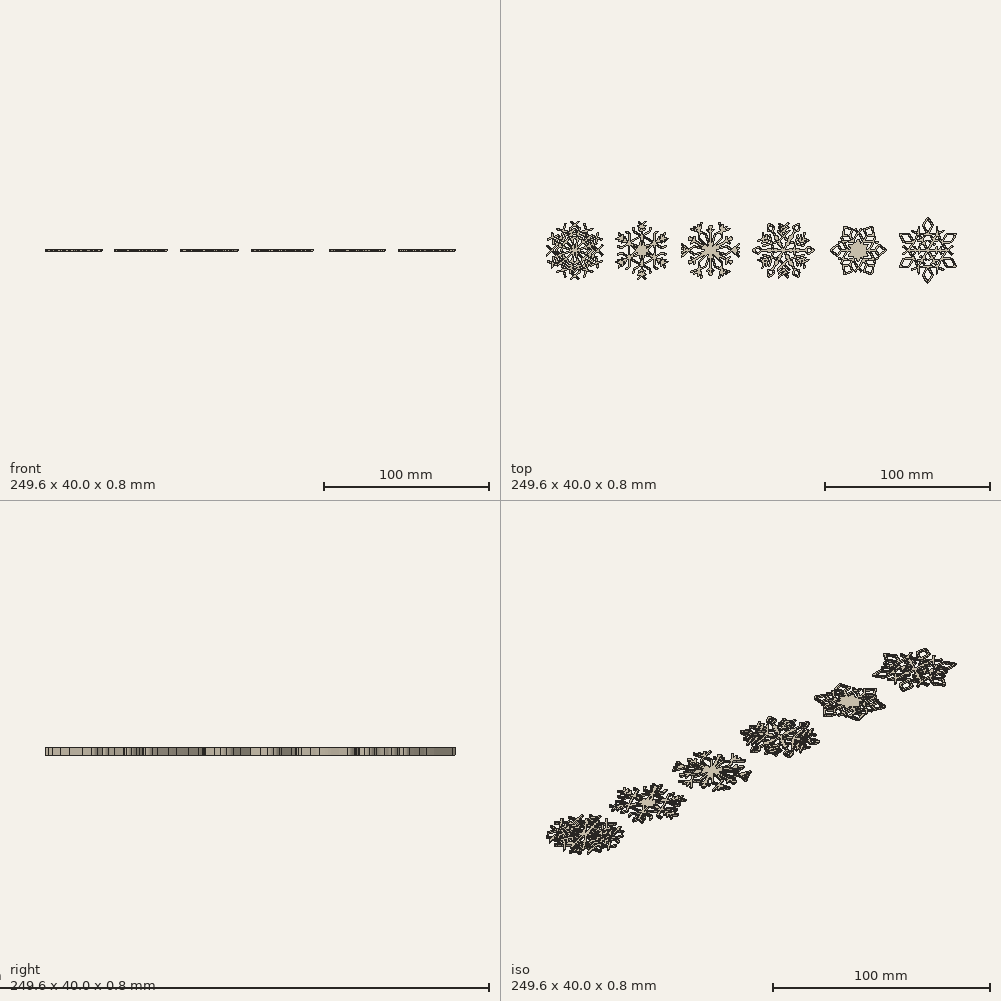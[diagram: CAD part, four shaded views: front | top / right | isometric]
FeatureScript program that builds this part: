
annotation { "Feature Type Name" : "Feature", "Feature Type Description" : "" }
export const myFeature = defineFeature(function(context is Context, id is Id, definition is map)
    precondition{}
    {
        {
            var Q0;
            Q0=qCreatedBy(makeId("Top.planeOp"),FACE);
            var sketch = newSketch(context, id + "F0", { "sketchPlane" : qUnion([Q0])});
            skFitSpline(sketch, "E0", {"points": [v(8.88, -6.2) * mm, v(8.55, -6.04) * mm, v(8.27, -5.88) * mm, v(7.95, -5.8) * mm]});
            skFitSpline(sketch, "E1", {"points": [v(7.95, -5.8) * mm, v(7.92, -6.14) * mm, v(7.88, -6.46) * mm, v(7.85, -6.78) * mm]});
            skFitSpline(sketch, "E2", {"points": [v(7.85, -6.78) * mm, v(8.16, -6.92) * mm, v(8.46, -7.06) * mm, v(8.79, -7.2) * mm]});
            skFitSpline(sketch, "E3", {"points": [v(8.79, -7.2) * mm, v(8.82, -6.86) * mm, v(8.85, -6.53) * mm, v(8.88, -6.2) * mm]});
            skFitSpline(sketch, "E4", {"points": [v(20.42, 12.96) * mm, v(20.13, 13.17) * mm, v(19.86, 13.36) * mm, v(19.6, 13.55) * mm]});
            skFitSpline(sketch, "E5", {"points": [v(19.6, 13.55) * mm, v(19.32, 13.36) * mm, v(19.06, 13.17) * mm, v(18.77, 12.96) * mm]});
            skFitSpline(sketch, "E6", {"points": [v(18.77, 12.96) * mm, v(19.05, 12.76) * mm, v(19.32, 12.56) * mm, v(19.6, 12.36) * mm]});
            skFitSpline(sketch, "E7", {"points": [v(19.6, 12.36) * mm, v(19.88, 12.57) * mm, v(20.14, 12.76) * mm, v(20.42, 12.96) * mm]});
            skFitSpline(sketch, "E8", {"points": [v(7.85, 6.77) * mm, v(7.88, 6.44) * mm, v(7.92, 6.12) * mm, v(7.96, 5.76) * mm]});
            skFitSpline(sketch, "E9", {"points": [v(7.96, 5.76) * mm, v(8.27, 5.9) * mm, v(8.57, 6.04) * mm, v(8.87, 6.17) * mm]});
            skFitSpline(sketch, "E10", {"points": [v(8.87, 6.17) * mm, v(8.87, 6.53) * mm, v(8.83, 6.86) * mm, v(8.77, 7.19) * mm]});
            skFitSpline(sketch, "E11", {"points": [v(8.77, 7.19) * mm, v(8.45, 7.04) * mm, v(8.16, 6.91) * mm, v(7.85, 6.77) * mm]});
            skFitSpline(sketch, "E12", {"points": [v(30.4, 7.2) * mm, v(30.37, 6.85) * mm, v(30.34, 6.52) * mm, v(30.3, 6.18) * mm]});
            skFitSpline(sketch, "E13", {"points": [v(30.3, 6.18) * mm, v(30.62, 6.04) * mm, v(30.92, 5.9) * mm, v(31.24, 5.76) * mm]});
            skFitSpline(sketch, "E14", {"points": [v(31.24, 5.76) * mm, v(31.27, 6.12) * mm, v(31.3, 6.45) * mm, v(31.33, 6.78) * mm]});
            skFitSpline(sketch, "E15", {"points": [v(31.33, 6.78) * mm, v(31.02, 6.92) * mm, v(30.73, 7.05) * mm, v(30.4, 7.2) * mm]});
            skFitSpline(sketch, "E16", {"points": [v(19.6, -13.56) * mm, v(19.88, -13.36) * mm, v(20.14, -13.17) * mm, v(20.42, -12.97) * mm]});
            skFitSpline(sketch, "E17", {"points": [v(20.42, -12.97) * mm, v(20.14, -12.77) * mm, v(19.87, -12.57) * mm, v(19.6, -12.37) * mm]});
            skFitSpline(sketch, "E18", {"points": [v(19.6, -12.37) * mm, v(19.3, -12.58) * mm, v(19.04, -12.77) * mm, v(18.77, -12.97) * mm]});
            skFitSpline(sketch, "E19", {"points": [v(18.77, -12.97) * mm, v(19.05, -13.17) * mm, v(19.32, -13.36) * mm, v(19.6, -13.56) * mm]});
            skFitSpline(sketch, "E20", {"points": [v(30.3, -6.19) * mm, v(30.34, -6.53) * mm, v(30.37, -6.86) * mm, v(30.4, -7.2) * mm]});
            skFitSpline(sketch, "E21", {"points": [v(30.4, -7.2) * mm, v(30.72, -7.06) * mm, v(31.03, -6.92) * mm, v(31.33, -6.78) * mm]});
            skFitSpline(sketch, "E22", {"points": [v(31.33, -6.78) * mm, v(31.3, -6.44) * mm, v(31.27, -6.12) * mm, v(31.24, -5.77) * mm]});
            skFitSpline(sketch, "E23", {"points": [v(31.24, -5.77) * mm, v(30.92, -5.91) * mm, v(30.62, -6.05) * mm, v(30.3, -6.19) * mm]});
            skFitSpline(sketch, "E24", {"points": [v(20.74, 10.31) * mm, v(20.41, 10.61) * mm, v(19.97, 10.81) * mm, v(19.6, 11.12) * mm]});
            skFitSpline(sketch, "E25", {"points": [v(19.6, 11.12) * mm, v(19.21, 10.8) * mm, v(18.76, 10.62) * mm, v(18.4, 10.26) * mm]});
            skFitSpline(sketch, "E26", {"points": [v(18.4, 10.26) * mm, v(18.8, 9.87) * mm, v(19.2, 9.49) * mm, v(19.61, 9.08) * mm]});
            skFitSpline(sketch, "E27", {"points": [v(19.61, 9.08) * mm, v(20, 9.5) * mm, v(20.36, 9.9) * mm, v(20.74, 10.31) * mm]});
            skFitSpline(sketch, "E28", {"points": [v(20.78, -10.27) * mm, v(20.38, -9.88) * mm, v(20, -9.48) * mm, v(19.56, -9.1) * mm]});
            skFitSpline(sketch, "E29", {"points": [v(19.56, -9.1) * mm, v(19.18, -9.5) * mm, v(18.82, -9.9) * mm, v(18.44, -10.32) * mm]});
            skFitSpline(sketch, "E30", {"points": [v(18.44, -10.32) * mm, v(18.77, -10.62) * mm, v(19.22, -10.82) * mm, v(19.6, -11.13) * mm]});
            skFitSpline(sketch, "E31", {"points": [v(19.6, -11.13) * mm, v(19.97, -10.8) * mm, v(20.43, -10.63) * mm, v(20.78, -10.27) * mm]});
            skFitSpline(sketch, "E32", {"points": [v(11.69, -4.55) * mm, v(11.17, -4.4) * mm, v(10.64, -4.26) * mm, v(10.1, -4.11) * mm]});
            skFitSpline(sketch, "E33", {"points": [v(10.1, -4.11) * mm, v(9.96, -4.61) * mm, v(10.04, -5.1) * mm, v(9.96, -5.57) * mm]});
            skFitSpline(sketch, "E34", {"points": [v(9.96, -5.57) * mm, v(10.43, -5.74) * mm, v(10.81, -6.04) * mm, v(11.3, -6.17) * mm]});
            skFitSpline(sketch, "E35", {"points": [v(11.3, -6.17) * mm, v(11.43, -5.64) * mm, v(11.56, -5.14) * mm, v(11.69, -4.64) * mm]});
            skFitSpline(sketch, "E36", {"points": [v(11.69, -4.64) * mm, v(11.7, -4.62) * mm, v(11.69, -4.6) * mm, v(11.69, -4.55) * mm]});
            skFitSpline(sketch, "E37", {"points": [v(27.9, -6.2) * mm, v(28.36, -5.98) * mm, v(28.78, -5.77) * mm, v(29.22, -5.56) * mm]});
            skFitSpline(sketch, "E38", {"points": [v(29.22, -5.56) * mm, v(29.16, -5.09) * mm, v(29.2, -4.6) * mm, v(29.08, -4.11) * mm]});
            skFitSpline(sketch, "E39", {"points": [v(29.08, -4.11) * mm, v(28.53, -4.26) * mm, v(28.01, -4.4) * mm, v(27.47, -4.55) * mm]});
            skFitSpline(sketch, "E40", {"points": [v(27.47, -4.55) * mm, v(27.61, -5.1) * mm, v(27.75, -5.62) * mm, v(27.9, -6.2) * mm]});
            skFitSpline(sketch, "E41", {"points": [v(27.47, 4.55) * mm, v(28.01, 4.4) * mm, v(28.54, 4.25) * mm, v(29.09, 4.1) * mm]});
            skFitSpline(sketch, "E42", {"points": [v(29.09, 4.1) * mm, v(29.2, 4.6) * mm, v(29.17, 5.09) * mm, v(29.21, 5.55) * mm]});
            skFitSpline(sketch, "E43", {"points": [v(29.21, 5.55) * mm, v(28.98, 5.67) * mm, v(28.77, 5.77) * mm, v(28.56, 5.87) * mm]});
            skFitSpline(sketch, "E44", {"points": [v(28.56, 5.87) * mm, v(28.35, 5.98) * mm, v(28.15, 6.11) * mm, v(27.9, 6.15) * mm]});
            skFitSpline(sketch, "E45", {"points": [v(27.9, 6.15) * mm, v(27.75, 5.62) * mm, v(27.62, 5.1) * mm, v(27.47, 4.55) * mm]});
            skFitSpline(sketch, "E46", {"points": [v(9.96, 5.54) * mm, v(10.05, 5.08) * mm, v(9.95, 4.58) * mm, v(10.12, 4.1) * mm]});
            skFitSpline(sketch, "E47", {"points": [v(10.12, 4.1) * mm, v(10.66, 4.25) * mm, v(11.18, 4.4) * mm, v(11.72, 4.55) * mm]});
            skFitSpline(sketch, "E48", {"points": [v(11.72, 4.55) * mm, v(11.57, 5.1) * mm, v(11.43, 5.63) * mm, v(11.3, 6.16) * mm]});
            skFitSpline(sketch, "E49", {"points": [v(11.3, 6.16) * mm, v(11.18, 6.12) * mm, v(11.09, 6.1) * mm, v(11.01, 6.07) * mm]});
            skFitSpline(sketch, "E50", {"points": [v(11.01, 6.07) * mm, v(10.67, 5.9) * mm, v(10.33, 5.72) * mm, v(9.96, 5.54) * mm]});
            skFitSpline(sketch, "E51", {"points": [v(37.3, 0) * mm, v(36.53, 0.5) * mm, v(35.83, 1.07) * mm, v(34.95, 1.36) * mm]});
            skFitSpline(sketch, "E52", {"points": [v(34.95, 1.36) * mm, v(34.4, 1) * mm, v(34.06, 0.44) * mm, v(33.57, 0) * mm]});
            skFitSpline(sketch, "E53", {"points": [v(33.57, 0) * mm, v(34.06, -0.45) * mm, v(34.4, -1.02) * mm, v(34.96, -1.36) * mm]});
            skFitSpline(sketch, "E54", {"points": [v(34.96, -1.36) * mm, v(35.83, -1.07) * mm, v(36.53, -0.5) * mm, v(37.3, 0) * mm]});
            skFitSpline(sketch, "E55", {"points": [v(5.62, 0) * mm, v(5.12, 0.45) * mm, v(4.78, 1) * mm, v(4.23, 1.36) * mm]});
            skFitSpline(sketch, "E56", {"points": [v(4.23, 1.36) * mm, v(3.36, 1.06) * mm, v(2.66, 0.5) * mm, v(1.89, 0) * mm]});
            skFitSpline(sketch, "E57", {"points": [v(1.89, 0) * mm, v(2.67, -0.5) * mm, v(3.37, -1.08) * mm, v(4.24, -1.36) * mm]});
            skFitSpline(sketch, "E58", {"points": [v(4.24, -1.36) * mm, v(4.78, -1) * mm, v(5.13, -0.45) * mm, v(5.62, 0) * mm]});
            skFitSpline(sketch, "E59", {"points": [v(26.58, -12.11) * mm, v(26.44, -12.75) * mm, v(26.13, -13.33) * mm, v(26.1, -13.99) * mm]});
            skFitSpline(sketch, "E60", {"points": [v(26.1, -13.99) * mm, v(26.78, -14.6) * mm, v(27.62, -14.92) * mm, v(28.45, -15.34) * mm]});
            skFitSpline(sketch, "E61", {"points": [v(28.45, -15.34) * mm, v(28.5, -14.4) * mm, v(28.64, -13.52) * mm, v(28.45, -12.63) * mm]});
            skFitSpline(sketch, "E62", {"points": [v(28.45, -12.63) * mm, v(27.87, -12.33) * mm, v(27.2, -12.3) * mm, v(26.58, -12.11) * mm]});
            skFitSpline(sketch, "E63", {"points": [v(12.58, 12.12) * mm, v(12.75, 12.4) * mm, v(13.1, 13.71) * mm, v(13.07, 14) * mm]});
            skFitSpline(sketch, "E64", {"points": [v(13.07, 14) * mm, v(12.39, 14.6) * mm, v(11.56, 14.92) * mm, v(10.73, 15.33) * mm]});
            skFitSpline(sketch, "E65", {"points": [v(10.73, 15.33) * mm, v(10.7, 14.4) * mm, v(10.53, 13.5) * mm, v(10.75, 12.58) * mm]});
            skFitSpline(sketch, "E66", {"points": [v(10.75, 12.58) * mm, v(11.04, 12.5) * mm, v(11.34, 12.4) * mm, v(11.64, 12.33) * mm]});
            skFitSpline(sketch, "E67", {"points": [v(11.64, 12.33) * mm, v(11.95, 12.25) * mm, v(12.26, 12.2) * mm, v(12.58, 12.12) * mm]});
            skFitSpline(sketch, "E68", {"points": [v(13.1, -13.98) * mm, v(13.05, -13.33) * mm, v(12.75, -12.74) * mm, v(12.6, -12.1) * mm]});
            skFitSpline(sketch, "E69", {"points": [v(12.6, -12.1) * mm, v(11.97, -12.31) * mm, v(11.32, -12.33) * mm, v(10.73, -12.63) * mm]});
            skFitSpline(sketch, "E70", {"points": [v(10.73, -12.63) * mm, v(10.54, -13.52) * mm, v(10.7, -14.4) * mm, v(10.73, -15.34) * mm]});
            skFitSpline(sketch, "E71", {"points": [v(10.73, -15.34) * mm, v(11.56, -14.92) * mm, v(12.4, -14.6) * mm, v(13.1, -13.98) * mm]});
            skFitSpline(sketch, "E72", {"points": [v(26.58, 12.11) * mm, v(27.78, 12.36) * mm, v(28.2, 12.48) * mm, v(28.48, 12.65) * mm]});
            skFitSpline(sketch, "E73", {"points": [v(28.48, 12.65) * mm, v(28.5, 12.94) * mm, v(28.53, 13.24) * mm, v(28.54, 13.55) * mm]});
            skFitSpline(sketch, "E74", {"points": [v(28.54, 13.55) * mm, v(28.55, 13.84) * mm, v(28.55, 14.13) * mm, v(28.52, 14.42) * mm]});
            skFitSpline(sketch, "E75", {"points": [v(28.52, 14.42) * mm, v(28.48, 14.71) * mm, v(28.51, 15.02) * mm, v(28.43, 15.32) * mm]});
            skFitSpline(sketch, "E76", {"points": [v(28.43, 15.32) * mm, v(27.6, 14.9) * mm, v(26.77, 14.58) * mm, v(26.1, 13.97) * mm]});
            skFitSpline(sketch, "E77", {"points": [v(26.1, 13.97) * mm, v(26.13, 13.32) * mm, v(26.44, 12.74) * mm, v(26.58, 12.11) * mm]});
            skFitSpline(sketch, "E78", {"points": [v(22.07, -5.29) * mm, v(22.06, -5.27) * mm, v(22.05, -5.25) * mm, v(22.03, -5.24) * mm]});
            skFitSpline(sketch, "E79", {"points": [v(22.03, -5.24) * mm, v(21.97, -5.24) * mm, v(21.9, -5.24) * mm, v(21.85, -5.23) * mm]});
            skFitSpline(sketch, "E80", {"points": [v(21.85, -5.23) * mm, v(21.62, -5.22) * mm, v(21.41, -5.13) * mm, v(21.25, -4.97) * mm]});
            skFitSpline(sketch, "E81", {"points": [v(21.25, -4.97) * mm, v(21.15, -4.88) * mm, v(21.06, -4.78) * mm, v(20.97, -4.68) * mm]});
            skFitSpline(sketch, "E82", {"points": [v(20.97, -4.68) * mm, v(20.65, -4.33) * mm, v(20.52, -3.94) * mm, v(20.72, -3.49) * mm]});
            skFitSpline(sketch, "E83", {"points": [v(20.72, -3.49) * mm, v(20.76, -3.4) * mm, v(20.82, -3.3) * mm, v(20.86, -3.23) * mm]});
            skFitSpline(sketch, "E84", {"points": [v(20.86, -3.23) * mm, v(20.44, -2.49) * mm, v(20.03, -1.76) * mm, v(19.6, -1) * mm]});
            skFitSpline(sketch, "E85", {"points": [v(19.6, -1) * mm, v(19.15, -1.77) * mm, v(18.74, -2.5) * mm, v(18.33, -3.24) * mm]});
            skFitSpline(sketch, "E86", {"points": [v(18.33, -3.24) * mm, v(18.72, -3.84) * mm, v(18.57, -4.35) * mm, v(18.14, -4.75) * mm]});
            skFitSpline(sketch, "E87", {"points": [v(18.14, -4.75) * mm, v(18.1, -4.78) * mm, v(18.07, -4.81) * mm, v(18.04, -4.85) * mm]});
            skFitSpline(sketch, "E88", {"points": [v(18.04, -4.85) * mm, v(17.84, -5.13) * mm, v(17.57, -5.24) * mm, v(17.23, -5.24) * mm]});
            skFitSpline(sketch, "E89", {"points": [v(17.23, -5.24) * mm, v(17.2, -5.24) * mm, v(17.16, -5.27) * mm, v(17.12, -5.29) * mm]});
            skFitSpline(sketch, "E90", {"points": [v(17.12, -5.29) * mm, v(17.27, -5.52) * mm, v(19.42, -7.61) * mm, v(19.62, -7.73) * mm]});
            skFitSpline(sketch, "E91", {"points": [v(19.62, -7.73) * mm, v(19.7, -7.65) * mm, v(19.8, -7.57) * mm, v(19.9, -7.48) * mm]});
            skFitSpline(sketch, "E92", {"points": [v(19.9, -7.48) * mm, v(20.06, -7.32) * mm, v(20.2, -7.14) * mm, v(20.37, -6.98) * mm]});
            skFitSpline(sketch, "E93", {"points": [v(20.37, -6.98) * mm, v(20.9, -6.46) * mm, v(21.44, -5.95) * mm, v(21.97, -5.43) * mm]});
            skFitSpline(sketch, "E94", {"points": [v(21.97, -5.43) * mm, v(22.01, -5.4) * mm, v(22.04, -5.33) * mm, v(22.07, -5.29) * mm]});
            skFitSpline(sketch, "E95", {"points": [v(22.05, 5.26) * mm, v(22.09, 5.33) * mm, v(22.02, 5.38) * mm, v(21.97, 5.43) * mm]});
            skFitSpline(sketch, "E96", {"points": [v(21.97, 5.43) * mm, v(21.55, 5.83) * mm, v(21.13, 6.24) * mm, v(20.72, 6.65) * mm]});
            skFitSpline(sketch, "E97", {"points": [v(20.72, 6.65) * mm, v(20.5, 6.85) * mm, v(20.3, 7.07) * mm, v(20.1, 7.27) * mm]});
            skFitSpline(sketch, "E98", {"points": [v(20.1, 7.27) * mm, v(19.93, 7.43) * mm, v(19.8, 7.61) * mm, v(19.57, 7.72) * mm]});
            skFitSpline(sketch, "E99", {"points": [v(19.57, 7.72) * mm, v(19.48, 7.64) * mm, v(19.38, 7.57) * mm, v(19.3, 7.47) * mm]});
            skFitSpline(sketch, "E100", {"points": [v(19.3, 7.47) * mm, v(18.95, 7.1) * mm, v(18.59, 6.76) * mm, v(18.22, 6.42) * mm]});
            skFitSpline(sketch, "E101", {"points": [v(18.22, 6.42) * mm, v(17.87, 6.1) * mm, v(17.54, 5.75) * mm, v(17.21, 5.42) * mm]});
            skFitSpline(sketch, "E102", {"points": [v(17.21, 5.42) * mm, v(17.18, 5.38) * mm, v(17.16, 5.31) * mm, v(17.14, 5.26) * mm]});
            skFitSpline(sketch, "E103", {"points": [v(17.14, 5.26) * mm, v(17.19, 5.25) * mm, v(17.24, 5.22) * mm, v(17.29, 5.22) * mm]});
            skFitSpline(sketch, "E104", {"points": [v(17.29, 5.22) * mm, v(17.59, 5.22) * mm, v(17.83, 5.11) * mm, v(18.02, 4.88) * mm]});
            skFitSpline(sketch, "E105", {"points": [v(18.02, 4.88) * mm, v(18.06, 4.81) * mm, v(18.13, 4.76) * mm, v(18.18, 4.7) * mm]});
            skFitSpline(sketch, "E106", {"points": [v(18.18, 4.7) * mm, v(18.55, 4.36) * mm, v(18.65, 3.9) * mm, v(18.46, 3.46) * mm]});
            skFitSpline(sketch, "E107", {"points": [v(18.46, 3.46) * mm, v(18.42, 3.38) * mm, v(18.37, 3.3) * mm, v(18.33, 3.22) * mm]});
            skFitSpline(sketch, "E108", {"points": [v(18.33, 3.22) * mm, v(18.75, 2.48) * mm, v(19.16, 1.76) * mm, v(19.6, 0.99) * mm]});
            skFitSpline(sketch, "E109", {"points": [v(19.6, 0.99) * mm, v(20.03, 1.76) * mm, v(20.45, 2.5) * mm, v(20.86, 3.23) * mm]});
            skFitSpline(sketch, "E110", {"points": [v(20.86, 3.23) * mm, v(20.83, 3.29) * mm, v(20.8, 3.33) * mm, v(20.77, 3.38) * mm]});
            skFitSpline(sketch, "E111", {"points": [v(20.77, 3.38) * mm, v(20.68, 3.6) * mm, v(20.59, 3.8) * mm, v(20.64, 4.05) * mm]});
            skFitSpline(sketch, "E112", {"points": [v(20.64, 4.05) * mm, v(20.74, 4.51) * mm, v(21.08, 4.8) * mm, v(21.4, 5.09) * mm]});
            skFitSpline(sketch, "E113", {"points": [v(21.4, 5.09) * mm, v(21.42, 5.1) * mm, v(21.45, 5.11) * mm, v(21.47, 5.12) * mm]});
            skFitSpline(sketch, "E114", {"points": [v(21.47, 5.12) * mm, v(21.65, 5.16) * mm, v(21.83, 5.2) * mm, v(22.05, 5.26) * mm]});
            skLineSegment(sketch, "E115", {"start": v(23.02, -0.51) * mm, "end": v(20.46, -0.51) * mm});
            skFitSpline(sketch, "E116", {"points": [v(20.46, -0.51) * mm, v(20.9, -1.27) * mm, v(21.34, -2) * mm, v(21.76, -2.72) * mm]});
            skFitSpline(sketch, "E117", {"points": [v(21.76, -2.72) * mm, v(21.8, -2.72) * mm, v(21.8, -2.72) * mm, v(21.82, -2.72) * mm]});
            skFitSpline(sketch, "E118", {"points": [v(21.82, -2.72) * mm, v(22.47, -2.68) * mm, v(22.86, -3.07) * mm, v(22.97, -3.64) * mm]});
            skFitSpline(sketch, "E119", {"points": [v(22.97, -3.64) * mm, v(22.98, -3.7) * mm, v(23, -3.74) * mm, v(23.02, -3.8) * mm]});
            skFitSpline(sketch, "E120", {"points": [v(23.02, -3.8) * mm, v(23.15, -4.09) * mm, v(23.1, -4.37) * mm, v(22.96, -4.64) * mm]});
            skFitSpline(sketch, "E121", {"points": [v(22.96, -4.64) * mm, v(22.93, -4.68) * mm, v(22.93, -4.72) * mm, v(22.92, -4.77) * mm]});
            skFitSpline(sketch, "E122", {"points": [v(22.92, -4.77) * mm, v(23.15, -4.8) * mm, v(26.04, -4) * mm, v(26.3, -3.84) * mm]});
            skFitSpline(sketch, "E123", {"points": [v(26.3, -3.84) * mm, v(26.27, -3.72) * mm, v(26.25, -3.6) * mm, v(26.22, -3.48) * mm]});
            skFitSpline(sketch, "E124", {"points": [v(26.22, -3.48) * mm, v(26.12, -3.1) * mm, v(26.02, -2.74) * mm, v(25.92, -2.37) * mm]});
            skFitSpline(sketch, "E125", {"points": [v(25.92, -2.37) * mm, v(25.77, -1.8) * mm, v(25.63, -1.24) * mm, v(25.49, -0.68) * mm]});
            skFitSpline(sketch, "E126", {"points": [v(25.49, -0.68) * mm, v(25.47, -0.62) * mm, v(25.44, -0.57) * mm, v(25.43, -0.52) * mm]});
            skFitSpline(sketch, "E127", {"points": [v(25.43, -0.52) * mm, v(25.3, -0.5) * mm, v(25.3, -0.59) * mm, v(25.26, -0.64) * mm]});
            skFitSpline(sketch, "E128", {"points": [v(25.26, -0.64) * mm, v(25.13, -0.86) * mm, v(24.94, -1) * mm, v(24.7, -1.06) * mm]});
            skFitSpline(sketch, "E129", {"points": [v(24.7, -1.06) * mm, v(24.57, -1.1) * mm, v(24.44, -1.13) * mm, v(24.3, -1.16) * mm]});
            skFitSpline(sketch, "E130", {"points": [v(24.3, -1.16) * mm, v(23.86, -1.23) * mm, v(23.46, -1.17) * mm, v(23.18, -0.77) * mm]});
            skFitSpline(sketch, "E131", {"points": [v(23.18, -0.77) * mm, v(23.12, -0.7) * mm, v(23.08, -0.6) * mm, v(23.02, -0.51) * mm]});
            skFitSpline(sketch, "E132", {"points": [v(16.18, 0.5) * mm, v(17.01, 0.54) * mm, v(17.85, 0.44) * mm, v(18.72, 0.52) * mm]});
            skFitSpline(sketch, "E133", {"points": [v(18.72, 0.52) * mm, v(18.28, 1.26) * mm, v(17.86, 1.98) * mm, v(17.43, 2.7) * mm]});
            skFitSpline(sketch, "E134", {"points": [v(17.43, 2.7) * mm, v(17.37, 2.7) * mm, v(17.3, 2.7) * mm, v(17.25, 2.7) * mm]});
            skFitSpline(sketch, "E135", {"points": [v(17.25, 2.7) * mm, v(16.91, 2.73) * mm, v(16.62, 2.84) * mm, v(16.43, 3.13) * mm]});
            skFitSpline(sketch, "E136", {"points": [v(16.43, 3.13) * mm, v(16.22, 3.43) * mm, v(16.14, 3.78) * mm, v(16.1, 4.14) * mm]});
            skFitSpline(sketch, "E137", {"points": [v(16.1, 4.14) * mm, v(16.08, 4.31) * mm, v(16.13, 4.48) * mm, v(16.24, 4.63) * mm]});
            skFitSpline(sketch, "E138", {"points": [v(16.24, 4.63) * mm, v(16.26, 4.66) * mm, v(16.27, 4.7) * mm, v(16.3, 4.78) * mm]});
            skFitSpline(sketch, "E139", {"points": [v(16.3, 4.78) * mm, v(16.2, 4.77) * mm, v(16.13, 4.78) * mm, v(16.07, 4.76) * mm]});
            skFitSpline(sketch, "E140", {"points": [v(16.07, 4.76) * mm, v(15.54, 4.62) * mm, v(15, 4.47) * mm, v(14.48, 4.32) * mm]});
            skFitSpline(sketch, "E141", {"points": [v(14.48, 4.32) * mm, v(14.16, 4.23) * mm, v(13.83, 4.14) * mm, v(13.51, 4.06) * mm]});
            skFitSpline(sketch, "E142", {"points": [v(13.51, 4.06) * mm, v(13.3, 4) * mm, v(13.09, 3.98) * mm, v(12.89, 3.84) * mm]});
            skFitSpline(sketch, "E143", {"points": [v(12.89, 3.84) * mm, v(12.92, 3.72) * mm, v(12.93, 3.6) * mm, v(12.97, 3.47) * mm]});
            skFitSpline(sketch, "E144", {"points": [v(12.97, 3.47) * mm, v(13.03, 3.27) * mm, v(13.1, 3.06) * mm, v(13.16, 2.86) * mm]});
            skFitSpline(sketch, "E145", {"points": [v(13.16, 2.86) * mm, v(13.35, 2.12) * mm, v(13.52, 1.39) * mm, v(13.7, 0.65) * mm]});
            skFitSpline(sketch, "E146", {"points": [v(13.7, 0.65) * mm, v(13.72, 0.6) * mm, v(13.75, 0.55) * mm, v(13.8, 0.46) * mm]});
            skFitSpline(sketch, "E147", {"points": [v(13.8, 0.46) * mm, v(13.85, 0.53) * mm, v(13.89, 0.57) * mm, v(13.91, 0.61) * mm]});
            skFitSpline(sketch, "E148", {"points": [v(13.91, 0.61) * mm, v(14.06, 0.86) * mm, v(14.27, 1.01) * mm, v(14.56, 1.06) * mm]});
            skFitSpline(sketch, "E149", {"points": [v(14.56, 1.06) * mm, v(14.66, 1.08) * mm, v(14.76, 1.12) * mm, v(14.86, 1.14) * mm]});
            skFitSpline(sketch, "E150", {"points": [v(14.86, 1.14) * mm, v(15.31, 1.23) * mm, v(15.72, 1.17) * mm, v(16, 0.76) * mm]});
            skFitSpline(sketch, "E151", {"points": [v(16, 0.76) * mm, v(16.06, 0.69) * mm, v(16.1, 0.6) * mm, v(16.18, 0.5) * mm]});
            skFitSpline(sketch, "E152", {"points": [v(20.46, 0.5) * mm, v(20.82, 0.5) * mm, v(21.14, 0.48) * mm, v(21.46, 0.48) * mm]});
            skFitSpline(sketch, "E153", {"points": [v(21.46, 0.48) * mm, v(21.85, 0.48) * mm, v(22.24, 0.5) * mm, v(22.63, 0.5) * mm]});
            skFitSpline(sketch, "E154", {"points": [v(22.63, 0.5) * mm, v(22.76, 0.5) * mm, v(22.9, 0.5) * mm, v(23.03, 0.5) * mm]});
            skFitSpline(sketch, "E155", {"points": [v(23.03, 0.5) * mm, v(23.05, 0.55) * mm, v(23.06, 0.57) * mm, v(23.08, 0.6) * mm]});
            skFitSpline(sketch, "E156", {"points": [v(23.08, 0.6) * mm, v(23.28, 0.97) * mm, v(23.58, 1.2) * mm, v(24.02, 1.17) * mm]});
            skFitSpline(sketch, "E157", {"points": [v(24.02, 1.17) * mm, v(24.2, 1.16) * mm, v(24.38, 1.1) * mm, v(24.56, 1.08) * mm]});
            skFitSpline(sketch, "E158", {"points": [v(24.56, 1.08) * mm, v(24.9, 1.03) * mm, v(25.14, 0.87) * mm, v(25.3, 0.57) * mm]});
            skFitSpline(sketch, "E159", {"points": [v(25.3, 0.57) * mm, v(25.32, 0.54) * mm, v(25.37, 0.52) * mm, v(25.43, 0.48) * mm]});
            skFitSpline(sketch, "E160", {"points": [v(25.43, 0.48) * mm, v(25.54, 0.88) * mm, v(25.65, 1.25) * mm, v(25.75, 1.62) * mm]});
            skFitSpline(sketch, "E161", {"points": [v(25.75, 1.62) * mm, v(25.9, 2.18) * mm, v(26.04, 2.74) * mm, v(26.18, 3.3) * mm]});
            skFitSpline(sketch, "E162", {"points": [v(26.18, 3.3) * mm, v(26.22, 3.49) * mm, v(26.31, 3.67) * mm, v(26.26, 3.88) * mm]});
            skFitSpline(sketch, "E163", {"points": [v(26.26, 3.88) * mm, v(26.15, 3.92) * mm, v(26.03, 3.97) * mm, v(25.9, 4) * mm]});
            skFitSpline(sketch, "E164", {"points": [v(25.9, 4) * mm, v(25.7, 4.06) * mm, v(25.47, 4.09) * mm, v(25.25, 4.15) * mm]});
            skFitSpline(sketch, "E165", {"points": [v(25.25, 4.15) * mm, v(24.54, 4.35) * mm, v(23.83, 4.56) * mm, v(23.12, 4.76) * mm]});
            skFitSpline(sketch, "E166", {"points": [v(23.12, 4.76) * mm, v(23.06, 4.78) * mm, v(22.99, 4.77) * mm, v(22.93, 4.77) * mm]});
            skFitSpline(sketch, "E167", {"points": [v(22.93, 4.77) * mm, v(22.92, 4.73) * mm, v(22.92, 4.72) * mm, v(22.92, 4.71) * mm]});
            skFitSpline(sketch, "E168", {"points": [v(22.92, 4.71) * mm, v(22.92, 4.7) * mm, v(22.92, 4.68) * mm, v(22.93, 4.67) * mm]});
            skFitSpline(sketch, "E169", {"points": [v(22.93, 4.67) * mm, v(23.12, 4.37) * mm, v(23.16, 4.06) * mm, v(23, 3.74) * mm]});
            skFitSpline(sketch, "E170", {"points": [v(23, 3.74) * mm, v(22.98, 3.7) * mm, v(22.98, 3.63) * mm, v(22.97, 3.58) * mm]});
            skFitSpline(sketch, "E171", {"points": [v(22.97, 3.58) * mm, v(22.85, 3.17) * mm, v(22.64, 2.83) * mm, v(22.18, 2.75) * mm]});
            skFitSpline(sketch, "E172", {"points": [v(22.18, 2.75) * mm, v(22.04, 2.72) * mm, v(21.9, 2.7) * mm, v(21.75, 2.7) * mm]});
            skFitSpline(sketch, "E173", {"points": [v(21.75, 2.7) * mm, v(21.33, 1.98) * mm, v(20.9, 1.26) * mm, v(20.46, 0.5) * mm]});
            skLineSegment(sketch, "E174", {"start": v(18.73, -0.5) * mm, "end": v(16.17, -0.5) * mm});
            skFitSpline(sketch, "E175", {"points": [v(16.17, -0.5) * mm, v(16.14, -0.55) * mm, v(16.13, -0.58) * mm, v(16.1, -0.61) * mm]});
            skFitSpline(sketch, "E176", {"points": [v(16.1, -0.61) * mm, v(15.9, -0.98) * mm, v(15.6, -1.21) * mm, v(15.16, -1.18) * mm]});
            skFitSpline(sketch, "E177", {"points": [v(15.16, -1.18) * mm, v(14.98, -1.16) * mm, v(14.79, -1.11) * mm, v(14.6, -1.08) * mm]});
            skFitSpline(sketch, "E178", {"points": [v(14.6, -1.08) * mm, v(14.29, -1.04) * mm, v(14.06, -0.88) * mm, v(13.9, -0.6) * mm]});
            skFitSpline(sketch, "E179", {"points": [v(13.9, -0.6) * mm, v(13.88, -0.56) * mm, v(13.83, -0.53) * mm, v(13.8, -0.49) * mm]});
            skFitSpline(sketch, "E180", {"points": [v(13.8, -0.49) * mm, v(13.66, -0.73) * mm, v(12.92, -3.6) * mm, v(12.91, -3.88) * mm]});
            skFitSpline(sketch, "E181", {"points": [v(12.91, -3.88) * mm, v(13.02, -3.92) * mm, v(13.14, -3.97) * mm, v(13.26, -4) * mm]});
            skFitSpline(sketch, "E182", {"points": [v(13.26, -4) * mm, v(13.47, -4.06) * mm, v(13.68, -4.09) * mm, v(13.89, -4.15) * mm]});
            skFitSpline(sketch, "E183", {"points": [v(13.89, -4.15) * mm, v(14.3, -4.26) * mm, v(14.7, -4.4) * mm, v(15.1, -4.52) * mm]});
            skFitSpline(sketch, "E184", {"points": [v(15.1, -4.52) * mm, v(15.44, -4.62) * mm, v(15.78, -4.7) * mm, v(16.12, -4.78) * mm]});
            skFitSpline(sketch, "E185", {"points": [v(16.12, -4.78) * mm, v(16.19, -4.8) * mm, v(16.25, -4.81) * mm, v(16.28, -4.72) * mm]});
            skFitSpline(sketch, "E186", {"points": [v(16.28, -4.72) * mm, v(16.27, -4.7) * mm, v(16.26, -4.68) * mm, v(16.25, -4.66) * mm]});
            skFitSpline(sketch, "E187", {"points": [v(16.25, -4.66) * mm, v(16.06, -4.4) * mm, v(16.05, -4.1) * mm, v(16.16, -3.8) * mm]});
            skFitSpline(sketch, "E188", {"points": [v(16.16, -3.8) * mm, v(16.18, -3.74) * mm, v(16.2, -3.68) * mm, v(16.2, -3.61) * mm]});
            skFitSpline(sketch, "E189", {"points": [v(16.2, -3.61) * mm, v(16.34, -3.17) * mm, v(16.56, -2.82) * mm, v(17.05, -2.74) * mm]});
            skFitSpline(sketch, "E190", {"points": [v(17.05, -2.74) * mm, v(17.18, -2.72) * mm, v(17.3, -2.72) * mm, v(17.44, -2.7) * mm]});
            skFitSpline(sketch, "E191", {"points": [v(17.44, -2.7) * mm, v(17.86, -2) * mm, v(18.28, -1.27) * mm, v(18.73, -0.5) * mm]});
            skFitSpline(sketch, "E192", {"points": [v(18.75, -14.17) * mm, v(18.52, -13.96) * mm, v(18.22, -13.85) * mm, v(18.14, -13.5) * mm]});
            skFitSpline(sketch, "E193", {"points": [v(18.14, -13.5) * mm, v(17.98, -13.6) * mm, v(17.84, -13.71) * mm, v(17.7, -13.81) * mm]});
            skFitSpline(sketch, "E194", {"points": [v(17.7, -13.81) * mm, v(17.52, -13.95) * mm, v(17.35, -14.09) * mm, v(17.16, -14.21) * mm]});
            skFitSpline(sketch, "E195", {"points": [v(17.16, -14.21) * mm, v(16.97, -14.34) * mm, v(16.74, -14.33) * mm, v(16.58, -14.2) * mm]});
            skFitSpline(sketch, "E196", {"points": [v(16.58, -14.2) * mm, v(16.32, -14.01) * mm, v(16.32, -13.66) * mm, v(16.58, -13.44) * mm]});
            skFitSpline(sketch, "E197", {"points": [v(16.58, -13.44) * mm, v(16.8, -13.26) * mm, v(17.04, -13.1) * mm, v(17.27, -12.92) * mm]});
            skFitSpline(sketch, "E198", {"points": [v(17.27, -12.92) * mm, v(17.52, -12.73) * mm, v(17.77, -12.53) * mm, v(18.02, -12.33) * mm]});
            skFitSpline(sketch, "E199", {"points": [v(18.02, -12.33) * mm, v(18.27, -12.14) * mm, v(18.51, -11.95) * mm, v(18.77, -11.75) * mm]});
            skFitSpline(sketch, "E200", {"points": [v(18.77, -11.75) * mm, v(18.41, -11.5) * mm, v(18.06, -11.25) * mm, v(17.7, -11) * mm]});
            skFitSpline(sketch, "E201", {"points": [v(17.7, -11) * mm, v(17.54, -11.14) * mm, v(17.37, -11.29) * mm, v(17.21, -11.45) * mm]});
            skFitSpline(sketch, "E202", {"points": [v(17.21, -11.45) * mm, v(16.93, -11.73) * mm, v(16.67, -12) * mm, v(16.4, -12.29) * mm]});
            skFitSpline(sketch, "E203", {"points": [v(16.4, -12.29) * mm, v(16.22, -12.47) * mm, v(16, -12.5) * mm, v(15.79, -12.36) * mm]});
            skFitSpline(sketch, "E204", {"points": [v(15.79, -12.36) * mm, v(15.58, -12.23) * mm, v(15.5, -11.96) * mm, v(15.61, -11.73) * mm]});
            skFitSpline(sketch, "E205", {"points": [v(15.61, -11.73) * mm, v(15.68, -11.61) * mm, v(15.76, -11.5) * mm, v(15.86, -11.4) * mm]});
            skFitSpline(sketch, "E206", {"points": [v(15.86, -11.4) * mm, v(16.8, -10.47) * mm, v(17.76, -9.54) * mm, v(18.72, -8.6) * mm]});
            skFitSpline(sketch, "E207", {"points": [v(18.72, -8.6) * mm, v(18.77, -8.55) * mm, v(18.81, -8.5) * mm, v(18.87, -8.43) * mm]});
            skFitSpline(sketch, "E208", {"points": [v(18.87, -8.43) * mm, v(18.12, -7.69) * mm, v(17.37, -6.95) * mm, v(16.6, -6.2) * mm]});
            skFitSpline(sketch, "E209", {"points": [v(16.6, -6.2) * mm, v(16.49, -6.37) * mm, v(16.39, -6.54) * mm, v(16.3, -6.7) * mm]});
            skFitSpline(sketch, "E210", {"points": [v(16.3, -6.7) * mm, v(16.37, -6.84) * mm, v(16.46, -6.97) * mm, v(16.5, -7.11) * mm]});
            skFitSpline(sketch, "E211", {"points": [v(16.5, -7.11) * mm, v(16.6, -7.58) * mm, v(16.5, -8.03) * mm, v(16.26, -8.44) * mm]});
            skFitSpline(sketch, "E212", {"points": [v(16.26, -8.44) * mm, v(16.16, -8.6) * mm, v(16.06, -8.77) * mm, v(15.88, -8.87) * mm]});
            skFitSpline(sketch, "E213", {"points": [v(15.88, -8.87) * mm, v(15.56, -9.04) * mm, v(15.43, -9.05) * mm, v(15.06, -8.95) * mm]});
            skFitSpline(sketch, "E214", {"points": [v(15.06, -8.95) * mm, v(14.98, -9.08) * mm, v(14.9, -9.21) * mm, v(14.82, -9.35) * mm]});
            skFitSpline(sketch, "E215", {"points": [v(14.82, -9.35) * mm, v(14.49, -9.92) * mm, v(14.16, -10.48) * mm, v(13.83, -11.05) * mm]});
            skFitSpline(sketch, "E216", {"points": [v(13.83, -11.05) * mm, v(13.74, -11.2) * mm, v(13.63, -11.36) * mm, v(13.54, -11.51) * mm]});
            skFitSpline(sketch, "E217", {"points": [v(13.54, -11.51) * mm, v(13.49, -11.6) * mm, v(13.5, -11.67) * mm, v(13.52, -11.76) * mm]});
            skFitSpline(sketch, "E218", {"points": [v(13.52, -11.76) * mm, v(13.67, -12.26) * mm, v(13.83, -12.75) * mm, v(13.96, -13.26) * mm]});
            skFitSpline(sketch, "E219", {"points": [v(13.96, -13.26) * mm, v(14.03, -13.56) * mm, v(14.06, -13.87) * mm, v(14.1, -14.18) * mm]});
            skFitSpline(sketch, "E220", {"points": [v(14.1, -14.18) * mm, v(14.12, -14.39) * mm, v(14.02, -14.54) * mm, v(13.85, -14.67) * mm]});
            skFitSpline(sketch, "E221", {"points": [v(13.85, -14.67) * mm, v(13.24, -15.13) * mm, v(12.6, -15.55) * mm, v(11.9, -15.86) * mm]});
            skFitSpline(sketch, "E222", {"points": [v(11.9, -15.86) * mm, v(11.57, -16.01) * mm, v(11.26, -16.18) * mm, v(10.95, -16.33) * mm]});
            skFitSpline(sketch, "E223", {"points": [v(10.95, -16.33) * mm, v(10.71, -16.45) * mm, v(10.53, -16.43) * mm, v(10.33, -16.27) * mm]});
            skFitSpline(sketch, "E224", {"points": [v(10.33, -16.27) * mm, v(10.27, -16.22) * mm, v(10.2, -16.18) * mm, v(10.13, -16.15) * mm]});
            skFitSpline(sketch, "E225", {"points": [v(10.13, -16.15) * mm, v(9.9, -16.07) * mm, v(9.8, -15.92) * mm, v(9.78, -15.7) * mm]});
            skFitSpline(sketch, "E226", {"points": [v(9.78, -15.7) * mm, v(9.75, -15.14) * mm, v(9.72, -14.6) * mm, v(9.68, -14.04) * mm]});
            skFitSpline(sketch, "E227", {"points": [v(9.68, -14.04) * mm, v(9.65, -13.56) * mm, v(9.7, -13.09) * mm, v(9.74, -12.61) * mm]});
            skFitSpline(sketch, "E228", {"points": [v(9.74, -12.61) * mm, v(9.75, -12.5) * mm, v(9.77, -12.4) * mm, v(9.77, -12.3) * mm]});
            skFitSpline(sketch, "E229", {"points": [v(9.77, -12.3) * mm, v(9.79, -12.1) * mm, v(9.88, -11.95) * mm, v(10.05, -11.85) * mm]});
            skFitSpline(sketch, "E230", {"points": [v(10.05, -11.85) * mm, v(10.16, -11.8) * mm, v(10.28, -11.74) * mm, v(10.4, -11.7) * mm]});
            skFitSpline(sketch, "E231", {"points": [v(10.4, -11.7) * mm, v(10.89, -11.5) * mm, v(11.4, -11.38) * mm, v(11.92, -11.28) * mm]});
            skFitSpline(sketch, "E232", {"points": [v(11.92, -11.28) * mm, v(12.11, -11.25) * mm, v(12.3, -11.2) * mm, v(12.5, -11.13) * mm]});
            skFitSpline(sketch, "E233", {"points": [v(12.5, -11.13) * mm, v(12.56, -11.1) * mm, v(12.62, -11.05) * mm, v(12.66, -11) * mm]});
            skFitSpline(sketch, "E234", {"points": [v(12.66, -11) * mm, v(12.76, -10.81) * mm, v(12.86, -10.62) * mm, v(12.96, -10.43) * mm]});
            skFitSpline(sketch, "E235", {"points": [v(12.96, -10.43) * mm, v(13.33, -9.78) * mm, v(13.7, -9.14) * mm, v(14.07, -8.5) * mm]});
            skFitSpline(sketch, "E236", {"points": [v(14.07, -8.5) * mm, v(14.08, -8.47) * mm, v(14.1, -8.44) * mm, v(14.12, -8.4) * mm]});
            skFitSpline(sketch, "E237", {"points": [v(14.12, -8.4) * mm, v(13.78, -8.18) * mm, v(13.75, -7.84) * mm, v(13.8, -7.5) * mm]});
            skFitSpline(sketch, "E238", {"points": [v(13.8, -7.5) * mm, v(13.85, -7.19) * mm, v(14.02, -6.92) * mm, v(14.26, -6.7) * mm]});
            skFitSpline(sketch, "E239", {"points": [v(14.26, -6.7) * mm, v(14.38, -6.58) * mm, v(14.52, -6.47) * mm, v(14.67, -6.37) * mm]});
            skFitSpline(sketch, "E240", {"points": [v(14.67, -6.37) * mm, v(14.9, -6.21) * mm, v(15.16, -6.2) * mm, v(15.43, -6.23) * mm]});
            skFitSpline(sketch, "E241", {"points": [v(15.43, -6.23) * mm, v(15.53, -6.06) * mm, v(15.63, -5.9) * mm, v(15.73, -5.7) * mm]});
            skFitSpline(sketch, "E242", {"points": [v(15.73, -5.7) * mm, v(15.21, -5.56) * mm, v(14.7, -5.4) * mm, v(14.2, -5.26) * mm]});
            skFitSpline(sketch, "E243", {"points": [v(14.2, -5.26) * mm, v(13.69, -5.12) * mm, v(13.18, -4.99) * mm, v(12.67, -4.85) * mm]});
            skFitSpline(sketch, "E244", {"points": [v(12.67, -4.85) * mm, v(12.64, -4.9) * mm, v(12.62, -4.95) * mm, v(12.6, -5) * mm]});
            skFitSpline(sketch, "E245", {"points": [v(12.6, -5) * mm, v(12.37, -5.89) * mm, v(12.13, -6.78) * mm, v(11.9, -7.67) * mm]});
            skFitSpline(sketch, "E246", {"points": [v(11.9, -7.67) * mm, v(11.8, -8.07) * mm, v(11.7, -8.49) * mm, v(11.6, -8.9) * mm]});
            skFitSpline(sketch, "E247", {"points": [v(11.6, -8.9) * mm, v(11.56, -9.03) * mm, v(11.52, -9.18) * mm, v(11.44, -9.3) * mm]});
            skFitSpline(sketch, "E248", {"points": [v(11.44, -9.3) * mm, v(11.24, -9.62) * mm, v(10.77, -9.61) * mm, v(10.6, -9.28) * mm]});
            skFitSpline(sketch, "E249", {"points": [v(10.6, -9.28) * mm, v(10.53, -9.16) * mm, v(10.52, -9.04) * mm, v(10.56, -8.91) * mm]});
            skFitSpline(sketch, "E250", {"points": [v(10.56, -8.91) * mm, v(10.7, -8.39) * mm, v(10.84, -7.87) * mm, v(10.98, -7.34) * mm]});
            skFitSpline(sketch, "E251", {"points": [v(10.98, -7.34) * mm, v(11, -7.27) * mm, v(11, -7.2) * mm, v(11.02, -7.14) * mm]});
            skFitSpline(sketch, "E252", {"points": [v(11.02, -7.14) * mm, v(10.62, -6.96) * mm, v(10.23, -6.78) * mm, v(9.83, -6.59) * mm]});
            skFitSpline(sketch, "E253", {"points": [v(9.83, -6.59) * mm, v(9.8, -6.87) * mm, v(9.78, -7.13) * mm, v(9.73, -7.38) * mm]});
            skFitSpline(sketch, "E254", {"points": [v(9.73, -7.38) * mm, v(9.6, -8) * mm, v(9.57, -8.63) * mm, v(9.48, -9.25) * mm]});
            skFitSpline(sketch, "E255", {"points": [v(9.48, -9.25) * mm, v(9.47, -9.33) * mm, v(9.45, -9.41) * mm, v(9.42, -9.48) * mm]});
            skFitSpline(sketch, "E256", {"points": [v(9.42, -9.48) * mm, v(9.33, -9.68) * mm, v(9.1, -9.8) * mm, v(8.9, -9.76) * mm]});
            skFitSpline(sketch, "E257", {"points": [v(8.9, -9.76) * mm, v(8.68, -9.7) * mm, v(8.51, -9.53) * mm, v(8.52, -9.3) * mm]});
            skFitSpline(sketch, "E258", {"points": [v(8.52, -9.3) * mm, v(8.53, -9.02) * mm, v(8.57, -8.75) * mm, v(8.6, -8.47) * mm]});
            skFitSpline(sketch, "E259", {"points": [v(8.6, -8.47) * mm, v(8.6, -8.33) * mm, v(8.62, -8.18) * mm, v(8.64, -8.01) * mm]});
            skFitSpline(sketch, "E260", {"points": [v(8.64, -8.01) * mm, v(8.3, -8.11) * mm, v(8.05, -7.92) * mm, v(7.75, -7.82) * mm]});
            skFitSpline(sketch, "E261", {"points": [v(7.75, -7.82) * mm, v(7.72, -8.02) * mm, v(7.69, -8.22) * mm, v(7.67, -8.4) * mm]});
            skFitSpline(sketch, "E262", {"points": [v(7.67, -8.4) * mm, v(7.6, -8.99) * mm, v(7.6, -9.57) * mm, v(7.47, -10.14) * mm]});
            skFitSpline(sketch, "E263", {"points": [v(7.47, -10.14) * mm, v(7.43, -10.29) * mm, v(7.4, -10.44) * mm, v(7.36, -10.58) * mm]});
            skFitSpline(sketch, "E264", {"points": [v(7.36, -10.58) * mm, v(7.27, -10.85) * mm, v(7.02, -11.01) * mm, v(6.8, -10.95) * mm]});
            skFitSpline(sketch, "E265", {"points": [v(6.8, -10.95) * mm, v(6.52, -10.88) * mm, v(6.36, -10.63) * mm, v(6.42, -10.34) * mm]});
            skFitSpline(sketch, "E266", {"points": [v(6.42, -10.34) * mm, v(6.48, -9.98) * mm, v(6.56, -9.62) * mm, v(6.62, -9.26) * mm]});
            skFitSpline(sketch, "E267", {"points": [v(6.62, -9.26) * mm, v(6.66, -9.03) * mm, v(6.66, -8.8) * mm, v(6.68, -8.57) * mm]});
            skFitSpline(sketch, "E268", {"points": [v(6.68, -8.57) * mm, v(6.72, -8.18) * mm, v(6.77, -7.78) * mm, v(6.81, -7.38) * mm]});
            skFitSpline(sketch, "E269", {"points": [v(6.81, -7.38) * mm, v(6.52, -7.26) * mm, v(6.23, -7.14) * mm, v(5.95, -7.01) * mm]});
            skFitSpline(sketch, "E270", {"points": [v(5.95, -7.01) * mm, v(5.55, -6.84) * mm, v(5.15, -6.64) * mm, v(4.75, -6.47) * mm]});
            skFitSpline(sketch, "E271", {"points": [v(4.75, -6.47) * mm, v(4.54, -6.39) * mm, v(4.32, -6.33) * mm, v(4.11, -6.26) * mm]});
            skFitSpline(sketch, "E272", {"points": [v(4.11, -6.26) * mm, v(4.04, -6.24) * mm, v(3.96, -6.2) * mm, v(3.9, -6.16) * mm]});
            skFitSpline(sketch, "E273", {"points": [v(3.9, -6.16) * mm, v(3.72, -6.04) * mm, v(3.66, -5.83) * mm, v(3.72, -5.63) * mm]});
            skFitSpline(sketch, "E274", {"points": [v(3.72, -5.63) * mm, v(3.79, -5.42) * mm, v(3.94, -5.3) * mm, v(4.17, -5.31) * mm]});
            skFitSpline(sketch, "E275", {"points": [v(4.17, -5.31) * mm, v(4.36, -5.33) * mm, v(4.56, -5.37) * mm, v(4.74, -5.44) * mm]});
            skFitSpline(sketch, "E276", {"points": [v(4.74, -5.44) * mm, v(5.12, -5.58) * mm, v(5.5, -5.74) * mm, v(5.87, -5.9) * mm]});
            skFitSpline(sketch, "E277", {"points": [v(5.87, -5.9) * mm, v(6.15, -6.02) * mm, v(6.43, -6.15) * mm, v(6.7, -6.28) * mm]});
            skFitSpline(sketch, "E278", {"points": [v(6.7, -6.28) * mm, v(6.77, -6.3) * mm, v(6.83, -6.32) * mm, v(6.9, -6.35) * mm]});
            skFitSpline(sketch, "E279", {"points": [v(6.9, -6.35) * mm, v(6.98, -6.05) * mm, v(6.92, -5.74) * mm, v(7.2, -5.5) * mm]});
            skFitSpline(sketch, "E280", {"points": [v(7.2, -5.5) * mm, v(7, -5.41) * mm, v(6.84, -5.34) * mm, v(6.68, -5.27) * mm]});
            skFitSpline(sketch, "E281", {"points": [v(6.68, -5.27) * mm, v(6.47, -5.18) * mm, v(6.26, -5.1) * mm, v(6.06, -5) * mm]});
            skFitSpline(sketch, "E282", {"points": [v(6.06, -5) * mm, v(5.78, -4.85) * mm, v(5.7, -4.5) * mm, v(5.88, -4.26) * mm]});
            skFitSpline(sketch, "E283", {"points": [v(5.88, -4.26) * mm, v(6.02, -4.08) * mm, v(6.25, -4.03) * mm, v(6.51, -4.13) * mm]});
            skFitSpline(sketch, "E284", {"points": [v(6.51, -4.13) * mm, v(6.84, -4.26) * mm, v(7.16, -4.4) * mm, v(7.48, -4.54) * mm]});
            skFitSpline(sketch, "E285", {"points": [v(7.48, -4.54) * mm, v(7.62, -4.6) * mm, v(7.76, -4.67) * mm, v(7.9, -4.72) * mm]});
            skFitSpline(sketch, "E286", {"points": [v(7.9, -4.72) * mm, v(8.27, -4.87) * mm, v(8.64, -5) * mm, v(9.02, -5.15) * mm]});
            skFitSpline(sketch, "E287", {"points": [v(9.02, -5.15) * mm, v(9.05, -4.72) * mm, v(9.09, -4.3) * mm, v(9.12, -3.86) * mm]});
            skFitSpline(sketch, "E288", {"points": [v(9.12, -3.86) * mm, v(8.95, -3.8) * mm, v(8.76, -3.74) * mm, v(8.57, -3.68) * mm]});
            skFitSpline(sketch, "E289", {"points": [v(8.57, -3.68) * mm, v(8.25, -3.59) * mm, v(7.93, -3.5) * mm, v(7.6, -3.41) * mm]});
            skFitSpline(sketch, "E290", {"points": [v(7.6, -3.41) * mm, v(7.54, -3.4) * mm, v(7.46, -3.4) * mm, v(7.4, -3.38) * mm]});
            skFitSpline(sketch, "E291", {"points": [v(7.4, -3.38) * mm, v(7.15, -3.34) * mm, v(6.98, -3.13) * mm, v(6.98, -2.9) * mm]});
            skFitSpline(sketch, "E292", {"points": [v(6.98, -2.9) * mm, v(7, -2.65) * mm, v(7.19, -2.45) * mm, v(7.44, -2.43) * mm]});
            skFitSpline(sketch, "E293", {"points": [v(7.44, -2.43) * mm, v(7.71, -2.4) * mm, v(7.96, -2.5) * mm, v(8.21, -2.57) * mm]});
            skFitSpline(sketch, "E294", {"points": [v(8.21, -2.57) * mm, v(9.26, -2.86) * mm, v(10.3, -3.15) * mm, v(11.35, -3.44) * mm]});
            skFitSpline(sketch, "E295", {"points": [v(11.35, -3.44) * mm, v(11.54, -3.49) * mm, v(11.73, -3.54) * mm, v(11.94, -3.6) * mm]});
            skFitSpline(sketch, "E296", {"points": [v(11.94, -3.6) * mm, v(12.2, -2.56) * mm, v(12.47, -1.54) * mm, v(12.73, -0.5) * mm]});
            skLineSegment(sketch, "E297", {"start": v(12.73, -0.5) * mm, "end": v(12.1, -0.5) * mm});
            skFitSpline(sketch, "E298", {"points": [v(12.1, -0.5) * mm, v(12, -0.85) * mm, v(11.75, -1.04) * mm, v(11.44, -1.17) * mm]});
            skFitSpline(sketch, "E299", {"points": [v(11.44, -1.17) * mm, v(11.09, -1.32) * mm, v(10.73, -1.37) * mm, v(10.36, -1.32) * mm]});
            skFitSpline(sketch, "E300", {"points": [v(10.36, -1.32) * mm, v(10.05, -1.29) * mm, v(9.7, -1) * mm, v(9.62, -0.7) * mm]});
            skFitSpline(sketch, "E301", {"points": [v(9.62, -0.7) * mm, v(9.6, -0.65) * mm, v(9.59, -0.6) * mm, v(9.56, -0.54) * mm]});
            skFitSpline(sketch, "E302", {"points": [v(9.56, -0.54) * mm, v(9.4, -0.54) * mm, v(9.22, -0.54) * mm, v(9.04, -0.54) * mm]});
            skFitSpline(sketch, "E303", {"points": [v(9.04, -0.54) * mm, v(8.32, -0.53) * mm, v(7.6, -0.52) * mm, v(6.89, -0.5) * mm]});
            skFitSpline(sketch, "E304", {"points": [v(6.89, -0.5) * mm, v(6.8, -0.5) * mm, v(6.7, -0.5) * mm, v(6.6, -0.51) * mm]});
            skFitSpline(sketch, "E305", {"points": [v(6.6, -0.51) * mm, v(6.53, -0.52) * mm, v(6.45, -0.56) * mm, v(6.4, -0.6) * mm]});
            skFitSpline(sketch, "E306", {"points": [v(6.4, -0.6) * mm, v(6.12, -0.89) * mm, v(5.87, -1.18) * mm, v(5.59, -1.46) * mm]});
            skFitSpline(sketch, "E307", {"points": [v(5.59, -1.46) * mm, v(5.32, -1.73) * mm, v(5.03, -1.99) * mm, v(4.74, -2.23) * mm]});
            skFitSpline(sketch, "E308", {"points": [v(4.74, -2.23) * mm, v(4.5, -2.43) * mm, v(4.25, -2.47) * mm, v(3.94, -2.33) * mm]});
            skFitSpline(sketch, "E309", {"points": [v(3.94, -2.33) * mm, v(3.2, -2) * mm, v(2.5, -1.63) * mm, v(1.86, -1.16) * mm]});
            skFitSpline(sketch, "E310", {"points": [v(1.86, -1.16) * mm, v(1.63, -1) * mm, v(1.4, -0.85) * mm, v(1.16, -0.7) * mm]});
            skFitSpline(sketch, "E311", {"points": [v(1.16, -0.7) * mm, v(0.9, -0.54) * mm, v(0.84, -0.38) * mm, v(0.88, -0.1) * mm]});
            skFitSpline(sketch, "E312", {"points": [v(0.88, -0.1) * mm, v(0.9, -0.02) * mm, v(0.89, 0.06) * mm, v(0.87, 0.13) * mm]});
            skFitSpline(sketch, "E313", {"points": [v(0.87, 0.13) * mm, v(0.83, 0.34) * mm, v(0.9, 0.51) * mm, v(1.06, 0.62) * mm]});
            skFitSpline(sketch, "E314", {"points": [v(1.06, 0.62) * mm, v(1.66, 1.02) * mm, v(2.27, 1.43) * mm, v(2.89, 1.8) * mm]});
            skFitSpline(sketch, "E315", {"points": [v(2.89, 1.8) * mm, v(3.22, 2) * mm, v(3.6, 2.14) * mm, v(3.94, 2.32) * mm]});
            skFitSpline(sketch, "E316", {"points": [v(3.94, 2.32) * mm, v(4.26, 2.49) * mm, v(4.53, 2.41) * mm, v(4.78, 2.2) * mm]});
            skFitSpline(sketch, "E317", {"points": [v(4.78, 2.2) * mm, v(5.14, 1.9) * mm, v(5.5, 1.59) * mm, v(5.8, 1.22) * mm]});
            skFitSpline(sketch, "E318", {"points": [v(5.8, 1.22) * mm, v(5.99, 1) * mm, v(6.2, 0.79) * mm, v(6.41, 0.58) * mm]});
            skFitSpline(sketch, "E319", {"points": [v(6.41, 0.58) * mm, v(6.46, 0.54) * mm, v(6.53, 0.5) * mm, v(6.6, 0.5) * mm]});
            skFitSpline(sketch, "E320", {"points": [v(6.6, 0.5) * mm, v(6.77, 0.5) * mm, v(6.95, 0.52) * mm, v(7.12, 0.52) * mm]});
            skFitSpline(sketch, "E321", {"points": [v(7.12, 0.52) * mm, v(7.64, 0.53) * mm, v(8.16, 0.54) * mm, v(8.68, 0.55) * mm]});
            skFitSpline(sketch, "E322", {"points": [v(8.68, 0.55) * mm, v(8.9, 0.55) * mm, v(9.13, 0.53) * mm, v(9.35, 0.52) * mm]});
            skFitSpline(sketch, "E323", {"points": [v(9.35, 0.52) * mm, v(9.42, 0.52) * mm, v(9.5, 0.53) * mm, v(9.56, 0.53) * mm]});
            skFitSpline(sketch, "E324", {"points": [v(9.56, 0.53) * mm, v(9.58, 0.57) * mm, v(9.6, 0.6) * mm, v(9.6, 0.63) * mm]});
            skFitSpline(sketch, "E325", {"points": [v(9.6, 0.63) * mm, v(9.73, 1.06) * mm, v(10.04, 1.28) * mm, v(10.5, 1.32) * mm]});
            skFitSpline(sketch, "E326", {"points": [v(10.5, 1.32) * mm, v(10.9, 1.36) * mm, v(11.25, 1.25) * mm, v(11.6, 1.09) * mm]});
            skFitSpline(sketch, "E327", {"points": [v(11.6, 1.09) * mm, v(11.85, 0.97) * mm, v(12.03, 0.78) * mm, v(12.1, 0.5) * mm]});
            skLineSegment(sketch, "E328", {"start": v(12.1, 0.5) * mm, "end": v(12.73, 0.5) * mm});
            skFitSpline(sketch, "E329", {"points": [v(12.73, 0.5) * mm, v(12.47, 1.52) * mm, v(12.2, 2.54) * mm, v(11.94, 3.58) * mm]});
            skFitSpline(sketch, "E330", {"points": [v(11.94, 3.58) * mm, v(11.87, 3.57) * mm, v(11.8, 3.56) * mm, v(11.73, 3.54) * mm]});
            skFitSpline(sketch, "E331", {"points": [v(11.73, 3.54) * mm, v(10.67, 3.25) * mm, v(9.6, 2.95) * mm, v(8.55, 2.66) * mm]});
            skFitSpline(sketch, "E332", {"points": [v(8.55, 2.66) * mm, v(8.3, 2.6) * mm, v(8.07, 2.51) * mm, v(7.83, 2.46) * mm]});
            skFitSpline(sketch, "E333", {"points": [v(7.83, 2.46) * mm, v(7.7, 2.43) * mm, v(7.55, 2.4) * mm, v(7.41, 2.42) * mm]});
            skFitSpline(sketch, "E334", {"points": [v(7.41, 2.42) * mm, v(7.15, 2.45) * mm, v(6.97, 2.67) * mm, v(6.98, 2.92) * mm]});
            skFitSpline(sketch, "E335", {"points": [v(6.98, 2.92) * mm, v(7, 3.16) * mm, v(7.18, 3.34) * mm, v(7.45, 3.38) * mm]});
            skFitSpline(sketch, "E336", {"points": [v(7.45, 3.38) * mm, v(7.59, 3.4) * mm, v(7.73, 3.44) * mm, v(7.86, 3.48) * mm]});
            skFitSpline(sketch, "E337", {"points": [v(7.86, 3.48) * mm, v(8.28, 3.6) * mm, v(8.7, 3.72) * mm, v(9.12, 3.84) * mm]});
            skFitSpline(sketch, "E338", {"points": [v(9.12, 3.84) * mm, v(9.09, 4.28) * mm, v(9.06, 4.7) * mm, v(9.02, 5.15) * mm]});
            skFitSpline(sketch, "E339", {"points": [v(9.02, 5.15) * mm, v(8.97, 5.13) * mm, v(8.92, 5.12) * mm, v(8.87, 5.1) * mm]});
            skFitSpline(sketch, "E340", {"points": [v(8.87, 5.1) * mm, v(8.56, 4.98) * mm, v(8.25, 4.86) * mm, v(7.94, 4.73) * mm]});
            skFitSpline(sketch, "E341", {"points": [v(7.94, 4.73) * mm, v(7.47, 4.53) * mm, v(7, 4.33) * mm, v(6.53, 4.13) * mm]});
            skFitSpline(sketch, "E342", {"points": [v(6.53, 4.13) * mm, v(6.41, 4.08) * mm, v(6.3, 4.03) * mm, v(6.16, 4.07) * mm]});
            skFitSpline(sketch, "E343", {"points": [v(6.16, 4.07) * mm, v(5.96, 4.13) * mm, v(5.8, 4.3) * mm, v(5.79, 4.5) * mm]});
            skFitSpline(sketch, "E344", {"points": [v(5.79, 4.5) * mm, v(5.76, 4.7) * mm, v(5.86, 4.89) * mm, v(6.06, 4.98) * mm]});
            skFitSpline(sketch, "E345", {"points": [v(6.06, 4.98) * mm, v(6.26, 5.08) * mm, v(6.47, 5.17) * mm, v(6.67, 5.26) * mm]});
            skFitSpline(sketch, "E346", {"points": [v(6.67, 5.26) * mm, v(6.84, 5.33) * mm, v(7, 5.4) * mm, v(7.2, 5.49) * mm]});
            skFitSpline(sketch, "E347", {"points": [v(7.2, 5.49) * mm, v(6.92, 5.73) * mm, v(6.97, 6.04) * mm, v(6.91, 6.35) * mm]});
            skFitSpline(sketch, "E348", {"points": [v(6.91, 6.35) * mm, v(6.81, 6.3) * mm, v(6.72, 6.28) * mm, v(6.64, 6.24) * mm]});
            skFitSpline(sketch, "E349", {"points": [v(6.64, 6.24) * mm, v(6.22, 6.05) * mm, v(5.8, 5.84) * mm, v(5.37, 5.67) * mm]});
            skFitSpline(sketch, "E350", {"points": [v(5.37, 5.67) * mm, v(5.04, 5.53) * mm, v(4.68, 5.42) * mm, v(4.34, 5.3) * mm]});
            skFitSpline(sketch, "E351", {"points": [v(4.34, 5.3) * mm, v(4.13, 5.24) * mm, v(3.95, 5.3) * mm, v(3.81, 5.45) * mm]});
            skFitSpline(sketch, "E352", {"points": [v(3.81, 5.45) * mm, v(3.6, 5.69) * mm, v(3.68, 6.06) * mm, v(3.97, 6.2) * mm]});
            skFitSpline(sketch, "E353", {"points": [v(3.97, 6.2) * mm, v(4.07, 6.25) * mm, v(4.18, 6.27) * mm, v(4.29, 6.31) * mm]});
            skFitSpline(sketch, "E354", {"points": [v(4.29, 6.31) * mm, v(4.66, 6.46) * mm, v(5.03, 6.6) * mm, v(5.4, 6.75) * mm]});
            skFitSpline(sketch, "E355", {"points": [v(5.4, 6.75) * mm, v(5.8, 6.91) * mm, v(6.19, 7.1) * mm, v(6.58, 7.27) * mm]});
            skFitSpline(sketch, "E356", {"points": [v(6.58, 7.27) * mm, v(6.65, 7.3) * mm, v(6.73, 7.33) * mm, v(6.81, 7.37) * mm]});
            skFitSpline(sketch, "E357", {"points": [v(6.81, 7.37) * mm, v(6.8, 7.46) * mm, v(6.8, 7.54) * mm, v(6.79, 7.63) * mm]});
            skFitSpline(sketch, "E358", {"points": [v(6.79, 7.63) * mm, v(6.74, 8.12) * mm, v(6.7, 8.62) * mm, v(6.64, 9.1) * mm]});
            skFitSpline(sketch, "E359", {"points": [v(6.64, 9.1) * mm, v(6.6, 9.5) * mm, v(6.5, 9.87) * mm, v(6.44, 10.26) * mm]});
            skFitSpline(sketch, "E360", {"points": [v(6.44, 10.26) * mm, v(6.42, 10.32) * mm, v(6.4, 10.38) * mm, v(6.4, 10.45) * mm]});
            skFitSpline(sketch, "E361", {"points": [v(6.4, 10.45) * mm, v(6.4, 10.68) * mm, v(6.56, 10.88) * mm, v(6.77, 10.92) * mm]});
            skFitSpline(sketch, "E362", {"points": [v(6.77, 10.92) * mm, v(7.03, 10.98) * mm, v(7.26, 10.87) * mm, v(7.34, 10.62) * mm]});
            skFitSpline(sketch, "E363", {"points": [v(7.34, 10.62) * mm, v(7.41, 10.39) * mm, v(7.47, 10.15) * mm, v(7.5, 9.92) * mm]});
            skFitSpline(sketch, "E364", {"points": [v(7.5, 9.92) * mm, v(7.56, 9.57) * mm, v(7.58, 9.22) * mm, v(7.62, 8.87) * mm]});
            skFitSpline(sketch, "E365", {"points": [v(7.62, 8.87) * mm, v(7.65, 8.55) * mm, v(7.7, 8.22) * mm, v(7.73, 7.9) * mm]});
            skFitSpline(sketch, "E366", {"points": [v(7.73, 7.9) * mm, v(7.73, 7.88) * mm, v(7.75, 7.86) * mm, v(7.77, 7.82) * mm]});
            skFitSpline(sketch, "E367", {"points": [v(7.77, 7.82) * mm, v(8.05, 7.88) * mm, v(8.29, 8.12) * mm, v(8.64, 7.99) * mm]});
            skFitSpline(sketch, "E368", {"points": [v(8.64, 7.99) * mm, v(8.61, 8.24) * mm, v(8.58, 8.47) * mm, v(8.56, 8.7) * mm]});
            skFitSpline(sketch, "E369", {"points": [v(8.56, 8.7) * mm, v(8.54, 8.89) * mm, v(8.52, 9.08) * mm, v(8.52, 9.27) * mm]});
            skFitSpline(sketch, "E370", {"points": [v(8.52, 9.27) * mm, v(8.52, 9.51) * mm, v(8.67, 9.7) * mm, v(8.89, 9.73) * mm]});
            skFitSpline(sketch, "E371", {"points": [v(8.89, 9.73) * mm, v(9.17, 9.77) * mm, v(9.38, 9.65) * mm, v(9.45, 9.4) * mm]});
            skFitSpline(sketch, "E372", {"points": [v(9.45, 9.4) * mm, v(9.49, 9.27) * mm, v(9.51, 9.13) * mm, v(9.52, 9) * mm]});
            skFitSpline(sketch, "E373", {"points": [v(9.52, 9) * mm, v(9.55, 8.28) * mm, v(9.7, 7.58) * mm, v(9.8, 6.86) * mm]});
            skFitSpline(sketch, "E374", {"points": [v(9.8, 6.86) * mm, v(9.81, 6.78) * mm, v(9.82, 6.7) * mm, v(9.83, 6.58) * mm]});
            skFitSpline(sketch, "E375", {"points": [v(9.83, 6.58) * mm, v(10.23, 6.76) * mm, v(10.61, 6.94) * mm, v(11.02, 7.13) * mm]});
            skFitSpline(sketch, "E376", {"points": [v(11.02, 7.13) * mm, v(10.98, 7.31) * mm, v(10.95, 7.5) * mm, v(10.9, 7.7) * mm]});
            skFitSpline(sketch, "E377", {"points": [v(10.9, 7.7) * mm, v(10.78, 8.1) * mm, v(10.67, 8.5) * mm, v(10.55, 8.92) * mm]});
            skFitSpline(sketch, "E378", {"points": [v(10.55, 8.92) * mm, v(10.49, 9.14) * mm, v(10.6, 9.38) * mm, v(10.8, 9.48) * mm]});
            skFitSpline(sketch, "E379", {"points": [v(10.8, 9.48) * mm, v(11.03, 9.59) * mm, v(11.3, 9.52) * mm, v(11.44, 9.3) * mm]});
            skFitSpline(sketch, "E380", {"points": [v(11.44, 9.3) * mm, v(11.51, 9.17) * mm, v(11.56, 9.02) * mm, v(11.6, 8.88) * mm]});
            skFitSpline(sketch, "E381", {"points": [v(11.6, 8.88) * mm, v(11.81, 8.07) * mm, v(12.01, 7.27) * mm, v(12.22, 6.46) * mm]});
            skFitSpline(sketch, "E382", {"points": [v(12.22, 6.46) * mm, v(12.34, 5.98) * mm, v(12.47, 5.5) * mm, v(12.6, 5.03) * mm]});
            skFitSpline(sketch, "E383", {"points": [v(12.6, 5.03) * mm, v(12.61, 4.97) * mm, v(12.63, 4.9) * mm, v(12.66, 4.83) * mm]});
            skFitSpline(sketch, "E384", {"points": [v(12.66, 4.83) * mm, v(13.69, 5.12) * mm, v(14.7, 5.4) * mm, v(15.74, 5.7) * mm]});
            skFitSpline(sketch, "E385", {"points": [v(15.74, 5.7) * mm, v(15.63, 5.88) * mm, v(15.54, 6.04) * mm, v(15.44, 6.2) * mm]});
            skFitSpline(sketch, "E386", {"points": [v(15.44, 6.2) * mm, v(15.35, 6.2) * mm, v(15.26, 6.2) * mm, v(15.17, 6.21) * mm]});
            skFitSpline(sketch, "E387", {"points": [v(15.17, 6.21) * mm, v(15.02, 6.24) * mm, v(14.85, 6.26) * mm, v(14.72, 6.33) * mm]});
            skFitSpline(sketch, "E388", {"points": [v(14.72, 6.33) * mm, v(14.31, 6.58) * mm, v(13.97, 6.9) * mm, v(13.83, 7.37) * mm]});
            skFitSpline(sketch, "E389", {"points": [v(13.83, 7.37) * mm, v(13.73, 7.74) * mm, v(13.75, 8.12) * mm, v(14.12, 8.4) * mm]});
            skFitSpline(sketch, "E390", {"points": [v(14.12, 8.4) * mm, v(14.04, 8.53) * mm, v(13.96, 8.67) * mm, v(13.89, 8.81) * mm]});
            skFitSpline(sketch, "E391", {"points": [v(13.89, 8.81) * mm, v(13.56, 9.38) * mm, v(13.23, 9.95) * mm, v(12.9, 10.52) * mm]});
            skFitSpline(sketch, "E392", {"points": [v(12.9, 10.52) * mm, v(12.82, 10.67) * mm, v(12.75, 10.84) * mm, v(12.65, 11) * mm]});
            skFitSpline(sketch, "E393", {"points": [v(12.65, 11) * mm, v(12.61, 11.06) * mm, v(12.53, 11.1) * mm, v(12.46, 11.12) * mm]});
            skFitSpline(sketch, "E394", {"points": [v(12.46, 11.12) * mm, v(12.08, 11.22) * mm, v(11.68, 11.3) * mm, v(11.3, 11.4) * mm]});
            skFitSpline(sketch, "E395", {"points": [v(11.3, 11.4) * mm, v(10.94, 11.5) * mm, v(10.58, 11.62) * mm, v(10.23, 11.75) * mm]});
            skFitSpline(sketch, "E396", {"points": [v(10.23, 11.75) * mm, v(9.92, 11.86) * mm, v(9.76, 12.08) * mm, v(9.76, 12.43) * mm]});
            skFitSpline(sketch, "E397", {"points": [v(9.76, 12.43) * mm, v(9.76, 12.69) * mm, v(9.7, 12.95) * mm, v(9.68, 13.2) * mm]});
            skFitSpline(sketch, "E398", {"points": [v(9.68, 13.2) * mm, v(9.64, 13.84) * mm, v(9.71, 14.47) * mm, v(9.76, 15.1) * mm]});
            skFitSpline(sketch, "E399", {"points": [v(9.76, 15.1) * mm, v(9.77, 15.28) * mm, v(9.77, 15.46) * mm, v(9.78, 15.65) * mm]});
            skFitSpline(sketch, "E400", {"points": [v(9.78, 15.65) * mm, v(9.79, 15.91) * mm, v(9.9, 16.06) * mm, v(10.14, 16.15) * mm]});
            skFitSpline(sketch, "E401", {"points": [v(10.14, 16.15) * mm, v(10.2, 16.17) * mm, v(10.27, 16.2) * mm, v(10.32, 16.25) * mm]});
            skFitSpline(sketch, "E402", {"points": [v(10.32, 16.25) * mm, v(10.52, 16.42) * mm, v(10.71, 16.44) * mm, v(10.94, 16.33) * mm]});
            skFitSpline(sketch, "E403", {"points": [v(10.94, 16.33) * mm, v(11.47, 16.07) * mm, v(12, 15.8) * mm, v(12.52, 15.54) * mm]});
            skFitSpline(sketch, "E404", {"points": [v(12.52, 15.54) * mm, v(12.72, 15.43) * mm, v(12.91, 15.31) * mm, v(13.1, 15.2) * mm]});
            skFitSpline(sketch, "E405", {"points": [v(13.1, 15.2) * mm, v(13.31, 15.05) * mm, v(13.5, 14.88) * mm, v(13.73, 14.75) * mm]});
            skFitSpline(sketch, "E406", {"points": [v(13.73, 14.75) * mm, v(14.09, 14.55) * mm, v(14.15, 14.23) * mm, v(14.08, 13.87) * mm]});
            skFitSpline(sketch, "E407", {"points": [v(14.08, 13.87) * mm, v(14, 13.38) * mm, v(13.9, 12.9) * mm, v(13.72, 12.43) * mm]});
            skFitSpline(sketch, "E408", {"points": [v(13.72, 12.43) * mm, v(13.63, 12.2) * mm, v(13.57, 11.94) * mm, v(13.5, 11.7) * mm]});
            skFitSpline(sketch, "E409", {"points": [v(13.5, 11.7) * mm, v(13.5, 11.63) * mm, v(13.51, 11.55) * mm, v(13.55, 11.5) * mm]});
            skFitSpline(sketch, "E410", {"points": [v(13.55, 11.5) * mm, v(13.66, 11.3) * mm, v(13.78, 11.12) * mm, v(13.9, 10.93) * mm]});
            skFitSpline(sketch, "E411", {"points": [v(13.9, 10.93) * mm, v(14.27, 10.3) * mm, v(14.63, 9.67) * mm, v(15, 9.04) * mm]});
            skFitSpline(sketch, "E412", {"points": [v(15, 9.04) * mm, v(15.01, 9.01) * mm, v(15.03, 8.99) * mm, v(15.05, 8.95) * mm]});
            skFitSpline(sketch, "E413", {"points": [v(15.05, 8.95) * mm, v(15.08, 8.96) * mm, v(15.11, 8.95) * mm, v(15.14, 8.96) * mm]});
            skFitSpline(sketch, "E414", {"points": [v(15.14, 8.96) * mm, v(15.52, 9.07) * mm, v(15.9, 8.93) * mm, v(16.14, 8.62) * mm]});
            skFitSpline(sketch, "E415", {"points": [v(16.14, 8.62) * mm, v(16.4, 8.28) * mm, v(16.51, 7.88) * mm, v(16.54, 7.46) * mm]});
            skFitSpline(sketch, "E416", {"points": [v(16.54, 7.46) * mm, v(16.56, 7.2) * mm, v(16.5, 6.94) * mm, v(16.27, 6.73) * mm]});
            skFitSpline(sketch, "E417", {"points": [v(16.27, 6.73) * mm, v(16.38, 6.55) * mm, v(16.48, 6.37) * mm, v(16.59, 6.18) * mm]});
            skFitSpline(sketch, "E418", {"points": [v(16.59, 6.18) * mm, v(17.36, 6.93) * mm, v(18.1, 7.67) * mm, v(18.87, 8.41) * mm]});
            skFitSpline(sketch, "E419", {"points": [v(18.87, 8.41) * mm, v(18.82, 8.47) * mm, v(18.78, 8.53) * mm, v(18.74, 8.57) * mm]});
            skFitSpline(sketch, "E420", {"points": [v(18.74, 8.57) * mm, v(18.3, 9) * mm, v(17.86, 9.44) * mm, v(17.42, 9.87) * mm]});
            skFitSpline(sketch, "E421", {"points": [v(17.42, 9.87) * mm, v(16.93, 10.36) * mm, v(16.42, 10.84) * mm, v(15.93, 11.33) * mm]});
            skFitSpline(sketch, "E422", {"points": [v(15.93, 11.33) * mm, v(15.82, 11.43) * mm, v(15.72, 11.55) * mm, v(15.64, 11.68) * mm]});
            skFitSpline(sketch, "E423", {"points": [v(15.64, 11.68) * mm, v(15.53, 11.85) * mm, v(15.53, 12.04) * mm, v(15.65, 12.22) * mm]});
            skFitSpline(sketch, "E424", {"points": [v(15.65, 12.22) * mm, v(15.76, 12.4) * mm, v(15.94, 12.45) * mm, v(16.13, 12.41) * mm]});
            skFitSpline(sketch, "E425", {"points": [v(16.13, 12.41) * mm, v(16.23, 12.39) * mm, v(16.34, 12.33) * mm, v(16.41, 12.25) * mm]});
            skFitSpline(sketch, "E426", {"points": [v(16.41, 12.25) * mm, v(16.84, 11.83) * mm, v(17.26, 11.4) * mm, v(17.68, 10.97) * mm]});
            skFitSpline(sketch, "E427", {"points": [v(17.68, 10.97) * mm, v(18.05, 11.24) * mm, v(18.4, 11.48) * mm, v(18.77, 11.74) * mm]});
            skFitSpline(sketch, "E428", {"points": [v(18.77, 11.74) * mm, v(18.69, 11.8) * mm, v(18.61, 11.86) * mm, v(18.54, 11.92) * mm]});
            skFitSpline(sketch, "E429", {"points": [v(18.54, 11.92) * mm, v(18.04, 12.3) * mm, v(17.55, 12.7) * mm, v(17.05, 13.08) * mm]});
            skFitSpline(sketch, "E430", {"points": [v(17.05, 13.08) * mm, v(16.9, 13.2) * mm, v(16.72, 13.31) * mm, v(16.57, 13.44) * mm]});
            skFitSpline(sketch, "E431", {"points": [v(16.57, 13.44) * mm, v(16.38, 13.6) * mm, v(16.33, 13.84) * mm, v(16.45, 14.04) * mm]});
            skFitSpline(sketch, "E432", {"points": [v(16.45, 14.04) * mm, v(16.58, 14.29) * mm, v(16.9, 14.37) * mm, v(17.15, 14.2) * mm]});
            skFitSpline(sketch, "E433", {"points": [v(17.15, 14.2) * mm, v(17.34, 14.09) * mm, v(17.51, 13.95) * mm, v(17.7, 13.81) * mm]});
            skFitSpline(sketch, "E434", {"points": [v(17.7, 13.81) * mm, v(17.83, 13.7) * mm, v(17.97, 13.6) * mm, v(18.14, 13.48) * mm]});
            skFitSpline(sketch, "E435", {"points": [v(18.14, 13.48) * mm, v(18.22, 13.83) * mm, v(18.52, 13.95) * mm, v(18.77, 14.17) * mm]});
            skFitSpline(sketch, "E436", {"points": [v(18.77, 14.17) * mm, v(18.4, 14.42) * mm, v(18.07, 14.67) * mm, v(17.73, 14.9) * mm]});
            skFitSpline(sketch, "E437", {"points": [v(17.73, 14.9) * mm, v(17.3, 15.19) * mm, v(16.9, 15.5) * mm, v(16.56, 15.88) * mm]});
            skFitSpline(sketch, "E438", {"points": [v(16.56, 15.88) * mm, v(16.29, 16.17) * mm, v(16.39, 16.58) * mm, v(16.74, 16.7) * mm]});
            skFitSpline(sketch, "E439", {"points": [v(16.74, 16.7) * mm, v(16.93, 16.75) * mm, v(17.1, 16.7) * mm, v(17.23, 16.57) * mm]});
            skFitSpline(sketch, "E440", {"points": [v(17.23, 16.57) * mm, v(17.4, 16.43) * mm, v(17.54, 16.27) * mm, v(17.71, 16.14) * mm]});
            skFitSpline(sketch, "E441", {"points": [v(17.71, 16.14) * mm, v(18.02, 15.9) * mm, v(18.34, 15.68) * mm, v(18.66, 15.45) * mm]});
            skFitSpline(sketch, "E442", {"points": [v(18.66, 15.45) * mm, v(18.97, 15.22) * mm, v(19.28, 15) * mm, v(19.6, 14.75) * mm]});
            skFitSpline(sketch, "E443", {"points": [v(19.6, 14.75) * mm, v(19.64, 14.79) * mm, v(19.7, 14.82) * mm, v(19.74, 14.86) * mm]});
            skFitSpline(sketch, "E444", {"points": [v(19.74, 14.86) * mm, v(20.15, 15.15) * mm, v(20.57, 15.44) * mm, v(20.97, 15.74) * mm]});
            skFitSpline(sketch, "E445", {"points": [v(20.97, 15.74) * mm, v(21.28, 15.99) * mm, v(21.58, 16.25) * mm, v(21.89, 16.5) * mm]});
            skFitSpline(sketch, "E446", {"points": [v(21.89, 16.5) * mm, v(21.93, 16.54) * mm, v(21.97, 16.58) * mm, v(22.01, 16.62) * mm]});
            skFitSpline(sketch, "E447", {"points": [v(22.01, 16.62) * mm, v(22.22, 16.76) * mm, v(22.48, 16.74) * mm, v(22.65, 16.57) * mm]});
            skFitSpline(sketch, "E448", {"points": [v(22.65, 16.57) * mm, v(22.82, 16.4) * mm, v(22.84, 16.1) * mm, v(22.66, 15.92) * mm]});
            skFitSpline(sketch, "E449", {"points": [v(22.66, 15.92) * mm, v(22.48, 15.72) * mm, v(22.3, 15.54) * mm, v(22.08, 15.38) * mm]});
            skFitSpline(sketch, "E450", {"points": [v(22.08, 15.38) * mm, v(21.7, 15.09) * mm, v(21.31, 14.81) * mm, v(20.92, 14.53) * mm]});
            skFitSpline(sketch, "E451", {"points": [v(20.92, 14.53) * mm, v(20.76, 14.42) * mm, v(20.6, 14.3) * mm, v(20.44, 14.17) * mm]});
            skFitSpline(sketch, "E452", {"points": [v(20.44, 14.17) * mm, v(20.65, 13.95) * mm, v(20.97, 13.84) * mm, v(21.04, 13.48) * mm]});
            skFitSpline(sketch, "E453", {"points": [v(21.04, 13.48) * mm, v(21.22, 13.6) * mm, v(21.37, 13.72) * mm, v(21.52, 13.83) * mm]});
            skFitSpline(sketch, "E454", {"points": [v(21.52, 13.83) * mm, v(21.7, 13.96) * mm, v(21.86, 14.1) * mm, v(22.04, 14.21) * mm]});
            skFitSpline(sketch, "E455", {"points": [v(22.04, 14.21) * mm, v(22.35, 14.4) * mm, v(22.74, 14.24) * mm, v(22.8, 13.88) * mm]});
            skFitSpline(sketch, "E456", {"points": [v(22.8, 13.88) * mm, v(22.83, 13.68) * mm, v(22.74, 13.52) * mm, v(22.58, 13.4) * mm]});
            skFitSpline(sketch, "E457", {"points": [v(22.58, 13.4) * mm, v(22.34, 13.22) * mm, v(22.1, 13.05) * mm, v(21.85, 12.86) * mm]});
            skFitSpline(sketch, "E458", {"points": [v(21.85, 12.86) * mm, v(21.48, 12.57) * mm, v(21.11, 12.28) * mm, v(20.74, 11.99) * mm]});
            skFitSpline(sketch, "E459", {"points": [v(20.74, 11.99) * mm, v(20.64, 11.9) * mm, v(20.54, 11.83) * mm, v(20.41, 11.74) * mm]});
            skFitSpline(sketch, "E460", {"points": [v(20.41, 11.74) * mm, v(20.77, 11.5) * mm, v(21.12, 11.25) * mm, v(21.49, 10.99) * mm]});
            skFitSpline(sketch, "E461", {"points": [v(21.49, 10.99) * mm, v(21.6, 11.09) * mm, v(21.73, 11.2) * mm, v(21.86, 11.32) * mm]});
            skFitSpline(sketch, "E462", {"points": [v(21.86, 11.32) * mm, v(22.17, 11.63) * mm, v(22.47, 11.95) * mm, v(22.78, 12.26) * mm]});
            skFitSpline(sketch, "E463", {"points": [v(22.78, 12.26) * mm, v(22.93, 12.42) * mm, v(23.18, 12.47) * mm, v(23.37, 12.37) * mm]});
            skFitSpline(sketch, "E464", {"points": [v(23.37, 12.37) * mm, v(23.56, 12.28) * mm, v(23.68, 12.03) * mm, v(23.6, 11.83) * mm]});
            skFitSpline(sketch, "E465", {"points": [v(23.6, 11.83) * mm, v(23.55, 11.67) * mm, v(23.45, 11.53) * mm, v(23.34, 11.41) * mm]});
            skFitSpline(sketch, "E466", {"points": [v(23.34, 11.41) * mm, v(23.1, 11.16) * mm, v(22.85, 10.93) * mm, v(22.6, 10.69) * mm]});
            skFitSpline(sketch, "E467", {"points": [v(22.6, 10.69) * mm, v(21.95, 10.05) * mm, v(21.3, 9.4) * mm, v(20.66, 8.77) * mm]});
            skFitSpline(sketch, "E468", {"points": [v(20.66, 8.77) * mm, v(20.54, 8.66) * mm, v(20.43, 8.55) * mm, v(20.3, 8.42) * mm]});
            skFitSpline(sketch, "E469", {"points": [v(20.3, 8.42) * mm, v(21.08, 7.67) * mm, v(21.83, 6.94) * mm, v(22.6, 6.18) * mm]});
            skFitSpline(sketch, "E470", {"points": [v(22.6, 6.18) * mm, v(22.7, 6.37) * mm, v(22.8, 6.54) * mm, v(22.9, 6.68) * mm]});
            skFitSpline(sketch, "E471", {"points": [v(22.9, 6.68) * mm, v(22.81, 6.85) * mm, v(22.71, 7) * mm, v(22.68, 7.15) * mm]});
            skFitSpline(sketch, "E472", {"points": [v(22.68, 7.15) * mm, v(22.59, 7.62) * mm, v(22.7, 8.06) * mm, v(22.94, 8.46) * mm]});
            skFitSpline(sketch, "E473", {"points": [v(22.94, 8.46) * mm, v(23.07, 8.65) * mm, v(23.2, 8.83) * mm, v(23.44, 8.92) * mm]});
            skFitSpline(sketch, "E474", {"points": [v(23.44, 8.92) * mm, v(23.67, 9.01) * mm, v(23.88, 9.04) * mm, v(24.13, 8.93) * mm]});
            skFitSpline(sketch, "E475", {"points": [v(24.13, 8.93) * mm, v(24.2, 9.07) * mm, v(24.29, 9.2) * mm, v(24.36, 9.32) * mm]});
            skFitSpline(sketch, "E476", {"points": [v(24.36, 9.32) * mm, v(24.7, 9.9) * mm, v(25.02, 10.46) * mm, v(25.35, 11.02) * mm]});
            skFitSpline(sketch, "E477", {"points": [v(25.35, 11.02) * mm, v(25.45, 11.19) * mm, v(25.56, 11.34) * mm, v(25.65, 11.51) * mm]});
            skFitSpline(sketch, "E478", {"points": [v(25.65, 11.51) * mm, v(25.68, 11.57) * mm, v(25.7, 11.65) * mm, v(25.68, 11.71) * mm]});
            skFitSpline(sketch, "E479", {"points": [v(25.68, 11.71) * mm, v(25.57, 12.09) * mm, v(25.44, 12.46) * mm, v(25.34, 12.84) * mm]});
            skFitSpline(sketch, "E480", {"points": [v(25.34, 12.84) * mm, v(25.24, 13.26) * mm, v(25.16, 13.7) * mm, v(25.09, 14.12) * mm]});
            skFitSpline(sketch, "E481", {"points": [v(25.09, 14.12) * mm, v(25.05, 14.36) * mm, v(25.17, 14.53) * mm, v(25.36, 14.67) * mm]});
            skFitSpline(sketch, "E482", {"points": [v(25.36, 14.67) * mm, v(26, 15.16) * mm, v(26.67, 15.58) * mm, v(27.4, 15.9) * mm]});
            skFitSpline(sketch, "E483", {"points": [v(27.4, 15.9) * mm, v(27.68, 16.03) * mm, v(27.95, 16.18) * mm, v(28.22, 16.32) * mm]});
            skFitSpline(sketch, "E484", {"points": [v(28.22, 16.32) * mm, v(28.47, 16.45) * mm, v(28.65, 16.43) * mm, v(28.88, 16.24) * mm]});
            skFitSpline(sketch, "E485", {"points": [v(28.88, 16.24) * mm, v(28.93, 16.2) * mm, v(29, 16.17) * mm, v(29.06, 16.14) * mm]});
            skFitSpline(sketch, "E486", {"points": [v(29.06, 16.14) * mm, v(29.28, 16.07) * mm, v(29.39, 15.92) * mm, v(29.4, 15.7) * mm]});
            skFitSpline(sketch, "E487", {"points": [v(29.4, 15.7) * mm, v(29.44, 15.08) * mm, v(29.5, 14.46) * mm, v(29.52, 13.84) * mm]});
            skFitSpline(sketch, "E488", {"points": [v(29.52, 13.84) * mm, v(29.54, 13.5) * mm, v(29.5, 13.16) * mm, v(29.47, 12.82) * mm]});
            skFitSpline(sketch, "E489", {"points": [v(29.47, 12.82) * mm, v(29.46, 12.63) * mm, v(29.42, 12.44) * mm, v(29.4, 12.25) * mm]});
            skFitSpline(sketch, "E490", {"points": [v(29.4, 12.25) * mm, v(29.39, 12.07) * mm, v(29.3, 11.94) * mm, v(29.16, 11.86) * mm]});
            skFitSpline(sketch, "E491", {"points": [v(29.16, 11.86) * mm, v(29.02, 11.78) * mm, v(28.87, 11.73) * mm, v(28.72, 11.67) * mm]});
            skFitSpline(sketch, "E492", {"points": [v(28.72, 11.67) * mm, v(28.28, 11.48) * mm, v(27.8, 11.38) * mm, v(27.34, 11.29) * mm]});
            skFitSpline(sketch, "E493", {"points": [v(27.34, 11.29) * mm, v(27.12, 11.25) * mm, v(26.9, 11.18) * mm, v(26.69, 11.12) * mm]});
            skFitSpline(sketch, "E494", {"points": [v(26.69, 11.12) * mm, v(26.63, 11.1) * mm, v(26.56, 11.04) * mm, v(26.53, 10.99) * mm]});
            skFitSpline(sketch, "E495", {"points": [v(26.53, 10.99) * mm, v(26.42, 10.8) * mm, v(26.33, 10.6) * mm, v(26.23, 10.42) * mm]});
            skFitSpline(sketch, "E496", {"points": [v(26.23, 10.42) * mm, v(25.86, 9.77) * mm, v(25.49, 9.13) * mm, v(25.12, 8.48) * mm]});
            skFitSpline(sketch, "E497", {"points": [v(25.12, 8.48) * mm, v(25.1, 8.46) * mm, v(25.1, 8.43) * mm, v(25.07, 8.39) * mm]});
            skFitSpline(sketch, "E498", {"points": [v(25.07, 8.39) * mm, v(25.4, 8.15) * mm, v(25.46, 7.8) * mm, v(25.38, 7.45) * mm]});
            skFitSpline(sketch, "E499", {"points": [v(25.38, 7.45) * mm, v(25.32, 7.16) * mm, v(25.16, 6.9) * mm, v(24.93, 6.7) * mm]});
            skFitSpline(sketch, "E500", {"points": [v(24.93, 6.7) * mm, v(24.8, 6.57) * mm, v(24.67, 6.46) * mm, v(24.52, 6.36) * mm]});
            skFitSpline(sketch, "E501", {"points": [v(24.52, 6.36) * mm, v(24.37, 6.26) * mm, v(24.2, 6.2) * mm, v(24, 6.2) * mm]});
            skFitSpline(sketch, "E502", {"points": [v(24, 6.2) * mm, v(23.93, 6.21) * mm, v(23.85, 6.2) * mm, v(23.75, 6.2) * mm]});
            skFitSpline(sketch, "E503", {"points": [v(23.75, 6.2) * mm, v(23.66, 6.05) * mm, v(23.56, 5.89) * mm, v(23.45, 5.7) * mm]});
            skFitSpline(sketch, "E504", {"points": [v(23.45, 5.7) * mm, v(23.97, 5.55) * mm, v(24.48, 5.4) * mm, v(25, 5.26) * mm]});
            skFitSpline(sketch, "E505", {"points": [v(25, 5.26) * mm, v(25.5, 5.11) * mm, v(26, 4.98) * mm, v(26.52, 4.84) * mm]});
            skFitSpline(sketch, "E506", {"points": [v(26.52, 4.84) * mm, v(26.55, 4.9) * mm, v(26.58, 4.97) * mm, v(26.6, 5.04) * mm]});
            skFitSpline(sketch, "E507", {"points": [v(26.6, 5.04) * mm, v(26.8, 5.8) * mm, v(27, 6.56) * mm, v(27.2, 7.33) * mm]});
            skFitSpline(sketch, "E508", {"points": [v(27.2, 7.33) * mm, v(27.33, 7.83) * mm, v(27.44, 8.34) * mm, v(27.58, 8.84) * mm]});
            skFitSpline(sketch, "E509", {"points": [v(27.58, 8.84) * mm, v(27.62, 9) * mm, v(27.67, 9.15) * mm, v(27.74, 9.28) * mm]});
            skFitSpline(sketch, "E510", {"points": [v(27.74, 9.28) * mm, v(27.85, 9.48) * mm, v(28.07, 9.56) * mm, v(28.28, 9.51) * mm]});
            skFitSpline(sketch, "E511", {"points": [v(28.28, 9.51) * mm, v(28.48, 9.47) * mm, v(28.6, 9.34) * mm, v(28.64, 9.14) * mm]});
            skFitSpline(sketch, "E512", {"points": [v(28.64, 9.14) * mm, v(28.66, 9.06) * mm, v(28.64, 8.97) * mm, v(28.62, 8.89) * mm]});
            skFitSpline(sketch, "E513", {"points": [v(28.62, 8.89) * mm, v(28.47, 8.3) * mm, v(28.3, 7.72) * mm, v(28.14, 7.14) * mm]});
            skFitSpline(sketch, "E514", {"points": [v(28.14, 7.14) * mm, v(28.56, 6.95) * mm, v(28.94, 6.77) * mm, v(29.36, 6.58) * mm]});
            skFitSpline(sketch, "E515", {"points": [v(29.36, 6.58) * mm, v(29.38, 6.78) * mm, v(29.4, 6.95) * mm, v(29.43, 7.13) * mm]});
            skFitSpline(sketch, "E516", {"points": [v(29.43, 7.13) * mm, v(29.47, 7.4) * mm, v(29.52, 7.67) * mm, v(29.55, 7.94) * mm]});
            skFitSpline(sketch, "E517", {"points": [v(29.55, 7.94) * mm, v(29.6, 8.27) * mm, v(29.63, 8.6) * mm, v(29.67, 8.93) * mm]});
            skFitSpline(sketch, "E518", {"points": [v(29.67, 8.93) * mm, v(29.7, 9.08) * mm, v(29.7, 9.23) * mm, v(29.73, 9.38) * mm]});
            skFitSpline(sketch, "E519", {"points": [v(29.73, 9.38) * mm, v(29.79, 9.62) * mm, v(30, 9.75) * mm, v(30.26, 9.73) * mm]});
            skFitSpline(sketch, "E520", {"points": [v(30.26, 9.73) * mm, v(30.5, 9.71) * mm, v(30.68, 9.53) * mm, v(30.68, 9.29) * mm]});
            skFitSpline(sketch, "E521", {"points": [v(30.68, 9.29) * mm, v(30.67, 9.05) * mm, v(30.64, 8.81) * mm, v(30.61, 8.57) * mm]});
            skFitSpline(sketch, "E522", {"points": [v(30.61, 8.57) * mm, v(30.6, 8.4) * mm, v(30.57, 8.21) * mm, v(30.54, 8) * mm]});
            skFitSpline(sketch, "E523", {"points": [v(30.54, 8) * mm, v(30.89, 8.1) * mm, v(31.14, 7.9) * mm, v(31.45, 7.8) * mm]});
            skFitSpline(sketch, "E524", {"points": [v(31.45, 7.8) * mm, v(31.5, 8.17) * mm, v(31.54, 8.5) * mm, v(31.56, 8.84) * mm]});
            skFitSpline(sketch, "E525", {"points": [v(31.56, 8.84) * mm, v(31.6, 9.4) * mm, v(31.67, 9.95) * mm, v(31.8, 10.5) * mm]});
            skFitSpline(sketch, "E526", {"points": [v(31.8, 10.5) * mm, v(31.89, 10.8) * mm, v(32.04, 10.93) * mm, v(32.3, 10.93) * mm]});
            skFitSpline(sketch, "E527", {"points": [v(32.3, 10.93) * mm, v(32.61, 10.93) * mm, v(32.84, 10.67) * mm, v(32.78, 10.36) * mm]});
            skFitSpline(sketch, "E528", {"points": [v(32.78, 10.36) * mm, v(32.72, 10.05) * mm, v(32.65, 9.75) * mm, v(32.6, 9.45) * mm]});
            skFitSpline(sketch, "E529", {"points": [v(32.6, 9.45) * mm, v(32.56, 9.24) * mm, v(32.54, 9.03) * mm, v(32.52, 8.83) * mm]});
            skFitSpline(sketch, "E530", {"points": [v(32.52, 8.83) * mm, v(32.47, 8.4) * mm, v(32.43, 7.96) * mm, v(32.38, 7.52) * mm]});
            skFitSpline(sketch, "E531", {"points": [v(32.38, 7.52) * mm, v(32.37, 7.48) * mm, v(32.37, 7.43) * mm, v(32.37, 7.37) * mm]});
            skFitSpline(sketch, "E532", {"points": [v(32.37, 7.37) * mm, v(32.46, 7.33) * mm, v(32.54, 7.3) * mm, v(32.62, 7.27) * mm]});
            skFitSpline(sketch, "E533", {"points": [v(32.62, 7.27) * mm, v(32.95, 7.12) * mm, v(33.3, 6.99) * mm, v(33.62, 6.82) * mm]});
            skFitSpline(sketch, "E534", {"points": [v(33.62, 6.82) * mm, v(34.06, 6.61) * mm, v(34.5, 6.42) * mm, v(34.96, 6.3) * mm]});
            skFitSpline(sketch, "E535", {"points": [v(34.96, 6.3) * mm, v(35.03, 6.28) * mm, v(35.1, 6.25) * mm, v(35.16, 6.22) * mm]});
            skFitSpline(sketch, "E536", {"points": [v(35.16, 6.22) * mm, v(35.42, 6.12) * mm, v(35.55, 5.88) * mm, v(35.47, 5.63) * mm]});
            skFitSpline(sketch, "E537", {"points": [v(35.47, 5.63) * mm, v(35.41, 5.4) * mm, v(35.15, 5.22) * mm, v(34.87, 5.3) * mm]});
            skFitSpline(sketch, "E538", {"points": [v(34.87, 5.3) * mm, v(34.37, 5.44) * mm, v(33.9, 5.6) * mm, v(33.43, 5.83) * mm]});
            skFitSpline(sketch, "E539", {"points": [v(33.43, 5.83) * mm, v(33.06, 6.01) * mm, v(32.68, 6.18) * mm, v(32.3, 6.36) * mm]});
            skFitSpline(sketch, "E540", {"points": [v(32.3, 6.36) * mm, v(32.19, 6.06) * mm, v(32.3, 5.73) * mm, v(32.01, 5.51) * mm]});
            skFitSpline(sketch, "E541", {"points": [v(32.01, 5.51) * mm, v(32.17, 5.37) * mm, v(32.35, 5.33) * mm, v(32.51, 5.26) * mm]});
            skFitSpline(sketch, "E542", {"points": [v(32.51, 5.26) * mm, v(32.72, 5.17) * mm, v(32.92, 5.09) * mm, v(33.12, 4.99) * mm]});
            skFitSpline(sketch, "E543", {"points": [v(33.12, 4.99) * mm, v(33.32, 4.9) * mm, v(33.44, 4.68) * mm, v(33.4, 4.5) * mm]});
            skFitSpline(sketch, "E544", {"points": [v(33.4, 4.5) * mm, v(33.37, 4.28) * mm, v(33.25, 4.12) * mm, v(33.03, 4.08) * mm]});
            skFitSpline(sketch, "E545", {"points": [v(33.03, 4.08) * mm, v(32.93, 4.06) * mm, v(32.8, 4.08) * mm, v(32.69, 4.12) * mm]});
            skFitSpline(sketch, "E546", {"points": [v(32.69, 4.12) * mm, v(32.4, 4.23) * mm, v(32.13, 4.36) * mm, v(31.85, 4.48) * mm]});
            skFitSpline(sketch, "E547", {"points": [v(31.85, 4.48) * mm, v(31.41, 4.66) * mm, v(30.97, 4.83) * mm, v(30.52, 5.01) * mm]});
            skFitSpline(sketch, "E548", {"points": [v(30.52, 5.01) * mm, v(30.41, 5.06) * mm, v(30.3, 5.1) * mm, v(30.17, 5.16) * mm]});
            skFitSpline(sketch, "E549", {"points": [v(30.17, 5.16) * mm, v(30.13, 4.72) * mm, v(30.1, 4.3) * mm, v(30.06, 3.85) * mm]});
            skFitSpline(sketch, "E550", {"points": [v(30.06, 3.85) * mm, v(30.23, 3.8) * mm, v(30.42, 3.73) * mm, v(30.6, 3.68) * mm]});
            skFitSpline(sketch, "E551", {"points": [v(30.6, 3.68) * mm, v(30.93, 3.58) * mm, v(31.25, 3.5) * mm, v(31.58, 3.4) * mm]});
            skFitSpline(sketch, "E552", {"points": [v(31.58, 3.4) * mm, v(31.62, 3.4) * mm, v(31.67, 3.38) * mm, v(31.72, 3.38) * mm]});
            skFitSpline(sketch, "E553", {"points": [v(31.72, 3.38) * mm, v(32.03, 3.35) * mm, v(32.23, 3.13) * mm, v(32.21, 2.87) * mm]});
            skFitSpline(sketch, "E554", {"points": [v(32.21, 2.87) * mm, v(32.18, 2.58) * mm, v(31.92, 2.37) * mm, v(31.62, 2.41) * mm]});
            skFitSpline(sketch, "E555", {"points": [v(31.62, 2.41) * mm, v(31.4, 2.44) * mm, v(31.2, 2.5) * mm, v(30.99, 2.56) * mm]});
            skFitSpline(sketch, "E556", {"points": [v(30.99, 2.56) * mm, v(29.94, 2.85) * mm, v(28.9, 3.14) * mm, v(27.85, 3.43) * mm]});
            skFitSpline(sketch, "E557", {"points": [v(27.85, 3.43) * mm, v(27.69, 3.47) * mm, v(27.53, 3.52) * mm, v(27.37, 3.57) * mm]});
            skFitSpline(sketch, "E558", {"points": [v(27.37, 3.57) * mm, v(27.33, 3.58) * mm, v(27.3, 3.57) * mm, v(27.25, 3.57) * mm]});
            skFitSpline(sketch, "E559", {"points": [v(27.25, 3.57) * mm, v(26.98, 2.54) * mm, v(26.72, 1.53) * mm, v(26.45, 0.49) * mm]});
            skLineSegment(sketch, "E560", {"start": v(26.45, 0.49) * mm, "end": v(27.06, 0.49) * mm});
            skFitSpline(sketch, "E561", {"points": [v(27.06, 0.49) * mm, v(27.32, 1.02) * mm, v(27.95, 1.38) * mm, v(28.55, 1.33) * mm]});
            skFitSpline(sketch, "E562", {"points": [v(28.55, 1.33) * mm, v(28.75, 1.31) * mm, v(28.95, 1.32) * mm, v(29.13, 1.2) * mm]});
            skFitSpline(sketch, "E563", {"points": [v(29.13, 1.2) * mm, v(29.43, 1.02) * mm, v(29.51, 0.91) * mm, v(29.62, 0.53) * mm]});
            skFitSpline(sketch, "E564", {"points": [v(29.62, 0.53) * mm, v(29.8, 0.53) * mm, v(30, 0.53) * mm, v(30.2, 0.53) * mm]});
            skFitSpline(sketch, "E565", {"points": [v(30.2, 0.53) * mm, v(30.47, 0.53) * mm, v(30.74, 0.53) * mm, v(31, 0.53) * mm]});
            skFitSpline(sketch, "E566", {"points": [v(31, 0.53) * mm, v(31.15, 0.53) * mm, v(31.3, 0.52) * mm, v(31.44, 0.52) * mm]});
            skFitSpline(sketch, "E567", {"points": [v(31.44, 0.52) * mm, v(31.82, 0.51) * mm, v(32.2, 0.5) * mm, v(32.56, 0.5) * mm]});
            skFitSpline(sketch, "E568", {"points": [v(32.56, 0.5) * mm, v(32.67, 0.5) * mm, v(32.74, 0.54) * mm, v(32.81, 0.61) * mm]});
            skFitSpline(sketch, "E569", {"points": [v(32.81, 0.61) * mm, v(33.34, 1.1) * mm, v(33.75, 1.7) * mm, v(34.34, 2.13) * mm]});
            skFitSpline(sketch, "E570", {"points": [v(34.34, 2.13) * mm, v(34.43, 2.2) * mm, v(34.52, 2.27) * mm, v(34.61, 2.33) * mm]});
            skFitSpline(sketch, "E571", {"points": [v(34.61, 2.33) * mm, v(34.79, 2.44) * mm, v(34.97, 2.44) * mm, v(35.16, 2.36) * mm]});
            skFitSpline(sketch, "E572", {"points": [v(35.16, 2.36) * mm, v(35.89, 2.05) * mm, v(36.59, 1.68) * mm, v(37.23, 1.22) * mm]});
            skFitSpline(sketch, "E573", {"points": [v(37.23, 1.22) * mm, v(37.5, 1.03) * mm, v(37.76, 0.86) * mm, v(38.03, 0.7) * mm]});
            skFitSpline(sketch, "E574", {"points": [v(38.03, 0.7) * mm, v(38.29, 0.53) * mm, v(38.36, 0.37) * mm, v(38.3, 0.09) * mm]});
            skFitSpline(sketch, "E575", {"points": [v(38.3, 0.09) * mm, v(38.3, 0.02) * mm, v(38.3, -0.05) * mm, v(38.31, -0.12) * mm]});
            skFitSpline(sketch, "E576", {"points": [v(38.31, -0.12) * mm, v(38.35, -0.36) * mm, v(38.28, -0.54) * mm, v(38.07, -0.67) * mm]});
            skFitSpline(sketch, "E577", {"points": [v(38.07, -0.67) * mm, v(37.57, -1) * mm, v(37.06, -1.35) * mm, v(36.55, -1.67) * mm]});
            skFitSpline(sketch, "E578", {"points": [v(36.55, -1.67) * mm, v(36.36, -1.8) * mm, v(36.15, -1.9) * mm, v(35.94, -2) * mm]});
            skFitSpline(sketch, "E579", {"points": [v(35.94, -2) * mm, v(35.71, -2.12) * mm, v(35.47, -2.2) * mm, v(35.25, -2.33) * mm]});
            skFitSpline(sketch, "E580", {"points": [v(35.25, -2.33) * mm, v(34.95, -2.49) * mm, v(34.69, -2.43) * mm, v(34.45, -2.23) * mm]});
            skFitSpline(sketch, "E581", {"points": [v(34.45, -2.23) * mm, v(34.17, -2) * mm, v(33.9, -1.76) * mm, v(33.65, -1.51) * mm]});
            skFitSpline(sketch, "E582", {"points": [v(33.65, -1.51) * mm, v(33.35, -1.22) * mm, v(33.07, -0.9) * mm, v(32.8, -0.6) * mm]});
            skFitSpline(sketch, "E583", {"points": [v(32.8, -0.6) * mm, v(32.72, -0.52) * mm, v(32.64, -0.5) * mm, v(32.54, -0.5) * mm]});
            skFitSpline(sketch, "E584", {"points": [v(32.54, -0.5) * mm, v(32.06, -0.52) * mm, v(31.58, -0.53) * mm, v(31.1, -0.54) * mm]});
            skFitSpline(sketch, "E585", {"points": [v(31.1, -0.54) * mm, v(30.8, -0.54) * mm, v(30.5, -0.54) * mm, v(30.2, -0.54) * mm]});
            skFitSpline(sketch, "E586", {"points": [v(30.2, -0.54) * mm, v(30, -0.54) * mm, v(29.81, -0.54) * mm, v(29.6, -0.54) * mm]});
            skFitSpline(sketch, "E587", {"points": [v(29.6, -0.54) * mm, v(29.57, -0.76) * mm, v(29.48, -0.94) * mm, v(29.32, -1.08) * mm]});
            skFitSpline(sketch, "E588", {"points": [v(29.32, -1.08) * mm, v(29.05, -1.32) * mm, v(28.73, -1.35) * mm, v(28.4, -1.34) * mm]});
            skFitSpline(sketch, "E589", {"points": [v(28.4, -1.34) * mm, v(28.1, -1.33) * mm, v(27.82, -1.21) * mm, v(27.56, -1.08) * mm]});
            skFitSpline(sketch, "E590", {"points": [v(27.56, -1.08) * mm, v(27.32, -0.96) * mm, v(27.15, -0.77) * mm, v(27.09, -0.5) * mm]});
            skLineSegment(sketch, "E591", {"start": v(27.09, -0.5) * mm, "end": v(26.46, -0.5) * mm});
            skFitSpline(sketch, "E592", {"points": [v(26.46, -0.5) * mm, v(26.6, -1.02) * mm, v(26.72, -1.53) * mm, v(26.85, -2.04) * mm]});
            skFitSpline(sketch, "E593", {"points": [v(26.85, -2.04) * mm, v(26.98, -2.54) * mm, v(27.11, -3.05) * mm, v(27.25, -3.58) * mm]});
            skFitSpline(sketch, "E594", {"points": [v(27.25, -3.58) * mm, v(27.32, -3.57) * mm, v(27.39, -3.57) * mm, v(27.45, -3.55) * mm]});
            skFitSpline(sketch, "E595", {"points": [v(27.45, -3.55) * mm, v(28.24, -3.34) * mm, v(29.02, -3.13) * mm, v(29.8, -2.9) * mm]});
            skFitSpline(sketch, "E596", {"points": [v(29.8, -2.9) * mm, v(30.29, -2.77) * mm, v(30.76, -2.63) * mm, v(31.24, -2.5) * mm]});
            skFitSpline(sketch, "E597", {"points": [v(31.24, -2.5) * mm, v(31.4, -2.45) * mm, v(31.58, -2.43) * mm, v(31.75, -2.43) * mm]});
            skFitSpline(sketch, "E598", {"points": [v(31.75, -2.43) * mm, v(32, -2.43) * mm, v(32.2, -2.66) * mm, v(32.21, -2.9) * mm]});
            skFitSpline(sketch, "E599", {"points": [v(32.21, -2.9) * mm, v(32.22, -3.12) * mm, v(32.04, -3.33) * mm, v(31.82, -3.38) * mm]});
            skFitSpline(sketch, "E600", {"points": [v(31.82, -3.38) * mm, v(31.35, -3.5) * mm, v(30.9, -3.62) * mm, v(30.43, -3.74) * mm]});
            skFitSpline(sketch, "E601", {"points": [v(30.43, -3.74) * mm, v(30.3, -3.77) * mm, v(30.19, -3.82) * mm, v(30.06, -3.86) * mm]});
            skFitSpline(sketch, "E602", {"points": [v(30.06, -3.86) * mm, v(30.1, -4.29) * mm, v(30.13, -4.71) * mm, v(30.17, -5.16) * mm]});
            skFitSpline(sketch, "E603", {"points": [v(30.17, -5.16) * mm, v(30.3, -5.1) * mm, v(30.44, -5.05) * mm, v(30.57, -5) * mm]});
            skFitSpline(sketch, "E604", {"points": [v(30.57, -5) * mm, v(30.8, -4.9) * mm, v(31.04, -4.83) * mm, v(31.28, -4.73) * mm]});
            skFitSpline(sketch, "E605", {"points": [v(31.28, -4.73) * mm, v(31.73, -4.54) * mm, v(32.17, -4.34) * mm, v(32.62, -4.16) * mm]});
            skFitSpline(sketch, "E606", {"points": [v(32.62, -4.16) * mm, v(32.7, -4.12) * mm, v(32.79, -4.1) * mm, v(32.87, -4.09) * mm]});
            skFitSpline(sketch, "E607", {"points": [v(32.87, -4.09) * mm, v(33.14, -4.07) * mm, v(33.3, -4.18) * mm, v(33.38, -4.42) * mm]});
            skFitSpline(sketch, "E608", {"points": [v(33.38, -4.42) * mm, v(33.45, -4.64) * mm, v(33.36, -4.88) * mm, v(33.14, -4.99) * mm]});
            skFitSpline(sketch, "E609", {"points": [v(33.14, -4.99) * mm, v(32.94, -5.09) * mm, v(32.73, -5.17) * mm, v(32.53, -5.26) * mm]});
            skFitSpline(sketch, "E610", {"points": [v(32.53, -5.26) * mm, v(32.36, -5.33) * mm, v(32.2, -5.4) * mm, v(32, -5.5) * mm]});
            skFitSpline(sketch, "E611", {"points": [v(32, -5.5) * mm, v(32.27, -5.73) * mm, v(32.2, -6.05) * mm, v(32.29, -6.35) * mm]});
            skFitSpline(sketch, "E612", {"points": [v(32.29, -6.35) * mm, v(32.38, -6.32) * mm, v(32.48, -6.29) * mm, v(32.57, -6.25) * mm]});
            skFitSpline(sketch, "E613", {"points": [v(32.57, -6.25) * mm, v(33.07, -6.02) * mm, v(33.57, -5.79) * mm, v(34.08, -5.57) * mm]});
            skFitSpline(sketch, "E614", {"points": [v(34.08, -5.57) * mm, v(34.31, -5.47) * mm, v(34.56, -5.4) * mm, v(34.8, -5.33) * mm]});
            skFitSpline(sketch, "E615", {"points": [v(34.8, -5.33) * mm, v(34.93, -5.3) * mm, v(35.08, -5.3) * mm, v(35.2, -5.34) * mm]});
            skFitSpline(sketch, "E616", {"points": [v(35.2, -5.34) * mm, v(35.38, -5.4) * mm, v(35.48, -5.55) * mm, v(35.5, -5.74) * mm]});
            skFitSpline(sketch, "E617", {"points": [v(35.5, -5.74) * mm, v(35.5, -5.95) * mm, v(35.41, -6.1) * mm, v(35.24, -6.2) * mm]});
            skFitSpline(sketch, "E618", {"points": [v(35.24, -6.2) * mm, v(35.13, -6.26) * mm, v(35, -6.28) * mm, v(34.88, -6.33) * mm]});
            skFitSpline(sketch, "E619", {"points": [v(34.88, -6.33) * mm, v(34.51, -6.47) * mm, v(34.15, -6.6) * mm, v(33.79, -6.76) * mm]});
            skFitSpline(sketch, "E620", {"points": [v(33.79, -6.76) * mm, v(33.32, -6.96) * mm, v(32.86, -7.18) * mm, v(32.37, -7.4) * mm]});
            skFitSpline(sketch, "E621", {"points": [v(32.37, -7.4) * mm, v(32.38, -7.51) * mm, v(32.4, -7.64) * mm, v(32.42, -7.78) * mm]});
            skFitSpline(sketch, "E622", {"points": [v(32.42, -7.78) * mm, v(32.46, -8.18) * mm, v(32.52, -8.58) * mm, v(32.54, -8.99) * mm]});
            skFitSpline(sketch, "E623", {"points": [v(32.54, -8.99) * mm, v(32.56, -9.45) * mm, v(32.67, -9.89) * mm, v(32.76, -10.33) * mm]});
            skFitSpline(sketch, "E624", {"points": [v(32.76, -10.33) * mm, v(32.78, -10.4) * mm, v(32.79, -10.48) * mm, v(32.78, -10.54) * mm]});
            skFitSpline(sketch, "E625", {"points": [v(32.78, -10.54) * mm, v(32.74, -10.77) * mm, v(32.55, -10.94) * mm, v(32.34, -10.96) * mm]});
            skFitSpline(sketch, "E626", {"points": [v(32.34, -10.96) * mm, v(32.14, -10.98) * mm, v(31.9, -10.84) * mm, v(31.85, -10.62) * mm]});
            skFitSpline(sketch, "E627", {"points": [v(31.85, -10.62) * mm, v(31.77, -10.34) * mm, v(31.7, -10.05) * mm, v(31.66, -9.76) * mm]});
            skFitSpline(sketch, "E628", {"points": [v(31.66, -9.76) * mm, v(31.59, -9.26) * mm, v(31.55, -8.76) * mm, v(31.5, -8.26) * mm]});
            skFitSpline(sketch, "E629", {"points": [v(31.5, -8.26) * mm, v(31.49, -8.12) * mm, v(31.47, -7.99) * mm, v(31.45, -7.84) * mm]});
            skFitSpline(sketch, "E630", {"points": [v(31.45, -7.84) * mm, v(31.15, -7.87) * mm, v(30.9, -8.15) * mm, v(30.55, -7.99) * mm]});
            skFitSpline(sketch, "E631", {"points": [v(30.55, -7.99) * mm, v(30.57, -8.18) * mm, v(30.58, -8.34) * mm, v(30.6, -8.5) * mm]});
            skFitSpline(sketch, "E632", {"points": [v(30.6, -8.5) * mm, v(30.62, -8.72) * mm, v(30.66, -8.95) * mm, v(30.68, -9.18) * mm]});
            skFitSpline(sketch, "E633", {"points": [v(30.68, -9.18) * mm, v(30.68, -9.26) * mm, v(30.68, -9.34) * mm, v(30.66, -9.42) * mm]});
            skFitSpline(sketch, "E634", {"points": [v(30.66, -9.42) * mm, v(30.6, -9.62) * mm, v(30.38, -9.77) * mm, v(30.19, -9.76) * mm]});
            skFitSpline(sketch, "E635", {"points": [v(30.19, -9.76) * mm, v(29.98, -9.76) * mm, v(29.77, -9.6) * mm, v(29.73, -9.37) * mm]});
            skFitSpline(sketch, "E636", {"points": [v(29.73, -9.37) * mm, v(29.69, -9.11) * mm, v(29.66, -8.85) * mm, v(29.63, -8.59) * mm]});
            skFitSpline(sketch, "E637", {"points": [v(29.63, -8.59) * mm, v(29.57, -8.2) * mm, v(29.51, -7.82) * mm, v(29.46, -7.43) * mm]});
            skFitSpline(sketch, "E638", {"points": [v(29.46, -7.43) * mm, v(29.43, -7.21) * mm, v(29.41, -6.99) * mm, v(29.39, -6.77) * mm]});
            skFitSpline(sketch, "E639", {"points": [v(29.39, -6.77) * mm, v(29.38, -6.71) * mm, v(29.37, -6.66) * mm, v(29.35, -6.59) * mm]});
            skFitSpline(sketch, "E640", {"points": [v(29.35, -6.59) * mm, v(28.95, -6.78) * mm, v(28.56, -6.96) * mm, v(28.16, -7.15) * mm]});
            skFitSpline(sketch, "E641", {"points": [v(28.16, -7.15) * mm, v(28.26, -7.56) * mm, v(28.36, -7.99) * mm, v(28.47, -8.41) * mm]});
            skFitSpline(sketch, "E642", {"points": [v(28.47, -8.41) * mm, v(28.51, -8.57) * mm, v(28.56, -8.72) * mm, v(28.62, -8.87) * mm]});
            skFitSpline(sketch, "E643", {"points": [v(28.62, -8.87) * mm, v(28.7, -9.11) * mm, v(28.62, -9.37) * mm, v(28.4, -9.48) * mm]});
            skFitSpline(sketch, "E644", {"points": [v(28.4, -9.48) * mm, v(28.18, -9.6) * mm, v(27.9, -9.53) * mm, v(27.76, -9.32) * mm]});
            skFitSpline(sketch, "E645", {"points": [v(27.76, -9.32) * mm, v(27.68, -9.19) * mm, v(27.63, -9.04) * mm, v(27.59, -8.9) * mm]});
            skFitSpline(sketch, "E646", {"points": [v(27.59, -8.9) * mm, v(27.5, -8.58) * mm, v(27.42, -8.25) * mm, v(27.34, -7.92) * mm]});
            skFitSpline(sketch, "E647", {"points": [v(27.34, -7.92) * mm, v(27.12, -7.08) * mm, v(26.9, -6.24) * mm, v(26.68, -5.4) * mm]});
            skFitSpline(sketch, "E648", {"points": [v(26.68, -5.4) * mm, v(26.64, -5.22) * mm, v(26.6, -5.04) * mm, v(26.54, -4.84) * mm]});
            skFitSpline(sketch, "E649", {"points": [v(26.54, -4.84) * mm, v(25.5, -5.13) * mm, v(24.5, -5.4) * mm, v(23.45, -5.7) * mm]});
            skFitSpline(sketch, "E650", {"points": [v(23.45, -5.7) * mm, v(23.56, -5.88) * mm, v(23.65, -6.06) * mm, v(23.74, -6.2) * mm]});
            skFitSpline(sketch, "E651", {"points": [v(23.74, -6.2) * mm, v(23.93, -6.22) * mm, v(24.1, -6.2) * mm, v(24.26, -6.26) * mm]});
            skFitSpline(sketch, "E652", {"points": [v(24.26, -6.26) * mm, v(24.7, -6.42) * mm, v(25.03, -6.73) * mm, v(25.26, -7.14) * mm]});
            skFitSpline(sketch, "E653", {"points": [v(25.26, -7.14) * mm, v(25.4, -7.4) * mm, v(25.43, -7.64) * mm, v(25.38, -7.93) * mm]});
            skFitSpline(sketch, "E654", {"points": [v(25.38, -7.93) * mm, v(25.34, -8.14) * mm, v(25.21, -8.27) * mm, v(25.07, -8.4) * mm]});
            skFitSpline(sketch, "E655", {"points": [v(25.07, -8.4) * mm, v(25.36, -8.9) * mm, v(25.65, -9.4) * mm, v(25.93, -9.9) * mm]});
            skFitSpline(sketch, "E656", {"points": [v(25.93, -9.9) * mm, v(26.1, -10.19) * mm, v(26.24, -10.48) * mm, v(26.39, -10.77) * mm]});
            skFitSpline(sketch, "E657", {"points": [v(26.39, -10.77) * mm, v(26.5, -10.97) * mm, v(26.6, -11.14) * mm, v(26.87, -11.18) * mm]});
            skFitSpline(sketch, "E658", {"points": [v(26.87, -11.18) * mm, v(27.2, -11.22) * mm, v(27.53, -11.31) * mm, v(27.85, -11.4) * mm]});
            skFitSpline(sketch, "E659", {"points": [v(27.85, -11.4) * mm, v(28.23, -11.5) * mm, v(28.6, -11.63) * mm, v(28.97, -11.76) * mm]});
            skFitSpline(sketch, "E660", {"points": [v(28.97, -11.76) * mm, v(29.27, -11.87) * mm, v(29.42, -12.1) * mm, v(29.43, -12.42) * mm]});
            skFitSpline(sketch, "E661", {"points": [v(29.43, -12.42) * mm, v(29.46, -12.8) * mm, v(29.5, -13.18) * mm, v(29.52, -13.56) * mm]});
            skFitSpline(sketch, "E662", {"points": [v(29.52, -13.56) * mm, v(29.53, -13.73) * mm, v(29.5, -13.9) * mm, v(29.5, -14.06) * mm]});
            skFitSpline(sketch, "E663", {"points": [v(29.5, -14.06) * mm, v(29.47, -14.6) * mm, v(29.43, -15.16) * mm, v(29.4, -15.7) * mm]});
            skFitSpline(sketch, "E664", {"points": [v(29.4, -15.7) * mm, v(29.4, -15.93) * mm, v(29.28, -16.06) * mm, v(29.09, -16.15) * mm]});
            skFitSpline(sketch, "E665", {"points": [v(29.09, -16.15) * mm, v(29, -16.18) * mm, v(28.92, -16.22) * mm, v(28.84, -16.28) * mm]});
            skFitSpline(sketch, "E666", {"points": [v(28.84, -16.28) * mm, v(28.66, -16.43) * mm, v(28.47, -16.45) * mm, v(28.27, -16.35) * mm]});
            skFitSpline(sketch, "E667", {"points": [v(28.27, -16.35) * mm, v(27.72, -16.07) * mm, v(27.16, -15.8) * mm, v(26.62, -15.52) * mm]});
            skFitSpline(sketch, "E668", {"points": [v(26.62, -15.52) * mm, v(26.36, -15.39) * mm, v(26.13, -15.22) * mm, v(25.89, -15.06) * mm]});
            skFitSpline(sketch, "E669", {"points": [v(25.89, -15.06) * mm, v(25.73, -14.95) * mm, v(25.58, -14.82) * mm, v(25.42, -14.73) * mm]});
            skFitSpline(sketch, "E670", {"points": [v(25.42, -14.73) * mm, v(25.1, -14.54) * mm, v(25.03, -14.25) * mm, v(25.1, -13.92) * mm]});
            skFitSpline(sketch, "E671", {"points": [v(25.1, -13.92) * mm, v(25.18, -13.47) * mm, v(25.26, -13.03) * mm, v(25.42, -12.6) * mm]});
            skFitSpline(sketch, "E672", {"points": [v(25.42, -12.6) * mm, v(25.52, -12.31) * mm, v(25.6, -12.02) * mm, v(25.67, -11.73) * mm]});
            skFitSpline(sketch, "E673", {"points": [v(25.67, -11.73) * mm, v(25.7, -11.66) * mm, v(25.68, -11.56) * mm, v(25.64, -11.5) * mm]});
            skFitSpline(sketch, "E674", {"points": [v(25.64, -11.5) * mm, v(25.53, -11.3) * mm, v(25.4, -11.13) * mm, v(25.3, -10.93) * mm]});
            skFitSpline(sketch, "E675", {"points": [v(25.3, -10.93) * mm, v(24.92, -10.3) * mm, v(24.56, -9.68) * mm, v(24.2, -9.05) * mm]});
            skFitSpline(sketch, "E676", {"points": [v(24.2, -9.05) * mm, v(24.18, -9.02) * mm, v(24.16, -9) * mm, v(24.14, -8.97) * mm]});
            skFitSpline(sketch, "E677", {"points": [v(24.14, -8.97) * mm, v(24.12, -8.96) * mm, v(24.1, -8.96) * mm, v(24.07, -8.96) * mm]});
            skFitSpline(sketch, "E678", {"points": [v(24.07, -8.96) * mm, v(23.66, -9.08) * mm, v(23.3, -8.95) * mm, v(23.04, -8.61) * mm]});
            skFitSpline(sketch, "E679", {"points": [v(23.04, -8.61) * mm, v(22.76, -8.26) * mm, v(22.68, -7.85) * mm, v(22.64, -7.43) * mm]});
            skFitSpline(sketch, "E680", {"points": [v(22.64, -7.43) * mm, v(22.62, -7.21) * mm, v(22.7, -7) * mm, v(22.9, -6.72) * mm]});
            skFitSpline(sketch, "E681", {"points": [v(22.9, -6.72) * mm, v(22.8, -6.55) * mm, v(22.7, -6.38) * mm, v(22.6, -6.2) * mm]});
            skFitSpline(sketch, "E682", {"points": [v(22.6, -6.2) * mm, v(21.83, -6.94) * mm, v(21.08, -7.68) * mm, v(20.32, -8.43) * mm]});
            skFitSpline(sketch, "E683", {"points": [v(20.32, -8.43) * mm, v(20.36, -8.48) * mm, v(20.4, -8.53) * mm, v(20.44, -8.57) * mm]});
            skFitSpline(sketch, "E684", {"points": [v(20.44, -8.57) * mm, v(20.9, -9.02) * mm, v(21.34, -9.46) * mm, v(21.79, -9.9) * mm]});
            skFitSpline(sketch, "E685", {"points": [v(21.79, -9.9) * mm, v(22.28, -10.39) * mm, v(22.78, -10.86) * mm, v(23.27, -11.34) * mm]});
            skFitSpline(sketch, "E686", {"points": [v(23.27, -11.34) * mm, v(23.37, -11.44) * mm, v(23.47, -11.55) * mm, v(23.54, -11.67) * mm]});
            skFitSpline(sketch, "E687", {"points": [v(23.54, -11.67) * mm, v(23.73, -11.97) * mm, v(23.6, -12.3) * mm, v(23.3, -12.42) * mm]});
            skFitSpline(sketch, "E688", {"points": [v(23.3, -12.42) * mm, v(23.1, -12.5) * mm, v(22.91, -12.41) * mm, v(22.74, -12.23) * mm]});
            skFitSpline(sketch, "E689", {"points": [v(22.74, -12.23) * mm, v(22.34, -11.8) * mm, v(21.92, -11.4) * mm, v(21.5, -10.99) * mm]});
            skFitSpline(sketch, "E690", {"points": [v(21.5, -10.99) * mm, v(21.13, -11.25) * mm, v(20.78, -11.5) * mm, v(20.41, -11.75) * mm]});
            skFitSpline(sketch, "E691", {"points": [v(20.41, -11.75) * mm, v(20.51, -11.82) * mm, v(20.6, -11.89) * mm, v(20.7, -11.96) * mm]});
            skFitSpline(sketch, "E692", {"points": [v(20.7, -11.96) * mm, v(21.18, -12.34) * mm, v(21.67, -12.73) * mm, v(22.16, -13.1) * mm]});
            skFitSpline(sketch, "E693", {"points": [v(22.16, -13.1) * mm, v(22.3, -13.22) * mm, v(22.45, -13.3) * mm, v(22.59, -13.42) * mm]});
            skFitSpline(sketch, "E694", {"points": [v(22.59, -13.42) * mm, v(22.83, -13.61) * mm, v(22.87, -13.89) * mm, v(22.7, -14.11) * mm]});
            skFitSpline(sketch, "E695", {"points": [v(22.7, -14.11) * mm, v(22.54, -14.33) * mm, v(22.25, -14.37) * mm, v(22, -14.19) * mm]});
            skFitSpline(sketch, "E696", {"points": [v(22, -14.19) * mm, v(21.75, -14.01) * mm, v(21.5, -13.83) * mm, v(21.26, -13.65) * mm]});
            skFitSpline(sketch, "E697", {"points": [v(21.26, -13.65) * mm, v(21.2, -13.6) * mm, v(21.14, -13.56) * mm, v(21.04, -13.5) * mm]});
            skFitSpline(sketch, "E698", {"points": [v(21.04, -13.5) * mm, v(20.98, -13.84) * mm, v(20.67, -13.95) * mm, v(20.45, -14.16) * mm]});
            skFitSpline(sketch, "E699", {"points": [v(20.45, -14.16) * mm, v(20.5, -14.2) * mm, v(20.52, -14.24) * mm, v(20.57, -14.27) * mm]});
            skFitSpline(sketch, "E700", {"points": [v(20.57, -14.27) * mm, v(20.85, -14.48) * mm, v(21.13, -14.7) * mm, v(21.43, -14.89) * mm]});
            skFitSpline(sketch, "E701", {"points": [v(21.43, -14.89) * mm, v(21.85, -15.17) * mm, v(22.25, -15.5) * mm, v(22.6, -15.86) * mm]});
            skFitSpline(sketch, "E702", {"points": [v(22.6, -15.86) * mm, v(22.68, -15.94) * mm, v(22.74, -16.04) * mm, v(22.77, -16.15) * mm]});
            skFitSpline(sketch, "E703", {"points": [v(22.77, -16.15) * mm, v(22.82, -16.35) * mm, v(22.73, -16.54) * mm, v(22.57, -16.65) * mm]});
            skFitSpline(sketch, "E704", {"points": [v(22.57, -16.65) * mm, v(22.39, -16.76) * mm, v(22.2, -16.75) * mm, v(22.03, -16.63) * mm]});
            skFitSpline(sketch, "E705", {"points": [v(22.03, -16.63) * mm, v(21.93, -16.56) * mm, v(21.85, -16.47) * mm, v(21.75, -16.4) * mm]});
            skFitSpline(sketch, "E706", {"points": [v(21.75, -16.4) * mm, v(21.45, -16.15) * mm, v(21.15, -15.9) * mm, v(20.84, -15.67) * mm]});
            skFitSpline(sketch, "E707", {"points": [v(20.84, -15.67) * mm, v(20.51, -15.42) * mm, v(20.18, -15.19) * mm, v(19.85, -14.95) * mm]});
            skFitSpline(sketch, "E708", {"points": [v(19.85, -14.95) * mm, v(19.76, -14.89) * mm, v(19.68, -14.82) * mm, v(19.6, -14.75) * mm]});
            skFitSpline(sketch, "E709", {"points": [v(19.6, -14.75) * mm, v(19.48, -14.84) * mm, v(19.38, -14.93) * mm, v(19.27, -15) * mm]});
            skFitSpline(sketch, "E710", {"points": [v(19.27, -15) * mm, v(18.94, -15.25) * mm, v(18.6, -15.47) * mm, v(18.28, -15.72) * mm]});
            skFitSpline(sketch, "E711", {"points": [v(18.28, -15.72) * mm, v(17.94, -15.98) * mm, v(17.62, -16.25) * mm, v(17.3, -16.52) * mm]});
            skFitSpline(sketch, "E712", {"points": [v(17.3, -16.52) * mm, v(17.25, -16.56) * mm, v(17.21, -16.6) * mm, v(17.17, -16.63) * mm]});
            skFitSpline(sketch, "E713", {"points": [v(17.17, -16.63) * mm, v(16.96, -16.77) * mm, v(16.7, -16.75) * mm, v(16.53, -16.57) * mm]});
            skFitSpline(sketch, "E714", {"points": [v(16.53, -16.57) * mm, v(16.37, -16.4) * mm, v(16.35, -16.13) * mm, v(16.52, -15.94) * mm]});
            skFitSpline(sketch, "E715", {"points": [v(16.52, -15.94) * mm, v(16.7, -15.74) * mm, v(16.9, -15.55) * mm, v(17.11, -15.38) * mm]});
            skFitSpline(sketch, "E716", {"points": [v(17.11, -15.38) * mm, v(17.57, -15.03) * mm, v(18.04, -14.7) * mm, v(18.5, -14.36) * mm]});
            skFitSpline(sketch, "E717", {"points": [v(18.5, -14.36) * mm, v(18.58, -14.3) * mm, v(18.66, -14.25) * mm, v(18.75, -14.17) * mm]});
            skFitSpline(sketch, "E718", {"points": [v(107.4, -18.65) * mm, v(107.59, -18.4) * mm, v(107.76, -18.2) * mm, v(107.93, -17.97) * mm]});
            skFitSpline(sketch, "E719", {"points": [v(107.93, -17.97) * mm, v(108.13, -17.68) * mm, v(108.34, -17.38) * mm, v(108.53, -17.08) * mm]});
            skFitSpline(sketch, "E720", {"points": [v(108.53, -17.08) * mm, v(108.8, -16.67) * mm, v(109.07, -16.27) * mm, v(109.33, -15.86) * mm]});
            skFitSpline(sketch, "E721", {"points": [v(109.33, -15.86) * mm, v(109.43, -15.7) * mm, v(109.53, -15.53) * mm, v(109.63, -15.37) * mm]});
            skFitSpline(sketch, "E722", {"points": [v(109.63, -15.37) * mm, v(109.69, -15.27) * mm, v(109.7, -15.18) * mm, v(109.64, -15.07) * mm]});
            skFitSpline(sketch, "E723", {"points": [v(109.64, -15.07) * mm, v(109.47, -14.71) * mm, v(109.32, -14.34) * mm, v(109.13, -14) * mm]});
            skFitSpline(sketch, "E724", {"points": [v(109.13, -14) * mm, v(108.74, -13.3) * mm, v(108.33, -12.6) * mm, v(107.95, -11.91) * mm]});
            skFitSpline(sketch, "E725", {"points": [v(107.95, -11.91) * mm, v(107.8, -11.65) * mm, v(107.68, -11.37) * mm, v(107.55, -11.1) * mm]});
            skFitSpline(sketch, "E726", {"points": [v(107.55, -11.1) * mm, v(107.5, -11) * mm, v(107.47, -10.91) * mm, v(107.41, -10.79) * mm]});
            skFitSpline(sketch, "E727", {"points": [v(107.41, -10.79) * mm, v(107.36, -10.87) * mm, v(107.33, -10.92) * mm, v(107.32, -10.97) * mm]});
            skFitSpline(sketch, "E728", {"points": [v(107.32, -10.97) * mm, v(107.11, -11.54) * mm, v(106.8, -12.05) * mm, v(106.5, -12.56) * mm]});
            skFitSpline(sketch, "E729", {"points": [v(106.5, -12.56) * mm, v(106.03, -13.36) * mm, v(105.55, -14.16) * mm, v(105.2, -15.01) * mm]});
            skFitSpline(sketch, "E730", {"points": [v(105.2, -15.01) * mm, v(105.13, -15.16) * mm, v(105.12, -15.28) * mm, v(105.2, -15.41) * mm]});
            skFitSpline(sketch, "E731", {"points": [v(105.2, -15.41) * mm, v(105.3, -15.57) * mm, v(105.4, -15.73) * mm, v(105.5, -15.88) * mm]});
            skFitSpline(sketch, "E732", {"points": [v(105.5, -15.88) * mm, v(105.74, -16.25) * mm, v(106, -16.61) * mm, v(106.22, -17) * mm]});
            skFitSpline(sketch, "E733", {"points": [v(106.22, -17) * mm, v(106.54, -17.6) * mm, v(107, -18.08) * mm, v(107.4, -18.65) * mm]});
            skFitSpline(sketch, "E734", {"points": [v(107.4, 10.79) * mm, v(107.45, 10.87) * mm, v(107.48, 10.92) * mm, v(107.5, 10.97) * mm]});
            skFitSpline(sketch, "E735", {"points": [v(107.5, 10.97) * mm, v(107.7, 11.53) * mm, v(108.01, 12.03) * mm, v(108.31, 12.54) * mm]});
            skFitSpline(sketch, "E736", {"points": [v(108.31, 12.54) * mm, v(108.78, 13.34) * mm, v(109.25, 14.14) * mm, v(109.61, 15) * mm]});
            skFitSpline(sketch, "E737", {"points": [v(109.61, 15) * mm, v(109.68, 15.15) * mm, v(109.7, 15.28) * mm, v(109.6, 15.42) * mm]});
            skFitSpline(sketch, "E738", {"points": [v(109.6, 15.42) * mm, v(109.5, 15.57) * mm, v(109.41, 15.72) * mm, v(109.32, 15.86) * mm]});
            skFitSpline(sketch, "E739", {"points": [v(109.32, 15.86) * mm, v(109.15, 16.1) * mm, v(108.96, 16.34) * mm, v(108.81, 16.6) * mm]});
            skFitSpline(sketch, "E740", {"points": [v(108.81, 16.6) * mm, v(108.48, 17.17) * mm, v(108.14, 17.74) * mm, v(107.7, 18.24) * mm]});
            skFitSpline(sketch, "E741", {"points": [v(107.7, 18.24) * mm, v(107.6, 18.36) * mm, v(107.52, 18.5) * mm, v(107.4, 18.64) * mm]});
            skFitSpline(sketch, "E742", {"points": [v(107.4, 18.64) * mm, v(107.23, 18.41) * mm, v(107.08, 18.2) * mm, v(106.91, 18) * mm]});
            skFitSpline(sketch, "E743", {"points": [v(106.91, 18) * mm, v(106.66, 17.69) * mm, v(106.44, 17.36) * mm, v(106.24, 17.01) * mm]});
            skFitSpline(sketch, "E744", {"points": [v(106.24, 17.01) * mm, v(106, 16.63) * mm, v(105.75, 16.26) * mm, v(105.5, 15.89) * mm]});
            skFitSpline(sketch, "E745", {"points": [v(105.5, 15.89) * mm, v(105.43, 15.77) * mm, v(105.36, 15.64) * mm, v(105.27, 15.53) * mm]});
            skFitSpline(sketch, "E746", {"points": [v(105.27, 15.53) * mm, v(105.1, 15.32) * mm, v(105.1, 15.1) * mm, v(105.25, 14.9) * mm]});
            skFitSpline(sketch, "E747", {"points": [v(105.25, 14.9) * mm, v(105.28, 14.85) * mm, v(105.3, 14.79) * mm, v(105.32, 14.74) * mm]});
            skFitSpline(sketch, "E748", {"points": [v(105.32, 14.74) * mm, v(105.56, 14.25) * mm, v(105.8, 13.76) * mm, v(106.06, 13.29) * mm]});
            skFitSpline(sketch, "E749", {"points": [v(106.06, 13.29) * mm, v(106.48, 12.54) * mm, v(106.98, 11.83) * mm, v(107.29, 11.02) * mm]});
            skFitSpline(sketch, "E750", {"points": [v(107.29, 11.02) * mm, v(107.31, 10.95) * mm, v(107.35, 10.89) * mm, v(107.4, 10.79) * mm]});
            skFitSpline(sketch, "E751", {"points": [v(123.55, -9.33) * mm, v(123.38, -8.92) * mm, v(123.22, -8.53) * mm, v(123.06, -8.14) * mm]});
            skFitSpline(sketch, "E752", {"points": [v(123.06, -8.14) * mm, v(123.02, -8.03) * mm, v(122.97, -7.93) * mm, v(122.91, -7.84) * mm]});
            skFitSpline(sketch, "E753", {"points": [v(122.91, -7.84) * mm, v(122.59, -7.3) * mm, v(122.3, -6.74) * mm, v(122.05, -6.16) * mm]});
            skFitSpline(sketch, "E754", {"points": [v(122.05, -6.16) * mm, v(122.02, -6.1) * mm, v(121.98, -6.05) * mm, v(121.96, -5.99) * mm]});
            skFitSpline(sketch, "E755", {"points": [v(121.96, -5.99) * mm, v(121.84, -5.71) * mm, v(121.67, -5.54) * mm, v(121.34, -5.6) * mm]});
            skFitSpline(sketch, "E756", {"points": [v(121.34, -5.6) * mm, v(121.32, -5.6) * mm, v(121.3, -5.59) * mm, v(121.3, -5.58) * mm]});
            skFitSpline(sketch, "E757", {"points": [v(121.3, -5.58) * mm, v(120.89, -5.56) * mm, v(120.48, -5.5) * mm, v(120.08, -5.5) * mm]});
            skFitSpline(sketch, "E758", {"points": [v(120.08, -5.5) * mm, v(119.43, -5.49) * mm, v(118.78, -5.5) * mm, v(118.14, -5.5) * mm]});
            skFitSpline(sketch, "E759", {"points": [v(118.14, -5.5) * mm, v(117.77, -5.48) * mm, v(117.4, -5.44) * mm, v(117.02, -5.4) * mm]});
            skFitSpline(sketch, "E760", {"points": [v(117.02, -5.4) * mm, v(116.94, -5.4) * mm, v(116.87, -5.4) * mm, v(116.75, -5.4) * mm]});
            skFitSpline(sketch, "E761", {"points": [v(116.75, -5.4) * mm, v(116.82, -5.5) * mm, v(116.86, -5.57) * mm, v(116.91, -5.64) * mm]});
            skFitSpline(sketch, "E762", {"points": [v(116.91, -5.64) * mm, v(117.11, -5.94) * mm, v(117.33, -6.23) * mm, v(117.51, -6.54) * mm]});
            skFitSpline(sketch, "E763", {"points": [v(117.51, -6.54) * mm, v(117.78, -6.98) * mm, v(118, -7.45) * mm, v(118.28, -7.89) * mm]});
            skFitSpline(sketch, "E764", {"points": [v(118.28, -7.89) * mm, v(118.62, -8.42) * mm, v(118.98, -8.94) * mm, v(119.32, -9.46) * mm]});
            skFitSpline(sketch, "E765", {"points": [v(119.32, -9.46) * mm, v(119.4, -9.58) * mm, v(119.5, -9.62) * mm, v(119.63, -9.62) * mm]});
            skFitSpline(sketch, "E766", {"points": [v(119.63, -9.62) * mm, v(119.83, -9.62) * mm, v(120.03, -9.6) * mm, v(120.22, -9.6) * mm]});
            skFitSpline(sketch, "E767", {"points": [v(120.22, -9.6) * mm, v(120.63, -9.58) * mm, v(121.04, -9.55) * mm, v(121.44, -9.53) * mm]});
            skFitSpline(sketch, "E768", {"points": [v(121.44, -9.53) * mm, v(121.78, -9.5) * mm, v(122.13, -9.5) * mm, v(122.47, -9.47) * mm]});
            skFitSpline(sketch, "E769", {"points": [v(122.47, -9.47) * mm, v(122.82, -9.44) * mm, v(123.18, -9.38) * mm, v(123.55, -9.33) * mm]});
            skFitSpline(sketch, "E770", {"points": [v(91.24, -9.33) * mm, v(91.47, -9.36) * mm, v(91.66, -9.38) * mm, v(91.84, -9.4) * mm]});
            skFitSpline(sketch, "E771", {"points": [v(91.84, -9.4) * mm, v(92.37, -9.5) * mm, v(92.91, -9.55) * mm, v(93.46, -9.53) * mm]});
            skFitSpline(sketch, "E772", {"points": [v(93.46, -9.53) * mm, v(93.72, -9.52) * mm, v(93.98, -9.55) * mm, v(94.24, -9.57) * mm]});
            skFitSpline(sketch, "E773", {"points": [v(94.24, -9.57) * mm, v(94.55, -9.58) * mm, v(94.85, -9.6) * mm, v(95.15, -9.62) * mm]});
            skFitSpline(sketch, "E774", {"points": [v(95.15, -9.62) * mm, v(95.3, -9.63) * mm, v(95.42, -9.57) * mm, v(95.5, -9.43) * mm]});
            skFitSpline(sketch, "E775", {"points": [v(95.5, -9.43) * mm, v(95.6, -9.28) * mm, v(95.72, -9.13) * mm, v(95.83, -8.98) * mm]});
            skFitSpline(sketch, "E776", {"points": [v(95.83, -8.98) * mm, v(96.3, -8.33) * mm, v(96.67, -7.6) * mm, v(97.08, -6.91) * mm]});
            skFitSpline(sketch, "E777", {"points": [v(97.08, -6.91) * mm, v(97.34, -6.46) * mm, v(97.59, -6) * mm, v(97.94, -5.6) * mm]});
            skFitSpline(sketch, "E778", {"points": [v(97.94, -5.6) * mm, v(97.98, -5.54) * mm, v(98, -5.48) * mm, v(98.05, -5.4) * mm]});
            skFitSpline(sketch, "E779", {"points": [v(98.05, -5.4) * mm, v(97.94, -5.4) * mm, v(97.86, -5.4) * mm, v(97.78, -5.41) * mm]});
            skFitSpline(sketch, "E780", {"points": [v(97.78, -5.41) * mm, v(97.44, -5.44) * mm, v(97.11, -5.49) * mm, v(96.78, -5.5) * mm]});
            skFitSpline(sketch, "E781", {"points": [v(96.78, -5.5) * mm, v(96.23, -5.5) * mm, v(95.68, -5.47) * mm, v(95.13, -5.48) * mm]});
            skFitSpline(sketch, "E782", {"points": [v(95.13, -5.48) * mm, v(94.51, -5.5) * mm, v(93.9, -5.56) * mm, v(93.29, -5.6) * mm]});
            skFitSpline(sketch, "E783", {"points": [v(93.29, -5.6) * mm, v(93.15, -5.6) * mm, v(93.04, -5.65) * mm, v(92.98, -5.78) * mm]});
            skFitSpline(sketch, "E784", {"points": [v(92.98, -5.78) * mm, v(92.9, -5.92) * mm, v(92.8, -6.06) * mm, v(92.74, -6.22) * mm]});
            skFitSpline(sketch, "E785", {"points": [v(92.74, -6.22) * mm, v(92.5, -6.75) * mm, v(92.21, -7.26) * mm, v(91.94, -7.77) * mm]});
            skFitSpline(sketch, "E786", {"points": [v(91.94, -7.77) * mm, v(91.68, -8.26) * mm, v(91.48, -8.79) * mm, v(91.24, -9.33) * mm]});
            skFitSpline(sketch, "E787", {"points": [v(123.57, 9.32) * mm, v(123.31, 9.35) * mm, v(123.1, 9.38) * mm, v(122.89, 9.4) * mm]});
            skFitSpline(sketch, "E788", {"points": [v(122.89, 9.4) * mm, v(122.43, 9.47) * mm, v(121.97, 9.53) * mm, v(121.5, 9.52) * mm]});
            skFitSpline(sketch, "E789", {"points": [v(121.5, 9.52) * mm, v(121.16, 9.52) * mm, v(120.82, 9.55) * mm, v(120.48, 9.57) * mm]});
            skFitSpline(sketch, "E790", {"points": [v(120.48, 9.57) * mm, v(120.2, 9.58) * mm, v(119.94, 9.6) * mm, v(119.67, 9.61) * mm]});
            skFitSpline(sketch, "E791", {"points": [v(119.67, 9.61) * mm, v(119.53, 9.62) * mm, v(119.42, 9.59) * mm, v(119.33, 9.47) * mm]});
            skFitSpline(sketch, "E792", {"points": [v(119.33, 9.47) * mm, v(119.09, 9.1) * mm, v(118.82, 8.75) * mm, v(118.6, 8.38) * mm]});
            skFitSpline(sketch, "E793", {"points": [v(118.6, 8.38) * mm, v(118.26, 7.83) * mm, v(117.96, 7.27) * mm, v(117.63, 6.73) * mm]});
            skFitSpline(sketch, "E794", {"points": [v(117.63, 6.73) * mm, v(117.4, 6.34) * mm, v(117.14, 5.98) * mm, v(116.9, 5.6) * mm]});
            skFitSpline(sketch, "E795", {"points": [v(116.9, 5.6) * mm, v(116.85, 5.54) * mm, v(116.8, 5.48) * mm, v(116.74, 5.39) * mm]});
            skFitSpline(sketch, "E796", {"points": [v(116.74, 5.39) * mm, v(116.88, 5.4) * mm, v(116.97, 5.4) * mm, v(117.05, 5.4) * mm]});
            skFitSpline(sketch, "E797", {"points": [v(117.05, 5.4) * mm, v(117.56, 5.44) * mm, v(118.07, 5.47) * mm, v(118.58, 5.49) * mm]});
            skFitSpline(sketch, "E798", {"points": [v(118.58, 5.49) * mm, v(118.95, 5.5) * mm, v(119.31, 5.45) * mm, v(119.68, 5.47) * mm]});
            skFitSpline(sketch, "E799", {"points": [v(119.68, 5.47) * mm, v(120.3, 5.5) * mm, v(120.93, 5.55) * mm, v(121.56, 5.59) * mm]});
            skFitSpline(sketch, "E800", {"points": [v(121.56, 5.59) * mm, v(121.67, 5.6) * mm, v(121.76, 5.64) * mm, v(121.82, 5.74) * mm]});
            skFitSpline(sketch, "E801", {"points": [v(121.82, 5.74) * mm, v(121.9, 5.9) * mm, v(122, 6.06) * mm, v(122.08, 6.22) * mm]});
            skFitSpline(sketch, "E802", {"points": [v(122.08, 6.22) * mm, v(122.3, 6.73) * mm, v(122.57, 7.2) * mm, v(122.83, 7.7) * mm]});
            skFitSpline(sketch, "E803", {"points": [v(122.83, 7.7) * mm, v(123.1, 8.2) * mm, v(123.32, 8.75) * mm, v(123.57, 9.32) * mm]});
            skFitSpline(sketch, "E804", {"points": [v(91.26, 9.33) * mm, v(91.37, 9.05) * mm, v(91.46, 8.8) * mm, v(91.58, 8.56) * mm]});
            skFitSpline(sketch, "E805", {"points": [v(91.58, 8.56) * mm, v(91.74, 8.2) * mm, v(91.9, 7.86) * mm, v(92.07, 7.52) * mm]});
            skFitSpline(sketch, "E806", {"points": [v(92.07, 7.52) * mm, v(92.28, 7.1) * mm, v(92.49, 6.7) * mm, v(92.7, 6.28) * mm]});
            skFitSpline(sketch, "E807", {"points": [v(92.7, 6.28) * mm, v(92.8, 6.1) * mm, v(92.89, 5.93) * mm, v(92.98, 5.76) * mm]});
            skFitSpline(sketch, "E808", {"points": [v(92.98, 5.76) * mm, v(93.04, 5.65) * mm, v(93.13, 5.6) * mm, v(93.25, 5.59) * mm]});
            skFitSpline(sketch, "E809", {"points": [v(93.25, 5.59) * mm, v(93.41, 5.58) * mm, v(93.57, 5.55) * mm, v(93.73, 5.54) * mm]});
            skFitSpline(sketch, "E810", {"points": [v(93.73, 5.54) * mm, v(94.28, 5.52) * mm, v(94.84, 5.5) * mm, v(95.4, 5.49) * mm]});
            skFitSpline(sketch, "E811", {"points": [v(95.4, 5.49) * mm, v(95.61, 5.48) * mm, v(95.83, 5.45) * mm, v(96.04, 5.47) * mm]});
            skFitSpline(sketch, "E812", {"points": [v(96.04, 5.47) * mm, v(96.61, 5.51) * mm, v(97.17, 5.48) * mm, v(97.74, 5.41) * mm]});
            skFitSpline(sketch, "E813", {"points": [v(97.74, 5.41) * mm, v(97.83, 5.4) * mm, v(97.93, 5.4) * mm, v(98.07, 5.4) * mm]});
            skFitSpline(sketch, "E814", {"points": [v(98.07, 5.4) * mm, v(98, 5.5) * mm, v(97.95, 5.56) * mm, v(97.9, 5.63) * mm]});
            skFitSpline(sketch, "E815", {"points": [v(97.9, 5.63) * mm, v(97.7, 5.93) * mm, v(97.48, 6.23) * mm, v(97.3, 6.54) * mm]});
            skFitSpline(sketch, "E816", {"points": [v(97.3, 6.54) * mm, v(97.02, 7) * mm, v(96.78, 7.46) * mm, v(96.5, 7.91) * mm]});
            skFitSpline(sketch, "E817", {"points": [v(96.5, 7.91) * mm, v(96.22, 8.38) * mm, v(95.88, 8.82) * mm, v(95.6, 9.3) * mm]});
            skFitSpline(sketch, "E818", {"points": [v(95.6, 9.3) * mm, v(95.44, 9.56) * mm, v(95.24, 9.65) * mm, v(94.95, 9.62) * mm]});
            skFitSpline(sketch, "E819", {"points": [v(94.95, 9.62) * mm, v(94.9, 9.61) * mm, v(94.85, 9.62) * mm, v(94.8, 9.61) * mm]});
            skFitSpline(sketch, "E820", {"points": [v(94.8, 9.61) * mm, v(94.27, 9.54) * mm, v(93.73, 9.5) * mm, v(93.18, 9.52) * mm]});
            skFitSpline(sketch, "E821", {"points": [v(93.18, 9.52) * mm, v(92.54, 9.54) * mm, v(91.92, 9.38) * mm, v(91.26, 9.33) * mm]});
            skFitSpline(sketch, "E822", {"points": [v(109, 4.1) * mm, v(108.98, 4.14) * mm, v(108.97, 4.17) * mm, v(108.95, 4.2) * mm]});
            skFitSpline(sketch, "E823", {"points": [v(108.95, 4.2) * mm, v(108.67, 4.57) * mm, v(108.38, 4.95) * mm, v(108.1, 5.33) * mm]});
            skFitSpline(sketch, "E824", {"points": [v(108.1, 5.33) * mm, v(108.04, 5.42) * mm, v(107.98, 5.52) * mm, v(107.96, 5.62) * mm]});
            skFitSpline(sketch, "E825", {"points": [v(107.96, 5.62) * mm, v(107.92, 5.82) * mm, v(108, 5.98) * mm, v(108.18, 6.09) * mm]});
            skFitSpline(sketch, "E826", {"points": [v(108.18, 6.09) * mm, v(108.37, 6.2) * mm, v(108.57, 6.2) * mm, v(108.74, 6.06) * mm]});
            skFitSpline(sketch, "E827", {"points": [v(108.74, 6.06) * mm, v(108.85, 5.98) * mm, v(108.93, 5.87) * mm, v(109.01, 5.76) * mm]});
            skFitSpline(sketch, "E828", {"points": [v(109.01, 5.76) * mm, v(109.19, 5.54) * mm, v(109.34, 5.3) * mm, v(109.57, 5.08) * mm]});
            skFitSpline(sketch, "E829", {"points": [v(109.57, 5.08) * mm, v(109.84, 5.54) * mm, v(110.1, 5.97) * mm, v(110.34, 6.39) * mm]});
            skFitSpline(sketch, "E830", {"points": [v(110.34, 6.39) * mm, v(110.2, 6.56) * mm, v(110.1, 6.72) * mm, v(109.97, 6.88) * mm]});
            skFitSpline(sketch, "E831", {"points": [v(109.97, 6.88) * mm, v(109.75, 7.16) * mm, v(109.53, 7.44) * mm, v(109.3, 7.73) * mm]});
            skFitSpline(sketch, "E832", {"points": [v(109.3, 7.73) * mm, v(109.2, 7.88) * mm, v(109.15, 8.04) * mm, v(109.22, 8.22) * mm]});
            skFitSpline(sketch, "E833", {"points": [v(109.22, 8.22) * mm, v(109.3, 8.4) * mm, v(109.43, 8.5) * mm, v(109.62, 8.53) * mm]});
            skFitSpline(sketch, "E834", {"points": [v(109.62, 8.53) * mm, v(109.84, 8.56) * mm, v(110.01, 8.47) * mm, v(110.14, 8.3) * mm]});
            skFitSpline(sketch, "E835", {"points": [v(110.14, 8.3) * mm, v(110.35, 8.02) * mm, v(110.55, 7.74) * mm, v(110.75, 7.47) * mm]});
            skFitSpline(sketch, "E836", {"points": [v(110.75, 7.47) * mm, v(110.8, 7.41) * mm, v(110.84, 7.36) * mm, v(110.9, 7.27) * mm]});
            skFitSpline(sketch, "E837", {"points": [v(110.9, 7.27) * mm, v(111.35, 8.1) * mm, v(111.95, 8.8) * mm, v(112.37, 9.66) * mm]});
            skFitSpline(sketch, "E838", {"points": [v(112.37, 9.66) * mm, v(112.3, 9.66) * mm, v(112.24, 9.66) * mm, v(112.19, 9.66) * mm]});
            skFitSpline(sketch, "E839", {"points": [v(112.19, 9.66) * mm, v(111.66, 9.68) * mm, v(111.14, 9.57) * mm, v(110.62, 9.5) * mm]});
            skFitSpline(sketch, "E840", {"points": [v(110.62, 9.5) * mm, v(110.3, 9.45) * mm, v(109.98, 9.37) * mm, v(109.65, 9.33) * mm]});
            skFitSpline(sketch, "E841", {"points": [v(109.65, 9.33) * mm, v(109.24, 9.28) * mm, v(108.83, 9.24) * mm, v(108.41, 9.24) * mm]});
            skFitSpline(sketch, "E842", {"points": [v(108.41, 9.24) * mm, v(107.6, 9.22) * mm, v(106.77, 9.2) * mm, v(105.95, 9.25) * mm]});
            skFitSpline(sketch, "E843", {"points": [v(105.95, 9.25) * mm, v(105.23, 9.3) * mm, v(104.51, 9.45) * mm, v(103.8, 9.55) * mm]});
            skFitSpline(sketch, "E844", {"points": [v(103.8, 9.55) * mm, v(103.51, 9.6) * mm, v(103.23, 9.63) * mm, v(102.94, 9.66) * mm]});
            skFitSpline(sketch, "E845", {"points": [v(102.94, 9.66) * mm, v(102.78, 9.68) * mm, v(102.62, 9.66) * mm, v(102.4, 9.66) * mm]});
            skFitSpline(sketch, "E846", {"points": [v(102.4, 9.66) * mm, v(102.92, 8.84) * mm, v(103.41, 8.07) * mm, v(103.92, 7.28) * mm]});
            skFitSpline(sketch, "E847", {"points": [v(103.92, 7.28) * mm, v(103.98, 7.36) * mm, v(104.02, 7.4) * mm, v(104.05, 7.46) * mm]});
            skFitSpline(sketch, "E848", {"points": [v(104.05, 7.46) * mm, v(104.24, 7.72) * mm, v(104.43, 7.98) * mm, v(104.62, 8.23) * mm]});
            skFitSpline(sketch, "E849", {"points": [v(104.62, 8.23) * mm, v(104.68, 8.3) * mm, v(104.74, 8.38) * mm, v(104.82, 8.44) * mm]});
            skFitSpline(sketch, "E850", {"points": [v(104.82, 8.44) * mm, v(105.03, 8.6) * mm, v(105.34, 8.55) * mm, v(105.5, 8.35) * mm]});
            skFitSpline(sketch, "E851", {"points": [v(105.5, 8.35) * mm, v(105.68, 8.15) * mm, v(105.66, 7.89) * mm, v(105.46, 7.68) * mm]});
            skFitSpline(sketch, "E852", {"points": [v(105.46, 7.68) * mm, v(105.39, 7.61) * mm, v(105.32, 7.53) * mm, v(105.26, 7.45) * mm]});
            skFitSpline(sketch, "E853", {"points": [v(105.26, 7.45) * mm, v(105, 7.1) * mm, v(104.74, 6.75) * mm, v(104.48, 6.38) * mm]});
            skFitSpline(sketch, "E854", {"points": [v(104.48, 6.38) * mm, v(104.74, 5.96) * mm, v(104.95, 5.5) * mm, v(105.27, 5.08) * mm]});
            skFitSpline(sketch, "E855", {"points": [v(105.27, 5.08) * mm, v(105.46, 5.33) * mm, v(105.63, 5.55) * mm, v(105.8, 5.78) * mm]});
            skFitSpline(sketch, "E856", {"points": [v(105.8, 5.78) * mm, v(105.86, 5.86) * mm, v(105.92, 5.94) * mm, v(105.99, 6) * mm]});
            skFitSpline(sketch, "E857", {"points": [v(105.99, 6) * mm, v(106.2, 6.21) * mm, v(106.52, 6.21) * mm, v(106.72, 6.02) * mm]});
            skFitSpline(sketch, "E858", {"points": [v(106.72, 6.02) * mm, v(106.9, 5.85) * mm, v(106.87, 5.5) * mm, v(106.7, 5.3) * mm]});
            skFitSpline(sketch, "E859", {"points": [v(106.7, 5.3) * mm, v(106.4, 4.97) * mm, v(106.15, 4.6) * mm, v(105.88, 4.24) * mm]});
            skFitSpline(sketch, "E860", {"points": [v(105.88, 4.24) * mm, v(105.82, 4.15) * mm, v(105.82, 4.08) * mm, v(105.87, 3.98) * mm]});
            skFitSpline(sketch, "E861", {"points": [v(105.87, 3.98) * mm, v(106.24, 3.28) * mm, v(106.6, 2.59) * mm, v(106.95, 1.9) * mm]});
            skFitSpline(sketch, "E862", {"points": [v(106.95, 1.9) * mm, v(107.09, 1.63) * mm, v(107.24, 1.38) * mm, v(107.4, 1.1) * mm]});
            skFitSpline(sketch, "E863", {"points": [v(107.4, 1.1) * mm, v(107.45, 1.18) * mm, v(107.5, 1.23) * mm, v(107.52, 1.29) * mm]});
            skFitSpline(sketch, "E864", {"points": [v(107.52, 1.29) * mm, v(107.7, 1.6) * mm, v(107.86, 1.92) * mm, v(108.02, 2.24) * mm]});
            skFitSpline(sketch, "E865", {"points": [v(108.02, 2.24) * mm, v(108.19, 2.56) * mm, v(108.34, 2.89) * mm, v(108.5, 3.2) * mm]});
            skFitSpline(sketch, "E866", {"points": [v(108.5, 3.2) * mm, v(108.66, 3.5) * mm, v(108.83, 3.8) * mm, v(109, 4.1) * mm]});
            skFitSpline(sketch, "E867", {"points": [v(102.84, -6.66) * mm, v(102.42, -6.62) * mm, v(102.04, -6.58) * mm, v(101.67, -6.53) * mm]});
            skFitSpline(sketch, "E868", {"points": [v(101.67, -6.53) * mm, v(101.56, -6.52) * mm, v(101.46, -6.5) * mm, v(101.37, -6.46) * mm]});
            skFitSpline(sketch, "E869", {"points": [v(101.37, -6.46) * mm, v(101.12, -6.34) * mm, v(101.02, -6.05) * mm, v(101.13, -5.8) * mm]});
            skFitSpline(sketch, "E870", {"points": [v(101.13, -5.8) * mm, v(101.23, -5.56) * mm, v(101.48, -5.46) * mm, v(101.74, -5.54) * mm]});
            skFitSpline(sketch, "E871", {"points": [v(101.74, -5.54) * mm, v(101.8, -5.56) * mm, v(101.86, -5.58) * mm, v(101.92, -5.59) * mm]});
            skFitSpline(sketch, "E872", {"points": [v(101.92, -5.59) * mm, v(102.4, -5.64) * mm, v(102.86, -5.69) * mm, v(103.34, -5.74) * mm]});
            skFitSpline(sketch, "E873", {"points": [v(103.34, -5.74) * mm, v(103.58, -5.3) * mm, v(103.83, -4.87) * mm, v(104.1, -4.4) * mm]});
            skFitSpline(sketch, "E874", {"points": [v(104.1, -4.4) * mm, v(103.74, -4.35) * mm, v(103.43, -4.32) * mm, v(103.13, -4.27) * mm]});
            skFitSpline(sketch, "E875", {"points": [v(103.13, -4.27) * mm, v(103, -4.25) * mm, v(102.84, -4.21) * mm, v(102.73, -4.14) * mm]});
            skFitSpline(sketch, "E876", {"points": [v(102.73, -4.14) * mm, v(102.52, -4) * mm, v(102.46, -3.74) * mm, v(102.56, -3.52) * mm]});
            skFitSpline(sketch, "E877", {"points": [v(102.56, -3.52) * mm, v(102.67, -3.3) * mm, v(102.9, -3.21) * mm, v(103.15, -3.28) * mm]});
            skFitSpline(sketch, "E878", {"points": [v(103.15, -3.28) * mm, v(103.22, -3.3) * mm, v(103.3, -3.31) * mm, v(103.38, -3.32) * mm]});
            skFitSpline(sketch, "E879", {"points": [v(103.38, -3.32) * mm, v(103.71, -3.37) * mm, v(104.05, -3.4) * mm, v(104.38, -3.45) * mm]});
            skFitSpline(sketch, "E880", {"points": [v(104.38, -3.45) * mm, v(104.57, -3.48) * mm, v(104.66, -3.42) * mm, v(104.76, -3.26) * mm]});
            skFitSpline(sketch, "E881", {"points": [v(104.76, -3.26) * mm, v(105.12, -2.68) * mm, v(105.5, -2.1) * mm, v(105.87, -1.52) * mm]});
            skFitSpline(sketch, "E882", {"points": [v(105.87, -1.52) * mm, v(106.03, -1.27) * mm, v(106.2, -1) * mm, v(106.35, -0.75) * mm]});
            skFitSpline(sketch, "E883", {"points": [v(106.35, -0.75) * mm, v(106.38, -0.7) * mm, v(106.4, -0.64) * mm, v(106.43, -0.55) * mm]});
            skFitSpline(sketch, "E884", {"points": [v(106.43, -0.55) * mm, v(106.3, -0.55) * mm, v(106.2, -0.55) * mm, v(106.1, -0.55) * mm]});
            skFitSpline(sketch, "E885", {"points": [v(106.1, -0.55) * mm, v(105.63, -0.58) * mm, v(105.15, -0.6) * mm, v(104.67, -0.63) * mm]});
            skFitSpline(sketch, "E886", {"points": [v(104.67, -0.63) * mm, v(104.18, -0.65) * mm, v(103.7, -0.67) * mm, v(103.2, -0.67) * mm]});
            skFitSpline(sketch, "E887", {"points": [v(103.2, -0.67) * mm, v(103.08, -0.68) * mm, v(103, -0.72) * mm, v(102.95, -0.84) * mm]});
            skFitSpline(sketch, "E888", {"points": [v(102.95, -0.84) * mm, v(102.78, -1.23) * mm, v(102.6, -1.63) * mm, v(102.44, -2.02) * mm]});
            skFitSpline(sketch, "E889", {"points": [v(102.44, -2.02) * mm, v(102.41, -2.08) * mm, v(102.4, -2.15) * mm, v(102.38, -2.2) * mm]});
            skFitSpline(sketch, "E890", {"points": [v(102.38, -2.2) * mm, v(102.27, -2.4) * mm, v(102.04, -2.48) * mm, v(101.84, -2.42) * mm]});
            skFitSpline(sketch, "E891", {"points": [v(101.84, -2.42) * mm, v(101.61, -2.35) * mm, v(101.46, -2.14) * mm, v(101.48, -1.9) * mm]});
            skFitSpline(sketch, "E892", {"points": [v(101.48, -1.9) * mm, v(101.5, -1.77) * mm, v(101.54, -1.65) * mm, v(101.59, -1.53) * mm]});
            skFitSpline(sketch, "E893", {"points": [v(101.59, -1.53) * mm, v(101.7, -1.26) * mm, v(101.81, -1) * mm, v(101.93, -0.7) * mm]});
            skFitSpline(sketch, "E894", {"points": [v(101.93, -0.7) * mm, v(101.4, -0.61) * mm, v(100.88, -0.66) * mm, v(100.4, -0.65) * mm]});
            skFitSpline(sketch, "E895", {"points": [v(100.4, -0.65) * mm, v(100.34, -0.8) * mm, v(100.3, -0.93) * mm, v(100.24, -1.05) * mm]});
            skFitSpline(sketch, "E896", {"points": [v(100.24, -1.05) * mm, v(100.08, -1.44) * mm, v(99.92, -1.83) * mm, v(99.76, -2.22) * mm]});
            skFitSpline(sketch, "E897", {"points": [v(99.76, -2.22) * mm, v(99.68, -2.4) * mm, v(99.53, -2.54) * mm, v(99.32, -2.55) * mm]});
            skFitSpline(sketch, "E898", {"points": [v(99.32, -2.55) * mm, v(99.13, -2.56) * mm, v(98.93, -2.44) * mm, v(98.84, -2.25) * mm]});
            skFitSpline(sketch, "E899", {"points": [v(98.84, -2.25) * mm, v(98.76, -2.09) * mm, v(98.79, -1.93) * mm, v(98.86, -1.77) * mm]});
            skFitSpline(sketch, "E900", {"points": [v(98.86, -1.77) * mm, v(98.98, -1.47) * mm, v(99.11, -1.18) * mm, v(99.24, -0.89) * mm]});
            skFitSpline(sketch, "E901", {"points": [v(99.24, -0.89) * mm, v(99.27, -0.81) * mm, v(99.3, -0.73) * mm, v(99.34, -0.65) * mm]});
            skFitSpline(sketch, "E902", {"points": [v(99.34, -0.65) * mm, v(99.29, -0.63) * mm, v(99.26, -0.61) * mm, v(99.23, -0.61) * mm]});
            skFitSpline(sketch, "E903", {"points": [v(99.23, -0.61) * mm, v(98.35, -0.57) * mm, v(97.47, -0.54) * mm, v(96.56, -0.5) * mm]});
            skFitSpline(sketch, "E904", {"points": [v(96.56, -0.5) * mm, v(96.6, -0.57) * mm, v(96.6, -0.6) * mm, v(96.62, -0.64) * mm]});
            skFitSpline(sketch, "E905", {"points": [v(96.62, -0.64) * mm, v(96.97, -1.3) * mm, v(97.47, -1.86) * mm, v(97.94, -2.43) * mm]});
            skFitSpline(sketch, "E906", {"points": [v(97.94, -2.43) * mm, v(98.27, -2.82) * mm, v(98.6, -3.22) * mm, v(98.86, -3.65) * mm]});
            skFitSpline(sketch, "E907", {"points": [v(98.86, -3.65) * mm, v(99.07, -4) * mm, v(99.3, -4.36) * mm, v(99.5, -4.72) * mm]});
            skFitSpline(sketch, "E908", {"points": [v(99.5, -4.72) * mm, v(99.7, -5.09) * mm, v(99.93, -5.45) * mm, v(100.1, -5.84) * mm]});
            skFitSpline(sketch, "E909", {"points": [v(100.1, -5.84) * mm, v(100.41, -6.56) * mm, v(100.69, -7.3) * mm, v(100.98, -8.03) * mm]});
            skFitSpline(sketch, "E910", {"points": [v(100.98, -8.03) * mm, v(101.13, -8.41) * mm, v(101.29, -8.78) * mm, v(101.55, -9.14) * mm]});
            skFitSpline(sketch, "E911", {"points": [v(101.55, -9.14) * mm, v(101.99, -8.3) * mm, v(102.4, -7.5) * mm, v(102.84, -6.66) * mm]});
            skFitSpline(sketch, "E912", {"points": [v(112.87, -0.7) * mm, v(113, -1) * mm, v(113.13, -1.27) * mm, v(113.23, -1.56) * mm]});
            skFitSpline(sketch, "E913", {"points": [v(113.23, -1.56) * mm, v(113.28, -1.69) * mm, v(113.32, -1.83) * mm, v(113.32, -1.97) * mm]});
            skFitSpline(sketch, "E914", {"points": [v(113.32, -1.97) * mm, v(113.33, -2.21) * mm, v(113.13, -2.4) * mm, v(112.9, -2.44) * mm]});
            skFitSpline(sketch, "E915", {"points": [v(112.9, -2.44) * mm, v(112.68, -2.47) * mm, v(112.47, -2.33) * mm, v(112.39, -2.11) * mm]});
            skFitSpline(sketch, "E916", {"points": [v(112.39, -2.11) * mm, v(112.26, -1.79) * mm, v(112.14, -1.46) * mm, v(112, -1.14) * mm]});
            skFitSpline(sketch, "E917", {"points": [v(112, -1.14) * mm, v(111.95, -1.01) * mm, v(111.89, -0.89) * mm, v(111.82, -0.77) * mm]});
            skFitSpline(sketch, "E918", {"points": [v(111.82, -0.77) * mm, v(111.79, -0.73) * mm, v(111.72, -0.69) * mm, v(111.67, -0.68) * mm]});
            skFitSpline(sketch, "E919", {"points": [v(111.67, -0.68) * mm, v(111.49, -0.66) * mm, v(111.3, -0.66) * mm, v(111.12, -0.65) * mm]});
            skFitSpline(sketch, "E920", {"points": [v(111.12, -0.65) * mm, v(110.82, -0.64) * mm, v(110.53, -0.65) * mm, v(110.23, -0.63) * mm]});
            skFitSpline(sketch, "E921", {"points": [v(110.23, -0.63) * mm, v(109.7, -0.6) * mm, v(109.17, -0.57) * mm, v(108.63, -0.54) * mm]});
            skFitSpline(sketch, "E922", {"points": [v(108.63, -0.54) * mm, v(108.55, -0.54) * mm, v(108.47, -0.56) * mm, v(108.36, -0.57) * mm]});
            skFitSpline(sketch, "E923", {"points": [v(108.36, -0.57) * mm, v(108.43, -0.7) * mm, v(108.48, -0.79) * mm, v(108.54, -0.87) * mm]});
            skFitSpline(sketch, "E924", {"points": [v(108.54, -0.87) * mm, v(108.87, -1.39) * mm, v(109.21, -1.9) * mm, v(109.55, -2.42) * mm]});
            skFitSpline(sketch, "E925", {"points": [v(109.55, -2.42) * mm, v(109.73, -2.71) * mm, v(109.91, -3.02) * mm, v(110.09, -3.32) * mm]});
            skFitSpline(sketch, "E926", {"points": [v(110.09, -3.32) * mm, v(110.15, -3.42) * mm, v(110.22, -3.48) * mm, v(110.34, -3.46) * mm]});
            skFitSpline(sketch, "E927", {"points": [v(110.34, -3.46) * mm, v(110.8, -3.4) * mm, v(111.26, -3.32) * mm, v(111.73, -3.26) * mm]});
            skFitSpline(sketch, "E928", {"points": [v(111.73, -3.26) * mm, v(111.8, -3.25) * mm, v(111.86, -3.25) * mm, v(111.92, -3.26) * mm]});
            skFitSpline(sketch, "E929", {"points": [v(111.92, -3.26) * mm, v(112.13, -3.32) * mm, v(112.26, -3.46) * mm, v(112.3, -3.68) * mm]});
            skFitSpline(sketch, "E930", {"points": [v(112.3, -3.68) * mm, v(112.32, -3.87) * mm, v(112.22, -4.09) * mm, v(112.03, -4.18) * mm]});
            skFitSpline(sketch, "E931", {"points": [v(112.03, -4.18) * mm, v(111.91, -4.23) * mm, v(111.79, -4.26) * mm, v(111.66, -4.27) * mm]});
            skFitSpline(sketch, "E932", {"points": [v(111.66, -4.27) * mm, v(111.36, -4.32) * mm, v(111.06, -4.35) * mm, v(110.71, -4.4) * mm]});
            skFitSpline(sketch, "E933", {"points": [v(110.71, -4.4) * mm, v(110.98, -4.87) * mm, v(111.23, -5.3) * mm, v(111.47, -5.74) * mm]});
            skFitSpline(sketch, "E934", {"points": [v(111.47, -5.74) * mm, v(111.65, -5.72) * mm, v(111.8, -5.7) * mm, v(111.95, -5.69) * mm]});
            skFitSpline(sketch, "E935", {"points": [v(111.95, -5.69) * mm, v(112.35, -5.63) * mm, v(112.76, -5.65) * mm, v(113.16, -5.51) * mm]});
            skFitSpline(sketch, "E936", {"points": [v(113.16, -5.51) * mm, v(113.21, -5.5) * mm, v(113.28, -5.5) * mm, v(113.34, -5.52) * mm]});
            skFitSpline(sketch, "E937", {"points": [v(113.34, -5.52) * mm, v(113.57, -5.58) * mm, v(113.7, -5.74) * mm, v(113.7, -5.96) * mm]});
            skFitSpline(sketch, "E938", {"points": [v(113.7, -5.96) * mm, v(113.72, -6.23) * mm, v(113.6, -6.42) * mm, v(113.36, -6.5) * mm]});
            skFitSpline(sketch, "E939", {"points": [v(113.36, -6.5) * mm, v(113.24, -6.53) * mm, v(113.1, -6.54) * mm, v(112.98, -6.55) * mm]});
            skFitSpline(sketch, "E940", {"points": [v(112.98, -6.55) * mm, v(112.65, -6.59) * mm, v(112.32, -6.62) * mm, v(111.97, -6.66) * mm]});
            skFitSpline(sketch, "E941", {"points": [v(111.97, -6.66) * mm, v(112.2, -7.09) * mm, v(112.41, -7.49) * mm, v(112.6, -7.9) * mm]});
            skFitSpline(sketch, "E942", {"points": [v(112.6, -7.9) * mm, v(112.8, -8.31) * mm, v(113.04, -8.7) * mm, v(113.27, -9.12) * mm]});
            skFitSpline(sketch, "E943", {"points": [v(113.27, -9.12) * mm, v(113.32, -9.06) * mm, v(113.34, -9.03) * mm, v(113.36, -9) * mm]});
            skFitSpline(sketch, "E944", {"points": [v(113.36, -9) * mm, v(113.75, -8.35) * mm, v(114, -7.64) * mm, v(114.25, -6.94) * mm]});
            skFitSpline(sketch, "E945", {"points": [v(114.25, -6.94) * mm, v(114.48, -6.26) * mm, v(114.8, -5.63) * mm, v(115.14, -5) * mm]});
            skFitSpline(sketch, "E946", {"points": [v(115.14, -5) * mm, v(115.29, -4.75) * mm, v(115.43, -4.5) * mm, v(115.59, -4.24) * mm]});
            skFitSpline(sketch, "E947", {"points": [v(115.59, -4.24) * mm, v(115.88, -3.79) * mm, v(116.16, -3.32) * mm, v(116.49, -2.89) * mm]});
            skFitSpline(sketch, "E948", {"points": [v(116.49, -2.89) * mm, v(116.83, -2.42) * mm, v(117.22, -1.99) * mm, v(117.59, -1.53) * mm]});
            skFitSpline(sketch, "E949", {"points": [v(117.59, -1.53) * mm, v(117.84, -1.22) * mm, v(118.07, -0.9) * mm, v(118.24, -0.53) * mm]});
            skFitSpline(sketch, "E950", {"points": [v(118.24, -0.53) * mm, v(117.6, -0.5) * mm, v(115.64, -0.6) * mm, v(115.48, -0.67) * mm]});
            skFitSpline(sketch, "E951", {"points": [v(115.48, -0.67) * mm, v(115.5, -0.72) * mm, v(115.51, -0.77) * mm, v(115.54, -0.82) * mm]});
            skFitSpline(sketch, "E952", {"points": [v(115.54, -0.82) * mm, v(115.67, -1.12) * mm, v(115.8, -1.41) * mm, v(115.93, -1.72) * mm]});
            skFitSpline(sketch, "E953", {"points": [v(115.93, -1.72) * mm, v(115.98, -1.82) * mm, v(116, -1.95) * mm, v(116, -2.06) * mm]});
            skFitSpline(sketch, "E954", {"points": [v(116, -2.06) * mm, v(116, -2.31) * mm, v(115.8, -2.52) * mm, v(115.56, -2.55) * mm]});
            skFitSpline(sketch, "E955", {"points": [v(115.56, -2.55) * mm, v(115.31, -2.57) * mm, v(115.1, -2.41) * mm, v(115.04, -2.16) * mm]});
            skFitSpline(sketch, "E956", {"points": [v(115.04, -2.16) * mm, v(115.02, -2.07) * mm, v(114.99, -1.99) * mm, v(114.95, -1.9) * mm]});
            skFitSpline(sketch, "E957", {"points": [v(114.95, -1.9) * mm, v(114.77, -1.5) * mm, v(114.59, -1.08) * mm, v(114.4, -0.65) * mm]});
            skFitSpline(sketch, "E958", {"points": [v(114.4, -0.65) * mm, v(113.9, -0.66) * mm, v(113.4, -0.62) * mm, v(112.87, -0.7) * mm]});
            skFitSpline(sketch, "E959", {"points": [v(101.55, 9.14) * mm, v(101.5, 9.07) * mm, v(101.48, 9.03) * mm, v(101.46, 9) * mm]});
            skFitSpline(sketch, "E960", {"points": [v(101.46, 9) * mm, v(101.06, 8.35) * mm, v(100.8, 7.63) * mm, v(100.56, 6.92) * mm]});
            skFitSpline(sketch, "E961", {"points": [v(100.56, 6.92) * mm, v(100.33, 6.26) * mm, v(100.02, 5.64) * mm, v(99.69, 5.03) * mm]});
            skFitSpline(sketch, "E962", {"points": [v(99.69, 5.03) * mm, v(99.54, 4.76) * mm, v(99.39, 4.5) * mm, v(99.22, 4.25) * mm]});
            skFitSpline(sketch, "E963", {"points": [v(99.22, 4.25) * mm, v(98.92, 3.78) * mm, v(98.63, 3.3) * mm, v(98.3, 2.85) * mm]});
            skFitSpline(sketch, "E964", {"points": [v(98.3, 2.85) * mm, v(97.88, 2.28) * mm, v(97.4, 1.74) * mm, v(96.97, 1.18) * mm]});
            skFitSpline(sketch, "E965", {"points": [v(96.97, 1.18) * mm, v(96.84, 1.02) * mm, v(96.75, 0.84) * mm, v(96.64, 0.66) * mm]});
            skFitSpline(sketch, "E966", {"points": [v(96.64, 0.66) * mm, v(96.62, 0.61) * mm, v(96.6, 0.56) * mm, v(96.58, 0.52) * mm]});
            skFitSpline(sketch, "E967", {"points": [v(96.58, 0.52) * mm, v(96.9, 0.52) * mm, v(97.2, 0.5) * mm, v(97.51, 0.52) * mm]});
            skFitSpline(sketch, "E968", {"points": [v(97.51, 0.52) * mm, v(97.82, 0.53) * mm, v(98.13, 0.57) * mm, v(98.44, 0.6) * mm]});
            skFitSpline(sketch, "E969", {"points": [v(98.44, 0.6) * mm, v(98.74, 0.62) * mm, v(99.04, 0.54) * mm, v(99.35, 0.64) * mm]});
            skFitSpline(sketch, "E970", {"points": [v(99.35, 0.64) * mm, v(99.2, 1) * mm, v(99.05, 1.32) * mm, v(98.9, 1.65) * mm]});
            skFitSpline(sketch, "E971", {"points": [v(98.9, 1.65) * mm, v(98.86, 1.74) * mm, v(98.82, 1.84) * mm, v(98.8, 1.94) * mm]});
            skFitSpline(sketch, "E972", {"points": [v(98.8, 1.94) * mm, v(98.75, 2.18) * mm, v(98.92, 2.45) * mm, v(99.16, 2.52) * mm]});
            skFitSpline(sketch, "E973", {"points": [v(99.16, 2.52) * mm, v(99.42, 2.59) * mm, v(99.66, 2.46) * mm, v(99.76, 2.21) * mm]});
            skFitSpline(sketch, "E974", {"points": [v(99.76, 2.21) * mm, v(99.91, 1.83) * mm, v(100.07, 1.45) * mm, v(100.23, 1.06) * mm]});
            skFitSpline(sketch, "E975", {"points": [v(100.23, 1.06) * mm, v(100.28, 0.93) * mm, v(100.34, 0.8) * mm, v(100.4, 0.65) * mm]});
            skFitSpline(sketch, "E976", {"points": [v(100.4, 0.65) * mm, v(100.88, 0.65) * mm, v(101.4, 0.61) * mm, v(101.91, 0.68) * mm]});
            skFitSpline(sketch, "E977", {"points": [v(101.91, 0.68) * mm, v(101.9, 0.75) * mm, v(101.89, 0.8) * mm, v(101.87, 0.84) * mm]});
            skFitSpline(sketch, "E978", {"points": [v(101.87, 0.84) * mm, v(101.77, 1.07) * mm, v(101.67, 1.3) * mm, v(101.58, 1.55) * mm]});
            skFitSpline(sketch, "E979", {"points": [v(101.58, 1.55) * mm, v(101.53, 1.68) * mm, v(101.48, 1.82) * mm, v(101.48, 1.96) * mm]});
            skFitSpline(sketch, "E980", {"points": [v(101.48, 1.96) * mm, v(101.48, 2.2) * mm, v(101.68, 2.4) * mm, v(101.91, 2.43) * mm]});
            skFitSpline(sketch, "E981", {"points": [v(101.91, 2.43) * mm, v(102.12, 2.46) * mm, v(102.34, 2.33) * mm, v(102.41, 2.13) * mm]});
            skFitSpline(sketch, "E982", {"points": [v(102.41, 2.13) * mm, v(102.53, 1.83) * mm, v(102.65, 1.52) * mm, v(102.77, 1.22) * mm]});
            skFitSpline(sketch, "E983", {"points": [v(102.77, 1.22) * mm, v(102.83, 1.07) * mm, v(102.9, 0.93) * mm, v(102.98, 0.79) * mm]});
            skFitSpline(sketch, "E984", {"points": [v(102.98, 0.79) * mm, v(103.01, 0.7) * mm, v(103.06, 0.66) * mm, v(103.16, 0.66) * mm]});
            skFitSpline(sketch, "E985", {"points": [v(103.16, 0.66) * mm, v(103.24, 0.66) * mm, v(103.32, 0.65) * mm, v(103.4, 0.64) * mm]});
            skFitSpline(sketch, "E986", {"points": [v(103.4, 0.64) * mm, v(103.84, 0.63) * mm, v(104.28, 0.63) * mm, v(104.72, 0.62) * mm]});
            skFitSpline(sketch, "E987", {"points": [v(104.72, 0.62) * mm, v(105.16, 0.6) * mm, v(105.6, 0.57) * mm, v(106.05, 0.55) * mm]});
            skFitSpline(sketch, "E988", {"points": [v(106.05, 0.55) * mm, v(106.17, 0.54) * mm, v(106.3, 0.55) * mm, v(106.47, 0.55) * mm]});
            skFitSpline(sketch, "E989", {"points": [v(106.47, 0.55) * mm, v(106.23, 0.92) * mm, v(106.03, 1.26) * mm, v(105.82, 1.58) * mm]});
            skFitSpline(sketch, "E990", {"points": [v(105.82, 1.58) * mm, v(105.56, 1.99) * mm, v(105.3, 2.39) * mm, v(105.03, 2.79) * mm]});
            skFitSpline(sketch, "E991", {"points": [v(105.03, 2.79) * mm, v(104.92, 2.96) * mm, v(104.82, 3.14) * mm, v(104.71, 3.32) * mm]});
            skFitSpline(sketch, "E992", {"points": [v(104.71, 3.32) * mm, v(104.67, 3.4) * mm, v(104.6, 3.46) * mm, v(104.5, 3.45) * mm]});
            skFitSpline(sketch, "E993", {"points": [v(104.5, 3.45) * mm, v(104.04, 3.38) * mm, v(103.57, 3.33) * mm, v(103.1, 3.25) * mm]});
            skFitSpline(sketch, "E994", {"points": [v(103.1, 3.25) * mm, v(102.83, 3.2) * mm, v(102.55, 3.38) * mm, v(102.52, 3.67) * mm]});
            skFitSpline(sketch, "E995", {"points": [v(102.52, 3.67) * mm, v(102.49, 3.96) * mm, v(102.68, 4.2) * mm, v(103, 4.25) * mm]});
            skFitSpline(sketch, "E996", {"points": [v(103, 4.25) * mm, v(103.2, 4.28) * mm, v(103.38, 4.29) * mm, v(103.57, 4.31) * mm]});
            skFitSpline(sketch, "E997", {"points": [v(103.57, 4.31) * mm, v(103.73, 4.33) * mm, v(103.9, 4.37) * mm, v(104.1, 4.4) * mm]});
            skFitSpline(sketch, "E998", {"points": [v(104.1, 4.4) * mm, v(103.82, 4.87) * mm, v(103.58, 5.3) * mm, v(103.33, 5.74) * mm]});
            skFitSpline(sketch, "E999", {"points": [v(103.33, 5.74) * mm, v(103.2, 5.72) * mm, v(103.1, 5.7) * mm, v(102.98, 5.68) * mm]});
            skFitSpline(sketch, "E1000", {"points": [v(102.98, 5.68) * mm, v(102.54, 5.63) * mm, v(102.09, 5.64) * mm, v(101.66, 5.5) * mm]});
            skFitSpline(sketch, "E1001", {"points": [v(101.66, 5.5) * mm, v(101.6, 5.49) * mm, v(101.51, 5.5) * mm, v(101.45, 5.52) * mm]});
            skFitSpline(sketch, "E1002", {"points": [v(101.45, 5.52) * mm, v(101.22, 5.58) * mm, v(101.1, 5.76) * mm, v(101.1, 6) * mm]});
            skFitSpline(sketch, "E1003", {"points": [v(101.1, 6) * mm, v(101.1, 6.23) * mm, v(101.24, 6.43) * mm, v(101.47, 6.49) * mm]});
            skFitSpline(sketch, "E1004", {"points": [v(101.47, 6.49) * mm, v(101.6, 6.52) * mm, v(101.74, 6.53) * mm, v(101.87, 6.55) * mm]});
            skFitSpline(sketch, "E1005", {"points": [v(101.87, 6.55) * mm, v(102.18, 6.58) * mm, v(102.5, 6.62) * mm, v(102.84, 6.65) * mm]});
            skFitSpline(sketch, "E1006", {"points": [v(102.84, 6.65) * mm, v(102.4, 7.49) * mm, v(101.99, 8.3) * mm, v(101.55, 9.14) * mm]});
            skFitSpline(sketch, "E1007", {"points": [v(118.24, 0.52) * mm, v(118.21, 0.57) * mm, v(118.2, 0.6) * mm, v(118.19, 0.63) * mm]});
            skFitSpline(sketch, "E1008", {"points": [v(118.19, 0.63) * mm, v(117.83, 1.3) * mm, v(117.33, 1.88) * mm, v(116.83, 2.45) * mm]});
            skFitSpline(sketch, "E1009", {"points": [v(116.83, 2.45) * mm, v(116.37, 2.99) * mm, v(115.99, 3.57) * mm, v(115.62, 4.17) * mm]});
            skFitSpline(sketch, "E1010", {"points": [v(115.62, 4.17) * mm, v(115.46, 4.43) * mm, v(115.31, 4.7) * mm, v(115.17, 4.96) * mm]});
            skFitSpline(sketch, "E1011", {"points": [v(115.17, 4.96) * mm, v(114.92, 5.45) * mm, v(114.65, 5.93) * mm, v(114.43, 6.44) * mm]});
            skFitSpline(sketch, "E1012", {"points": [v(114.43, 6.44) * mm, v(114.2, 6.97) * mm, v(114.03, 7.53) * mm, v(113.8, 8.07) * mm]});
            skFitSpline(sketch, "E1013", {"points": [v(113.8, 8.07) * mm, v(113.68, 8.38) * mm, v(113.52, 8.67) * mm, v(113.37, 8.97) * mm]});
            skFitSpline(sketch, "E1014", {"points": [v(113.37, 8.97) * mm, v(113.35, 9.01) * mm, v(113.3, 9.05) * mm, v(113.25, 9.12) * mm]});
            skFitSpline(sketch, "E1015", {"points": [v(113.25, 9.12) * mm, v(112.82, 8.29) * mm, v(112.4, 7.48) * mm, v(111.97, 6.65) * mm]});
            skFitSpline(sketch, "E1016", {"points": [v(111.97, 6.65) * mm, v(112.32, 6.61) * mm, v(112.64, 6.58) * mm, v(112.96, 6.54) * mm]});
            skFitSpline(sketch, "E1017", {"points": [v(112.96, 6.54) * mm, v(113.09, 6.53) * mm, v(113.22, 6.53) * mm, v(113.34, 6.49) * mm]});
            skFitSpline(sketch, "E1018", {"points": [v(113.34, 6.49) * mm, v(113.68, 6.38) * mm, v(113.76, 6.15) * mm, v(113.7, 5.83) * mm]});
            skFitSpline(sketch, "E1019", {"points": [v(113.7, 5.83) * mm, v(113.65, 5.6) * mm, v(113.36, 5.44) * mm, v(113.13, 5.51) * mm]});
            skFitSpline(sketch, "E1020", {"points": [v(113.13, 5.51) * mm, v(112.59, 5.67) * mm, v(112.02, 5.62) * mm, v(111.48, 5.74) * mm]});
            skFitSpline(sketch, "E1021", {"points": [v(111.48, 5.74) * mm, v(111.22, 5.29) * mm, v(110.98, 4.85) * mm, v(110.71, 4.39) * mm]});
            skFitSpline(sketch, "E1022", {"points": [v(110.71, 4.39) * mm, v(111.07, 4.34) * mm, v(111.38, 4.3) * mm, v(111.69, 4.26) * mm]});
            skFitSpline(sketch, "E1023", {"points": [v(111.69, 4.26) * mm, v(111.82, 4.24) * mm, v(111.97, 4.2) * mm, v(112.09, 4.13) * mm]});
            skFitSpline(sketch, "E1024", {"points": [v(112.09, 4.13) * mm, v(112.3, 4) * mm, v(112.35, 3.72) * mm, v(112.25, 3.51) * mm]});
            skFitSpline(sketch, "E1025", {"points": [v(112.25, 3.51) * mm, v(112.14, 3.3) * mm, v(111.91, 3.22) * mm, v(111.68, 3.26) * mm]});
            skFitSpline(sketch, "E1026", {"points": [v(111.68, 3.26) * mm, v(111.23, 3.34) * mm, v(110.77, 3.39) * mm, v(110.3, 3.45) * mm]});
            skFitSpline(sketch, "E1027", {"points": [v(110.3, 3.45) * mm, v(110.2, 3.46) * mm, v(110.15, 3.4) * mm, v(110.1, 3.33) * mm]});
            skFitSpline(sketch, "E1028", {"points": [v(110.1, 3.33) * mm, v(109.66, 2.65) * mm, v(109.23, 1.97) * mm, v(108.8, 1.29) * mm]});
            skFitSpline(sketch, "E1029", {"points": [v(108.8, 1.29) * mm, v(108.65, 1.06) * mm, v(108.51, 0.82) * mm, v(108.37, 0.57) * mm]});
            skFitSpline(sketch, "E1030", {"points": [v(108.37, 0.57) * mm, v(108.46, 0.55) * mm, v(108.52, 0.52) * mm, v(108.59, 0.53) * mm]});
            skFitSpline(sketch, "E1031", {"points": [v(108.59, 0.53) * mm, v(108.87, 0.53) * mm, v(109.16, 0.53) * mm, v(109.45, 0.56) * mm]});
            skFitSpline(sketch, "E1032", {"points": [v(109.45, 0.56) * mm, v(110.05, 0.63) * mm, v(110.66, 0.65) * mm, v(111.26, 0.65) * mm]});
            skFitSpline(sketch, "E1033", {"points": [v(111.26, 0.65) * mm, v(111.37, 0.64) * mm, v(111.49, 0.66) * mm, v(111.6, 0.66) * mm]});
            skFitSpline(sketch, "E1034", {"points": [v(111.6, 0.66) * mm, v(111.73, 0.65) * mm, v(111.8, 0.7) * mm, v(111.86, 0.83) * mm]});
            skFitSpline(sketch, "E1035", {"points": [v(111.86, 0.83) * mm, v(111.89, 0.9) * mm, v(111.93, 0.97) * mm, v(111.96, 1.04) * mm]});
            skFitSpline(sketch, "E1036", {"points": [v(111.96, 1.04) * mm, v(112.1, 1.39) * mm, v(112.25, 1.73) * mm, v(112.38, 2.08) * mm]});
            skFitSpline(sketch, "E1037", {"points": [v(112.38, 2.08) * mm, v(112.46, 2.31) * mm, v(112.67, 2.46) * mm, v(112.9, 2.43) * mm]});
            skFitSpline(sketch, "E1038", {"points": [v(112.9, 2.43) * mm, v(113.14, 2.4) * mm, v(113.33, 2.2) * mm, v(113.32, 1.94) * mm]});
            skFitSpline(sketch, "E1039", {"points": [v(113.32, 1.94) * mm, v(113.32, 1.8) * mm, v(113.28, 1.67) * mm, v(113.23, 1.55) * mm]});
            skFitSpline(sketch, "E1040", {"points": [v(113.23, 1.55) * mm, v(113.15, 1.32) * mm, v(113.05, 1.1) * mm, v(112.96, 0.88) * mm]});
            skFitSpline(sketch, "E1041", {"points": [v(112.96, 0.88) * mm, v(112.93, 0.82) * mm, v(112.92, 0.75) * mm, v(112.89, 0.66) * mm]});
            skLineSegment(sketch, "E1042", {"start": v(112.89, 0.66) * mm, "end": v(114.4, 0.66) * mm});
            skFitSpline(sketch, "E1043", {"points": [v(114.4, 0.66) * mm, v(114.48, 0.84) * mm, v(114.56, 1) * mm, v(114.63, 1.18) * mm]});
            skFitSpline(sketch, "E1044", {"points": [v(114.63, 1.18) * mm, v(114.77, 1.52) * mm, v(114.91, 1.87) * mm, v(115.05, 2.22) * mm]});
            skFitSpline(sketch, "E1045", {"points": [v(115.05, 2.22) * mm, v(115.12, 2.38) * mm, v(115.24, 2.5) * mm, v(115.42, 2.53) * mm]});
            skFitSpline(sketch, "E1046", {"points": [v(115.42, 2.53) * mm, v(115.8, 2.6) * mm, v(116.1, 2.25) * mm, v(116, 1.86) * mm]});
            skFitSpline(sketch, "E1047", {"points": [v(116, 1.86) * mm, v(115.95, 1.73) * mm, v(115.9, 1.61) * mm, v(115.84, 1.49) * mm]});
            skFitSpline(sketch, "E1048", {"points": [v(115.84, 1.49) * mm, v(115.72, 1.2) * mm, v(115.6, 0.93) * mm, v(115.47, 0.66) * mm]});
            skFitSpline(sketch, "E1049", {"points": [v(115.47, 0.66) * mm, v(115.62, 0.6) * mm, v(117.93, 0.49) * mm, v(118.24, 0.52) * mm]});
            skFitSpline(sketch, "E1050", {"points": [v(102.4, -9.67) * mm, v(102.52, -9.67) * mm, v(102.57, -9.67) * mm, v(102.61, -9.67) * mm]});
            skFitSpline(sketch, "E1051", {"points": [v(102.61, -9.67) * mm, v(103.37, -9.66) * mm, v(104.1, -9.54) * mm, v(104.84, -9.4) * mm]});
            skFitSpline(sketch, "E1052", {"points": [v(104.84, -9.4) * mm, v(105.36, -9.3) * mm, v(105.88, -9.25) * mm, v(106.41, -9.23) * mm]});
            skFitSpline(sketch, "E1053", {"points": [v(106.41, -9.23) * mm, v(107.33, -9.2) * mm, v(108.25, -9.19) * mm, v(109.17, -9.28) * mm]});
            skFitSpline(sketch, "E1054", {"points": [v(109.17, -9.28) * mm, v(109.85, -9.35) * mm, v(110.52, -9.49) * mm, v(111.2, -9.6) * mm]});
            skFitSpline(sketch, "E1055", {"points": [v(111.2, -9.6) * mm, v(111.43, -9.63) * mm, v(111.66, -9.65) * mm, v(111.89, -9.67) * mm]});
            skFitSpline(sketch, "E1056", {"points": [v(111.89, -9.67) * mm, v(112.04, -9.68) * mm, v(112.2, -9.67) * mm, v(112.4, -9.67) * mm]});
            skFitSpline(sketch, "E1057", {"points": [v(112.4, -9.67) * mm, v(111.89, -8.85) * mm, v(111.4, -8.08) * mm, v(110.9, -7.29) * mm]});
            skFitSpline(sketch, "E1058", {"points": [v(110.9, -7.29) * mm, v(110.83, -7.37) * mm, v(110.8, -7.42) * mm, v(110.76, -7.47) * mm]});
            skFitSpline(sketch, "E1059", {"points": [v(110.76, -7.47) * mm, v(110.56, -7.73) * mm, v(110.37, -8) * mm, v(110.17, -8.26) * mm]});
            skFitSpline(sketch, "E1060", {"points": [v(110.17, -8.26) * mm, v(110.12, -8.33) * mm, v(110.05, -8.4) * mm, v(109.97, -8.46) * mm]});
            skFitSpline(sketch, "E1061", {"points": [v(109.97, -8.46) * mm, v(109.75, -8.6) * mm, v(109.46, -8.56) * mm, v(109.3, -8.36) * mm]});
            skFitSpline(sketch, "E1062", {"points": [v(109.3, -8.36) * mm, v(109.13, -8.16) * mm, v(109.15, -7.9) * mm, v(109.35, -7.7) * mm]});
            skFitSpline(sketch, "E1063", {"points": [v(109.35, -7.7) * mm, v(109.43, -7.61) * mm, v(109.5, -7.53) * mm, v(109.57, -7.44) * mm]});
            skFitSpline(sketch, "E1064", {"points": [v(109.57, -7.44) * mm, v(109.83, -7.1) * mm, v(110.08, -6.75) * mm, v(110.34, -6.4) * mm]});
            skFitSpline(sketch, "E1065", {"points": [v(110.34, -6.4) * mm, v(110.09, -5.97) * mm, v(109.83, -5.53) * mm, v(109.55, -5.07) * mm]});
            skFitSpline(sketch, "E1066", {"points": [v(109.55, -5.07) * mm, v(109.35, -5.34) * mm, v(109.16, -5.58) * mm, v(108.98, -5.82) * mm]});
            skFitSpline(sketch, "E1067", {"points": [v(108.98, -5.82) * mm, v(108.89, -5.95) * mm, v(108.79, -6.08) * mm, v(108.63, -6.14) * mm]});
            skFitSpline(sketch, "E1068", {"points": [v(108.63, -6.14) * mm, v(108.42, -6.22) * mm, v(108.18, -6.15) * mm, v(108.05, -5.98) * mm]});
            skFitSpline(sketch, "E1069", {"points": [v(108.05, -5.98) * mm, v(107.91, -5.8) * mm, v(107.92, -5.56) * mm, v(108.06, -5.38) * mm]});
            skFitSpline(sketch, "E1070", {"points": [v(108.06, -5.38) * mm, v(108.28, -5.11) * mm, v(108.5, -4.85) * mm, v(108.7, -4.57) * mm]});
            skFitSpline(sketch, "E1071", {"points": [v(108.7, -4.57) * mm, v(108.82, -4.43) * mm, v(108.9, -4.27) * mm, v(108.99, -4.15) * mm]});
            skFitSpline(sketch, "E1072", {"points": [v(108.99, -4.15) * mm, v(108.59, -3.35) * mm, v(108.2, -2.6) * mm, v(107.82, -1.83) * mm]});
            skFitSpline(sketch, "E1073", {"points": [v(107.82, -1.83) * mm, v(107.73, -1.66) * mm, v(107.64, -1.5) * mm, v(107.54, -1.32) * mm]});
            skFitSpline(sketch, "E1074", {"points": [v(107.54, -1.32) * mm, v(107.5, -1.26) * mm, v(107.46, -1.2) * mm, v(107.4, -1.11) * mm]});
            skFitSpline(sketch, "E1075", {"points": [v(107.4, -1.11) * mm, v(107.33, -1.24) * mm, v(107.27, -1.33) * mm, v(107.22, -1.43) * mm]});
            skFitSpline(sketch, "E1076", {"points": [v(107.22, -1.43) * mm, v(106.77, -2.28) * mm, v(106.33, -3.13) * mm, v(105.88, -3.97) * mm]});
            skFitSpline(sketch, "E1077", {"points": [v(105.88, -3.97) * mm, v(105.82, -4.08) * mm, v(105.82, -4.16) * mm, v(105.89, -4.26) * mm]});
            skFitSpline(sketch, "E1078", {"points": [v(105.89, -4.26) * mm, v(106.16, -4.61) * mm, v(106.4, -4.99) * mm, v(106.7, -5.32) * mm]});
            skFitSpline(sketch, "E1079", {"points": [v(106.7, -5.32) * mm, v(106.87, -5.51) * mm, v(106.89, -5.86) * mm, v(106.73, -6.02) * mm]});
            skFitSpline(sketch, "E1080", {"points": [v(106.73, -6.02) * mm, v(106.54, -6.2) * mm, v(106.23, -6.23) * mm, v(106.02, -6.03) * mm]});
            skFitSpline(sketch, "E1081", {"points": [v(106.02, -6.03) * mm, v(105.93, -5.96) * mm, v(105.87, -5.87) * mm, v(105.8, -5.78) * mm]});
            skFitSpline(sketch, "E1082", {"points": [v(105.8, -5.78) * mm, v(105.63, -5.56) * mm, v(105.45, -5.33) * mm, v(105.25, -5.07) * mm]});
            skFitSpline(sketch, "E1083", {"points": [v(105.25, -5.07) * mm, v(104.97, -5.55) * mm, v(104.72, -5.98) * mm, v(104.47, -6.4) * mm]});
            skFitSpline(sketch, "E1084", {"points": [v(104.47, -6.4) * mm, v(104.58, -6.53) * mm, v(104.66, -6.64) * mm, v(104.74, -6.75) * mm]});
            skFitSpline(sketch, "E1085", {"points": [v(104.74, -6.75) * mm, v(105, -7.08) * mm, v(105.24, -7.4) * mm, v(105.5, -7.73) * mm]});
            skFitSpline(sketch, "E1086", {"points": [v(105.5, -7.73) * mm, v(105.78, -8.08) * mm, v(105.53, -8.45) * mm, v(105.27, -8.52) * mm]});
            skFitSpline(sketch, "E1087", {"points": [v(105.27, -8.52) * mm, v(105.03, -8.58) * mm, v(104.84, -8.51) * mm, v(104.7, -8.33) * mm]});
            skFitSpline(sketch, "E1088", {"points": [v(104.7, -8.33) * mm, v(104.54, -8.13) * mm, v(104.4, -7.93) * mm, v(104.25, -7.73) * mm]});
            skFitSpline(sketch, "E1089", {"points": [v(104.25, -7.73) * mm, v(104.14, -7.6) * mm, v(104.04, -7.45) * mm, v(103.92, -7.29) * mm]});
            skFitSpline(sketch, "E1090", {"points": [v(103.92, -7.29) * mm, v(103.41, -8.08) * mm, v(102.92, -8.85) * mm, v(102.4, -9.67) * mm]});
            skFitSpline(sketch, "E1091", {"points": [v(99, -5.8) * mm, v(98.75, -6.13) * mm, v(98.5, -6.42) * mm, v(98.31, -6.74) * mm]});
            skFitSpline(sketch, "E1092", {"points": [v(98.31, -6.74) * mm, v(97.99, -7.26) * mm, v(97.71, -7.81) * mm, v(97.4, -8.34) * mm]});
            skFitSpline(sketch, "E1093", {"points": [v(97.4, -8.34) * mm, v(97.1, -8.81) * mm, v(96.8, -9.27) * mm, v(96.5, -9.73) * mm]});
            skFitSpline(sketch, "E1094", {"points": [v(96.5, -9.73) * mm, v(96.38, -9.9) * mm, v(96.24, -10.06) * mm, v(96.13, -10.23) * mm]});
            skFitSpline(sketch, "E1095", {"points": [v(96.13, -10.23) * mm, v(96, -10.44) * mm, v(95.8, -10.54) * mm, v(95.55, -10.56) * mm]});
            skFitSpline(sketch, "E1096", {"points": [v(95.55, -10.56) * mm, v(95.08, -10.6) * mm, v(94.6, -10.57) * mm, v(94.14, -10.53) * mm]});
            skFitSpline(sketch, "E1097", {"points": [v(94.14, -10.53) * mm, v(93.77, -10.5) * mm, v(93.4, -10.5) * mm, v(93.02, -10.48) * mm]});
            skFitSpline(sketch, "E1098", {"points": [v(93.02, -10.48) * mm, v(92.67, -10.46) * mm, v(92.32, -10.43) * mm, v(91.97, -10.4) * mm]});
            skFitSpline(sketch, "E1099", {"points": [v(91.97, -10.4) * mm, v(91.64, -10.37) * mm, v(91.32, -10.33) * mm, v(91, -10.3) * mm]});
            skFitSpline(sketch, "E1100", {"points": [v(91, -10.3) * mm, v(90.83, -10.27) * mm, v(90.66, -10.24) * mm, v(90.5, -10.2) * mm]});
            skFitSpline(sketch, "E1101", {"points": [v(90.5, -10.2) * mm, v(90.24, -10.16) * mm, v(90.01, -9.75) * mm, v(90.13, -9.48) * mm]});
            skFitSpline(sketch, "E1102", {"points": [v(90.13, -9.48) * mm, v(90.4, -8.88) * mm, v(90.64, -8.26) * mm, v(90.9, -7.65) * mm]});
            skFitSpline(sketch, "E1103", {"points": [v(90.9, -7.65) * mm, v(90.98, -7.47) * mm, v(91.09, -7.3) * mm, v(91.18, -7.12) * mm]});
            skFitSpline(sketch, "E1104", {"points": [v(91.18, -7.12) * mm, v(91.4, -6.71) * mm, v(91.6, -6.3) * mm, v(91.82, -5.89) * mm]});
            skFitSpline(sketch, "E1105", {"points": [v(91.82, -5.89) * mm, v(91.99, -5.57) * mm, v(92.17, -5.26) * mm, v(92.36, -4.96) * mm]});
            skFitSpline(sketch, "E1106", {"points": [v(92.36, -4.96) * mm, v(92.47, -4.78) * mm, v(92.64, -4.68) * mm, v(92.85, -4.66) * mm]});
            skFitSpline(sketch, "E1107", {"points": [v(92.85, -4.66) * mm, v(93.48, -4.62) * mm, v(94.1, -4.52) * mm, v(94.74, -4.53) * mm]});
            skFitSpline(sketch, "E1108", {"points": [v(94.74, -4.53) * mm, v(95.39, -4.55) * mm, v(96.03, -4.55) * mm, v(96.68, -4.53) * mm]});
            skFitSpline(sketch, "E1109", {"points": [v(96.68, -4.53) * mm, v(97.16, -4.52) * mm, v(97.65, -4.46) * mm, v(98.17, -4.41) * mm]});
            skFitSpline(sketch, "E1110", {"points": [v(98.17, -4.41) * mm, v(97.97, -4.06) * mm, v(97.78, -3.76) * mm, v(97.56, -3.48) * mm]});
            skFitSpline(sketch, "E1111", {"points": [v(97.56, -3.48) * mm, v(97.09, -2.9) * mm, v(96.6, -2.3) * mm, v(96.14, -1.7) * mm]});
            skFitSpline(sketch, "E1112", {"points": [v(96.14, -1.7) * mm, v(95.9, -1.37) * mm, v(95.69, -1.01) * mm, v(95.44, -0.63) * mm]});
            skFitSpline(sketch, "E1113", {"points": [v(95.44, -0.63) * mm, v(95.17, -0.85) * mm, v(94.89, -1.04) * mm, v(94.65, -1.27) * mm]});
            skFitSpline(sketch, "E1114", {"points": [v(94.65, -1.27) * mm, v(94.32, -1.57) * mm, v(94.01, -1.87) * mm, v(93.64, -2.11) * mm]});
            skFitSpline(sketch, "E1115", {"points": [v(93.64, -2.11) * mm, v(93.44, -2.24) * mm, v(93.26, -2.41) * mm, v(93.08, -2.56) * mm]});
            skFitSpline(sketch, "E1116", {"points": [v(93.08, -2.56) * mm, v(93.01, -2.62) * mm, v(92.94, -2.68) * mm, v(92.87, -2.72) * mm]});
            skFitSpline(sketch, "E1117", {"points": [v(92.87, -2.72) * mm, v(92.68, -2.81) * mm, v(92.5, -2.81) * mm, v(92.33, -2.68) * mm]});
            skFitSpline(sketch, "E1118", {"points": [v(92.33, -2.68) * mm, v(92.16, -2.54) * mm, v(92.09, -2.37) * mm, v(92.14, -2.15) * mm]});
            skFitSpline(sketch, "E1119", {"points": [v(92.14, -2.15) * mm, v(92.19, -1.93) * mm, v(92.3, -1.76) * mm, v(92.52, -1.7) * mm]});
            skFitSpline(sketch, "E1120", {"points": [v(92.52, -1.7) * mm, v(92.55, -1.7) * mm, v(92.58, -1.68) * mm, v(92.6, -1.66) * mm]});
            skFitSpline(sketch, "E1121", {"points": [v(92.6, -1.66) * mm, v(92.91, -1.44) * mm, v(93.23, -1.23) * mm, v(93.51, -1) * mm]});
            skFitSpline(sketch, "E1122", {"points": [v(93.51, -1) * mm, v(93.9, -0.68) * mm, v(94.25, -0.33) * mm, v(94.62, 0) * mm]});
            skFitSpline(sketch, "E1123", {"points": [v(94.62, 0) * mm, v(94.63, 0) * mm, v(94.63, 0.02) * mm, v(94.62, 0.02) * mm]});
            skFitSpline(sketch, "E1124", {"points": [v(94.62, 0.02) * mm, v(94.26, 0.33) * mm, v(93.92, 0.66) * mm, v(93.55, 0.95) * mm]});
            skFitSpline(sketch, "E1125", {"points": [v(93.55, 0.95) * mm, v(93.2, 1.23) * mm, v(92.85, 1.52) * mm, v(92.43, 1.72) * mm]});
            skFitSpline(sketch, "E1126", {"points": [v(92.43, 1.72) * mm, v(92.21, 1.83) * mm, v(92.13, 2.03) * mm, v(92.13, 2.25) * mm]});
            skFitSpline(sketch, "E1127", {"points": [v(92.13, 2.25) * mm, v(92.12, 2.46) * mm, v(92.21, 2.63) * mm, v(92.4, 2.72) * mm]});
            skFitSpline(sketch, "E1128", {"points": [v(92.4, 2.72) * mm, v(92.61, 2.82) * mm, v(92.81, 2.78) * mm, v(92.99, 2.64) * mm]});
            skFitSpline(sketch, "E1129", {"points": [v(92.99, 2.64) * mm, v(93.17, 2.49) * mm, v(93.33, 2.32) * mm, v(93.52, 2.2) * mm]});
            skFitSpline(sketch, "E1130", {"points": [v(93.52, 2.2) * mm, v(93.95, 1.9) * mm, v(94.33, 1.57) * mm, v(94.7, 1.21) * mm]});
            skFitSpline(sketch, "E1131", {"points": [v(94.7, 1.21) * mm, v(94.91, 1) * mm, v(95.17, 0.84) * mm, v(95.43, 0.64) * mm]});
            skFitSpline(sketch, "E1132", {"points": [v(95.43, 0.64) * mm, v(95.56, 0.82) * mm, v(95.69, 1) * mm, v(95.8, 1.17) * mm]});
            skFitSpline(sketch, "E1133", {"points": [v(95.8, 1.17) * mm, v(96.07, 1.54) * mm, v(96.32, 1.92) * mm, v(96.6, 2.28) * mm]});
            skFitSpline(sketch, "E1134", {"points": [v(96.6, 2.28) * mm, v(97.02, 2.85) * mm, v(97.47, 3.4) * mm, v(97.9, 3.96) * mm]});
            skFitSpline(sketch, "E1135", {"points": [v(97.9, 3.96) * mm, v(98, 4.08) * mm, v(98.06, 4.22) * mm, v(98.16, 4.37) * mm]});
            skFitSpline(sketch, "E1136", {"points": [v(98.16, 4.37) * mm, v(97.8, 4.44) * mm, v(97.47, 4.49) * mm, v(97.13, 4.5) * mm]});
            skFitSpline(sketch, "E1137", {"points": [v(97.13, 4.5) * mm, v(96.76, 4.51) * mm, v(96.38, 4.5) * mm, v(96.01, 4.5) * mm]});
            skFitSpline(sketch, "E1138", {"points": [v(96.01, 4.5) * mm, v(95.3, 4.52) * mm, v(94.6, 4.53) * mm, v(93.88, 4.55) * mm]});
            skFitSpline(sketch, "E1139", {"points": [v(93.88, 4.55) * mm, v(93.53, 4.57) * mm, v(93.18, 4.62) * mm, v(92.84, 4.65) * mm]});
            skFitSpline(sketch, "E1140", {"points": [v(92.84, 4.65) * mm, v(92.64, 4.67) * mm, v(92.48, 4.77) * mm, v(92.38, 4.93) * mm]});
            skFitSpline(sketch, "E1141", {"points": [v(92.38, 4.93) * mm, v(92.2, 5.2) * mm, v(92, 5.49) * mm, v(91.86, 5.79) * mm]});
            skFitSpline(sketch, "E1142", {"points": [v(91.86, 5.79) * mm, v(91.63, 6.26) * mm, v(91.41, 6.72) * mm, v(91.15, 7.17) * mm]});
            skFitSpline(sketch, "E1143", {"points": [v(91.15, 7.17) * mm, v(91, 7.46) * mm, v(90.86, 7.76) * mm, v(90.72, 8.06) * mm]});
            skFitSpline(sketch, "E1144", {"points": [v(90.72, 8.06) * mm, v(90.58, 8.38) * mm, v(90.44, 8.7) * mm, v(90.3, 9.02) * mm]});
            skFitSpline(sketch, "E1145", {"points": [v(90.3, 9.02) * mm, v(90.23, 9.2) * mm, v(90.17, 9.36) * mm, v(90.11, 9.54) * mm]});
            skFitSpline(sketch, "E1146", {"points": [v(90.11, 9.54) * mm, v(90.02, 9.83) * mm, v(90.25, 10.17) * mm, v(90.56, 10.2) * mm]});
            skFitSpline(sketch, "E1147", {"points": [v(90.56, 10.2) * mm, v(91.01, 10.27) * mm, v(91.47, 10.31) * mm, v(91.91, 10.39) * mm]});
            skFitSpline(sketch, "E1148", {"points": [v(91.91, 10.39) * mm, v(92.46, 10.48) * mm, v(93.01, 10.48) * mm, v(93.56, 10.48) * mm]});
            skFitSpline(sketch, "E1149", {"points": [v(93.56, 10.48) * mm, v(93.85, 10.49) * mm, v(94.13, 10.53) * mm, v(94.42, 10.54) * mm]});
            skFitSpline(sketch, "E1150", {"points": [v(94.42, 10.54) * mm, v(94.81, 10.55) * mm, v(95.2, 10.55) * mm, v(95.6, 10.55) * mm]});
            skFitSpline(sketch, "E1151", {"points": [v(95.6, 10.55) * mm, v(95.8, 10.54) * mm, v(95.97, 10.45) * mm, v(96.08, 10.28) * mm]});
            skFitSpline(sketch, "E1152", {"points": [v(96.08, 10.28) * mm, v(96.51, 9.65) * mm, v(96.96, 9.03) * mm, v(97.37, 8.38) * mm]});
            skFitSpline(sketch, "E1153", {"points": [v(97.37, 8.38) * mm, v(97.69, 7.87) * mm, v(97.95, 7.33) * mm, v(98.26, 6.82) * mm]});
            skFitSpline(sketch, "E1154", {"points": [v(98.26, 6.82) * mm, v(98.47, 6.47) * mm, v(98.72, 6.16) * mm, v(98.98, 5.8) * mm]});
            skFitSpline(sketch, "E1155", {"points": [v(98.98, 5.8) * mm, v(99.25, 6.26) * mm, v(99.44, 6.7) * mm, v(99.6, 7.16) * mm]});
            skFitSpline(sketch, "E1156", {"points": [v(99.6, 7.16) * mm, v(99.89, 7.94) * mm, v(100.17, 8.73) * mm, v(100.6, 9.46) * mm]});
            skFitSpline(sketch, "E1157", {"points": [v(100.6, 9.46) * mm, v(100.7, 9.63) * mm, v(100.76, 9.82) * mm, v(100.86, 10.03) * mm]});
            skFitSpline(sketch, "E1158", {"points": [v(100.86, 10.03) * mm, v(100.6, 10.17) * mm, v(100.31, 10.29) * mm, v(100.03, 10.38) * mm]});
            skFitSpline(sketch, "E1159", {"points": [v(100.03, 10.38) * mm, v(99.87, 10.44) * mm, v(99.7, 10.48) * mm, v(99.53, 10.53) * mm]});
            skFitSpline(sketch, "E1160", {"points": [v(99.53, 10.53) * mm, v(99.3, 10.61) * mm, v(99.08, 10.7) * mm, v(98.86, 10.8) * mm]});
            skFitSpline(sketch, "E1161", {"points": [v(98.86, 10.8) * mm, v(98.6, 10.9) * mm, v(98.33, 11) * mm, v(98.06, 11.11) * mm]});
            skFitSpline(sketch, "E1162", {"points": [v(98.06, 11.11) * mm, v(97.96, 11.15) * mm, v(97.84, 11.19) * mm, v(97.76, 11.25) * mm]});
            skFitSpline(sketch, "E1163", {"points": [v(97.76, 11.25) * mm, v(97.46, 11.46) * mm, v(97.47, 11.87) * mm, v(97.78, 12.08) * mm]});
            skFitSpline(sketch, "E1164", {"points": [v(97.78, 12.08) * mm, v(98, 12.22) * mm, v(98.34, 12.22) * mm, v(98.5, 12.04) * mm]});
            skFitSpline(sketch, "E1165", {"points": [v(98.5, 12.04) * mm, v(98.51, 12.02) * mm, v(98.54, 12) * mm, v(98.56, 11.98) * mm]});
            skFitSpline(sketch, "E1166", {"points": [v(98.56, 11.98) * mm, v(98.97, 11.81) * mm, v(99.37, 11.64) * mm, v(99.78, 11.48) * mm]});
            skFitSpline(sketch, "E1167", {"points": [v(99.78, 11.48) * mm, v(100.14, 11.34) * mm, v(100.52, 11.22) * mm, v(100.89, 11.1) * mm]});
            skFitSpline(sketch, "E1168", {"points": [v(100.89, 11.1) * mm, v(100.93, 11.08) * mm, v(100.97, 11.07) * mm, v(101, 11.06) * mm]});
            skFitSpline(sketch, "E1169", {"points": [v(101, 11.06) * mm, v(101.12, 11.61) * mm, v(101.25, 12.16) * mm, v(101.35, 12.7) * mm]});
            skFitSpline(sketch, "E1170", {"points": [v(101.35, 12.7) * mm, v(101.4, 13) * mm, v(101.42, 13.32) * mm, v(101.45, 13.63) * mm]});
            skFitSpline(sketch, "E1171", {"points": [v(101.45, 13.63) * mm, v(101.45, 13.67) * mm, v(101.43, 13.7) * mm, v(101.43, 13.75) * mm]});
            skFitSpline(sketch, "E1172", {"points": [v(101.43, 13.75) * mm, v(101.38, 14.04) * mm, v(101.55, 14.3) * mm, v(101.83, 14.4) * mm]});
            skFitSpline(sketch, "E1173", {"points": [v(101.83, 14.4) * mm, v(102.15, 14.52) * mm, v(102.47, 14.3) * mm, v(102.48, 13.95) * mm]});
            skFitSpline(sketch, "E1174", {"points": [v(102.48, 13.95) * mm, v(102.48, 13.85) * mm, v(102.46, 13.75) * mm, v(102.45, 13.64) * mm]});
            skFitSpline(sketch, "E1175", {"points": [v(102.45, 13.64) * mm, v(102.4, 13.33) * mm, v(102.37, 13.01) * mm, v(102.32, 12.7) * mm]});
            skFitSpline(sketch, "E1176", {"points": [v(102.32, 12.7) * mm, v(102.3, 12.48) * mm, v(102.25, 12.27) * mm, v(102.21, 12.06) * mm]});
            skFitSpline(sketch, "E1177", {"points": [v(102.21, 12.06) * mm, v(102.14, 11.66) * mm, v(102.07, 11.26) * mm, v(102, 10.86) * mm]});
            skFitSpline(sketch, "E1178", {"points": [v(102, 10.86) * mm, v(101.99, 10.8) * mm, v(102, 10.75) * mm, v(102, 10.68) * mm]});
            skFitSpline(sketch, "E1179", {"points": [v(102, 10.68) * mm, v(102.24, 10.66) * mm, v(102.48, 10.63) * mm, v(102.71, 10.63) * mm]});
            skFitSpline(sketch, "E1180", {"points": [v(102.71, 10.63) * mm, v(103.15, 10.62) * mm, v(103.59, 10.57) * mm, v(104.02, 10.5) * mm]});
            skFitSpline(sketch, "E1181", {"points": [v(104.02, 10.5) * mm, v(104.71, 10.39) * mm, v(105.4, 10.3) * mm, v(106.1, 10.2) * mm]});
            skFitSpline(sketch, "E1182", {"points": [v(106.1, 10.2) * mm, v(106.25, 10.18) * mm, v(106.4, 10.2) * mm, v(106.54, 10.2) * mm]});
            skFitSpline(sketch, "E1183", {"points": [v(106.54, 10.2) * mm, v(106.54, 10.24) * mm, v(106.55, 10.27) * mm, v(106.54, 10.3) * mm]});
            skFitSpline(sketch, "E1184", {"points": [v(106.54, 10.3) * mm, v(106.38, 10.65) * mm, v(106.24, 11) * mm, v(106.06, 11.34) * mm]});
            skFitSpline(sketch, "E1185", {"points": [v(106.06, 11.34) * mm, v(105.78, 11.85) * mm, v(105.46, 12.34) * mm, v(105.18, 12.85) * mm]});
            skFitSpline(sketch, "E1186", {"points": [v(105.18, 12.85) * mm, v(104.92, 13.32) * mm, v(104.7, 13.8) * mm, v(104.45, 14.28) * mm]});
            skFitSpline(sketch, "E1187", {"points": [v(104.45, 14.28) * mm, v(104.36, 14.48) * mm, v(104.29, 14.68) * mm, v(104.19, 14.87) * mm]});
            skFitSpline(sketch, "E1188", {"points": [v(104.19, 14.87) * mm, v(104.07, 15.1) * mm, v(104.07, 15.34) * mm, v(104.2, 15.56) * mm]});
            skFitSpline(sketch, "E1189", {"points": [v(104.2, 15.56) * mm, v(104.39, 15.9) * mm, v(104.58, 16.22) * mm, v(104.78, 16.55) * mm]});
            skFitSpline(sketch, "E1190", {"points": [v(104.78, 16.55) * mm, v(105, 16.88) * mm, v(105.21, 17.22) * mm, v(105.43, 17.55) * mm]});
            skFitSpline(sketch, "E1191", {"points": [v(105.43, 17.55) * mm, v(105.64, 17.87) * mm, v(105.85, 18.2) * mm, v(106.07, 18.5) * mm]});
            skFitSpline(sketch, "E1192", {"points": [v(106.07, 18.5) * mm, v(106.26, 18.78) * mm, v(106.47, 19.05) * mm, v(106.67, 19.31) * mm]});
            skFitSpline(sketch, "E1193", {"points": [v(106.67, 19.31) * mm, v(106.78, 19.46) * mm, v(106.9, 19.6) * mm, v(107.02, 19.74) * mm]});
            skFitSpline(sketch, "E1194", {"points": [v(107.02, 19.74) * mm, v(107.24, 19.96) * mm, v(107.63, 19.94) * mm, v(107.83, 19.7) * mm]});
            skFitSpline(sketch, "E1195", {"points": [v(107.83, 19.7) * mm, v(108.46, 18.87) * mm, v(109.13, 18.07) * mm, v(109.62, 17.15) * mm]});
            skFitSpline(sketch, "E1196", {"points": [v(109.62, 17.15) * mm, v(109.75, 16.9) * mm, v(109.93, 16.7) * mm, v(110.08, 16.47) * mm]});
            skFitSpline(sketch, "E1197", {"points": [v(110.08, 16.47) * mm, v(110.27, 16.16) * mm, v(110.46, 15.85) * mm, v(110.63, 15.52) * mm]});
            skFitSpline(sketch, "E1198", {"points": [v(110.63, 15.52) * mm, v(110.74, 15.32) * mm, v(110.74, 15.11) * mm, v(110.64, 14.9) * mm]});
            skFitSpline(sketch, "E1199", {"points": [v(110.64, 14.9) * mm, v(110.3, 14.24) * mm, v(110, 13.56) * mm, v(109.66, 12.9) * mm]});
            skFitSpline(sketch, "E1200", {"points": [v(109.66, 12.9) * mm, v(109.38, 12.37) * mm, v(109.04, 11.87) * mm, v(108.75, 11.35) * mm]});
            skFitSpline(sketch, "E1201", {"points": [v(108.75, 11.35) * mm, v(108.57, 11.02) * mm, v(108.44, 10.67) * mm, v(108.28, 10.33) * mm]});
            skFitSpline(sketch, "E1202", {"points": [v(108.28, 10.33) * mm, v(108.27, 10.3) * mm, v(108.27, 10.25) * mm, v(108.26, 10.2) * mm]});
            skFitSpline(sketch, "E1203", {"points": [v(108.26, 10.2) * mm, v(108.62, 10.17) * mm, v(108.97, 10.2) * mm, v(109.31, 10.26) * mm]});
            skFitSpline(sketch, "E1204", {"points": [v(109.31, 10.26) * mm, v(110.1, 10.37) * mm, v(110.87, 10.5) * mm, v(111.65, 10.62) * mm]});
            skFitSpline(sketch, "E1205", {"points": [v(111.65, 10.62) * mm, v(111.7, 10.62) * mm, v(111.77, 10.62) * mm, v(111.82, 10.62) * mm]});
            skFitSpline(sketch, "E1206", {"points": [v(111.82, 10.62) * mm, v(112.15, 10.64) * mm, v(112.47, 10.65) * mm, v(112.83, 10.67) * mm]});
            skFitSpline(sketch, "E1207", {"points": [v(112.83, 10.67) * mm, v(112.82, 10.77) * mm, v(112.81, 10.86) * mm, v(112.8, 10.94) * mm]});
            skFitSpline(sketch, "E1208", {"points": [v(112.8, 10.94) * mm, v(112.75, 11.24) * mm, v(112.73, 11.56) * mm, v(112.65, 11.86) * mm]});
            skFitSpline(sketch, "E1209", {"points": [v(112.65, 11.86) * mm, v(112.54, 12.24) * mm, v(112.5, 12.62) * mm, v(112.46, 13) * mm]});
            skFitSpline(sketch, "E1210", {"points": [v(112.46, 13) * mm, v(112.43, 13.25) * mm, v(112.38, 13.48) * mm, v(112.35, 13.72) * mm]});
            skFitSpline(sketch, "E1211", {"points": [v(112.35, 13.72) * mm, v(112.33, 13.8) * mm, v(112.32, 13.9) * mm, v(112.32, 13.98) * mm]});
            skFitSpline(sketch, "E1212", {"points": [v(112.32, 13.98) * mm, v(112.35, 14.33) * mm, v(112.7, 14.53) * mm, v(113.03, 14.38) * mm]});
            skFitSpline(sketch, "E1213", {"points": [v(113.03, 14.38) * mm, v(113.3, 14.26) * mm, v(113.4, 14.03) * mm, v(113.38, 13.72) * mm]});
            skFitSpline(sketch, "E1214", {"points": [v(113.38, 13.72) * mm, v(113.37, 13.51) * mm, v(113.43, 13.3) * mm, v(113.43, 13.08) * mm]});
            skFitSpline(sketch, "E1215", {"points": [v(113.43, 13.08) * mm, v(113.44, 12.5) * mm, v(113.67, 11.98) * mm, v(113.73, 11.41) * mm]});
            skFitSpline(sketch, "E1216", {"points": [v(113.73, 11.41) * mm, v(113.74, 11.3) * mm, v(113.76, 11.18) * mm, v(113.77, 11.05) * mm]});
            skFitSpline(sketch, "E1217", {"points": [v(113.77, 11.05) * mm, v(113.85, 11.07) * mm, v(113.9, 11.1) * mm, v(113.97, 11.11) * mm]});
            skFitSpline(sketch, "E1218", {"points": [v(113.97, 11.11) * mm, v(114.3, 11.23) * mm, v(114.63, 11.33) * mm, v(114.96, 11.46) * mm]});
            skFitSpline(sketch, "E1219", {"points": [v(114.96, 11.46) * mm, v(115.29, 11.58) * mm, v(115.61, 11.72) * mm, v(115.93, 11.85) * mm]});
            skFitSpline(sketch, "E1220", {"points": [v(115.93, 11.85) * mm, v(116.1, 11.92) * mm, v(116.25, 11.99) * mm, v(116.4, 12.1) * mm]});
            skFitSpline(sketch, "E1221", {"points": [v(116.4, 12.1) * mm, v(116.59, 12.24) * mm, v(116.8, 12.2) * mm, v(117, 12.09) * mm]});
            skFitSpline(sketch, "E1222", {"points": [v(117, 12.09) * mm, v(117.19, 11.98) * mm, v(117.28, 11.82) * mm, v(117.26, 11.6) * mm]});
            skFitSpline(sketch, "E1223", {"points": [v(117.26, 11.6) * mm, v(117.24, 11.38) * mm, v(117.1, 11.25) * mm, v(116.9, 11.17) * mm]});
            skFitSpline(sketch, "E1224", {"points": [v(116.9, 11.17) * mm, v(116.51, 11) * mm, v(116.11, 10.84) * mm, v(115.71, 10.68) * mm]});
            skFitSpline(sketch, "E1225", {"points": [v(115.71, 10.68) * mm, v(115.57, 10.62) * mm, v(115.41, 10.57) * mm, v(115.26, 10.53) * mm]});
            skFitSpline(sketch, "E1226", {"points": [v(115.26, 10.53) * mm, v(114.8, 10.41) * mm, v(114.38, 10.25) * mm, v(113.94, 10.03) * mm]});
            skFitSpline(sketch, "E1227", {"points": [v(113.94, 10.03) * mm, v(114.06, 9.79) * mm, v(114.18, 9.56) * mm, v(114.3, 9.32) * mm]});
            skFitSpline(sketch, "E1228", {"points": [v(114.3, 9.32) * mm, v(114.44, 9.03) * mm, v(114.6, 8.74) * mm, v(114.71, 8.44) * mm]});
            skFitSpline(sketch, "E1229", {"points": [v(114.71, 8.44) * mm, v(114.93, 7.9) * mm, v(115.12, 7.34) * mm, v(115.34, 6.8) * mm]});
            skFitSpline(sketch, "E1230", {"points": [v(115.34, 6.8) * mm, v(115.47, 6.47) * mm, v(115.64, 6.16) * mm, v(115.82, 5.78) * mm]});
            skFitSpline(sketch, "E1231", {"points": [v(115.82, 5.78) * mm, v(116.07, 6.14) * mm, v(116.32, 6.43) * mm, v(116.51, 6.75) * mm]});
            skFitSpline(sketch, "E1232", {"points": [v(116.51, 6.75) * mm, v(116.83, 7.27) * mm, v(117.1, 7.81) * mm, v(117.42, 8.33) * mm]});
            skFitSpline(sketch, "E1233", {"points": [v(117.42, 8.33) * mm, v(117.69, 8.79) * mm, v(117.99, 9.22) * mm, v(118.28, 9.66) * mm]});
            skFitSpline(sketch, "E1234", {"points": [v(118.28, 9.66) * mm, v(118.41, 9.86) * mm, v(118.56, 10.05) * mm, v(118.7, 10.25) * mm]});
            skFitSpline(sketch, "E1235", {"points": [v(118.7, 10.25) * mm, v(118.83, 10.44) * mm, v(119, 10.52) * mm, v(119.24, 10.55) * mm]});
            skFitSpline(sketch, "E1236", {"points": [v(119.24, 10.55) * mm, v(119.71, 10.6) * mm, v(120.18, 10.56) * mm, v(120.65, 10.53) * mm]});
            skFitSpline(sketch, "E1237", {"points": [v(120.65, 10.53) * mm, v(120.97, 10.5) * mm, v(121.29, 10.48) * mm, v(121.6, 10.48) * mm]});
            skFitSpline(sketch, "E1238", {"points": [v(121.6, 10.48) * mm, v(122.08, 10.5) * mm, v(122.54, 10.44) * mm, v(123.01, 10.37) * mm]});
            skFitSpline(sketch, "E1239", {"points": [v(123.01, 10.37) * mm, v(123.27, 10.34) * mm, v(123.54, 10.32) * mm, v(123.8, 10.29) * mm]});
            skFitSpline(sketch, "E1240", {"points": [v(123.8, 10.29) * mm, v(123.98, 10.26) * mm, v(124.16, 10.23) * mm, v(124.34, 10.2) * mm]});
            skFitSpline(sketch, "E1241", {"points": [v(124.34, 10.2) * mm, v(124.56, 10.14) * mm, v(124.8, 9.77) * mm, v(124.69, 9.5) * mm]});
            skFitSpline(sketch, "E1242", {"points": [v(124.69, 9.5) * mm, v(124.28, 8.56) * mm, v(123.95, 7.6) * mm, v(123.4, 6.72) * mm]});
            skFitSpline(sketch, "E1243", {"points": [v(123.4, 6.72) * mm, v(123.24, 6.45) * mm, v(123.14, 6.15) * mm, v(123, 5.88) * mm]});
            skFitSpline(sketch, "E1244", {"points": [v(123, 5.88) * mm, v(122.82, 5.56) * mm, v(122.64, 5.25) * mm, v(122.45, 4.95) * mm]});
            skFitSpline(sketch, "E1245", {"points": [v(122.45, 4.95) * mm, v(122.33, 4.76) * mm, v(122.14, 4.66) * mm, v(121.9, 4.65) * mm]});
            skFitSpline(sketch, "E1246", {"points": [v(121.9, 4.65) * mm, v(121.28, 4.6) * mm, v(120.66, 4.5) * mm, v(120.02, 4.53) * mm]});
            skFitSpline(sketch, "E1247", {"points": [v(120.02, 4.53) * mm, v(119.5, 4.54) * mm, v(118.97, 4.54) * mm, v(118.45, 4.53) * mm]});
            skFitSpline(sketch, "E1248", {"points": [v(118.45, 4.53) * mm, v(118.05, 4.52) * mm, v(117.65, 4.48) * mm, v(117.25, 4.45) * mm]});
            skFitSpline(sketch, "E1249", {"points": [v(117.25, 4.45) * mm, v(117.06, 4.44) * mm, v(116.88, 4.4) * mm, v(116.65, 4.38) * mm]});
            skFitSpline(sketch, "E1250", {"points": [v(116.65, 4.38) * mm, v(116.73, 4.24) * mm, v(116.8, 4.11) * mm, v(116.88, 4) * mm]});
            skFitSpline(sketch, "E1251", {"points": [v(116.88, 4) * mm, v(117.12, 3.68) * mm, v(117.38, 3.37) * mm, v(117.63, 3.04) * mm]});
            skFitSpline(sketch, "E1252", {"points": [v(117.63, 3.04) * mm, v(118.1, 2.42) * mm, v(118.63, 1.84) * mm, v(119.02, 1.15) * mm]});
            skFitSpline(sketch, "E1253", {"points": [v(119.02, 1.15) * mm, v(119.11, 0.98) * mm, v(119.24, 0.83) * mm, v(119.37, 0.64) * mm]});
            skFitSpline(sketch, "E1254", {"points": [v(119.37, 0.64) * mm, v(119.65, 0.84) * mm, v(119.94, 1.03) * mm, v(120.18, 1.27) * mm]});
            skFitSpline(sketch, "E1255", {"points": [v(120.18, 1.27) * mm, v(120.5, 1.57) * mm, v(120.8, 1.87) * mm, v(121.17, 2.1) * mm]});
            skFitSpline(sketch, "E1256", {"points": [v(121.17, 2.1) * mm, v(121.38, 2.23) * mm, v(121.56, 2.41) * mm, v(121.75, 2.57) * mm]});
            skFitSpline(sketch, "E1257", {"points": [v(121.75, 2.57) * mm, v(121.86, 2.67) * mm, v(121.97, 2.75) * mm, v(122.12, 2.77) * mm]});
            skFitSpline(sketch, "E1258", {"points": [v(122.12, 2.77) * mm, v(122.42, 2.8) * mm, v(122.67, 2.59) * mm, v(122.68, 2.28) * mm]});
            skFitSpline(sketch, "E1259", {"points": [v(122.68, 2.28) * mm, v(122.69, 2) * mm, v(122.56, 1.8) * mm, v(122.29, 1.7) * mm]});
            skFitSpline(sketch, "E1260", {"points": [v(122.29, 1.7) * mm, v(122.25, 1.68) * mm, v(122.21, 1.66) * mm, v(122.18, 1.64) * mm]});
            skFitSpline(sketch, "E1261", {"points": [v(122.18, 1.64) * mm, v(121.9, 1.43) * mm, v(121.6, 1.24) * mm, v(121.33, 1.01) * mm]});
            skFitSpline(sketch, "E1262", {"points": [v(121.33, 1.01) * mm, v(120.94, 0.69) * mm, v(120.57, 0.33) * mm, v(120.19, -0.02) * mm]});
            skFitSpline(sketch, "E1263", {"points": [v(120.19, -0.02) * mm, v(120.19, -0.01) * mm, v(120.2, -0.03) * mm, v(120.2, -0.04) * mm]});
            skFitSpline(sketch, "E1264", {"points": [v(120.2, -0.04) * mm, v(120.55, -0.34) * mm, v(120.89, -0.66) * mm, v(121.25, -0.95) * mm]});
            skFitSpline(sketch, "E1265", {"points": [v(121.25, -0.95) * mm, v(121.56, -1.2) * mm, v(121.89, -1.43) * mm, v(122.2, -1.67) * mm]});
            skFitSpline(sketch, "E1266", {"points": [v(122.2, -1.67) * mm, v(122.23, -1.69) * mm, v(122.26, -1.7) * mm, v(122.3, -1.7) * mm]});
            skFitSpline(sketch, "E1267", {"points": [v(122.3, -1.7) * mm, v(122.61, -1.79) * mm, v(122.7, -2.12) * mm, v(122.68, -2.35) * mm]});
            skFitSpline(sketch, "E1268", {"points": [v(122.68, -2.35) * mm, v(122.63, -2.7) * mm, v(122.27, -2.88) * mm, v(121.96, -2.73) * mm]});
            skFitSpline(sketch, "E1269", {"points": [v(121.96, -2.73) * mm, v(121.87, -2.68) * mm, v(121.8, -2.62) * mm, v(121.72, -2.56) * mm]});
            skFitSpline(sketch, "E1270", {"points": [v(121.72, -2.56) * mm, v(121.47, -2.36) * mm, v(121.22, -2.17) * mm, v(120.97, -1.97) * mm]});
            skFitSpline(sketch, "E1271", {"points": [v(120.97, -1.97) * mm, v(120.8, -1.83) * mm, v(120.61, -1.7) * mm, v(120.45, -1.54) * mm]});
            skFitSpline(sketch, "E1272", {"points": [v(120.45, -1.54) * mm, v(120.13, -1.2) * mm, v(119.77, -0.92) * mm, v(119.37, -0.65) * mm]});
            skFitSpline(sketch, "E1273", {"points": [v(119.37, -0.65) * mm, v(119.23, -0.86) * mm, v(119.09, -1.07) * mm, v(118.95, -1.27) * mm]});
            skFitSpline(sketch, "E1274", {"points": [v(118.95, -1.27) * mm, v(118.76, -1.55) * mm, v(118.58, -1.85) * mm, v(118.37, -2.12) * mm]});
            skFitSpline(sketch, "E1275", {"points": [v(118.37, -2.12) * mm, v(118, -2.58) * mm, v(117.62, -3.02) * mm, v(117.26, -3.47) * mm]});
            skFitSpline(sketch, "E1276", {"points": [v(117.26, -3.47) * mm, v(117.04, -3.76) * mm, v(116.85, -4.06) * mm, v(116.63, -4.39) * mm]});
            skFitSpline(sketch, "E1277", {"points": [v(116.63, -4.39) * mm, v(117, -4.43) * mm, v(117.32, -4.5) * mm, v(117.64, -4.51) * mm]});
            skFitSpline(sketch, "E1278", {"points": [v(117.64, -4.51) * mm, v(118.28, -4.53) * mm, v(118.92, -4.5) * mm, v(119.55, -4.52) * mm]});
            skFitSpline(sketch, "E1279", {"points": [v(119.55, -4.52) * mm, v(120.18, -4.53) * mm, v(120.82, -4.51) * mm, v(121.44, -4.62) * mm]});
            skFitSpline(sketch, "E1280", {"points": [v(121.44, -4.62) * mm, v(121.59, -4.65) * mm, v(121.74, -4.66) * mm, v(121.9, -4.66) * mm]});
            skFitSpline(sketch, "E1281", {"points": [v(121.9, -4.66) * mm, v(122.17, -4.67) * mm, v(122.37, -4.8) * mm, v(122.5, -5.03) * mm]});
            skFitSpline(sketch, "E1282", {"points": [v(122.5, -5.03) * mm, v(122.69, -5.35) * mm, v(122.87, -5.68) * mm, v(123.05, -6) * mm]});
            skFitSpline(sketch, "E1283", {"points": [v(123.05, -6) * mm, v(123.26, -6.4) * mm, v(123.47, -6.8) * mm, v(123.67, -7.2) * mm]});
            skFitSpline(sketch, "E1284", {"points": [v(123.67, -7.2) * mm, v(123.8, -7.46) * mm, v(123.94, -7.72) * mm, v(124.06, -8) * mm]});
            skFitSpline(sketch, "E1285", {"points": [v(124.06, -8) * mm, v(124.21, -8.34) * mm, v(124.36, -8.7) * mm, v(124.51, -9.05) * mm]});
            skFitSpline(sketch, "E1286", {"points": [v(124.51, -9.05) * mm, v(124.58, -9.22) * mm, v(124.65, -9.39) * mm, v(124.7, -9.56) * mm]});
            skFitSpline(sketch, "E1287", {"points": [v(124.7, -9.56) * mm, v(124.79, -9.85) * mm, v(124.55, -10.18) * mm, v(124.23, -10.22) * mm]});
            skFitSpline(sketch, "E1288", {"points": [v(124.23, -10.22) * mm, v(123.8, -10.28) * mm, v(123.38, -10.32) * mm, v(122.95, -10.4) * mm]});
            skFitSpline(sketch, "E1289", {"points": [v(122.95, -10.4) * mm, v(122.44, -10.47) * mm, v(121.92, -10.5) * mm, v(121.4, -10.49) * mm]});
            skFitSpline(sketch, "E1290", {"points": [v(121.4, -10.49) * mm, v(121.1, -10.49) * mm, v(120.78, -10.53) * mm, v(120.47, -10.54) * mm]});
            skFitSpline(sketch, "E1291", {"points": [v(120.47, -10.54) * mm, v(120.06, -10.55) * mm, v(119.66, -10.56) * mm, v(119.25, -10.56) * mm]});
            skFitSpline(sketch, "E1292", {"points": [v(119.25, -10.56) * mm, v(119.01, -10.56) * mm, v(118.83, -10.45) * mm, v(118.7, -10.24) * mm]});
            skFitSpline(sketch, "E1293", {"points": [v(118.7, -10.24) * mm, v(118.28, -9.63) * mm, v(117.85, -9.04) * mm, v(117.46, -8.42) * mm]});
            skFitSpline(sketch, "E1294", {"points": [v(117.46, -8.42) * mm, v(117.14, -7.9) * mm, v(116.88, -7.37) * mm, v(116.57, -6.86) * mm]});
            skFitSpline(sketch, "E1295", {"points": [v(116.57, -6.86) * mm, v(116.35, -6.5) * mm, v(116.1, -6.18) * mm, v(115.84, -5.81) * mm]});
            skFitSpline(sketch, "E1296", {"points": [v(115.84, -5.81) * mm, v(115.63, -6.16) * mm, v(115.46, -6.48) * mm, v(115.33, -6.82) * mm]});
            skFitSpline(sketch, "E1297", {"points": [v(115.33, -6.82) * mm, v(115.06, -7.51) * mm, v(114.8, -8.2) * mm, v(114.52, -8.9) * mm]});
            skFitSpline(sketch, "E1298", {"points": [v(114.52, -8.9) * mm, v(114.35, -9.28) * mm, v(114.14, -9.65) * mm, v(113.94, -10.04) * mm]});
            skFitSpline(sketch, "E1299", {"points": [v(113.94, -10.04) * mm, v(114.3, -10.22) * mm, v(114.66, -10.38) * mm, v(115.04, -10.47) * mm]});
            skFitSpline(sketch, "E1300", {"points": [v(115.04, -10.47) * mm, v(115.4, -10.57) * mm, v(115.74, -10.7) * mm, v(116.07, -10.86) * mm]});
            skFitSpline(sketch, "E1301", {"points": [v(116.07, -10.86) * mm, v(116.32, -10.98) * mm, v(116.59, -11.06) * mm, v(116.85, -11.15) * mm]});
            skFitSpline(sketch, "E1302", {"points": [v(116.85, -11.15) * mm, v(117.06, -11.23) * mm, v(117.22, -11.34) * mm, v(117.26, -11.58) * mm]});
            skFitSpline(sketch, "E1303", {"points": [v(117.26, -11.58) * mm, v(117.29, -11.8) * mm, v(117.21, -11.98) * mm, v(117.02, -12.09) * mm]});
            skFitSpline(sketch, "E1304", {"points": [v(117.02, -12.09) * mm, v(116.81, -12.21) * mm, v(116.6, -12.24) * mm, v(116.38, -12.1) * mm]});
            skFitSpline(sketch, "E1305", {"points": [v(116.38, -12.1) * mm, v(116.26, -12.03) * mm, v(116.13, -11.95) * mm, v(116, -11.89) * mm]});
            skFitSpline(sketch, "E1306", {"points": [v(116, -11.89) * mm, v(115.5, -11.65) * mm, v(115, -11.46) * mm, v(114.47, -11.31) * mm]});
            skFitSpline(sketch, "E1307", {"points": [v(114.47, -11.31) * mm, v(114.24, -11.25) * mm, v(114.03, -11.15) * mm, v(113.77, -11.05) * mm]});
            skFitSpline(sketch, "E1308", {"points": [v(113.77, -11.05) * mm, v(113.76, -11.18) * mm, v(113.75, -11.3) * mm, v(113.73, -11.4) * mm]});
            skFitSpline(sketch, "E1309", {"points": [v(113.73, -11.4) * mm, v(113.67, -11.72) * mm, v(113.58, -12.04) * mm, v(113.53, -12.36) * mm]});
            skFitSpline(sketch, "E1310", {"points": [v(113.53, -12.36) * mm, v(113.48, -12.65) * mm, v(113.45, -12.95) * mm, v(113.42, -13.24) * mm]});
            skFitSpline(sketch, "E1311", {"points": [v(113.42, -13.24) * mm, v(113.4, -13.45) * mm, v(113.37, -13.66) * mm, v(113.4, -13.88) * mm]});
            skFitSpline(sketch, "E1312", {"points": [v(113.4, -13.88) * mm, v(113.43, -14.17) * mm, v(113.06, -14.47) * mm, v(112.77, -14.44) * mm]});
            skFitSpline(sketch, "E1313", {"points": [v(112.77, -14.44) * mm, v(112.46, -14.4) * mm, v(112.27, -14.13) * mm, v(112.33, -13.79) * mm]});
            skFitSpline(sketch, "E1314", {"points": [v(112.33, -13.79) * mm, v(112.37, -13.5) * mm, v(112.46, -13.23) * mm, v(112.47, -12.94) * mm]});
            skFitSpline(sketch, "E1315", {"points": [v(112.47, -12.94) * mm, v(112.48, -12.37) * mm, v(112.7, -11.84) * mm, v(112.77, -11.27) * mm]});
            skFitSpline(sketch, "E1316", {"points": [v(112.77, -11.27) * mm, v(112.79, -11.09) * mm, v(112.8, -10.9) * mm, v(112.83, -10.69) * mm]});
            skFitSpline(sketch, "E1317", {"points": [v(112.83, -10.69) * mm, v(112.59, -10.67) * mm, v(112.36, -10.63) * mm, v(112.13, -10.63) * mm]});
            skFitSpline(sketch, "E1318", {"points": [v(112.13, -10.63) * mm, v(111.67, -10.63) * mm, v(111.22, -10.58) * mm, v(110.77, -10.5) * mm]});
            skFitSpline(sketch, "E1319", {"points": [v(110.77, -10.5) * mm, v(110.2, -10.41) * mm, v(109.62, -10.32) * mm, v(109.05, -10.24) * mm]});
            skFitSpline(sketch, "E1320", {"points": [v(109.05, -10.24) * mm, v(108.8, -10.2) * mm, v(108.53, -10.2) * mm, v(108.22, -10.19) * mm]});
            skFitSpline(sketch, "E1321", {"points": [v(108.22, -10.19) * mm, v(108.39, -10.58) * mm, v(108.52, -10.93) * mm, v(108.7, -11.25) * mm]});
            skFitSpline(sketch, "E1322", {"points": [v(108.7, -11.25) * mm, v(108.99, -11.8) * mm, v(109.32, -12.31) * mm, v(109.62, -12.85) * mm]});
            skFitSpline(sketch, "E1323", {"points": [v(109.62, -12.85) * mm, v(109.88, -13.31) * mm, v(110.1, -13.79) * mm, v(110.34, -14.26) * mm]});
            skFitSpline(sketch, "E1324", {"points": [v(110.34, -14.26) * mm, v(110.45, -14.47) * mm, v(110.53, -14.7) * mm, v(110.64, -14.91) * mm]});
            skFitSpline(sketch, "E1325", {"points": [v(110.64, -14.91) * mm, v(110.73, -15.11) * mm, v(110.74, -15.32) * mm, v(110.64, -15.51) * mm]});
            skFitSpline(sketch, "E1326", {"points": [v(110.64, -15.51) * mm, v(110.48, -15.81) * mm, v(110.31, -16.11) * mm, v(110.13, -16.4) * mm]});
            skFitSpline(sketch, "E1327", {"points": [v(110.13, -16.4) * mm, v(109.88, -16.81) * mm, v(109.62, -17.21) * mm, v(109.35, -17.61) * mm]});
            skFitSpline(sketch, "E1328", {"points": [v(109.35, -17.61) * mm, v(109.14, -17.92) * mm, v(108.93, -18.23) * mm, v(108.72, -18.54) * mm]});
            skFitSpline(sketch, "E1329", {"points": [v(108.72, -18.54) * mm, v(108.53, -18.8) * mm, v(108.34, -19.06) * mm, v(108.15, -19.31) * mm]});
            skFitSpline(sketch, "E1330", {"points": [v(108.15, -19.31) * mm, v(108.04, -19.46) * mm, v(107.91, -19.6) * mm, v(107.8, -19.74) * mm]});
            skFitSpline(sketch, "E1331", {"points": [v(107.8, -19.74) * mm, v(107.63, -19.95) * mm, v(107.17, -19.96) * mm, v(106.99, -19.71) * mm]});
            skFitSpline(sketch, "E1332", {"points": [v(106.99, -19.71) * mm, v(106.4, -18.93) * mm, v(105.76, -18.2) * mm, v(105.3, -17.33) * mm]});
            skFitSpline(sketch, "E1333", {"points": [v(105.3, -17.33) * mm, v(105.13, -17.03) * mm, v(104.9, -16.76) * mm, v(104.73, -16.47) * mm]});
            skFitSpline(sketch, "E1334", {"points": [v(104.73, -16.47) * mm, v(104.53, -16.16) * mm, v(104.35, -15.85) * mm, v(104.18, -15.52) * mm]});
            skFitSpline(sketch, "E1335", {"points": [v(104.18, -15.52) * mm, v(104.07, -15.33) * mm, v(104.07, -15.13) * mm, v(104.17, -14.92) * mm]});
            skFitSpline(sketch, "E1336", {"points": [v(104.17, -14.92) * mm, v(104.5, -14.26) * mm, v(104.8, -13.58) * mm, v(105.15, -12.92) * mm]});
            skFitSpline(sketch, "E1337", {"points": [v(105.15, -12.92) * mm, v(105.44, -12.37) * mm, v(105.79, -11.85) * mm, v(106.09, -11.3) * mm]});
            skFitSpline(sketch, "E1338", {"points": [v(106.09, -11.3) * mm, v(106.27, -10.97) * mm, v(106.41, -10.6) * mm, v(106.58, -10.22) * mm]});
            skFitSpline(sketch, "E1339", {"points": [v(106.58, -10.22) * mm, v(106.3, -10.16) * mm, v(106.04, -10.21) * mm, v(105.8, -10.24) * mm]});
            skFitSpline(sketch, "E1340", {"points": [v(105.8, -10.24) * mm, v(105.52, -10.26) * mm, v(105.25, -10.33) * mm, v(104.97, -10.37) * mm]});
            skFitSpline(sketch, "E1341", {"points": [v(104.97, -10.37) * mm, v(104.27, -10.47) * mm, v(103.57, -10.61) * mm, v(102.86, -10.63) * mm]});
            skFitSpline(sketch, "E1342", {"points": [v(102.86, -10.63) * mm, v(102.58, -10.64) * mm, v(102.3, -10.66) * mm, v(102, -10.68) * mm]});
            skFitSpline(sketch, "E1343", {"points": [v(102, -10.68) * mm, v(102, -10.75) * mm, v(101.99, -10.81) * mm, v(102, -10.87) * mm]});
            skFitSpline(sketch, "E1344", {"points": [v(102, -10.87) * mm, v(102.06, -11.25) * mm, v(102.13, -11.64) * mm, v(102.2, -12.02) * mm]});
            skFitSpline(sketch, "E1345", {"points": [v(102.2, -12.02) * mm, v(102.24, -12.3) * mm, v(102.28, -12.57) * mm, v(102.32, -12.85) * mm]});
            skFitSpline(sketch, "E1346", {"points": [v(102.32, -12.85) * mm, v(102.37, -13.11) * mm, v(102.4, -13.38) * mm, v(102.45, -13.65) * mm]});
            skFitSpline(sketch, "E1347", {"points": [v(102.45, -13.65) * mm, v(102.46, -13.75) * mm, v(102.48, -13.86) * mm, v(102.48, -13.96) * mm]});
            skFitSpline(sketch, "E1348", {"points": [v(102.48, -13.96) * mm, v(102.47, -14.34) * mm, v(102.1, -14.55) * mm, v(101.76, -14.38) * mm]});
            skFitSpline(sketch, "E1349", {"points": [v(101.76, -14.38) * mm, v(101.5, -14.25) * mm, v(101.39, -14.03) * mm, v(101.43, -13.73) * mm]});
            skFitSpline(sketch, "E1350", {"points": [v(101.43, -13.73) * mm, v(101.44, -13.7) * mm, v(101.45, -13.65) * mm, v(101.44, -13.62) * mm]});
            skFitSpline(sketch, "E1351", {"points": [v(101.44, -13.62) * mm, v(101.35, -13.08) * mm, v(101.36, -12.52) * mm, v(101.2, -11.99) * mm]});
            skFitSpline(sketch, "E1352", {"points": [v(101.2, -11.99) * mm, v(101.1, -11.7) * mm, v(101.08, -11.38) * mm, v(101.02, -11.07) * mm]});
            skFitSpline(sketch, "E1353", {"points": [v(101.02, -11.07) * mm, v(101, -11.07) * mm, v(100.99, -11.06) * mm, v(100.98, -11.07) * mm]});
            skFitSpline(sketch, "E1354", {"points": [v(100.98, -11.07) * mm, v(100.55, -11.26) * mm, v(100.11, -11.38) * mm, v(99.67, -11.52) * mm]});
            skFitSpline(sketch, "E1355", {"points": [v(99.67, -11.52) * mm, v(99.39, -11.6) * mm, v(99.13, -11.75) * mm, v(98.86, -11.87) * mm]});
            skFitSpline(sketch, "E1356", {"points": [v(98.86, -11.87) * mm, v(98.7, -11.94) * mm, v(98.55, -12) * mm, v(98.42, -12.1) * mm]});
            skFitSpline(sketch, "E1357", {"points": [v(98.42, -12.1) * mm, v(98.22, -12.25) * mm, v(98, -12.21) * mm, v(97.8, -12.1) * mm]});
            skFitSpline(sketch, "E1358", {"points": [v(97.8, -12.1) * mm, v(97.62, -12) * mm, v(97.53, -11.83) * mm, v(97.54, -11.62) * mm]});
            skFitSpline(sketch, "E1359", {"points": [v(97.54, -11.62) * mm, v(97.56, -11.4) * mm, v(97.7, -11.26) * mm, v(97.9, -11.18) * mm]});
            skFitSpline(sketch, "E1360", {"points": [v(97.9, -11.18) * mm, v(98.3, -11) * mm, v(98.7, -10.84) * mm, v(99.11, -10.68) * mm]});
            skFitSpline(sketch, "E1361", {"points": [v(99.11, -10.68) * mm, v(99.26, -10.62) * mm, v(99.41, -10.57) * mm, v(99.57, -10.53) * mm]});
            skFitSpline(sketch, "E1362", {"points": [v(99.57, -10.53) * mm, v(100, -10.42) * mm, v(100.43, -10.26) * mm, v(100.85, -10.04) * mm]});
            skFitSpline(sketch, "E1363", {"points": [v(100.85, -10.04) * mm, v(100.78, -9.87) * mm, v(100.73, -9.7) * mm, v(100.63, -9.54) * mm]});
            skFitSpline(sketch, "E1364", {"points": [v(100.63, -9.54) * mm, v(100.31, -9.03) * mm, v(100.1, -8.47) * mm, v(99.88, -7.9) * mm]});
            skFitSpline(sketch, "E1365", {"points": [v(99.88, -7.9) * mm, v(99.74, -7.55) * mm, v(99.63, -7.19) * mm, v(99.48, -6.83) * mm]});
            skFitSpline(sketch, "E1366", {"points": [v(99.48, -6.83) * mm, v(99.34, -6.5) * mm, v(99.17, -6.17) * mm, v(99, -5.8) * mm]});
            skFitSpline(sketch, "E1367", {"points": [v(65.07, -10.01) * mm, v(65.13, -9.94) * mm, v(65.16, -9.9) * mm, v(65.19, -9.87) * mm]});
            skFitSpline(sketch, "E1368", {"points": [v(65.19, -9.87) * mm, v(65.43, -9.5) * mm, v(65.68, -9.12) * mm, v(65.92, -8.75) * mm]});
            skFitSpline(sketch, "E1369", {"points": [v(65.92, -8.75) * mm, v(66.05, -8.55) * mm, v(66.17, -8.36) * mm, v(66.29, -8.16) * mm]});
            skFitSpline(sketch, "E1370", {"points": [v(66.29, -8.16) * mm, v(66.47, -7.83) * mm, v(66.63, -7.49) * mm, v(66.81, -7.16) * mm]});
            skFitSpline(sketch, "E1371", {"points": [v(66.81, -7.16) * mm, v(67.1, -6.66) * mm, v(67.3, -6.13) * mm, v(67.54, -5.6) * mm]});
            skFitSpline(sketch, "E1372", {"points": [v(67.54, -5.6) * mm, v(67.6, -5.47) * mm, v(67.57, -5.38) * mm, v(67.5, -5.27) * mm]});
            skFitSpline(sketch, "E1373", {"points": [v(67.5, -5.27) * mm, v(67.29, -4.94) * mm, v(67.08, -4.6) * mm, v(66.86, -4.26) * mm]});
            skFitSpline(sketch, "E1374", {"points": [v(66.86, -4.26) * mm, v(66.83, -4.22) * mm, v(66.8, -4.19) * mm, v(66.76, -4.15) * mm]});
            skFitSpline(sketch, "E1375", {"points": [v(66.76, -4.15) * mm, v(66.58, -4.53) * mm, v(66.41, -4.9) * mm, v(66.22, -5.26) * mm]});
            skFitSpline(sketch, "E1376", {"points": [v(66.22, -5.26) * mm, v(66, -5.66) * mm, v(65.77, -6.05) * mm, v(65.53, -6.44) * mm]});
            skFitSpline(sketch, "E1377", {"points": [v(65.53, -6.44) * mm, v(65.35, -6.73) * mm, v(64.83, -6.72) * mm, v(64.64, -6.45) * mm]});
            skFitSpline(sketch, "E1378", {"points": [v(64.64, -6.45) * mm, v(64.54, -6.32) * mm, v(64.44, -6.19) * mm, v(64.37, -6.05) * mm]});
            skFitSpline(sketch, "E1379", {"points": [v(64.37, -6.05) * mm, v(64.04, -5.48) * mm, v(63.73, -4.9) * mm, v(63.48, -4.3) * mm]});
            skFitSpline(sketch, "E1380", {"points": [v(63.48, -4.3) * mm, v(63.46, -4.25) * mm, v(63.43, -4.2) * mm, v(63.39, -4.12) * mm]});
            skFitSpline(sketch, "E1381", {"points": [v(63.39, -4.12) * mm, v(63.12, -4.54) * mm, v(62.87, -4.94) * mm, v(62.62, -5.34) * mm]});
            skFitSpline(sketch, "E1382", {"points": [v(62.62, -5.34) * mm, v(62.57, -5.41) * mm, v(62.57, -5.48) * mm, v(62.6, -5.56) * mm]});
            skFitSpline(sketch, "E1383", {"points": [v(62.6, -5.56) * mm, v(62.84, -6.07) * mm, v(63.06, -6.58) * mm, v(63.3, -7.08) * mm]});
            skFitSpline(sketch, "E1384", {"points": [v(63.3, -7.08) * mm, v(63.44, -7.35) * mm, v(63.6, -7.61) * mm, v(63.74, -7.88) * mm]});
            skFitSpline(sketch, "E1385", {"points": [v(63.74, -7.88) * mm, v(63.84, -8.06) * mm, v(63.93, -8.25) * mm, v(64.03, -8.43) * mm]});
            skFitSpline(sketch, "E1386", {"points": [v(64.03, -8.43) * mm, v(64.22, -8.73) * mm, v(64.41, -9.04) * mm, v(64.6, -9.34) * mm]});
            skFitSpline(sketch, "E1387", {"points": [v(64.6, -9.34) * mm, v(64.75, -9.56) * mm, v(64.9, -9.77) * mm, v(65.07, -10.01) * mm]});
            skFitSpline(sketch, "E1388", {"points": [v(63.4, 4.1) * mm, v(63.44, 4.2) * mm, v(63.47, 4.27) * mm, v(63.5, 4.35) * mm]});
            skFitSpline(sketch, "E1389", {"points": [v(63.5, 4.35) * mm, v(63.8, 5.04) * mm, v(64.16, 5.7) * mm, v(64.57, 6.35) * mm]});
            skFitSpline(sketch, "E1390", {"points": [v(64.57, 6.35) * mm, v(64.8, 6.72) * mm, v(65.36, 6.72) * mm, v(65.59, 6.36) * mm]});
            skFitSpline(sketch, "E1391", {"points": [v(65.59, 6.36) * mm, v(66, 5.73) * mm, v(66.34, 5.07) * mm, v(66.64, 4.38) * mm]});
            skFitSpline(sketch, "E1392", {"points": [v(66.64, 4.38) * mm, v(66.68, 4.3) * mm, v(66.71, 4.22) * mm, v(66.75, 4.15) * mm]});
            skFitSpline(sketch, "E1393", {"points": [v(66.75, 4.15) * mm, v(66.77, 4.16) * mm, v(66.8, 4.16) * mm, v(66.8, 4.17) * mm]});
            skFitSpline(sketch, "E1394", {"points": [v(66.8, 4.17) * mm, v(67.05, 4.56) * mm, v(67.3, 4.95) * mm, v(67.55, 5.34) * mm]});
            skFitSpline(sketch, "E1395", {"points": [v(67.55, 5.34) * mm, v(67.6, 5.42) * mm, v(67.58, 5.5) * mm, v(67.55, 5.57) * mm]});
            skFitSpline(sketch, "E1396", {"points": [v(67.55, 5.57) * mm, v(67.32, 6.07) * mm, v(67.1, 6.57) * mm, v(66.86, 7.07) * mm]});
            skFitSpline(sketch, "E1397", {"points": [v(66.86, 7.07) * mm, v(66.73, 7.34) * mm, v(66.57, 7.6) * mm, v(66.43, 7.87) * mm]});
            skFitSpline(sketch, "E1398", {"points": [v(66.43, 7.87) * mm, v(66.33, 8.04) * mm, v(66.25, 8.22) * mm, v(66.14, 8.4) * mm]});
            skFitSpline(sketch, "E1399", {"points": [v(66.14, 8.4) * mm, v(65.93, 8.75) * mm, v(65.7, 9.1) * mm, v(65.48, 9.45) * mm]});
            skFitSpline(sketch, "E1400", {"points": [v(65.48, 9.45) * mm, v(65.36, 9.63) * mm, v(65.22, 9.8) * mm, v(65.09, 10) * mm]});
            skFitSpline(sketch, "E1401", {"points": [v(65.09, 10) * mm, v(65.03, 9.93) * mm, v(64.99, 9.89) * mm, v(64.96, 9.84) * mm]});
            skFitSpline(sketch, "E1402", {"points": [v(64.96, 9.84) * mm, v(64.72, 9.47) * mm, v(64.47, 9.1) * mm, v(64.24, 8.74) * mm]});
            skFitSpline(sketch, "E1403", {"points": [v(64.24, 8.74) * mm, v(64.11, 8.54) * mm, v(63.99, 8.35) * mm, v(63.87, 8.15) * mm]});
            skFitSpline(sketch, "E1404", {"points": [v(63.87, 8.15) * mm, v(63.7, 7.82) * mm, v(63.53, 7.5) * mm, v(63.36, 7.17) * mm]});
            skFitSpline(sketch, "E1405", {"points": [v(63.36, 7.17) * mm, v(63.14, 6.72) * mm, v(62.92, 6.27) * mm, v(62.7, 5.82) * mm]});
            skFitSpline(sketch, "E1406", {"points": [v(62.7, 5.82) * mm, v(62.66, 5.72) * mm, v(62.62, 5.62) * mm, v(62.6, 5.52) * mm]});
            skFitSpline(sketch, "E1407", {"points": [v(62.6, 5.52) * mm, v(62.59, 5.47) * mm, v(62.59, 5.4) * mm, v(62.61, 5.35) * mm]});
            skFitSpline(sketch, "E1408", {"points": [v(62.61, 5.35) * mm, v(62.86, 4.94) * mm, v(63.12, 4.53) * mm, v(63.4, 4.1) * mm]});
            skFitSpline(sketch, "E1409", {"points": [v(56.42, 5.02) * mm, v(56.45, 4.93) * mm, v(56.46, 4.89) * mm, v(56.48, 4.84) * mm]});
            skFitSpline(sketch, "E1410", {"points": [v(56.48, 4.84) * mm, v(56.68, 4.44) * mm, v(56.88, 4.04) * mm, v(57.08, 3.65) * mm]});
            skFitSpline(sketch, "E1411", {"points": [v(57.08, 3.65) * mm, v(57.19, 3.44) * mm, v(57.3, 3.23) * mm, v(57.41, 3.04) * mm]});
            skFitSpline(sketch, "E1412", {"points": [v(57.41, 3.04) * mm, v(57.63, 2.67) * mm, v(57.86, 2.3) * mm, v(58.1, 1.94) * mm]});
            skFitSpline(sketch, "E1413", {"points": [v(58.1, 1.94) * mm, v(58.4, 1.5) * mm, v(58.72, 1.07) * mm, v(59.03, 0.64) * mm]});
            skFitSpline(sketch, "E1414", {"points": [v(59.03, 0.64) * mm, v(59.1, 0.55) * mm, v(59.17, 0.51) * mm, v(59.27, 0.52) * mm]});
            skFitSpline(sketch, "E1415", {"points": [v(59.27, 0.52) * mm, v(59.6, 0.54) * mm, v(59.94, 0.55) * mm, v(60.27, 0.56) * mm]});
            skFitSpline(sketch, "E1416", {"points": [v(60.27, 0.56) * mm, v(60.4, 0.57) * mm, v(60.53, 0.58) * mm, v(60.7, 0.58) * mm]});
            skFitSpline(sketch, "E1417", {"points": [v(60.7, 0.58) * mm, v(60.62, 0.69) * mm, v(60.57, 0.75) * mm, v(60.52, 0.81) * mm]});
            skFitSpline(sketch, "E1418", {"points": [v(60.52, 0.81) * mm, v(60.07, 1.42) * mm, v(59.67, 2.07) * mm, v(59.31, 2.74) * mm]});
            skFitSpline(sketch, "E1419", {"points": [v(59.31, 2.74) * mm, v(59.12, 3.1) * mm, v(59.38, 3.6) * mm, v(59.85, 3.62) * mm]});
            skFitSpline(sketch, "E1420", {"points": [v(59.85, 3.62) * mm, v(60.47, 3.64) * mm, v(61.09, 3.6) * mm, v(61.7, 3.57) * mm]});
            skFitSpline(sketch, "E1421", {"points": [v(61.7, 3.57) * mm, v(61.92, 3.56) * mm, v(62.12, 3.53) * mm, v(62.37, 3.5) * mm]});
            skFitSpline(sketch, "E1422", {"points": [v(62.37, 3.5) * mm, v(62.1, 4) * mm, v(61.87, 4.46) * mm, v(61.63, 4.91) * mm]});
            skFitSpline(sketch, "E1423", {"points": [v(61.63, 4.91) * mm, v(59.9, 5.13) * mm, v(58.17, 5.17) * mm, v(56.42, 5.02) * mm]});
            skFitSpline(sketch, "E1424", {"points": [v(69.5, 0.58) * mm, v(70, 0.56) * mm, v(70.48, 0.54) * mm, v(70.97, 0.53) * mm]});
            skFitSpline(sketch, "E1425", {"points": [v(70.97, 0.53) * mm, v(71.02, 0.53) * mm, v(71.1, 0.59) * mm, v(71.13, 0.64) * mm]});
            skFitSpline(sketch, "E1426", {"points": [v(71.13, 0.64) * mm, v(71.46, 1.1) * mm, v(71.79, 1.54) * mm, v(72.1, 2) * mm]});
            skFitSpline(sketch, "E1427", {"points": [v(72.1, 2) * mm, v(72.3, 2.29) * mm, v(72.46, 2.59) * mm, v(72.64, 2.88) * mm]});
            skFitSpline(sketch, "E1428", {"points": [v(72.64, 2.88) * mm, v(72.72, 3) * mm, v(72.8, 3.12) * mm, v(72.87, 3.25) * mm]});
            skFitSpline(sketch, "E1429", {"points": [v(72.87, 3.25) * mm, v(73.08, 3.63) * mm, v(73.29, 4.02) * mm, v(73.49, 4.4) * mm]});
            skFitSpline(sketch, "E1430", {"points": [v(73.49, 4.4) * mm, v(73.58, 4.6) * mm, v(73.65, 4.8) * mm, v(73.74, 5) * mm]});
            skFitSpline(sketch, "E1431", {"points": [v(73.74, 5) * mm, v(73.52, 5.03) * mm, v(73.33, 5.07) * mm, v(73.14, 5.07) * mm]});
            skFitSpline(sketch, "E1432", {"points": [v(73.14, 5.07) * mm, v(72.52, 5.1) * mm, v(71.9, 5.1) * mm, v(71.3, 5.1) * mm]});
            skFitSpline(sketch, "E1433", {"points": [v(71.3, 5.1) * mm, v(71.09, 5.1) * mm, v(70.88, 5.08) * mm, v(70.68, 5.08) * mm]});
            skFitSpline(sketch, "E1434", {"points": [v(70.68, 5.08) * mm, v(70, 5.1) * mm, v(69.34, 5) * mm, v(68.68, 4.92) * mm]});
            skFitSpline(sketch, "E1435", {"points": [v(68.68, 4.92) * mm, v(68.56, 4.9) * mm, v(68.5, 4.87) * mm, v(68.46, 4.77) * mm]});
            skFitSpline(sketch, "E1436", {"points": [v(68.46, 4.77) * mm, v(68.26, 4.4) * mm, v(68.07, 4.02) * mm, v(67.87, 3.65) * mm]});
            skFitSpline(sketch, "E1437", {"points": [v(67.87, 3.65) * mm, v(67.85, 3.61) * mm, v(67.84, 3.57) * mm, v(67.83, 3.52) * mm]});
            skFitSpline(sketch, "E1438", {"points": [v(67.83, 3.52) * mm, v(68.23, 3.55) * mm, v(68.61, 3.59) * mm, v(69, 3.6) * mm]});
            skFitSpline(sketch, "E1439", {"points": [v(69, 3.6) * mm, v(69.45, 3.61) * mm, v(69.91, 3.63) * mm, v(70.38, 3.61) * mm]});
            skFitSpline(sketch, "E1440", {"points": [v(70.38, 3.61) * mm, v(70.77, 3.6) * mm, v(71.04, 3.2) * mm, v(70.87, 2.81) * mm]});
            skFitSpline(sketch, "E1441", {"points": [v(70.87, 2.81) * mm, v(70.7, 2.42) * mm, v(70.47, 2.05) * mm, v(70.24, 1.69) * mm]});
            skFitSpline(sketch, "E1442", {"points": [v(70.24, 1.69) * mm, v(70.02, 1.34) * mm, v(69.77, 1) * mm, v(69.53, 0.66) * mm]});
            skFitSpline(sketch, "E1443", {"points": [v(69.53, 0.66) * mm, v(69.52, 0.65) * mm, v(69.52, 0.62) * mm, v(69.5, 0.58) * mm]});
            skFitSpline(sketch, "E1444", {"points": [v(60.68, -0.59) * mm, v(60.17, -0.57) * mm, v(59.7, -0.55) * mm, v(59.22, -0.53) * mm]});
            skFitSpline(sketch, "E1445", {"points": [v(59.22, -0.53) * mm, v(59.13, -0.53) * mm, v(59.08, -0.58) * mm, v(59.03, -0.65) * mm]});
            skFitSpline(sketch, "E1446", {"points": [v(59.03, -0.65) * mm, v(58.77, -1) * mm, v(58.48, -1.34) * mm, v(58.25, -1.7) * mm]});
            skFitSpline(sketch, "E1447", {"points": [v(58.25, -1.7) * mm, v(57.68, -2.61) * mm, v(57.12, -3.52) * mm, v(56.64, -4.48) * mm]});
            skFitSpline(sketch, "E1448", {"points": [v(56.64, -4.48) * mm, v(56.55, -4.64) * mm, v(56.5, -4.82) * mm, v(56.42, -5.03) * mm]});
            skFitSpline(sketch, "E1449", {"points": [v(56.42, -5.03) * mm, v(58.18, -5.18) * mm, v(59.91, -5.15) * mm, v(61.64, -4.92) * mm]});
            skFitSpline(sketch, "E1450", {"points": [v(61.64, -4.92) * mm, v(61.88, -4.45) * mm, v(62.12, -4) * mm, v(62.36, -3.53) * mm]});
            skFitSpline(sketch, "E1451", {"points": [v(62.36, -3.53) * mm, v(61.9, -3.56) * mm, v(61.47, -3.6) * mm, v(61.04, -3.62) * mm]});
            skFitSpline(sketch, "E1452", {"points": [v(61.04, -3.62) * mm, v(60.61, -3.64) * mm, v(60.18, -3.64) * mm, v(59.76, -3.62) * mm]});
            skFitSpline(sketch, "E1453", {"points": [v(59.76, -3.62) * mm, v(59.37, -3.6) * mm, v(59.11, -3.12) * mm, v(59.3, -2.8) * mm]});
            skFitSpline(sketch, "E1454", {"points": [v(59.3, -2.8) * mm, v(59.37, -2.66) * mm, v(59.42, -2.52) * mm, v(59.5, -2.39) * mm]});
            skFitSpline(sketch, "E1455", {"points": [v(59.5, -2.39) * mm, v(59.83, -1.82) * mm, v(60.18, -1.25) * mm, v(60.59, -0.73) * mm]});
            skFitSpline(sketch, "E1456", {"points": [v(60.59, -0.73) * mm, v(60.62, -0.7) * mm, v(60.64, -0.66) * mm, v(60.68, -0.59) * mm]});
            skFitSpline(sketch, "E1457", {"points": [v(73.74, -5.03) * mm, v(73.7, -4.93) * mm, v(73.7, -4.86) * mm, v(73.66, -4.8) * mm]});
            skFitSpline(sketch, "E1458", {"points": [v(73.66, -4.8) * mm, v(73.47, -4.42) * mm, v(73.27, -4.02) * mm, v(73.07, -3.63) * mm]});
            skFitSpline(sketch, "E1459", {"points": [v(73.07, -3.63) * mm, v(72.96, -3.43) * mm, v(72.85, -3.22) * mm, v(72.73, -3.03) * mm]});
            skFitSpline(sketch, "E1460", {"points": [v(72.73, -3.03) * mm, v(72.55, -2.72) * mm, v(72.34, -2.42) * mm, v(72.16, -2.11) * mm]});
            skFitSpline(sketch, "E1461", {"points": [v(72.16, -2.11) * mm, v(71.87, -1.6) * mm, v(71.5, -1.15) * mm, v(71.16, -0.68) * mm]});
            skFitSpline(sketch, "E1462", {"points": [v(71.16, -0.68) * mm, v(71.08, -0.56) * mm, v(70.98, -0.53) * mm, v(70.84, -0.53) * mm]});
            skFitSpline(sketch, "E1463", {"points": [v(70.84, -0.53) * mm, v(70.58, -0.55) * mm, v(70.31, -0.54) * mm, v(70.05, -0.56) * mm]});
            skFitSpline(sketch, "E1464", {"points": [v(70.05, -0.56) * mm, v(69.87, -0.57) * mm, v(69.7, -0.59) * mm, v(69.49, -0.6) * mm]});
            skFitSpline(sketch, "E1465", {"points": [v(69.49, -0.6) * mm, v(69.55, -0.69) * mm, v(69.58, -0.74) * mm, v(69.63, -0.8) * mm]});
            skFitSpline(sketch, "E1466", {"points": [v(69.63, -0.8) * mm, v(70.08, -1.42) * mm, v(70.5, -2.06) * mm, v(70.84, -2.75) * mm]});
            skFitSpline(sketch, "E1467", {"points": [v(70.84, -2.75) * mm, v(71.05, -3.19) * mm, v(70.75, -3.64) * mm, v(70.3, -3.63) * mm]});
            skFitSpline(sketch, "E1468", {"points": [v(70.3, -3.63) * mm, v(70.1, -3.62) * mm, v(69.9, -3.64) * mm, v(69.69, -3.63) * mm]});
            skFitSpline(sketch, "E1469", {"points": [v(69.69, -3.63) * mm, v(69.26, -3.62) * mm, v(68.83, -3.6) * mm, v(68.4, -3.58) * mm]});
            skFitSpline(sketch, "E1470", {"points": [v(68.4, -3.58) * mm, v(68.22, -3.57) * mm, v(68.03, -3.54) * mm, v(67.8, -3.52) * mm]});
            skFitSpline(sketch, "E1471", {"points": [v(67.8, -3.52) * mm, v(68.05, -4.01) * mm, v(68.3, -4.47) * mm, v(68.53, -4.92) * mm]});
            skFitSpline(sketch, "E1472", {"points": [v(68.53, -4.92) * mm, v(70.27, -5.15) * mm, v(71.98, -5.18) * mm, v(73.74, -5.03) * mm]});
            skFitSpline(sketch, "E1473", {"points": [v(77.8, -2.63) * mm, v(78.3, -2.32) * mm, v(80.88, -0.2) * mm, v(81.02, 0) * mm]});
            skFitSpline(sketch, "E1474", {"points": [v(81.02, 0) * mm, v(80.89, 0.17) * mm, v(78.05, 2.47) * mm, v(77.8, 2.6) * mm]});
            skFitSpline(sketch, "E1475", {"points": [v(77.8, 2.6) * mm, v(77.16, 1.7) * mm, v(76.48, 0.81) * mm, v(75.68, 0) * mm]});
            skFitSpline(sketch, "E1476", {"points": [v(75.68, 0) * mm, v(76.47, -0.82) * mm, v(77.16, -1.7) * mm, v(77.8, -2.63) * mm]});
            skFitSpline(sketch, "E1477", {"points": [v(56.45, -9.7) * mm, v(56.46, -9.88) * mm, v(56.45, -10.03) * mm, v(56.48, -10.18) * mm]});
            skFitSpline(sketch, "E1478", {"points": [v(56.48, -10.18) * mm, v(56.56, -10.7) * mm, v(56.67, -11.23) * mm, v(56.75, -11.75) * mm]});
            skFitSpline(sketch, "E1479", {"points": [v(56.75, -11.75) * mm, v(56.85, -12.35) * mm, v(56.93, -12.95) * mm, v(57.03, -13.55) * mm]});
            skFitSpline(sketch, "E1480", {"points": [v(57.03, -13.55) * mm, v(57.04, -13.64) * mm, v(57.07, -13.73) * mm, v(57.1, -13.81) * mm]});
            skFitSpline(sketch, "E1481", {"points": [v(57.1, -13.81) * mm, v(57.33, -13.78) * mm, v(60.75, -12.47) * mm, v(60.97, -12.33) * mm]});
            skFitSpline(sketch, "E1482", {"points": [v(60.97, -12.33) * mm, v(60.76, -11.81) * mm, v(60.53, -11.3) * mm, v(60.33, -10.79) * mm]});
            skFitSpline(sketch, "E1483", {"points": [v(60.33, -10.79) * mm, v(60.12, -10.26) * mm, v(59.95, -9.73) * mm, v(59.76, -9.19) * mm]});
            skFitSpline(sketch, "E1484", {"points": [v(59.76, -9.19) * mm, v(58.67, -9.47) * mm, v(57.58, -9.62) * mm, v(56.45, -9.7) * mm]});
            skFitSpline(sketch, "E1485", {"points": [v(73.7, -9.7) * mm, v(72.58, -9.62) * mm, v(71.48, -9.46) * mm, v(70.38, -9.19) * mm]});
            skFitSpline(sketch, "E1486", {"points": [v(70.38, -9.19) * mm, v(70.07, -10.28) * mm, v(69.66, -11.32) * mm, v(69.16, -12.34) * mm]});
            skFitSpline(sketch, "E1487", {"points": [v(69.16, -12.34) * mm, v(69.37, -12.43) * mm, v(69.56, -12.51) * mm, v(69.75, -12.59) * mm]});
            skFitSpline(sketch, "E1488", {"points": [v(69.75, -12.59) * mm, v(70.47, -12.87) * mm, v(71.19, -13.15) * mm, v(71.91, -13.43) * mm]});
            skFitSpline(sketch, "E1489", {"points": [v(71.91, -13.43) * mm, v(72.24, -13.55) * mm, v(72.57, -13.67) * mm, v(72.9, -13.8) * mm]});
            skFitSpline(sketch, "E1490", {"points": [v(72.9, -13.8) * mm, v(72.95, -13.81) * mm, v(73, -13.8) * mm, v(73.05, -13.82) * mm]});
            skFitSpline(sketch, "E1491", {"points": [v(73.05, -13.82) * mm, v(73.13, -13.62) * mm, v(73.72, -9.94) * mm, v(73.7, -9.7) * mm]});
            skFitSpline(sketch, "E1492", {"points": [v(54.48, 0) * mm, v(53.69, 0.81) * mm, v(53, 1.69) * mm, v(52.36, 2.63) * mm]});
            skFitSpline(sketch, "E1493", {"points": [v(52.36, 2.63) * mm, v(52.2, 2.51) * mm, v(52.04, 2.41) * mm, v(51.9, 2.3) * mm]});
            skFitSpline(sketch, "E1494", {"points": [v(51.9, 2.3) * mm, v(51.46, 1.94) * mm, v(51.03, 1.57) * mm, v(50.6, 1.21) * mm]});
            skFitSpline(sketch, "E1495", {"points": [v(50.6, 1.21) * mm, v(50.18, 0.88) * mm, v(49.77, 0.56) * mm, v(49.36, 0.23) * mm]});
            skFitSpline(sketch, "E1496", {"points": [v(49.36, 0.23) * mm, v(49.27, 0.16) * mm, v(49.2, 0.08) * mm, v(49.12, 0) * mm]});
            skFitSpline(sketch, "E1497", {"points": [v(49.12, 0) * mm, v(49.28, -0.19) * mm, v(52.13, -2.5) * mm, v(52.37, -2.62) * mm]});
            skFitSpline(sketch, "E1498", {"points": [v(52.37, -2.62) * mm, v(53, -1.7) * mm, v(53.69, -0.82) * mm, v(54.48, 0) * mm]});
            skFitSpline(sketch, "E1499", {"points": [v(56.45, 9.7) * mm, v(57.03, 9.64) * mm, v(57.57, 9.6) * mm, v(58.12, 9.5) * mm]});
            skFitSpline(sketch, "E1500", {"points": [v(58.12, 9.5) * mm, v(58.67, 9.42) * mm, v(59.21, 9.3) * mm, v(59.78, 9.2) * mm]});
            skFitSpline(sketch, "E1501", {"points": [v(59.78, 9.2) * mm, v(60.1, 10.27) * mm, v(60.5, 11.3) * mm, v(61, 12.33) * mm]});
            skFitSpline(sketch, "E1502", {"points": [v(61, 12.33) * mm, v(60.8, 12.42) * mm, v(60.65, 12.5) * mm, v(60.49, 12.56) * mm]});
            skFitSpline(sketch, "E1503", {"points": [v(60.49, 12.56) * mm, v(59.93, 12.77) * mm, v(59.36, 12.97) * mm, v(58.8, 13.18) * mm]});
            skFitSpline(sketch, "E1504", {"points": [v(58.8, 13.18) * mm, v(58.34, 13.36) * mm, v(57.89, 13.55) * mm, v(57.43, 13.73) * mm]});
            skFitSpline(sketch, "E1505", {"points": [v(57.43, 13.73) * mm, v(57.33, 13.77) * mm, v(57.22, 13.79) * mm, v(57.08, 13.82) * mm]});
            skFitSpline(sketch, "E1506", {"points": [v(57.08, 13.82) * mm, v(56.87, 12.58) * mm, v(56.67, 11.37) * mm, v(56.47, 10.15) * mm]});
            skFitSpline(sketch, "E1507", {"points": [v(56.47, 10.15) * mm, v(56.45, 10.01) * mm, v(56.46, 9.87) * mm, v(56.45, 9.7) * mm]});
            skFitSpline(sketch, "E1508", {"points": [v(69.17, 12.31) * mm, v(69.67, 11.3) * mm, v(70.06, 10.26) * mm, v(70.39, 9.18) * mm]});
            skFitSpline(sketch, "E1509", {"points": [v(70.39, 9.18) * mm, v(71.5, 9.46) * mm, v(72.6, 9.6) * mm, v(73.74, 9.7) * mm]});
            skFitSpline(sketch, "E1510", {"points": [v(73.74, 9.7) * mm, v(73.7, 9.95) * mm, v(73.67, 10.18) * mm, v(73.63, 10.4) * mm]});
            skFitSpline(sketch, "E1511", {"points": [v(73.63, 10.4) * mm, v(73.57, 10.8) * mm, v(73.5, 11.2) * mm, v(73.44, 11.6) * mm]});
            skFitSpline(sketch, "E1512", {"points": [v(73.44, 11.6) * mm, v(73.4, 11.9) * mm, v(73.35, 12.19) * mm, v(73.3, 12.48) * mm]});
            skFitSpline(sketch, "E1513", {"points": [v(73.3, 12.48) * mm, v(73.24, 12.86) * mm, v(73.18, 13.25) * mm, v(73.12, 13.63) * mm]});
            skFitSpline(sketch, "E1514", {"points": [v(73.12, 13.63) * mm, v(73.1, 13.7) * mm, v(73.08, 13.75) * mm, v(73.06, 13.8) * mm]});
            skFitSpline(sketch, "E1515", {"points": [v(73.06, 13.8) * mm, v(72.84, 13.78) * mm, v(69.46, 12.48) * mm, v(69.17, 12.31) * mm]});
            skFitSpline(sketch, "E1516", {"points": [v(59.55, -8.25) * mm, v(60.05, -7.47) * mm, v(60.53, -6.74) * mm, v(61.03, -5.98) * mm]});
            skFitSpline(sketch, "E1517", {"points": [v(61.03, -5.98) * mm, v(59.36, -6.1) * mm, v(57.74, -6.14) * mm, v(56.08, -5.96) * mm]});
            skFitSpline(sketch, "E1518", {"points": [v(56.08, -5.96) * mm, v(56.05, -6.05) * mm, v(56.02, -6.14) * mm, v(56, -6.23) * mm]});
            skFitSpline(sketch, "E1519", {"points": [v(56, -6.23) * mm, v(55.86, -6.66) * mm, v(55.73, -7.1) * mm, v(55.6, -7.53) * mm]});
            skFitSpline(sketch, "E1520", {"points": [v(55.6, -7.53) * mm, v(55.57, -7.63) * mm, v(55.54, -7.73) * mm, v(55.5, -7.83) * mm]});
            skFitSpline(sketch, "E1521", {"points": [v(55.5, -7.83) * mm, v(55.4, -8.17) * mm, v(55.12, -8.33) * mm, v(54.83, -8.22) * mm]});
            skFitSpline(sketch, "E1522", {"points": [v(54.83, -8.22) * mm, v(54.57, -8.12) * mm, v(54.43, -7.74) * mm, v(54.57, -7.45) * mm]});
            skFitSpline(sketch, "E1523", {"points": [v(54.57, -7.45) * mm, v(54.83, -6.92) * mm, v(54.99, -6.35) * mm, v(55.1, -5.77) * mm]});
            skFitSpline(sketch, "E1524", {"points": [v(55.1, -5.77) * mm, v(54.52, -5.58) * mm, v(53.94, -5.43) * mm, v(53.35, -5.37) * mm]});
            skFitSpline(sketch, "E1525", {"points": [v(53.35, -5.37) * mm, v(53.08, -5.35) * mm, v(52.84, -5.11) * mm, v(52.82, -4.86) * mm]});
            skFitSpline(sketch, "E1526", {"points": [v(52.82, -4.86) * mm, v(52.81, -4.65) * mm, v(53, -4.42) * mm, v(53.23, -4.37) * mm]});
            skFitSpline(sketch, "E1527", {"points": [v(53.23, -4.37) * mm, v(53.3, -4.35) * mm, v(53.38, -4.35) * mm, v(53.45, -4.37) * mm]});
            skFitSpline(sketch, "E1528", {"points": [v(53.45, -4.37) * mm, v(53.88, -4.45) * mm, v(54.32, -4.54) * mm, v(54.76, -4.64) * mm]});
            skFitSpline(sketch, "E1529", {"points": [v(54.76, -4.64) * mm, v(54.97, -4.7) * mm, v(55.18, -4.77) * mm, v(55.41, -4.83) * mm]});
            skFitSpline(sketch, "E1530", {"points": [v(55.41, -4.83) * mm, v(56.08, -3.3) * mm, v(56.94, -1.9) * mm, v(57.89, -0.51) * mm]});
            skFitSpline(sketch, "E1531", {"points": [v(57.89, -0.51) * mm, v(57.08, -0.57) * mm, v(56.29, -0.62) * mm, v(55.5, -0.67) * mm]});
            skFitSpline(sketch, "E1532", {"points": [v(55.5, -0.67) * mm, v(55.48, -0.67) * mm, v(55.47, -0.68) * mm, v(55.45, -0.67) * mm]});
            skFitSpline(sketch, "E1533", {"points": [v(55.45, -0.67) * mm, v(55.25, -0.6) * mm, v(55.13, -0.72) * mm, v(55, -0.86) * mm]});
            skFitSpline(sketch, "E1534", {"points": [v(55, -0.86) * mm, v(54.25, -1.67) * mm, v(53.58, -2.55) * mm, v(52.97, -3.48) * mm]});
            skFitSpline(sketch, "E1535", {"points": [v(52.97, -3.48) * mm, v(52.8, -3.74) * mm, v(52.53, -3.83) * mm, v(52.24, -3.71) * mm]});
            skFitSpline(sketch, "E1536", {"points": [v(52.24, -3.71) * mm, v(52.14, -3.67) * mm, v(52.03, -3.62) * mm, v(51.95, -3.55) * mm]});
            skFitSpline(sketch, "E1537", {"points": [v(51.95, -3.55) * mm, v(51.57, -3.26) * mm, v(51.2, -2.96) * mm, v(50.82, -2.66) * mm]});
            skFitSpline(sketch, "E1538", {"points": [v(50.82, -2.66) * mm, v(50.11, -2.1) * mm, v(49.4, -1.54) * mm, v(48.7, -0.97) * mm]});
            skFitSpline(sketch, "E1539", {"points": [v(48.7, -0.97) * mm, v(48.54, -0.83) * mm, v(48.4, -0.67) * mm, v(48.25, -0.51) * mm]});
            skFitSpline(sketch, "E1540", {"points": [v(48.25, -0.51) * mm, v(48.14, -0.4) * mm, v(48.1, -0.25) * mm, v(48.14, -0.09) * mm]});
            skFitSpline(sketch, "E1541", {"points": [v(48.14, -0.09) * mm, v(48.15, -0.04) * mm, v(48.16, 0) * mm, v(48.14, 0.05) * mm]});
            skFitSpline(sketch, "E1542", {"points": [v(48.14, 0.05) * mm, v(48.08, 0.27) * mm, v(48.17, 0.45) * mm, v(48.32, 0.59) * mm]});
            skFitSpline(sketch, "E1543", {"points": [v(48.32, 0.59) * mm, v(48.69, 0.92) * mm, v(49.06, 1.25) * mm, v(49.44, 1.56) * mm]});
            skFitSpline(sketch, "E1544", {"points": [v(49.44, 1.56) * mm, v(50.04, 2.06) * mm, v(50.64, 2.54) * mm, v(51.25, 3.02) * mm]});
            skFitSpline(sketch, "E1545", {"points": [v(51.25, 3.02) * mm, v(51.5, 3.23) * mm, v(51.77, 3.43) * mm, v(52.04, 3.6) * mm]});
            skFitSpline(sketch, "E1546", {"points": [v(52.04, 3.6) * mm, v(52.16, 3.68) * mm, v(52.3, 3.74) * mm, v(52.44, 3.75) * mm]});
            skFitSpline(sketch, "E1547", {"points": [v(52.44, 3.75) * mm, v(52.67, 3.78) * mm, v(52.84, 3.66) * mm, v(52.96, 3.48) * mm]});
            skFitSpline(sketch, "E1548", {"points": [v(52.96, 3.48) * mm, v(53.44, 2.75) * mm, v(53.96, 2.05) * mm, v(54.52, 1.38) * mm]});
            skFitSpline(sketch, "E1549", {"points": [v(54.52, 1.38) * mm, v(54.71, 1.16) * mm, v(54.92, 0.94) * mm, v(55.13, 0.73) * mm]});
            skFitSpline(sketch, "E1550", {"points": [v(55.13, 0.73) * mm, v(55.17, 0.69) * mm, v(55.24, 0.65) * mm, v(55.3, 0.65) * mm]});
            skFitSpline(sketch, "E1551", {"points": [v(55.3, 0.65) * mm, v(55.7, 0.62) * mm, v(56.1, 0.6) * mm, v(56.5, 0.59) * mm]});
            skFitSpline(sketch, "E1552", {"points": [v(56.5, 0.59) * mm, v(56.95, 0.57) * mm, v(57.4, 0.54) * mm, v(57.88, 0.51) * mm]});
            skFitSpline(sketch, "E1553", {"points": [v(57.88, 0.51) * mm, v(56.95, 1.9) * mm, v(56.08, 3.28) * mm, v(55.42, 4.81) * mm]});
            skFitSpline(sketch, "E1554", {"points": [v(55.42, 4.81) * mm, v(55.33, 4.8) * mm, v(55.24, 4.77) * mm, v(55.15, 4.75) * mm]});
            skFitSpline(sketch, "E1555", {"points": [v(55.15, 4.75) * mm, v(54.74, 4.66) * mm, v(54.34, 4.56) * mm, v(53.94, 4.46) * mm]});
            skFitSpline(sketch, "E1556", {"points": [v(53.94, 4.46) * mm, v(53.79, 4.42) * mm, v(53.64, 4.4) * mm, v(53.5, 4.36) * mm]});
            skFitSpline(sketch, "E1557", {"points": [v(53.5, 4.36) * mm, v(53.17, 4.3) * mm, v(52.88, 4.48) * mm, v(52.83, 4.78) * mm]});
            skFitSpline(sketch, "E1558", {"points": [v(52.83, 4.78) * mm, v(52.79, 5.05) * mm, v(53.05, 5.34) * mm, v(53.35, 5.36) * mm]});
            skFitSpline(sketch, "E1559", {"points": [v(53.35, 5.36) * mm, v(53.95, 5.42) * mm, v(54.53, 5.56) * mm, v(55.1, 5.76) * mm]});
            skFitSpline(sketch, "E1560", {"points": [v(55.1, 5.76) * mm, v(54.98, 6.35) * mm, v(54.82, 6.93) * mm, v(54.56, 7.47) * mm]});
            skFitSpline(sketch, "E1561", {"points": [v(54.56, 7.47) * mm, v(54.43, 7.74) * mm, v(54.56, 8.11) * mm, v(54.83, 8.22) * mm]});
            skFitSpline(sketch, "E1562", {"points": [v(54.83, 8.22) * mm, v(55.12, 8.32) * mm, v(55.4, 8.16) * mm, v(55.5, 7.84) * mm]});
            skFitSpline(sketch, "E1563", {"points": [v(55.5, 7.84) * mm, v(55.67, 7.28) * mm, v(55.84, 6.73) * mm, v(56, 6.17) * mm]});
            skFitSpline(sketch, "E1564", {"points": [v(56, 6.17) * mm, v(56.03, 6.1) * mm, v(56.05, 6.04) * mm, v(56.08, 5.95) * mm]});
            skFitSpline(sketch, "E1565", {"points": [v(56.08, 5.95) * mm, v(57.72, 6.13) * mm, v(59.35, 6.09) * mm, v(61.03, 5.97) * mm]});
            skFitSpline(sketch, "E1566", {"points": [v(61.03, 5.97) * mm, v(60.54, 6.72) * mm, v(60.06, 7.45) * mm, v(59.56, 8.22) * mm]});
            skFitSpline(sketch, "E1567", {"points": [v(59.56, 8.22) * mm, v(59.54, 8.23) * mm, v(59.48, 8.25) * mm, v(59.4, 8.27) * mm]});
            skFitSpline(sketch, "E1568", {"points": [v(59.4, 8.27) * mm, v(58.4, 8.5) * mm, v(57.39, 8.66) * mm, v(56.36, 8.73) * mm]});
            skFitSpline(sketch, "E1569", {"points": [v(56.36, 8.73) * mm, v(56.24, 8.73) * mm, v(56.12, 8.75) * mm, v(56, 8.75) * mm]});
            skFitSpline(sketch, "E1570", {"points": [v(56, 8.75) * mm, v(55.68, 8.77) * mm, v(55.45, 8.98) * mm, v(55.45, 9.3) * mm]});
            skFitSpline(sketch, "E1571", {"points": [v(55.45, 9.3) * mm, v(55.44, 9.55) * mm, v(55.46, 9.81) * mm, v(55.5, 10.06) * mm]});
            skFitSpline(sketch, "E1572", {"points": [v(55.5, 10.06) * mm, v(55.56, 10.51) * mm, v(55.64, 10.96) * mm, v(55.7, 11.4) * mm]});
            skFitSpline(sketch, "E1573", {"points": [v(55.7, 11.4) * mm, v(55.83, 12.19) * mm, v(55.94, 12.97) * mm, v(56.07, 13.75) * mm]});
            skFitSpline(sketch, "E1574", {"points": [v(56.07, 13.75) * mm, v(56.1, 13.94) * mm, v(56.16, 14.13) * mm, v(56.23, 14.32) * mm]});
            skFitSpline(sketch, "E1575", {"points": [v(56.23, 14.32) * mm, v(56.27, 14.47) * mm, v(56.37, 14.57) * mm, v(56.52, 14.62) * mm]});
            skFitSpline(sketch, "E1576", {"points": [v(56.52, 14.62) * mm, v(56.56, 14.64) * mm, v(56.61, 14.65) * mm, v(56.65, 14.68) * mm]});
            skFitSpline(sketch, "E1577", {"points": [v(56.65, 14.68) * mm, v(56.85, 14.88) * mm, v(57.07, 14.85) * mm, v(57.32, 14.78) * mm]});
            skFitSpline(sketch, "E1578", {"points": [v(57.32, 14.78) * mm, v(57.94, 14.6) * mm, v(58.53, 14.35) * mm, v(59.13, 14.1) * mm]});
            skFitSpline(sketch, "E1579", {"points": [v(59.13, 14.1) * mm, v(59.69, 13.88) * mm, v(60.25, 13.7) * mm, v(60.81, 13.48) * mm]});
            skFitSpline(sketch, "E1580", {"points": [v(60.81, 13.48) * mm, v(61.1, 13.37) * mm, v(61.4, 13.23) * mm, v(61.69, 13.1) * mm]});
            skFitSpline(sketch, "E1581", {"points": [v(61.69, 13.1) * mm, v(61.77, 13.06) * mm, v(61.84, 13) * mm, v(61.9, 12.94) * mm]});
            skFitSpline(sketch, "E1582", {"points": [v(61.9, 12.94) * mm, v(62.12, 12.76) * mm, v(62.17, 12.5) * mm, v(62.04, 12.25) * mm]});
            skFitSpline(sketch, "E1583", {"points": [v(62.04, 12.25) * mm, v(61.66, 11.48) * mm, v(61.31, 10.69) * mm, v(61.02, 9.88) * mm]});
            skFitSpline(sketch, "E1584", {"points": [v(61.02, 9.88) * mm, v(60.9, 9.55) * mm, v(60.8, 9.2) * mm, v(60.71, 8.9) * mm]});
            skFitSpline(sketch, "E1585", {"points": [v(60.71, 8.9) * mm, v(61.12, 8.1) * mm, v(61.52, 7.3) * mm, v(61.93, 6.5) * mm]});
            skFitSpline(sketch, "E1586", {"points": [v(61.93, 6.5) * mm, v(62.65, 8) * mm, v(63.43, 9.43) * mm, v(64.42, 10.77) * mm]});
            skFitSpline(sketch, "E1587", {"points": [v(64.42, 10.77) * mm, v(64.36, 10.84) * mm, v(64.3, 10.91) * mm, v(64.22, 10.99) * mm]});
            skFitSpline(sketch, "E1588", {"points": [v(64.22, 10.99) * mm, v(63.96, 11.26) * mm, v(63.7, 11.54) * mm, v(63.43, 11.82) * mm]});
            skFitSpline(sketch, "E1589", {"points": [v(63.43, 11.82) * mm, v(63.3, 11.94) * mm, v(63.2, 12.08) * mm, v(63.08, 12.21) * mm]});
            skFitSpline(sketch, "E1590", {"points": [v(63.08, 12.21) * mm, v(62.96, 12.35) * mm, v(62.87, 12.5) * mm, v(62.91, 12.69) * mm]});
            skFitSpline(sketch, "E1591", {"points": [v(62.91, 12.69) * mm, v(62.96, 12.9) * mm, v(63.08, 13.04) * mm, v(63.3, 13.07) * mm]});
            skFitSpline(sketch, "E1592", {"points": [v(63.3, 13.07) * mm, v(63.52, 13.11) * mm, v(63.72, 13.05) * mm, v(63.86, 12.85) * mm]});
            skFitSpline(sketch, "E1593", {"points": [v(63.86, 12.85) * mm, v(64.2, 12.36) * mm, v(64.62, 11.93) * mm, v(65.08, 11.52) * mm]});
            skFitSpline(sketch, "E1594", {"points": [v(65.08, 11.52) * mm, v(65.4, 11.8) * mm, v(65.69, 12.1) * mm, v(65.96, 12.4) * mm]});
            skFitSpline(sketch, "E1595", {"points": [v(65.96, 12.4) * mm, v(66.07, 12.55) * mm, v(66.19, 12.7) * mm, v(66.3, 12.84) * mm]});
            skFitSpline(sketch, "E1596", {"points": [v(66.3, 12.84) * mm, v(66.47, 13.09) * mm, v(66.82, 13.16) * mm, v(67.05, 13) * mm]});
            skFitSpline(sketch, "E1597", {"points": [v(67.05, 13) * mm, v(67.3, 12.81) * mm, v(67.33, 12.48) * mm, v(67.1, 12.23) * mm]});
            skFitSpline(sketch, "E1598", {"points": [v(67.1, 12.23) * mm, v(66.72, 11.8) * mm, v(66.32, 11.4) * mm, v(65.93, 10.98) * mm]});
            skFitSpline(sketch, "E1599", {"points": [v(65.93, 10.98) * mm, v(65.87, 10.91) * mm, v(65.8, 10.85) * mm, v(65.74, 10.78) * mm]});
            skFitSpline(sketch, "E1600", {"points": [v(65.74, 10.78) * mm, v(66.73, 9.44) * mm, v(67.5, 8) * mm, v(68.23, 6.5) * mm]});
            skFitSpline(sketch, "E1601", {"points": [v(68.23, 6.5) * mm, v(68.63, 7.3) * mm, v(69.03, 8.07) * mm, v(69.45, 8.9) * mm]});
            skFitSpline(sketch, "E1602", {"points": [v(69.45, 8.9) * mm, v(69.44, 8.9) * mm, v(69.43, 8.97) * mm, v(69.41, 9.03) * mm]});
            skFitSpline(sketch, "E1603", {"points": [v(69.41, 9.03) * mm, v(69.08, 10.13) * mm, v(68.65, 11.2) * mm, v(68.13, 12.22) * mm]});
            skFitSpline(sketch, "E1604", {"points": [v(68.13, 12.22) * mm, v(67.99, 12.5) * mm, v(68.04, 12.77) * mm, v(68.29, 12.97) * mm]});
            skFitSpline(sketch, "E1605", {"points": [v(68.29, 12.97) * mm, v(68.34, 13.02) * mm, v(68.4, 13.07) * mm, v(68.47, 13.1) * mm]});
            skFitSpline(sketch, "E1606", {"points": [v(68.47, 13.1) * mm, v(68.8, 13.24) * mm, v(69.13, 13.37) * mm, v(69.46, 13.5) * mm]});
            skFitSpline(sketch, "E1607", {"points": [v(69.46, 13.5) * mm, v(69.64, 13.58) * mm, v(69.82, 13.64) * mm, v(70, 13.7) * mm]});
            skFitSpline(sketch, "E1608", {"points": [v(70, 13.7) * mm, v(70.82, 14.03) * mm, v(71.63, 14.35) * mm, v(72.45, 14.66) * mm]});
            skFitSpline(sketch, "E1609", {"points": [v(72.45, 14.66) * mm, v(72.66, 14.74) * mm, v(72.88, 14.78) * mm, v(73.1, 14.84) * mm]});
            skFitSpline(sketch, "E1610", {"points": [v(73.1, 14.84) * mm, v(73.13, 14.85) * mm, v(73.17, 14.85) * mm, v(73.2, 14.84) * mm]});
            skFitSpline(sketch, "E1611", {"points": [v(73.2, 14.84) * mm, v(73.39, 14.74) * mm, v(73.6, 14.66) * mm, v(73.78, 14.53) * mm]});
            skFitSpline(sketch, "E1612", {"points": [v(73.78, 14.53) * mm, v(73.88, 14.46) * mm, v(73.94, 14.32) * mm, v(73.98, 14.2) * mm]});
            skFitSpline(sketch, "E1613", {"points": [v(73.98, 14.2) * mm, v(74.12, 13.71) * mm, v(74.19, 13.21) * mm, v(74.26, 12.72) * mm]});
            skFitSpline(sketch, "E1614", {"points": [v(74.26, 12.72) * mm, v(74.3, 12.4) * mm, v(74.35, 12.09) * mm, v(74.4, 11.77) * mm]});
            skFitSpline(sketch, "E1615", {"points": [v(74.4, 11.77) * mm, v(74.47, 11.3) * mm, v(74.56, 10.83) * mm, v(74.63, 10.36) * mm]});
            skFitSpline(sketch, "E1616", {"points": [v(74.63, 10.36) * mm, v(74.68, 10.05) * mm, v(74.71, 9.74) * mm, v(74.72, 9.43) * mm]});
            skFitSpline(sketch, "E1617", {"points": [v(74.72, 9.43) * mm, v(74.74, 8.99) * mm, v(74.5, 8.79) * mm, v(74.08, 8.75) * mm]});
            skFitSpline(sketch, "E1618", {"points": [v(74.08, 8.75) * mm, v(73.34, 8.68) * mm, v(72.62, 8.6) * mm, v(71.9, 8.5) * mm]});
            skFitSpline(sketch, "E1619", {"points": [v(71.9, 8.5) * mm, v(71.5, 8.44) * mm, v(71.12, 8.34) * mm, v(70.74, 8.27) * mm]});
            skFitSpline(sketch, "E1620", {"points": [v(70.74, 8.27) * mm, v(70.62, 8.24) * mm, v(70.54, 8.2) * mm, v(70.5, 8.07) * mm]});
            skFitSpline(sketch, "E1621", {"points": [v(70.5, 8.07) * mm, v(70.47, 7.97) * mm, v(70.39, 7.88) * mm, v(70.33, 7.79) * mm]});
            skFitSpline(sketch, "E1622", {"points": [v(70.33, 7.79) * mm, v(69.94, 7.2) * mm, v(69.55, 6.61) * mm, v(69.17, 6.03) * mm]});
            skFitSpline(sketch, "E1623", {"points": [v(69.17, 6.03) * mm, v(69.16, 6.02) * mm, v(69.16, 6) * mm, v(69.16, 5.97) * mm]});
            skFitSpline(sketch, "E1624", {"points": [v(69.16, 5.97) * mm, v(70.8, 6.08) * mm, v(72.44, 6.14) * mm, v(74.08, 5.95) * mm]});
            skFitSpline(sketch, "E1625", {"points": [v(74.08, 5.95) * mm, v(74.11, 6.05) * mm, v(74.14, 6.13) * mm, v(74.17, 6.22) * mm]});
            skFitSpline(sketch, "E1626", {"points": [v(74.17, 6.22) * mm, v(74.33, 6.77) * mm, v(74.5, 7.33) * mm, v(74.68, 7.89) * mm]});
            skFitSpline(sketch, "E1627", {"points": [v(74.68, 7.89) * mm, v(74.78, 8.19) * mm, v(75.08, 8.32) * mm, v(75.35, 8.2) * mm]});
            skFitSpline(sketch, "E1628", {"points": [v(75.35, 8.2) * mm, v(75.61, 8.1) * mm, v(75.72, 7.74) * mm, v(75.6, 7.47) * mm]});
            skFitSpline(sketch, "E1629", {"points": [v(75.6, 7.47) * mm, v(75.35, 6.93) * mm, v(75.18, 6.37) * mm, v(75.07, 5.78) * mm]});
            skFitSpline(sketch, "E1630", {"points": [v(75.07, 5.78) * mm, v(75.07, 5.78) * mm, v(75.08, 5.77) * mm, v(75.08, 5.75) * mm]});
            skFitSpline(sketch, "E1631", {"points": [v(75.08, 5.75) * mm, v(75.64, 5.56) * mm, v(76.22, 5.42) * mm, v(76.82, 5.36) * mm]});
            skFitSpline(sketch, "E1632", {"points": [v(76.82, 5.36) * mm, v(77.12, 5.33) * mm, v(77.37, 5.05) * mm, v(77.33, 4.78) * mm]});
            skFitSpline(sketch, "E1633", {"points": [v(77.33, 4.78) * mm, v(77.29, 4.48) * mm, v(77, 4.3) * mm, v(76.68, 4.36) * mm]});
            skFitSpline(sketch, "E1634", {"points": [v(76.68, 4.36) * mm, v(76.26, 4.45) * mm, v(75.84, 4.53) * mm, v(75.42, 4.63) * mm]});
            skFitSpline(sketch, "E1635", {"points": [v(75.42, 4.63) * mm, v(75.2, 4.68) * mm, v(74.98, 4.76) * mm, v(74.75, 4.82) * mm]});
            skFitSpline(sketch, "E1636", {"points": [v(74.75, 4.82) * mm, v(74.08, 3.3) * mm, v(73.22, 1.9) * mm, v(72.29, 0.52) * mm]});
            skFitSpline(sketch, "E1637", {"points": [v(72.29, 0.52) * mm, v(72.41, 0.52) * mm, v(72.52, 0.52) * mm, v(72.62, 0.52) * mm]});
            skFitSpline(sketch, "E1638", {"points": [v(72.62, 0.52) * mm, v(73.3, 0.57) * mm, v(73.98, 0.61) * mm, v(74.65, 0.66) * mm]});
            skFitSpline(sketch, "E1639", {"points": [v(74.65, 0.66) * mm, v(74.66, 0.66) * mm, v(74.67, 0.66) * mm, v(74.68, 0.66) * mm]});
            skFitSpline(sketch, "E1640", {"points": [v(74.68, 0.66) * mm, v(74.93, 0.58) * mm, v(75.06, 0.75) * mm, v(75.21, 0.91) * mm]});
            skFitSpline(sketch, "E1641", {"points": [v(75.21, 0.91) * mm, v(75.9, 1.66) * mm, v(76.51, 2.47) * mm, v(77.1, 3.3) * mm]});
            skFitSpline(sketch, "E1642", {"points": [v(77.1, 3.3) * mm, v(77.14, 3.37) * mm, v(77.17, 3.44) * mm, v(77.22, 3.5) * mm]});
            skFitSpline(sketch, "E1643", {"points": [v(77.22, 3.5) * mm, v(77.37, 3.72) * mm, v(77.6, 3.8) * mm, v(77.85, 3.73) * mm]});
            skFitSpline(sketch, "E1644", {"points": [v(77.85, 3.73) * mm, v(77.96, 3.7) * mm, v(78.08, 3.64) * mm, v(78.17, 3.58) * mm]});
            skFitSpline(sketch, "E1645", {"points": [v(78.17, 3.58) * mm, v(78.46, 3.36) * mm, v(78.74, 3.14) * mm, v(79.02, 2.92) * mm]});
            skFitSpline(sketch, "E1646", {"points": [v(79.02, 2.92) * mm, v(79.6, 2.46) * mm, v(80.18, 2) * mm, v(80.75, 1.54) * mm]});
            skFitSpline(sketch, "E1647", {"points": [v(80.75, 1.54) * mm, v(81.12, 1.24) * mm, v(81.47, 0.92) * mm, v(81.83, 0.6) * mm]});
            skFitSpline(sketch, "E1648", {"points": [v(81.83, 0.6) * mm, v(81.99, 0.46) * mm, v(82.07, 0.28) * mm, v(82.02, 0.06) * mm]});
            skFitSpline(sketch, "E1649", {"points": [v(82.02, 0.06) * mm, v(82.02, 0.04) * mm, v(82.01, 0.01) * mm, v(82.02, 0) * mm]});
            skFitSpline(sketch, "E1650", {"points": [v(82.02, 0) * mm, v(82.1, -0.3) * mm, v(81.94, -0.5) * mm, v(81.74, -0.7) * mm]});
            skFitSpline(sketch, "E1651", {"points": [v(81.74, -0.7) * mm, v(81.26, -1.17) * mm, v(80.72, -1.55) * mm, v(80.2, -1.96) * mm]});
            skFitSpline(sketch, "E1652", {"points": [v(80.2, -1.96) * mm, v(79.76, -2.31) * mm, v(79.33, -2.7) * mm, v(78.9, -3.05) * mm]});
            skFitSpline(sketch, "E1653", {"points": [v(78.9, -3.05) * mm, v(78.64, -3.25) * mm, v(78.38, -3.43) * mm, v(78.12, -3.62) * mm]});
            skFitSpline(sketch, "E1654", {"points": [v(78.12, -3.62) * mm, v(78.06, -3.66) * mm, v(77.98, -3.7) * mm, v(77.9, -3.72) * mm]});
            skFitSpline(sketch, "E1655", {"points": [v(77.9, -3.72) * mm, v(77.62, -3.82) * mm, v(77.36, -3.74) * mm, v(77.2, -3.49) * mm]});
            skFitSpline(sketch, "E1656", {"points": [v(77.2, -3.49) * mm, v(76.72, -2.75) * mm, v(76.2, -2.06) * mm, v(75.64, -1.4) * mm]});
            skFitSpline(sketch, "E1657", {"points": [v(75.64, -1.4) * mm, v(75.45, -1.17) * mm, v(75.24, -0.96) * mm, v(75.04, -0.74) * mm]});
            skFitSpline(sketch, "E1658", {"points": [v(75.04, -0.74) * mm, v(74.98, -0.67) * mm, v(74.9, -0.64) * mm, v(74.8, -0.66) * mm]});
            skFitSpline(sketch, "E1659", {"points": [v(74.8, -0.66) * mm, v(74.74, -0.67) * mm, v(74.67, -0.66) * mm, v(74.6, -0.66) * mm]});
            skFitSpline(sketch, "E1660", {"points": [v(74.6, -0.66) * mm, v(74.14, -0.63) * mm, v(73.67, -0.6) * mm, v(73.21, -0.58) * mm]});
            skFitSpline(sketch, "E1661", {"points": [v(73.21, -0.58) * mm, v(72.91, -0.56) * mm, v(72.6, -0.54) * mm, v(72.28, -0.52) * mm]});
            skFitSpline(sketch, "E1662", {"points": [v(72.28, -0.52) * mm, v(73.22, -1.9) * mm, v(74.08, -3.3) * mm, v(74.74, -4.82) * mm]});
            skFitSpline(sketch, "E1663", {"points": [v(74.74, -4.82) * mm, v(74.83, -4.8) * mm, v(74.9, -4.79) * mm, v(74.98, -4.77) * mm]});
            skFitSpline(sketch, "E1664", {"points": [v(74.98, -4.77) * mm, v(75.42, -4.67) * mm, v(75.87, -4.56) * mm, v(76.3, -4.45) * mm]});
            skFitSpline(sketch, "E1665", {"points": [v(76.3, -4.45) * mm, v(76.43, -4.43) * mm, v(76.56, -4.4) * mm, v(76.68, -4.37) * mm]});
            skFitSpline(sketch, "E1666", {"points": [v(76.68, -4.37) * mm, v(77, -4.3) * mm, v(77.28, -4.48) * mm, v(77.33, -4.78) * mm]});
            skFitSpline(sketch, "E1667", {"points": [v(77.33, -4.78) * mm, v(77.37, -5.04) * mm, v(77.14, -5.33) * mm, v(76.85, -5.37) * mm]});
            skFitSpline(sketch, "E1668", {"points": [v(76.85, -5.37) * mm, v(76.51, -5.43) * mm, v(76.17, -5.48) * mm, v(75.84, -5.55) * mm]});
            skFitSpline(sketch, "E1669", {"points": [v(75.84, -5.55) * mm, v(75.58, -5.6) * mm, v(75.33, -5.68) * mm, v(75.06, -5.76) * mm]});
            skFitSpline(sketch, "E1670", {"points": [v(75.06, -5.76) * mm, v(75.1, -5.95) * mm, v(75.12, -6.13) * mm, v(75.18, -6.3) * mm]});
            skFitSpline(sketch, "E1671", {"points": [v(75.18, -6.3) * mm, v(75.31, -6.7) * mm, v(75.45, -7.1) * mm, v(75.6, -7.5) * mm]});
            skFitSpline(sketch, "E1672", {"points": [v(75.6, -7.5) * mm, v(75.71, -7.76) * mm, v(75.6, -8.1) * mm, v(75.35, -8.21) * mm]});
            skFitSpline(sketch, "E1673", {"points": [v(75.35, -8.21) * mm, v(75.09, -8.33) * mm, v(74.78, -8.2) * mm, v(74.68, -7.9) * mm]});
            skFitSpline(sketch, "E1674", {"points": [v(74.68, -7.9) * mm, v(74.5, -7.35) * mm, v(74.34, -6.79) * mm, v(74.17, -6.23) * mm]});
            skFitSpline(sketch, "E1675", {"points": [v(74.17, -6.23) * mm, v(74.14, -6.15) * mm, v(74.12, -6.07) * mm, v(74.09, -5.96) * mm]});
            skFitSpline(sketch, "E1676", {"points": [v(74.09, -5.96) * mm, v(72.44, -6.14) * mm, v(70.8, -6.1) * mm, v(69.14, -5.98) * mm]});
            skFitSpline(sketch, "E1677", {"points": [v(69.14, -5.98) * mm, v(69.17, -6.04) * mm, v(69.2, -6.07) * mm, v(69.21, -6.1) * mm]});
            skFitSpline(sketch, "E1678", {"points": [v(69.21, -6.1) * mm, v(69.6, -6.7) * mm, v(70, -7.29) * mm, v(70.39, -7.88) * mm]});
            skFitSpline(sketch, "E1679", {"points": [v(70.39, -7.88) * mm, v(70.43, -7.94) * mm, v(70.48, -8) * mm, v(70.5, -8.06) * mm]});
            skFitSpline(sketch, "E1680", {"points": [v(70.5, -8.06) * mm, v(70.53, -8.2) * mm, v(70.62, -8.25) * mm, v(70.75, -8.28) * mm]});
            skFitSpline(sketch, "E1681", {"points": [v(70.75, -8.28) * mm, v(71.87, -8.54) * mm, v(73, -8.7) * mm, v(74.16, -8.76) * mm]});
            skFitSpline(sketch, "E1682", {"points": [v(74.16, -8.76) * mm, v(74.49, -8.78) * mm, v(74.72, -9) * mm, v(74.72, -9.35) * mm]});
            skFitSpline(sketch, "E1683", {"points": [v(74.72, -9.35) * mm, v(74.73, -9.59) * mm, v(74.7, -9.83) * mm, v(74.66, -10.06) * mm]});
            skFitSpline(sketch, "E1684", {"points": [v(74.66, -10.06) * mm, v(74.54, -10.87) * mm, v(74.41, -11.67) * mm, v(74.29, -12.47) * mm]});
            skFitSpline(sketch, "E1685", {"points": [v(74.29, -12.47) * mm, v(74.22, -12.89) * mm, v(74.17, -13.3) * mm, v(74.1, -13.72) * mm]});
            skFitSpline(sketch, "E1686", {"points": [v(74.1, -13.72) * mm, v(74.06, -13.94) * mm, v(74, -14.14) * mm, v(73.93, -14.35) * mm]});
            skFitSpline(sketch, "E1687", {"points": [v(73.93, -14.35) * mm, v(73.89, -14.48) * mm, v(73.79, -14.57) * mm, v(73.65, -14.63) * mm]});
            skFitSpline(sketch, "E1688", {"points": [v(73.65, -14.63) * mm, v(73.6, -14.64) * mm, v(73.56, -14.66) * mm, v(73.52, -14.69) * mm]});
            skFitSpline(sketch, "E1689", {"points": [v(73.52, -14.69) * mm, v(73.32, -14.88) * mm, v(73.1, -14.86) * mm, v(72.85, -14.8) * mm]});
            skFitSpline(sketch, "E1690", {"points": [v(72.85, -14.8) * mm, v(72.21, -14.62) * mm, v(71.6, -14.34) * mm, v(71, -14.1) * mm]});
            skFitSpline(sketch, "E1691", {"points": [v(71, -14.1) * mm, v(70.45, -13.88) * mm, v(69.9, -13.7) * mm, v(69.36, -13.5) * mm]});
            skFitSpline(sketch, "E1692", {"points": [v(69.36, -13.5) * mm, v(69.05, -13.37) * mm, v(68.75, -13.25) * mm, v(68.46, -13.1) * mm]});
            skFitSpline(sketch, "E1693", {"points": [v(68.46, -13.1) * mm, v(68.22, -12.97) * mm, v(68.02, -12.79) * mm, v(68.06, -12.47) * mm]});
            skFitSpline(sketch, "E1694", {"points": [v(68.06, -12.47) * mm, v(68.07, -12.4) * mm, v(68.1, -12.31) * mm, v(68.13, -12.24) * mm]});
            skFitSpline(sketch, "E1695", {"points": [v(68.13, -12.24) * mm, v(68.52, -11.46) * mm, v(68.86, -10.65) * mm, v(69.16, -9.82) * mm]});
            skFitSpline(sketch, "E1696", {"points": [v(69.16, -9.82) * mm, v(69.27, -9.52) * mm, v(69.36, -9.2) * mm, v(69.45, -8.9) * mm]});
            skFitSpline(sketch, "E1697", {"points": [v(69.45, -8.9) * mm, v(69.04, -8.1) * mm, v(68.64, -7.32) * mm, v(68.23, -6.5) * mm]});
            skFitSpline(sketch, "E1698", {"points": [v(68.23, -6.5) * mm, v(67.5, -8) * mm, v(66.73, -9.44) * mm, v(65.74, -10.78) * mm]});
            skFitSpline(sketch, "E1699", {"points": [v(65.74, -10.78) * mm, v(65.8, -10.85) * mm, v(65.87, -10.92) * mm, v(65.93, -10.99) * mm]});
            skFitSpline(sketch, "E1700", {"points": [v(65.93, -10.99) * mm, v(66.23, -11.3) * mm, v(66.53, -11.62) * mm, v(66.82, -11.93) * mm]});
            skFitSpline(sketch, "E1701", {"points": [v(66.82, -11.93) * mm, v(66.93, -12.04) * mm, v(67.03, -12.15) * mm, v(67.13, -12.27) * mm]});
            skFitSpline(sketch, "E1702", {"points": [v(67.13, -12.27) * mm, v(67.38, -12.59) * mm, v(67.23, -13.02) * mm, v(66.85, -13.08) * mm]});
            skFitSpline(sketch, "E1703", {"points": [v(66.85, -13.08) * mm, v(66.63, -13.12) * mm, v(66.44, -13.05) * mm, v(66.3, -12.86) * mm]});
            skFitSpline(sketch, "E1704", {"points": [v(66.3, -12.86) * mm, v(65.96, -12.37) * mm, v(65.54, -11.94) * mm, v(65.09, -11.53) * mm]});
            skFitSpline(sketch, "E1705", {"points": [v(65.09, -11.53) * mm, v(64.75, -11.8) * mm, v(64.47, -12.1) * mm, v(64.2, -12.43) * mm]});
            skFitSpline(sketch, "E1706", {"points": [v(64.2, -12.43) * mm, v(64.08, -12.57) * mm, v(63.97, -12.72) * mm, v(63.86, -12.86) * mm]});
            skFitSpline(sketch, "E1707", {"points": [v(63.86, -12.86) * mm, v(63.72, -13.05) * mm, v(63.53, -13.12) * mm, v(63.31, -13.08) * mm]});
            skFitSpline(sketch, "E1708", {"points": [v(63.31, -13.08) * mm, v(63.1, -13.06) * mm, v(62.97, -12.92) * mm, v(62.92, -12.72) * mm]});
            skFitSpline(sketch, "E1709", {"points": [v(62.92, -12.72) * mm, v(62.87, -12.53) * mm, v(62.94, -12.37) * mm, v(63.06, -12.23) * mm]});
            skFitSpline(sketch, "E1710", {"points": [v(63.06, -12.23) * mm, v(63.46, -11.8) * mm, v(63.86, -11.38) * mm, v(64.26, -10.96) * mm]});
            skFitSpline(sketch, "E1711", {"points": [v(64.26, -10.96) * mm, v(64.31, -10.9) * mm, v(64.36, -10.84) * mm, v(64.42, -10.78) * mm]});
            skFitSpline(sketch, "E1712", {"points": [v(64.42, -10.78) * mm, v(63.43, -9.45) * mm, v(62.66, -8.01) * mm, v(61.93, -6.5) * mm]});
            skFitSpline(sketch, "E1713", {"points": [v(61.93, -6.5) * mm, v(61.86, -6.65) * mm, v(61.79, -6.78) * mm, v(61.72, -6.9) * mm]});
            skFitSpline(sketch, "E1714", {"points": [v(61.72, -6.9) * mm, v(61.44, -7.47) * mm, v(61.16, -8.04) * mm, v(60.88, -8.6) * mm]});
            skFitSpline(sketch, "E1715", {"points": [v(60.88, -8.6) * mm, v(60.87, -8.62) * mm, v(60.87, -8.65) * mm, v(60.85, -8.67) * mm]});
            skFitSpline(sketch, "E1716", {"points": [v(60.85, -8.67) * mm, v(60.66, -8.82) * mm, v(60.73, -9) * mm, v(60.8, -9.19) * mm]});
            skFitSpline(sketch, "E1717", {"points": [v(60.8, -9.19) * mm, v(61.12, -10.24) * mm, v(61.54, -11.26) * mm, v(62.04, -12.24) * mm]});
            skFitSpline(sketch, "E1718", {"points": [v(62.04, -12.24) * mm, v(62.17, -12.52) * mm, v(62.12, -12.77) * mm, v(61.88, -12.97) * mm]});
            skFitSpline(sketch, "E1719", {"points": [v(61.88, -12.97) * mm, v(61.82, -13.02) * mm, v(61.76, -13.08) * mm, v(61.69, -13.1) * mm]});
            skFitSpline(sketch, "E1720", {"points": [v(61.69, -13.1) * mm, v(61.36, -13.25) * mm, v(61.03, -13.39) * mm, v(60.7, -13.52) * mm]});
            skFitSpline(sketch, "E1721", {"points": [v(60.7, -13.52) * mm, v(60.53, -13.59) * mm, v(60.36, -13.64) * mm, v(60.2, -13.7) * mm]});
            skFitSpline(sketch, "E1722", {"points": [v(60.2, -13.7) * mm, v(59.37, -14.03) * mm, v(58.55, -14.35) * mm, v(57.72, -14.67) * mm]});
            skFitSpline(sketch, "E1723", {"points": [v(57.72, -14.67) * mm, v(57.52, -14.75) * mm, v(57.3, -14.79) * mm, v(57.08, -14.84) * mm]});
            skFitSpline(sketch, "E1724", {"points": [v(57.08, -14.84) * mm, v(57.05, -14.85) * mm, v(57.01, -14.85) * mm, v(56.98, -14.85) * mm]});
            skFitSpline(sketch, "E1725", {"points": [v(56.98, -14.85) * mm, v(56.74, -14.82) * mm, v(56.57, -14.65) * mm, v(56.38, -14.53) * mm]});
            skFitSpline(sketch, "E1726", {"points": [v(56.38, -14.53) * mm, v(56.27, -14.47) * mm, v(56.2, -14.3) * mm, v(56.17, -14.17) * mm]});
            skFitSpline(sketch, "E1727", {"points": [v(56.17, -14.17) * mm, v(56.1, -13.85) * mm, v(56.03, -13.53) * mm, v(55.98, -13.2) * mm]});
            skFitSpline(sketch, "E1728", {"points": [v(55.98, -13.2) * mm, v(55.92, -12.87) * mm, v(55.89, -12.53) * mm, v(55.84, -12.2) * mm]});
            skFitSpline(sketch, "E1729", {"points": [v(55.84, -12.2) * mm, v(55.74, -11.62) * mm, v(55.63, -11.05) * mm, v(55.55, -10.47) * mm]});
            skFitSpline(sketch, "E1730", {"points": [v(55.55, -10.47) * mm, v(55.5, -10.1) * mm, v(55.46, -9.73) * mm, v(55.45, -9.35) * mm]});
            skFitSpline(sketch, "E1731", {"points": [v(55.45, -9.35) * mm, v(55.44, -9) * mm, v(55.67, -8.78) * mm, v(56.03, -8.76) * mm]});
            skFitSpline(sketch, "E1732", {"points": [v(56.03, -8.76) * mm, v(56.8, -8.72) * mm, v(57.57, -8.64) * mm, v(58.33, -8.5) * mm]});
            skFitSpline(sketch, "E1733", {"points": [v(58.33, -8.5) * mm, v(58.76, -8.42) * mm, v(59.18, -8.32) * mm, v(59.55, -8.25) * mm]});
            skFitSpline(sketch, "E1734", {"points": [v(-118.18, 6.15) * mm, v(-117.96, 5.32) * mm, v(-117.74, 4.53) * mm, v(-117.53, 3.73) * mm]});
            skFitSpline(sketch, "E1735", {"points": [v(-117.53, 3.73) * mm, v(-117.3, 3.64) * mm, v(-117.1, 3.56) * mm, v(-116.85, 3.47) * mm]});
            skFitSpline(sketch, "E1736", {"points": [v(-116.85, 3.47) * mm, v(-116.89, 3.63) * mm, v(-116.92, 3.75) * mm, v(-116.94, 3.88) * mm]});
            skFitSpline(sketch, "E1737", {"points": [v(-116.94, 3.88) * mm, v(-117, 4.21) * mm, v(-117.07, 4.55) * mm, v(-117.12, 4.89) * mm]});
            skFitSpline(sketch, "E1738", {"points": [v(-117.12, 4.89) * mm, v(-117.15, 5.06) * mm, v(-117.1, 5.22) * mm, v(-116.97, 5.34) * mm]});
            skFitSpline(sketch, "E1739", {"points": [v(-116.97, 5.34) * mm, v(-116.93, 5.38) * mm, v(-116.9, 5.45) * mm, v(-116.88, 5.5) * mm]});
            skFitSpline(sketch, "E1740", {"points": [v(-116.88, 5.5) * mm, v(-116.82, 5.7) * mm, v(-116.7, 5.83) * mm, v(-116.5, 5.9) * mm]});
            skFitSpline(sketch, "E1741", {"points": [v(-116.5, 5.9) * mm, v(-116.16, 6.02) * mm, v(-115.82, 6.13) * mm, v(-115.48, 6.25) * mm]});
            skFitSpline(sketch, "E1742", {"points": [v(-115.48, 6.25) * mm, v(-115.4, 6.28) * mm, v(-115.31, 6.3) * mm, v(-115.2, 6.35) * mm]});
            skFitSpline(sketch, "E1743", {"points": [v(-115.2, 6.35) * mm, v(-115.37, 6.5) * mm, v(-115.51, 6.61) * mm, v(-115.65, 6.73) * mm]});
            skFitSpline(sketch, "E1744", {"points": [v(-115.65, 6.73) * mm, v(-115.71, 6.78) * mm, v(-115.77, 6.79) * mm, v(-115.85, 6.77) * mm]});
            skFitSpline(sketch, "E1745", {"points": [v(-115.85, 6.77) * mm, v(-116.19, 6.67) * mm, v(-116.53, 6.6) * mm, v(-116.87, 6.5) * mm]});
            skFitSpline(sketch, "E1746", {"points": [v(-116.87, 6.5) * mm, v(-117.3, 6.4) * mm, v(-117.73, 6.27) * mm, v(-118.18, 6.15) * mm]});
            skFitSpline(sketch, "E1747", {"points": [v(-105.85, -9.83) * mm, v(-105.95, -9.92) * mm, v(-106.02, -9.98) * mm, v(-106.08, -10.03) * mm]});
            skFitSpline(sketch, "E1748", {"points": [v(-106.08, -10.03) * mm, v(-106.35, -10.27) * mm, v(-106.62, -10.5) * mm, v(-106.9, -10.74) * mm]});
            skFitSpline(sketch, "E1749", {"points": [v(-106.9, -10.74) * mm, v(-107.05, -10.88) * mm, v(-107.22, -10.92) * mm, v(-107.43, -10.87) * mm]});
            skFitSpline(sketch, "E1750", {"points": [v(-107.43, -10.87) * mm, v(-107.48, -10.85) * mm, v(-107.55, -10.85) * mm, v(-107.6, -10.87) * mm]});
            skFitSpline(sketch, "E1751", {"points": [v(-107.6, -10.87) * mm, v(-107.8, -10.92) * mm, v(-107.97, -10.88) * mm, v(-108.12, -10.75) * mm]});
            skFitSpline(sketch, "E1752", {"points": [v(-108.12, -10.75) * mm, v(-108.39, -10.51) * mm, v(-108.66, -10.28) * mm, v(-108.93, -10.04) * mm]});
            skFitSpline(sketch, "E1753", {"points": [v(-108.93, -10.04) * mm, v(-109, -9.98) * mm, v(-109.08, -9.92) * mm, v(-109.18, -9.83) * mm]});
            skFitSpline(sketch, "E1754", {"points": [v(-109.18, -9.83) * mm, v(-109.22, -10.1) * mm, v(-109.25, -10.31) * mm, v(-109.3, -10.57) * mm]});
            skFitSpline(sketch, "E1755", {"points": [v(-109.3, -10.57) * mm, v(-108.7, -11.14) * mm, v(-108.1, -11.72) * mm, v(-107.5, -12.31) * mm]});
            skFitSpline(sketch, "E1756", {"points": [v(-107.5, -12.31) * mm, v(-106.94, -11.75) * mm, v(-106.38, -11.18) * mm, v(-105.83, -10.62) * mm]});
            skFitSpline(sketch, "E1757", {"points": [v(-105.83, -10.62) * mm, v(-105.78, -10.57) * mm, v(-105.74, -10.52) * mm, v(-105.75, -10.44) * mm]});
            skFitSpline(sketch, "E1758", {"points": [v(-105.75, -10.44) * mm, v(-105.78, -10.25) * mm, v(-105.81, -10.06) * mm, v(-105.85, -9.83) * mm]});
            skFitSpline(sketch, "E1759", {"points": [v(-105.85, 9.82) * mm, v(-105.82, 10.03) * mm, v(-105.79, 10.2) * mm, v(-105.76, 10.36) * mm]});
            skFitSpline(sketch, "E1760", {"points": [v(-105.76, 10.36) * mm, v(-105.74, 10.46) * mm, v(-105.76, 10.54) * mm, v(-105.85, 10.63) * mm]});
            skFitSpline(sketch, "E1761", {"points": [v(-105.85, 10.63) * mm, v(-106.23, 11.01) * mm, v(-106.6, 11.4) * mm, v(-106.98, 11.8) * mm]});
            skFitSpline(sketch, "E1762", {"points": [v(-106.98, 11.8) * mm, v(-107.15, 11.97) * mm, v(-107.33, 12.13) * mm, v(-107.52, 12.3) * mm]});
            skFitSpline(sketch, "E1763", {"points": [v(-107.52, 12.3) * mm, v(-108.12, 11.7) * mm, v(-108.7, 11.11) * mm, v(-109.3, 10.53) * mm]});
            skFitSpline(sketch, "E1764", {"points": [v(-109.3, 10.53) * mm, v(-109.25, 10.29) * mm, v(-109.22, 10.07) * mm, v(-109.18, 9.82) * mm]});
            skFitSpline(sketch, "E1765", {"points": [v(-109.18, 9.82) * mm, v(-109.08, 9.9) * mm, v(-109, 9.97) * mm, v(-108.93, 10.03) * mm]});
            skFitSpline(sketch, "E1766", {"points": [v(-108.93, 10.03) * mm, v(-108.66, 10.27) * mm, v(-108.4, 10.5) * mm, v(-108.12, 10.74) * mm]});
            skFitSpline(sketch, "E1767", {"points": [v(-108.12, 10.74) * mm, v(-107.97, 10.87) * mm, v(-107.8, 10.9) * mm, v(-107.61, 10.86) * mm]});
            skFitSpline(sketch, "E1768", {"points": [v(-107.61, 10.86) * mm, v(-107.55, 10.85) * mm, v(-107.47, 10.85) * mm, v(-107.4, 10.86) * mm]});
            skFitSpline(sketch, "E1769", {"points": [v(-107.4, 10.86) * mm, v(-107.21, 10.9) * mm, v(-107.05, 10.87) * mm, v(-106.9, 10.74) * mm]});
            skFitSpline(sketch, "E1770", {"points": [v(-106.9, 10.74) * mm, v(-106.63, 10.5) * mm, v(-106.36, 10.26) * mm, v(-106.09, 10.03) * mm]});
            skFitSpline(sketch, "E1771", {"points": [v(-106.09, 10.03) * mm, v(-106.02, 9.97) * mm, v(-105.95, 9.91) * mm, v(-105.85, 9.82) * mm]});
            skFitSpline(sketch, "E1772", {"points": [v(-97.5, 3.72) * mm, v(-97.28, 4.54) * mm, v(-97.06, 5.34) * mm, v(-96.84, 6.15) * mm]});
            skFitSpline(sketch, "E1773", {"points": [v(-96.84, 6.15) * mm, v(-96.97, 6.18) * mm, v(-97.06, 6.21) * mm, v(-97.16, 6.24) * mm]});
            skFitSpline(sketch, "E1774", {"points": [v(-97.16, 6.24) * mm, v(-97.83, 6.4) * mm, v(-98.49, 6.58) * mm, v(-99.15, 6.75) * mm]});
            skFitSpline(sketch, "E1775", {"points": [v(-99.15, 6.75) * mm, v(-99.2, 6.77) * mm, v(-99.29, 6.78) * mm, v(-99.33, 6.75) * mm]});
            skFitSpline(sketch, "E1776", {"points": [v(-99.33, 6.75) * mm, v(-99.5, 6.63) * mm, v(-99.64, 6.5) * mm, v(-99.84, 6.34) * mm]});
            skFitSpline(sketch, "E1777", {"points": [v(-99.84, 6.34) * mm, v(-99.7, 6.3) * mm, v(-99.6, 6.27) * mm, v(-99.5, 6.24) * mm]});
            skFitSpline(sketch, "E1778", {"points": [v(-99.5, 6.24) * mm, v(-99.16, 6.12) * mm, v(-98.82, 6) * mm, v(-98.49, 5.88) * mm]});
            skFitSpline(sketch, "E1779", {"points": [v(-98.49, 5.88) * mm, v(-98.3, 5.82) * mm, v(-98.2, 5.7) * mm, v(-98.16, 5.5) * mm]});
            skFitSpline(sketch, "E1780", {"points": [v(-98.16, 5.5) * mm, v(-98.15, 5.45) * mm, v(-98.1, 5.38) * mm, v(-98.05, 5.34) * mm]});
            skFitSpline(sketch, "E1781", {"points": [v(-98.05, 5.34) * mm, v(-97.92, 5.2) * mm, v(-97.86, 5.06) * mm, v(-97.9, 4.88) * mm]});
            skFitSpline(sketch, "E1782", {"points": [v(-97.9, 4.88) * mm, v(-97.97, 4.5) * mm, v(-98.04, 4.13) * mm, v(-98.12, 3.76) * mm]});
            skFitSpline(sketch, "E1783", {"points": [v(-98.12, 3.76) * mm, v(-98.13, 3.67) * mm, v(-98.15, 3.59) * mm, v(-98.17, 3.47) * mm]});
            skFitSpline(sketch, "E1784", {"points": [v(-98.17, 3.47) * mm, v(-97.93, 3.56) * mm, v(-97.73, 3.64) * mm, v(-97.5, 3.72) * mm]});
            skFitSpline(sketch, "E1785", {"points": [v(-118.18, -6.16) * mm, v(-117.99, -6.21) * mm, v(-117.83, -6.26) * mm, v(-117.67, -6.3) * mm]});
            skFitSpline(sketch, "E1786", {"points": [v(-117.67, -6.3) * mm, v(-117.07, -6.46) * mm, v(-116.47, -6.61) * mm, v(-115.86, -6.77) * mm]});
            skFitSpline(sketch, "E1787", {"points": [v(-115.86, -6.77) * mm, v(-115.81, -6.78) * mm, v(-115.74, -6.8) * mm, v(-115.7, -6.77) * mm]});
            skFitSpline(sketch, "E1788", {"points": [v(-115.7, -6.77) * mm, v(-115.54, -6.64) * mm, v(-115.36, -6.53) * mm, v(-115.22, -6.35) * mm]});
            skFitSpline(sketch, "E1789", {"points": [v(-115.22, -6.35) * mm, v(-115.3, -6.32) * mm, v(-115.37, -6.3) * mm, v(-115.44, -6.27) * mm]});
            skFitSpline(sketch, "E1790", {"points": [v(-115.44, -6.27) * mm, v(-115.78, -6.15) * mm, v(-116.12, -6.04) * mm, v(-116.46, -5.93) * mm]});
            skFitSpline(sketch, "E1791", {"points": [v(-116.46, -5.93) * mm, v(-116.68, -5.85) * mm, v(-116.83, -5.72) * mm, v(-116.88, -5.49) * mm]});
            skFitSpline(sketch, "E1792", {"points": [v(-116.88, -5.49) * mm, v(-116.9, -5.44) * mm, v(-116.92, -5.4) * mm, v(-116.95, -5.37) * mm]});
            skFitSpline(sketch, "E1793", {"points": [v(-116.95, -5.37) * mm, v(-117.12, -5.23) * mm, v(-117.15, -5.05) * mm, v(-117.12, -4.85) * mm]});
            skFitSpline(sketch, "E1794", {"points": [v(-117.12, -4.85) * mm, v(-117.05, -4.5) * mm, v(-116.98, -4.14) * mm, v(-116.92, -3.8) * mm]});
            skFitSpline(sketch, "E1795", {"points": [v(-116.92, -3.8) * mm, v(-116.9, -3.7) * mm, v(-116.88, -3.6) * mm, v(-116.86, -3.48) * mm]});
            skFitSpline(sketch, "E1796", {"points": [v(-116.86, -3.48) * mm, v(-117.1, -3.58) * mm, v(-117.32, -3.66) * mm, v(-117.53, -3.74) * mm]});
            skFitSpline(sketch, "E1797", {"points": [v(-117.53, -3.74) * mm, v(-117.75, -4.55) * mm, v(-117.96, -5.35) * mm, v(-118.18, -6.16) * mm]});
            skFitSpline(sketch, "E1798", {"points": [v(-99.84, -6.36) * mm, v(-99.67, -6.5) * mm, v(-99.53, -6.6) * mm, v(-99.4, -6.71) * mm]});
            skFitSpline(sketch, "E1799", {"points": [v(-99.4, -6.71) * mm, v(-99.32, -6.78) * mm, v(-99.24, -6.8) * mm, v(-99.14, -6.77) * mm]});
            skFitSpline(sketch, "E1800", {"points": [v(-99.14, -6.77) * mm, v(-98.6, -6.62) * mm, v(-98.07, -6.5) * mm, v(-97.54, -6.36) * mm]});
            skFitSpline(sketch, "E1801", {"points": [v(-97.54, -6.36) * mm, v(-97.31, -6.3) * mm, v(-97.09, -6.23) * mm, v(-96.84, -6.16) * mm]});
            skFitSpline(sketch, "E1802", {"points": [v(-96.84, -6.16) * mm, v(-97.06, -5.34) * mm, v(-97.28, -4.54) * mm, v(-97.5, -3.73) * mm]});
            skFitSpline(sketch, "E1803", {"points": [v(-97.5, -3.73) * mm, v(-97.72, -3.65) * mm, v(-97.93, -3.57) * mm, v(-98.17, -3.48) * mm]});
            skFitSpline(sketch, "E1804", {"points": [v(-98.17, -3.48) * mm, v(-98.15, -3.59) * mm, v(-98.14, -3.66) * mm, v(-98.12, -3.73) * mm]});
            skFitSpline(sketch, "E1805", {"points": [v(-98.12, -3.73) * mm, v(-98.05, -4.11) * mm, v(-97.98, -4.5) * mm, v(-97.9, -4.87) * mm]});
            skFitSpline(sketch, "E1806", {"points": [v(-97.9, -4.87) * mm, v(-97.86, -5.06) * mm, v(-97.92, -5.22) * mm, v(-98.06, -5.35) * mm]});
            skFitSpline(sketch, "E1807", {"points": [v(-98.06, -5.35) * mm, v(-98.1, -5.4) * mm, v(-98.15, -5.45) * mm, v(-98.16, -5.5) * mm]});
            skFitSpline(sketch, "E1808", {"points": [v(-98.16, -5.5) * mm, v(-98.19, -5.7) * mm, v(-98.3, -5.83) * mm, v(-98.5, -5.9) * mm]});
            skFitSpline(sketch, "E1809", {"points": [v(-98.5, -5.9) * mm, v(-98.83, -6.02) * mm, v(-99.17, -6.13) * mm, v(-99.5, -6.25) * mm]});
            skFitSpline(sketch, "E1810", {"points": [v(-99.5, -6.25) * mm, v(-99.6, -6.28) * mm, v(-99.7, -6.31) * mm, v(-99.84, -6.36) * mm]});
            skFitSpline(sketch, "E1811", {"points": [v(-108.84, 7.6) * mm, v(-108.75, 7.68) * mm, v(-108.7, 7.72) * mm, v(-108.66, 7.76) * mm]});
            skFitSpline(sketch, "E1812", {"points": [v(-108.66, 7.76) * mm, v(-108.44, 7.97) * mm, v(-108.22, 8.19) * mm, v(-108, 8.4) * mm]});
            skFitSpline(sketch, "E1813", {"points": [v(-108, 8.4) * mm, v(-107.78, 8.6) * mm, v(-107.33, 8.64) * mm, v(-107.1, 8.45) * mm]});
            skFitSpline(sketch, "E1814", {"points": [v(-107.1, 8.45) * mm, v(-106.88, 8.28) * mm, v(-106.7, 8.09) * mm, v(-106.5, 7.9) * mm]});
            skFitSpline(sketch, "E1815", {"points": [v(-106.5, 7.9) * mm, v(-106.4, 7.81) * mm, v(-106.31, 7.72) * mm, v(-106.18, 7.6) * mm]});
            skFitSpline(sketch, "E1816", {"points": [v(-106.18, 7.6) * mm, v(-106.13, 7.93) * mm, v(-106.1, 8.22) * mm, v(-106.06, 8.5) * mm]});
            skFitSpline(sketch, "E1817", {"points": [v(-106.06, 8.5) * mm, v(-106.03, 8.63) * mm, v(-106.06, 8.72) * mm, v(-106.17, 8.8) * mm]});
            skFitSpline(sketch, "E1818", {"points": [v(-106.17, 8.8) * mm, v(-106.45, 9.06) * mm, v(-106.72, 9.31) * mm, v(-107, 9.56) * mm]});
            skFitSpline(sketch, "E1819", {"points": [v(-107, 9.56) * mm, v(-107.16, 9.7) * mm, v(-107.34, 9.83) * mm, v(-107.53, 9.98) * mm]});
            skFitSpline(sketch, "E1820", {"points": [v(-107.53, 9.98) * mm, v(-108.02, 9.55) * mm, v(-108.5, 9.12) * mm, v(-109, 8.68) * mm]});
            skFitSpline(sketch, "E1821", {"points": [v(-109, 8.68) * mm, v(-108.95, 8.34) * mm, v(-108.9, 8) * mm, v(-108.84, 7.6) * mm]});
            skFitSpline(sketch, "E1822", {"points": [v(-109, -8.7) * mm, v(-108.5, -9.13) * mm, v(-108.02, -9.56) * mm, v(-107.51, -10) * mm]});
            skFitSpline(sketch, "E1823", {"points": [v(-107.51, -10) * mm, v(-107, -9.56) * mm, v(-106.53, -9.13) * mm, v(-106.04, -8.7) * mm]});
            skFitSpline(sketch, "E1824", {"points": [v(-106.04, -8.7) * mm, v(-106.1, -8.35) * mm, v(-106.09, -7.99) * mm, v(-106.2, -7.63) * mm]});
            skFitSpline(sketch, "E1825", {"points": [v(-106.2, -7.63) * mm, v(-106.48, -7.89) * mm, v(-106.73, -8.13) * mm, v(-106.98, -8.36) * mm]});
            skFitSpline(sketch, "E1826", {"points": [v(-106.98, -8.36) * mm, v(-107.29, -8.66) * mm, v(-107.73, -8.66) * mm, v(-108.03, -8.37) * mm]});
            skFitSpline(sketch, "E1827", {"points": [v(-108.03, -8.37) * mm, v(-108.25, -8.16) * mm, v(-108.47, -7.95) * mm, v(-108.69, -7.74) * mm]});
            skFitSpline(sketch, "E1828", {"points": [v(-108.69, -7.74) * mm, v(-108.73, -7.7) * mm, v(-108.77, -7.68) * mm, v(-108.85, -7.62) * mm]});
            skFitSpline(sketch, "E1829", {"points": [v(-108.85, -7.62) * mm, v(-108.9, -8) * mm, v(-108.95, -8.35) * mm, v(-109, -8.7) * mm]});
            skFitSpline(sketch, "E1830", {"points": [v(-113.43, -4.96) * mm, v(-113.83, -4.84) * mm, v(-114.17, -4.74) * mm, v(-114.51, -4.64) * mm]});
            skFitSpline(sketch, "E1831", {"points": [v(-114.51, -4.64) * mm, v(-114.89, -4.52) * mm, v(-115.11, -4.13) * mm, v(-115.03, -3.76) * mm]});
            skFitSpline(sketch, "E1832", {"points": [v(-115.03, -3.76) * mm, v(-114.95, -3.45) * mm, v(-114.88, -3.15) * mm, v(-114.8, -2.85) * mm]});
            skFitSpline(sketch, "E1833", {"points": [v(-114.8, -2.85) * mm, v(-114.8, -2.8) * mm, v(-114.79, -2.75) * mm, v(-114.77, -2.66) * mm]});
            skFitSpline(sketch, "E1834", {"points": [v(-114.77, -2.66) * mm, v(-115.12, -2.8) * mm, v(-115.45, -2.93) * mm, v(-115.79, -3.07) * mm]});
            skFitSpline(sketch, "E1835", {"points": [v(-115.79, -3.07) * mm, v(-115.87, -3.72) * mm, v(-116.09, -4.34) * mm, v(-116.15, -5.01) * mm]});
            skFitSpline(sketch, "E1836", {"points": [v(-116.15, -5.01) * mm, v(-115.55, -5.21) * mm, v(-114.97, -5.4) * mm, v(-114.39, -5.6) * mm]});
            skFitSpline(sketch, "E1837", {"points": [v(-114.39, -5.6) * mm, v(-114.34, -5.6) * mm, v(-114.27, -5.6) * mm, v(-114.24, -5.57) * mm]});
            skFitSpline(sketch, "E1838", {"points": [v(-114.24, -5.57) * mm, v(-113.97, -5.38) * mm, v(-113.72, -5.18) * mm, v(-113.43, -4.96) * mm]});
            skFitSpline(sketch, "E1839", {"points": [v(-116.17, 4.98) * mm, v(-116.04, 4.32) * mm, v(-115.9, 3.68) * mm, v(-115.77, 3.06) * mm]});
            skFitSpline(sketch, "E1840", {"points": [v(-115.77, 3.06) * mm, v(-115.43, 2.92) * mm, v(-115.11, 2.79) * mm, v(-114.77, 2.65) * mm]});
            skFitSpline(sketch, "E1841", {"points": [v(-114.77, 2.65) * mm, v(-114.78, 2.73) * mm, v(-114.78, 2.76) * mm, v(-114.8, 2.8) * mm]});
            skFitSpline(sketch, "E1842", {"points": [v(-114.8, 2.8) * mm, v(-114.87, 3.12) * mm, v(-114.95, 3.43) * mm, v(-115.03, 3.75) * mm]});
            skFitSpline(sketch, "E1843", {"points": [v(-115.03, 3.75) * mm, v(-115.11, 4.11) * mm, v(-114.88, 4.51) * mm, v(-114.53, 4.62) * mm]});
            skFitSpline(sketch, "E1844", {"points": [v(-114.53, 4.62) * mm, v(-114.23, 4.71) * mm, v(-113.93, 4.8) * mm, v(-113.64, 4.88) * mm]});
            skFitSpline(sketch, "E1845", {"points": [v(-113.64, 4.88) * mm, v(-113.58, 4.9) * mm, v(-113.52, 4.91) * mm, v(-113.43, 4.95) * mm]});
            skFitSpline(sketch, "E1846", {"points": [v(-113.43, 4.95) * mm, v(-113.69, 5.15) * mm, v(-113.92, 5.32) * mm, v(-114.14, 5.5) * mm]});
            skFitSpline(sketch, "E1847", {"points": [v(-114.14, 5.5) * mm, v(-114.25, 5.6) * mm, v(-114.35, 5.61) * mm, v(-114.49, 5.56) * mm]});
            skFitSpline(sketch, "E1848", {"points": [v(-114.49, 5.56) * mm, v(-114.83, 5.44) * mm, v(-115.19, 5.34) * mm, v(-115.53, 5.22) * mm]});
            skFitSpline(sketch, "E1849", {"points": [v(-115.53, 5.22) * mm, v(-115.74, 5.15) * mm, v(-115.93, 5.07) * mm, v(-116.17, 4.98) * mm]});
            skFitSpline(sketch, "E1850", {"points": [v(-100.26, 2.65) * mm, v(-99.9, 2.8) * mm, v(-99.57, 2.93) * mm, v(-99.25, 3.06) * mm]});
            skFitSpline(sketch, "E1851", {"points": [v(-99.25, 3.06) * mm, v(-99.18, 3.4) * mm, v(-99.12, 3.72) * mm, v(-99.04, 4.04) * mm]});
            skFitSpline(sketch, "E1852", {"points": [v(-99.04, 4.04) * mm, v(-98.97, 4.35) * mm, v(-98.9, 4.67) * mm, v(-98.89, 5) * mm]});
            skFitSpline(sketch, "E1853", {"points": [v(-98.89, 5) * mm, v(-99.39, 5.17) * mm, v(-99.87, 5.33) * mm, v(-100.35, 5.5) * mm]});
            skFitSpline(sketch, "E1854", {"points": [v(-100.35, 5.5) * mm, v(-100.72, 5.62) * mm, v(-100.72, 5.63) * mm, v(-101.01, 5.4) * mm]});
            skFitSpline(sketch, "E1855", {"points": [v(-101.01, 5.4) * mm, v(-101.2, 5.26) * mm, v(-101.39, 5.1) * mm, v(-101.59, 4.95) * mm]});
            skFitSpline(sketch, "E1856", {"points": [v(-101.59, 4.95) * mm, v(-101.23, 4.84) * mm, v(-100.9, 4.74) * mm, v(-100.59, 4.65) * mm]});
            skFitSpline(sketch, "E1857", {"points": [v(-100.59, 4.65) * mm, v(-100.1, 4.5) * mm, v(-99.9, 4.14) * mm, v(-100.02, 3.66) * mm]});
            skFitSpline(sketch, "E1858", {"points": [v(-100.02, 3.66) * mm, v(-100.1, 3.34) * mm, v(-100.17, 3.02) * mm, v(-100.26, 2.65) * mm]});
            skFitSpline(sketch, "E1859", {"points": [v(-101.6, -4.96) * mm, v(-101.35, -5.15) * mm, v(-101.13, -5.3) * mm, v(-100.92, -5.48) * mm]});
            skFitSpline(sketch, "E1860", {"points": [v(-100.92, -5.48) * mm, v(-100.79, -5.6) * mm, v(-100.66, -5.62) * mm, v(-100.5, -5.56) * mm]});
            skFitSpline(sketch, "E1861", {"points": [v(-100.5, -5.56) * mm, v(-100.17, -5.44) * mm, v(-99.84, -5.35) * mm, v(-99.51, -5.24) * mm]});
            skFitSpline(sketch, "E1862", {"points": [v(-99.51, -5.24) * mm, v(-99.3, -5.17) * mm, v(-99.1, -5.08) * mm, v(-98.88, -5) * mm]});
            skFitSpline(sketch, "E1863", {"points": [v(-98.88, -5) * mm, v(-98.94, -4.33) * mm, v(-99.15, -3.71) * mm, v(-99.24, -3.08) * mm]});
            skFitSpline(sketch, "E1864", {"points": [v(-99.24, -3.08) * mm, v(-99.42, -3) * mm, v(-99.58, -2.93) * mm, v(-99.74, -2.86) * mm]});
            skFitSpline(sketch, "E1865", {"points": [v(-99.74, -2.86) * mm, v(-99.9, -2.8) * mm, v(-100.06, -2.7) * mm, v(-100.27, -2.7) * mm]});
            skFitSpline(sketch, "E1866", {"points": [v(-100.27, -2.7) * mm, v(-100.21, -2.88) * mm, v(-100.16, -3.04) * mm, v(-100.12, -3.2) * mm]});
            skFitSpline(sketch, "E1867", {"points": [v(-100.12, -3.2) * mm, v(-100.08, -3.36) * mm, v(-100.05, -3.53) * mm, v(-100.01, -3.69) * mm]});
            skFitSpline(sketch, "E1868", {"points": [v(-100.01, -3.69) * mm, v(-99.9, -4.15) * mm, v(-100.12, -4.52) * mm, v(-100.56, -4.65) * mm]});
            skFitSpline(sketch, "E1869", {"points": [v(-100.56, -4.65) * mm, v(-100.9, -4.75) * mm, v(-101.22, -4.85) * mm, v(-101.6, -4.96) * mm]});
            skFitSpline(sketch, "E1870", {"points": [v(-100.04, 1.69) * mm, v(-100.06, 1.66) * mm, v(-100.07, 1.64) * mm, v(-100.08, 1.61) * mm]});
            skFitSpline(sketch, "E1871", {"points": [v(-100.08, 1.61) * mm, v(-100, 1.56) * mm, v(-99.92, 1.5) * mm, v(-99.85, 1.44) * mm]});
            skFitSpline(sketch, "E1872", {"points": [v(-99.85, 1.44) * mm, v(-99.6, 1.22) * mm, v(-99.35, 1) * mm, v(-99.1, 0.77) * mm]});
            skFitSpline(sketch, "E1873", {"points": [v(-99.1, 0.77) * mm, v(-98.9, 0.56) * mm, v(-98.72, 0.34) * mm, v(-98.8, 0.01) * mm]});
            skFitSpline(sketch, "E1874", {"points": [v(-98.8, 0.01) * mm, v(-98.81, -0.03) * mm, v(-98.8, -0.08) * mm, v(-98.79, -0.13) * mm]});
            skFitSpline(sketch, "E1875", {"points": [v(-98.79, -0.13) * mm, v(-98.77, -0.29) * mm, v(-98.8, -0.44) * mm, v(-98.92, -0.55) * mm]});
            skFitSpline(sketch, "E1876", {"points": [v(-98.92, -0.55) * mm, v(-99.14, -0.78) * mm, v(-99.36, -1) * mm, v(-99.59, -1.23) * mm]});
            skFitSpline(sketch, "E1877", {"points": [v(-99.59, -1.23) * mm, v(-99.74, -1.38) * mm, v(-99.93, -1.48) * mm, v(-100.06, -1.69) * mm]});
            skFitSpline(sketch, "E1878", {"points": [v(-100.06, -1.69) * mm, v(-99.65, -1.85) * mm, v(-99.24, -2.01) * mm, v(-98.85, -2.17) * mm]});
            skFitSpline(sketch, "E1879", {"points": [v(-98.85, -2.17) * mm, v(-98.25, -1.38) * mm, v(-97.55, -0.7) * mm, v(-96.87, 0) * mm]});
            skFitSpline(sketch, "E1880", {"points": [v(-96.87, 0) * mm, v(-97.57, 0.7) * mm, v(-98.25, 1.38) * mm, v(-98.86, 2.16) * mm]});
            skFitSpline(sketch, "E1881", {"points": [v(-98.86, 2.16) * mm, v(-99.25, 2) * mm, v(-99.65, 1.85) * mm, v(-100.04, 1.69) * mm]});
            skFitSpline(sketch, "E1882", {"points": [v(-97.23, -8.57) * mm, v(-97.1, -8.39) * mm, v(-96.92, -8.34) * mm, v(-96.75, -8.28) * mm]});
            skFitSpline(sketch, "E1883", {"points": [v(-96.75, -8.28) * mm, v(-96.16, -8.06) * mm, v(-95.57, -7.84) * mm, v(-94.99, -7.6) * mm]});
            skFitSpline(sketch, "E1884", {"points": [v(-94.99, -7.6) * mm, v(-94.87, -7.56) * mm, v(-94.72, -7.52) * mm, v(-94.66, -7.42) * mm]});
            skFitSpline(sketch, "E1885", {"points": [v(-94.66, -7.42) * mm, v(-94.6, -7.34) * mm, v(-94.65, -7.2) * mm, v(-94.66, -7.08) * mm]});
            skFitSpline(sketch, "E1886", {"points": [v(-94.66, -7.08) * mm, v(-94.72, -6.6) * mm, v(-94.79, -6.1) * mm, v(-94.86, -5.61) * mm]});
            skFitSpline(sketch, "E1887", {"points": [v(-94.86, -5.61) * mm, v(-94.92, -5.28) * mm, v(-95.06, -4.96) * mm, v(-94.98, -4.61) * mm]});
            skFitSpline(sketch, "E1888", {"points": [v(-94.98, -4.61) * mm, v(-95.44, -4.46) * mm, v(-95.89, -4.32) * mm, v(-96.34, -4.18) * mm]});
            skFitSpline(sketch, "E1889", {"points": [v(-96.34, -4.18) * mm, v(-96.34, -4.22) * mm, v(-96.34, -4.25) * mm, v(-96.33, -4.27) * mm]});
            skFitSpline(sketch, "E1890", {"points": [v(-96.33, -4.27) * mm, v(-96.23, -4.67) * mm, v(-96.13, -5.07) * mm, v(-96.02, -5.47) * mm]});
            skFitSpline(sketch, "E1891", {"points": [v(-96.02, -5.47) * mm, v(-95.94, -5.76) * mm, v(-95.86, -6.04) * mm, v(-95.76, -6.31) * mm]});
            skFitSpline(sketch, "E1892", {"points": [v(-95.76, -6.31) * mm, v(-95.67, -6.6) * mm, v(-95.86, -6.96) * mm, v(-96.16, -7.02) * mm]});
            skFitSpline(sketch, "E1893", {"points": [v(-96.16, -7.02) * mm, v(-96.34, -7.06) * mm, v(-96.52, -7.09) * mm, v(-96.7, -7.13) * mm]});
            skFitSpline(sketch, "E1894", {"points": [v(-96.7, -7.13) * mm, v(-97.23, -7.28) * mm, v(-97.77, -7.42) * mm, v(-98.33, -7.58) * mm]});
            skFitSpline(sketch, "E1895", {"points": [v(-98.33, -7.58) * mm, v(-97.96, -7.92) * mm, v(-97.6, -8.23) * mm, v(-97.23, -8.57) * mm]});
            skFitSpline(sketch, "E1896", {"points": [v(-109.78, -13.13) * mm, v(-109.6, -13.25) * mm, v(-109.46, -13.33) * mm, v(-109.33, -13.44) * mm]});
            skFitSpline(sketch, "E1897", {"points": [v(-109.33, -13.44) * mm, v(-108.89, -13.8) * mm, v(-108.46, -14.17) * mm, v(-108.02, -14.52) * mm]});
            skFitSpline(sketch, "E1898", {"points": [v(-108.02, -14.52) * mm, v(-107.86, -14.65) * mm, v(-107.68, -14.76) * mm, v(-107.5, -14.88) * mm]});
            skFitSpline(sketch, "E1899", {"points": [v(-107.5, -14.88) * mm, v(-106.9, -14.44) * mm, v(-106.31, -14.02) * mm, v(-105.78, -13.52) * mm]});
            skFitSpline(sketch, "E1900", {"points": [v(-105.78, -13.52) * mm, v(-105.63, -13.37) * mm, v(-105.48, -13.21) * mm, v(-105.24, -13.18) * mm]});
            skFitSpline(sketch, "E1901", {"points": [v(-105.24, -13.18) * mm, v(-105.34, -12.7) * mm, v(-105.44, -12.24) * mm, v(-105.54, -11.74) * mm]});
            skFitSpline(sketch, "E1902", {"points": [v(-105.54, -11.74) * mm, v(-105.95, -12.15) * mm, v(-106.34, -12.53) * mm, v(-106.72, -12.9) * mm]});
            skFitSpline(sketch, "E1903", {"points": [v(-106.72, -12.9) * mm, v(-106.83, -13.03) * mm, v(-106.97, -13.14) * mm, v(-107.05, -13.28) * mm]});
            skFitSpline(sketch, "E1904", {"points": [v(-107.05, -13.28) * mm, v(-107.25, -13.58) * mm, v(-107.78, -13.6) * mm, v(-107.97, -13.27) * mm]});
            skFitSpline(sketch, "E1905", {"points": [v(-107.97, -13.27) * mm, v(-108, -13.23) * mm, v(-108.02, -13.19) * mm, v(-108.05, -13.16) * mm]});
            skFitSpline(sketch, "E1906", {"points": [v(-108.05, -13.16) * mm, v(-108.35, -12.86) * mm, v(-108.65, -12.56) * mm, v(-108.95, -12.26) * mm]});
            skFitSpline(sketch, "E1907", {"points": [v(-108.95, -12.26) * mm, v(-109.12, -12.1) * mm, v(-109.3, -11.93) * mm, v(-109.49, -11.75) * mm]});
            skFitSpline(sketch, "E1908", {"points": [v(-109.49, -11.75) * mm, v(-109.59, -12.24) * mm, v(-109.69, -12.7) * mm, v(-109.78, -13.13) * mm]});
            skFitSpline(sketch, "E1909", {"points": [v(-109.49, 11.75) * mm, v(-109.43, 11.8) * mm, v(-109.4, 11.82) * mm, v(-109.36, 11.85) * mm]});
            skFitSpline(sketch, "E1910", {"points": [v(-109.36, 11.85) * mm, v(-109.04, 12.17) * mm, v(-108.71, 12.49) * mm, v(-108.39, 12.8) * mm]});
            skFitSpline(sketch, "E1911", {"points": [v(-108.39, 12.8) * mm, v(-108.23, 12.97) * mm, v(-108.08, 13.15) * mm, v(-107.93, 13.32) * mm]});
            skFitSpline(sketch, "E1912", {"points": [v(-107.93, 13.32) * mm, v(-107.72, 13.56) * mm, v(-107.33, 13.57) * mm, v(-107.12, 13.34) * mm]});
            skFitSpline(sketch, "E1913", {"points": [v(-107.12, 13.34) * mm, v(-107, 13.22) * mm, v(-106.9, 13.09) * mm, v(-106.78, 12.97) * mm]});
            skFitSpline(sketch, "E1914", {"points": [v(-106.78, 12.97) * mm, v(-106.4, 12.6) * mm, v(-106.03, 12.23) * mm, v(-105.66, 11.85) * mm]});
            skFitSpline(sketch, "E1915", {"points": [v(-105.66, 11.85) * mm, v(-105.62, 11.82) * mm, v(-105.58, 11.8) * mm, v(-105.53, 11.76) * mm]});
            skFitSpline(sketch, "E1916", {"points": [v(-105.53, 11.76) * mm, v(-105.43, 12.24) * mm, v(-105.34, 12.7) * mm, v(-105.25, 13.12) * mm]});
            skFitSpline(sketch, "E1917", {"points": [v(-105.25, 13.12) * mm, v(-105.42, 13.24) * mm, v(-105.57, 13.33) * mm, v(-105.7, 13.43) * mm]});
            skFitSpline(sketch, "E1918", {"points": [v(-105.7, 13.43) * mm, v(-106.02, 13.7) * mm, v(-106.33, 13.98) * mm, v(-106.65, 14.24) * mm]});
            skFitSpline(sketch, "E1919", {"points": [v(-106.65, 14.24) * mm, v(-106.93, 14.46) * mm, v(-107.21, 14.66) * mm, v(-107.5, 14.87) * mm]});
            skFitSpline(sketch, "E1920", {"points": [v(-107.5, 14.87) * mm, v(-107.58, 14.81) * mm, v(-107.65, 14.78) * mm, v(-107.72, 14.73) * mm]});
            skFitSpline(sketch, "E1921", {"points": [v(-107.72, 14.73) * mm, v(-108.22, 14.33) * mm, v(-108.72, 13.94) * mm, v(-109.21, 13.53) * mm]});
            skFitSpline(sketch, "E1922", {"points": [v(-109.21, 13.53) * mm, v(-109.39, 13.39) * mm, v(-109.54, 13.2) * mm, v(-109.79, 13.16) * mm]});
            skFitSpline(sketch, "E1923", {"points": [v(-109.79, 13.16) * mm, v(-109.69, 12.69) * mm, v(-109.59, 12.23) * mm, v(-109.49, 11.75) * mm]});
            skFitSpline(sketch, "E1924", {"points": [v(-116.7, -7.58) * mm, v(-117.21, -7.44) * mm, v(-117.7, -7.3) * mm, v(-118.2, -7.17) * mm]});
            skFitSpline(sketch, "E1925", {"points": [v(-118.2, -7.17) * mm, v(-118.41, -7.11) * mm, v(-118.64, -7.07) * mm, v(-118.87, -7.02) * mm]});
            skFitSpline(sketch, "E1926", {"points": [v(-118.87, -7.02) * mm, v(-119.18, -6.95) * mm, v(-119.37, -6.6) * mm, v(-119.25, -6.3) * mm]});
            skFitSpline(sketch, "E1927", {"points": [v(-119.25, -6.3) * mm, v(-119.21, -6.2) * mm, v(-119.17, -6.1) * mm, v(-119.15, -6) * mm]});
            skFitSpline(sketch, "E1928", {"points": [v(-119.15, -6) * mm, v(-119.06, -5.69) * mm, v(-118.98, -5.37) * mm, v(-118.9, -5.06) * mm]});
            skFitSpline(sketch, "E1929", {"points": [v(-118.9, -5.06) * mm, v(-118.82, -4.77) * mm, v(-118.75, -4.48) * mm, v(-118.67, -4.17) * mm]});
            skFitSpline(sketch, "E1930", {"points": [v(-118.67, -4.17) * mm, v(-119.15, -4.32) * mm, v(-119.6, -4.47) * mm, v(-120.01, -4.6) * mm]});
            skFitSpline(sketch, "E1931", {"points": [v(-120.01, -4.6) * mm, v(-120.03, -4.79) * mm, v(-120.02, -4.95) * mm, v(-120.05, -5.1) * mm]});
            skFitSpline(sketch, "E1932", {"points": [v(-120.05, -5.1) * mm, v(-120.13, -5.62) * mm, v(-120.24, -6.13) * mm, v(-120.32, -6.65) * mm]});
            skFitSpline(sketch, "E1933", {"points": [v(-120.32, -6.65) * mm, v(-120.36, -6.9) * mm, v(-120.37, -7.17) * mm, v(-120.4, -7.43) * mm]});
            skFitSpline(sketch, "E1934", {"points": [v(-120.4, -7.43) * mm, v(-120.3, -7.48) * mm, v(-120.23, -7.53) * mm, v(-120.14, -7.56) * mm]});
            skFitSpline(sketch, "E1935", {"points": [v(-120.14, -7.56) * mm, v(-119.54, -7.8) * mm, v(-118.94, -8.03) * mm, v(-118.34, -8.26) * mm]});
            skFitSpline(sketch, "E1936", {"points": [v(-118.34, -8.26) * mm, v(-118.14, -8.34) * mm, v(-117.93, -8.38) * mm, v(-117.78, -8.55) * mm]});
            skFitSpline(sketch, "E1937", {"points": [v(-117.78, -8.55) * mm, v(-117.43, -8.24) * mm, v(-117.09, -7.94) * mm, v(-116.75, -7.64) * mm]});
            skFitSpline(sketch, "E1938", {"points": [v(-116.75, -7.64) * mm, v(-116.74, -7.63) * mm, v(-116.73, -7.62) * mm, v(-116.7, -7.58) * mm]});
            skFitSpline(sketch, "E1939", {"points": [v(-98.33, 7.57) * mm, v(-97.8, 7.42) * mm, v(-97.29, 7.28) * mm, v(-96.78, 7.14) * mm]});
            skFitSpline(sketch, "E1940", {"points": [v(-96.78, 7.14) * mm, v(-96.58, 7.09) * mm, v(-96.37, 7.06) * mm, v(-96.17, 7.02) * mm]});
            skFitSpline(sketch, "E1941", {"points": [v(-96.17, 7.02) * mm, v(-95.87, 6.96) * mm, v(-95.66, 6.61) * mm, v(-95.76, 6.32) * mm]});
            skFitSpline(sketch, "E1942", {"points": [v(-95.76, 6.32) * mm, v(-95.81, 6.16) * mm, v(-95.87, 6) * mm, v(-95.9, 5.84) * mm]});
            skFitSpline(sketch, "E1943", {"points": [v(-95.9, 5.84) * mm, v(-96.05, 5.33) * mm, v(-96.19, 4.81) * mm, v(-96.32, 4.3) * mm]});
            skFitSpline(sketch, "E1944", {"points": [v(-96.32, 4.3) * mm, v(-96.33, 4.26) * mm, v(-96.33, 4.21) * mm, v(-96.33, 4.17) * mm]});
            skFitSpline(sketch, "E1945", {"points": [v(-96.33, 4.17) * mm, v(-95.87, 4.32) * mm, v(-95.42, 4.46) * mm, v(-95.02, 4.6) * mm]});
            skFitSpline(sketch, "E1946", {"points": [v(-95.02, 4.6) * mm, v(-95, 4.81) * mm, v(-94.99, 5) * mm, v(-94.96, 5.17) * mm]});
            skFitSpline(sketch, "E1947", {"points": [v(-94.96, 5.17) * mm, v(-94.92, 5.39) * mm, v(-94.85, 5.6) * mm, v(-94.82, 5.82) * mm]});
            skFitSpline(sketch, "E1948", {"points": [v(-94.82, 5.82) * mm, v(-94.76, 6.28) * mm, v(-94.7, 6.74) * mm, v(-94.65, 7.2) * mm]});
            skFitSpline(sketch, "E1949", {"points": [v(-94.65, 7.2) * mm, v(-94.63, 7.43) * mm, v(-94.62, 7.44) * mm, v(-94.82, 7.52) * mm]});
            skFitSpline(sketch, "E1950", {"points": [v(-94.82, 7.52) * mm, v(-95.44, 7.77) * mm, v(-96.06, 8.02) * mm, v(-96.7, 8.25) * mm]});
            skFitSpline(sketch, "E1951", {"points": [v(-96.7, 8.25) * mm, v(-96.89, 8.33) * mm, v(-97.1, 8.37) * mm, v(-97.24, 8.56) * mm]});
            skFitSpline(sketch, "E1952", {"points": [v(-97.24, 8.56) * mm, v(-97.6, 8.22) * mm, v(-97.96, 7.91) * mm, v(-98.33, 7.57) * mm]});
            skFitSpline(sketch, "E1953", {"points": [v(-105.25, 7.27) * mm, v(-105.13, 7.3) * mm, v(-105.06, 7.31) * mm, v(-104.98, 7.34) * mm]});
            skFitSpline(sketch, "E1954", {"points": [v(-104.98, 7.34) * mm, v(-104.65, 7.44) * mm, v(-104.32, 7.56) * mm, v(-103.98, 7.66) * mm]});
            skFitSpline(sketch, "E1955", {"points": [v(-103.98, 7.66) * mm, v(-103.85, 7.7) * mm, v(-103.7, 7.73) * mm, v(-103.56, 7.71) * mm]});
            skFitSpline(sketch, "E1956", {"points": [v(-103.56, 7.71) * mm, v(-103.25, 7.67) * mm, v(-103, 7.5) * mm, v(-102.8, 7.27) * mm]});
            skFitSpline(sketch, "E1957", {"points": [v(-102.8, 7.27) * mm, v(-102.7, 7.16) * mm, v(-102.67, 7) * mm, v(-102.63, 6.85) * mm]});
            skFitSpline(sketch, "E1958", {"points": [v(-102.63, 6.85) * mm, v(-102.56, 6.53) * mm, v(-102.5, 6.2) * mm, v(-102.43, 5.87) * mm]});
            skFitSpline(sketch, "E1959", {"points": [v(-102.43, 5.87) * mm, v(-102.4, 5.79) * mm, v(-102.37, 5.7) * mm, v(-102.33, 5.6) * mm]});
            skFitSpline(sketch, "E1960", {"points": [v(-102.33, 5.6) * mm, v(-101.97, 5.9) * mm, v(-101.63, 6.16) * mm, v(-101.3, 6.41) * mm]});
            skFitSpline(sketch, "E1961", {"points": [v(-101.3, 6.41) * mm, v(-101.7, 7.33) * mm, v(-101.92, 8.27) * mm, v(-102.2, 9.2) * mm]});
            skFitSpline(sketch, "E1962", {"points": [v(-102.2, 9.2) * mm, v(-103.17, 8.97) * mm, v(-104.1, 8.7) * mm, v(-105.06, 8.58) * mm]});
            skFitSpline(sketch, "E1963", {"points": [v(-105.06, 8.58) * mm, v(-105.12, 8.16) * mm, v(-105.18, 7.73) * mm, v(-105.25, 7.27) * mm]});
            skFitSpline(sketch, "E1964", {"points": [v(-102.2, -9.22) * mm, v(-101.92, -8.26) * mm, v(-101.69, -7.32) * mm, v(-101.3, -6.42) * mm]});
            skFitSpline(sketch, "E1965", {"points": [v(-101.3, -6.42) * mm, v(-101.64, -6.15) * mm, v(-101.98, -5.89) * mm, v(-102.34, -5.6) * mm]});
            skFitSpline(sketch, "E1966", {"points": [v(-102.34, -5.6) * mm, v(-102.38, -5.72) * mm, v(-102.4, -5.8) * mm, v(-102.43, -5.88) * mm]});
            skFitSpline(sketch, "E1967", {"points": [v(-102.43, -5.88) * mm, v(-102.5, -6.22) * mm, v(-102.58, -6.55) * mm, v(-102.63, -6.89) * mm]});
            skFitSpline(sketch, "E1968", {"points": [v(-102.63, -6.89) * mm, v(-102.7, -7.35) * mm, v(-103.06, -7.56) * mm, v(-103.44, -7.7) * mm]});
            skFitSpline(sketch, "E1969", {"points": [v(-103.44, -7.7) * mm, v(-103.6, -7.76) * mm, v(-103.8, -7.7) * mm, v(-103.98, -7.66) * mm]});
            skFitSpline(sketch, "E1970", {"points": [v(-103.98, -7.66) * mm, v(-104.32, -7.58) * mm, v(-104.65, -7.45) * mm, v(-104.98, -7.35) * mm]});
            skFitSpline(sketch, "E1971", {"points": [v(-104.98, -7.35) * mm, v(-105.06, -7.32) * mm, v(-105.14, -7.31) * mm, v(-105.25, -7.29) * mm]});
            skFitSpline(sketch, "E1972", {"points": [v(-105.25, -7.29) * mm, v(-105.18, -7.75) * mm, v(-105.12, -8.18) * mm, v(-105.06, -8.59) * mm]});
            skFitSpline(sketch, "E1973", {"points": [v(-105.06, -8.59) * mm, v(-104.08, -8.71) * mm, v(-103.16, -8.98) * mm, v(-102.2, -9.22) * mm]});
            skFitSpline(sketch, "E1974", {"points": [v(-118.66, 4.16) * mm, v(-118.77, 4.58) * mm, v(-118.87, 4.97) * mm, v(-118.98, 5.35) * mm]});
            skFitSpline(sketch, "E1975", {"points": [v(-118.98, 5.35) * mm, v(-119.07, 5.66) * mm, v(-119.15, 5.98) * mm, v(-119.26, 6.29) * mm]});
            skFitSpline(sketch, "E1976", {"points": [v(-119.26, 6.29) * mm, v(-119.36, 6.6) * mm, v(-119.17, 6.95) * mm, v(-118.86, 7.02) * mm]});
            skFitSpline(sketch, "E1977", {"points": [v(-118.86, 7.02) * mm, v(-118.7, 7.05) * mm, v(-118.53, 7.08) * mm, v(-118.37, 7.12) * mm]});
            skFitSpline(sketch, "E1978", {"points": [v(-118.37, 7.12) * mm, v(-117.82, 7.26) * mm, v(-117.27, 7.41) * mm, v(-116.69, 7.57) * mm]});
            skFitSpline(sketch, "E1979", {"points": [v(-116.69, 7.57) * mm, v(-117.06, 7.9) * mm, v(-117.42, 8.22) * mm, v(-117.78, 8.55) * mm]});
            skFitSpline(sketch, "E1980", {"points": [v(-117.78, 8.55) * mm, v(-117.93, 8.38) * mm, v(-118.13, 8.33) * mm, v(-118.32, 8.26) * mm]});
            skFitSpline(sketch, "E1981", {"points": [v(-118.32, 8.26) * mm, v(-118.93, 8.03) * mm, v(-119.53, 7.8) * mm, v(-120.13, 7.56) * mm]});
            skFitSpline(sketch, "E1982", {"points": [v(-120.13, 7.56) * mm, v(-120.22, 7.52) * mm, v(-120.3, 7.47) * mm, v(-120.39, 7.43) * mm]});
            skFitSpline(sketch, "E1983", {"points": [v(-120.39, 7.43) * mm, v(-120.39, 7.37) * mm, v(-120.4, 7.32) * mm, v(-120.39, 7.28) * mm]});
            skFitSpline(sketch, "E1984", {"points": [v(-120.39, 7.28) * mm, v(-120.3, 6.65) * mm, v(-120.2, 6.02) * mm, v(-120.1, 5.39) * mm]});
            skFitSpline(sketch, "E1985", {"points": [v(-120.1, 5.39) * mm, v(-120.07, 5.13) * mm, v(-119.95, 4.88) * mm, v(-120.05, 4.6) * mm]});
            skFitSpline(sketch, "E1986", {"points": [v(-120.05, 4.6) * mm, v(-119.59, 4.46) * mm, v(-119.14, 4.31) * mm, v(-118.66, 4.16) * mm]});
            skFitSpline(sketch, "E1987", {"points": [v(-112.68, 5.6) * mm, v(-112.65, 5.7) * mm, v(-112.62, 5.78) * mm, v(-112.6, 5.86) * mm]});
            skFitSpline(sketch, "E1988", {"points": [v(-112.6, 5.86) * mm, v(-112.53, 6.2) * mm, v(-112.46, 6.56) * mm, v(-112.38, 6.9) * mm]});
            skFitSpline(sketch, "E1989", {"points": [v(-112.38, 6.9) * mm, v(-112.3, 7.18) * mm, v(-112.2, 7.45) * mm, v(-111.88, 7.53) * mm]});
            skFitSpline(sketch, "E1990", {"points": [v(-111.88, 7.53) * mm, v(-111.85, 7.53) * mm, v(-111.83, 7.56) * mm, v(-111.8, 7.58) * mm]});
            skFitSpline(sketch, "E1991", {"points": [v(-111.8, 7.58) * mm, v(-111.67, 7.71) * mm, v(-111.5, 7.75) * mm, v(-111.34, 7.7) * mm]});
            skFitSpline(sketch, "E1992", {"points": [v(-111.34, 7.7) * mm, v(-111.03, 7.64) * mm, v(-110.72, 7.56) * mm, v(-110.42, 7.47) * mm]});
            skFitSpline(sketch, "E1993", {"points": [v(-110.42, 7.47) * mm, v(-110.21, 7.41) * mm, v(-110.02, 7.33) * mm, v(-109.77, 7.25) * mm]});
            skFitSpline(sketch, "E1994", {"points": [v(-109.77, 7.25) * mm, v(-109.84, 7.73) * mm, v(-109.9, 8.17) * mm, v(-109.97, 8.59) * mm]});
            skFitSpline(sketch, "E1995", {"points": [v(-109.97, 8.59) * mm, v(-110.96, 8.7) * mm, v(-111.88, 8.98) * mm, v(-112.83, 9.2) * mm]});
            skFitSpline(sketch, "E1996", {"points": [v(-112.83, 9.2) * mm, v(-113.1, 8.26) * mm, v(-113.33, 7.32) * mm, v(-113.72, 6.41) * mm]});
            skFitSpline(sketch, "E1997", {"points": [v(-113.72, 6.41) * mm, v(-113.39, 6.15) * mm, v(-113.05, 5.89) * mm, v(-112.68, 5.6) * mm]});
            skFitSpline(sketch, "E1998", {"points": [v(-113.72, -6.42) * mm, v(-113.34, -7.33) * mm, v(-113.1, -8.27) * mm, v(-112.83, -9.21) * mm]});
            skFitSpline(sketch, "E1999", {"points": [v(-112.83, -9.21) * mm, v(-111.87, -8.98) * mm, v(-110.94, -8.7) * mm, v(-109.96, -8.6) * mm]});
            skFitSpline(sketch, "E2000", {"points": [v(-109.96, -8.6) * mm, v(-109.9, -8.16) * mm, v(-109.84, -7.74) * mm, v(-109.78, -7.28) * mm]});
            skFitSpline(sketch, "E2001", {"points": [v(-109.78, -7.28) * mm, v(-109.89, -7.3) * mm, v(-109.96, -7.32) * mm, v(-110.04, -7.35) * mm]});
            skFitSpline(sketch, "E2002", {"points": [v(-110.04, -7.35) * mm, v(-110.37, -7.45) * mm, v(-110.69, -7.56) * mm, v(-111.02, -7.66) * mm]});
            skFitSpline(sketch, "E2003", {"points": [v(-111.02, -7.66) * mm, v(-111.15, -7.7) * mm, v(-111.3, -7.74) * mm, v(-111.44, -7.72) * mm]});
            skFitSpline(sketch, "E2004", {"points": [v(-111.44, -7.72) * mm, v(-111.78, -7.67) * mm, v(-112.07, -7.52) * mm, v(-112.26, -7.22) * mm]});
            skFitSpline(sketch, "E2005", {"points": [v(-112.26, -7.22) * mm, v(-112.33, -7.12) * mm, v(-112.36, -6.99) * mm, v(-112.39, -6.87) * mm]});
            skFitSpline(sketch, "E2006", {"points": [v(-112.39, -6.87) * mm, v(-112.47, -6.53) * mm, v(-112.53, -6.2) * mm, v(-112.6, -5.86) * mm]});
            skFitSpline(sketch, "E2007", {"points": [v(-112.6, -5.86) * mm, v(-112.63, -5.79) * mm, v(-112.65, -5.7) * mm, v(-112.69, -5.6) * mm]});
            skFitSpline(sketch, "E2008", {"points": [v(-112.69, -5.6) * mm, v(-113.05, -5.9) * mm, v(-113.38, -6.15) * mm, v(-113.72, -6.42) * mm]});
            skFitSpline(sketch, "E2009", {"points": [v(-114.92, -1.67) * mm, v(-115.12, -1.5) * mm, v(-115.3, -1.37) * mm, v(-115.45, -1.22) * mm]});
            skFitSpline(sketch, "E2010", {"points": [v(-115.45, -1.22) * mm, v(-115.68, -1) * mm, v(-115.9, -0.76) * mm, v(-116.13, -0.52) * mm]});
            skFitSpline(sketch, "E2011", {"points": [v(-116.13, -0.52) * mm, v(-116.33, -0.31) * mm, v(-116.2, -0.05) * mm, v(-116.24, 0.2) * mm]});
            skFitSpline(sketch, "E2012", {"points": [v(-116.24, 0.2) * mm, v(-116.26, 0.29) * mm, v(-116.2, 0.4) * mm, v(-116.14, 0.5) * mm]});
            skFitSpline(sketch, "E2013", {"points": [v(-116.14, 0.5) * mm, v(-116.07, 0.6) * mm, v(-115.98, 0.7) * mm, v(-115.9, 0.8) * mm]});
            skFitSpline(sketch, "E2014", {"points": [v(-115.9, 0.8) * mm, v(-115.65, 1.02) * mm, v(-115.4, 1.24) * mm, v(-115.15, 1.47) * mm]});
            skFitSpline(sketch, "E2015", {"points": [v(-115.15, 1.47) * mm, v(-115.08, 1.53) * mm, v(-115.02, 1.6) * mm, v(-114.95, 1.67) * mm]});
            skFitSpline(sketch, "E2016", {"points": [v(-114.95, 1.67) * mm, v(-115.38, 1.85) * mm, v(-115.78, 2) * mm, v(-116.17, 2.16) * mm]});
            skFitSpline(sketch, "E2017", {"points": [v(-116.17, 2.16) * mm, v(-116.77, 1.38) * mm, v(-117.46, 0.7) * mm, v(-118.15, 0) * mm]});
            skFitSpline(sketch, "E2018", {"points": [v(-118.15, 0) * mm, v(-117.46, -0.7) * mm, v(-116.77, -1.39) * mm, v(-116.17, -2.17) * mm]});
            skFitSpline(sketch, "E2019", {"points": [v(-116.17, -2.17) * mm, v(-115.77, -2.01) * mm, v(-115.37, -1.85) * mm, v(-114.92, -1.67) * mm]});
            skFitSpline(sketch, "E2020", {"points": [v(-94.4, 0) * mm, v(-95.3, 0.95) * mm, v(-96.2, 1.88) * mm, v(-97.1, 2.84) * mm]});
            skFitSpline(sketch, "E2021", {"points": [v(-97.1, 2.84) * mm, v(-97.35, 2.74) * mm, v(-97.62, 2.63) * mm, v(-97.9, 2.53) * mm]});
            skFitSpline(sketch, "E2022", {"points": [v(-97.9, 2.53) * mm, v(-97.85, 2.47) * mm, v(-97.83, 2.43) * mm, v(-97.8, 2.4) * mm]});
            skFitSpline(sketch, "E2023", {"points": [v(-97.8, 2.4) * mm, v(-97.55, 2.12) * mm, v(-97.31, 1.84) * mm, v(-97.05, 1.57) * mm]});
            skFitSpline(sketch, "E2024", {"points": [v(-97.05, 1.57) * mm, v(-96.7, 1.22) * mm, v(-96.35, 0.9) * mm, v(-96, 0.56) * mm]});
            skFitSpline(sketch, "E2025", {"points": [v(-96, 0.56) * mm, v(-95.88, 0.44) * mm, v(-95.8, 0.3) * mm, v(-95.81, 0.13) * mm]});
            skFitSpline(sketch, "E2026", {"points": [v(-95.81, 0.13) * mm, v(-95.82, 0.07) * mm, v(-95.83, 0) * mm, v(-95.82, -0.06) * mm]});
            skFitSpline(sketch, "E2027", {"points": [v(-95.82, -0.06) * mm, v(-95.78, -0.3) * mm, v(-95.87, -0.5) * mm, v(-96.09, -0.62) * mm]});
            skFitSpline(sketch, "E2028", {"points": [v(-96.09, -0.62) * mm, v(-96.13, -0.65) * mm, v(-96.16, -0.68) * mm, v(-96.2, -0.72) * mm]});
            skFitSpline(sketch, "E2029", {"points": [v(-96.2, -0.72) * mm, v(-96.72, -1.27) * mm, v(-97.25, -1.83) * mm, v(-97.78, -2.38) * mm]});
            skFitSpline(sketch, "E2030", {"points": [v(-97.78, -2.38) * mm, v(-97.82, -2.42) * mm, v(-97.84, -2.47) * mm, v(-97.9, -2.53) * mm]});
            skFitSpline(sketch, "E2031", {"points": [v(-97.9, -2.53) * mm, v(-97.6, -2.64) * mm, v(-97.35, -2.75) * mm, v(-97.1, -2.84) * mm]});
            skFitSpline(sketch, "E2032", {"points": [v(-97.1, -2.84) * mm, v(-96.2, -1.89) * mm, v(-95.3, -0.95) * mm, v(-94.4, 0) * mm]});
            skFitSpline(sketch, "E2033", {"points": [v(-115.18, 7.6) * mm, v(-114.98, 7.43) * mm, v(-114.75, 7.25) * mm, v(-114.49, 7.04) * mm]});
            skFitSpline(sketch, "E2034", {"points": [v(-114.49, 7.04) * mm, v(-114.28, 7.72) * mm, v(-114.1, 8.36) * mm, v(-113.9, 9) * mm]});
            skFitSpline(sketch, "E2035", {"points": [v(-113.9, 9) * mm, v(-113.85, 9.2) * mm, v(-113.8, 9.42) * mm, v(-113.76, 9.63) * mm]});
            skFitSpline(sketch, "E2036", {"points": [v(-113.76, 9.63) * mm, v(-113.73, 9.78) * mm, v(-113.7, 9.93) * mm, v(-113.56, 10) * mm]});
            skFitSpline(sketch, "E2037", {"points": [v(-113.56, 10) * mm, v(-113.36, 10.1) * mm, v(-113.18, 10.3) * mm, v(-112.92, 10.28) * mm]});
            skFitSpline(sketch, "E2038", {"points": [v(-112.92, 10.28) * mm, v(-112.86, 10.28) * mm, v(-112.8, 10.25) * mm, v(-112.74, 10.22) * mm]});
            skFitSpline(sketch, "E2039", {"points": [v(-112.74, 10.22) * mm, v(-112.63, 10.19) * mm, v(-112.52, 10.14) * mm, v(-112.4, 10.1) * mm]});
            skFitSpline(sketch, "E2040", {"points": [v(-112.4, 10.1) * mm, v(-111.84, 9.96) * mm, v(-111.27, 9.83) * mm, v(-110.7, 9.7) * mm]});
            skFitSpline(sketch, "E2041", {"points": [v(-110.7, 9.7) * mm, v(-110.52, 9.65) * mm, v(-110.34, 9.62) * mm, v(-110.13, 9.58) * mm]});
            skFitSpline(sketch, "E2042", {"points": [v(-110.13, 9.58) * mm, v(-110.18, 9.9) * mm, v(-110.22, 10.18) * mm, v(-110.26, 10.44) * mm]});
            skFitSpline(sketch, "E2043", {"points": [v(-110.26, 10.44) * mm, v(-111.55, 10.74) * mm, v(-112.8, 11.04) * mm, v(-114.07, 11.35) * mm]});
            skFitSpline(sketch, "E2044", {"points": [v(-114.07, 11.35) * mm, v(-114.26, 10.71) * mm, v(-114.43, 10.1) * mm, v(-114.61, 9.49) * mm]});
            skFitSpline(sketch, "E2045", {"points": [v(-114.61, 9.49) * mm, v(-114.8, 8.87) * mm, v(-114.99, 8.25) * mm, v(-115.18, 7.6) * mm]});
            skFitSpline(sketch, "E2046", {"points": [v(-120.62, 0) * mm, v(-119.71, -0.96) * mm, v(-118.82, -1.9) * mm, v(-117.93, -2.84) * mm]});
            skFitSpline(sketch, "E2047", {"points": [v(-117.93, -2.84) * mm, v(-117.67, -2.74) * mm, v(-117.4, -2.65) * mm, v(-117.12, -2.52) * mm]});
            skFitSpline(sketch, "E2048", {"points": [v(-117.12, -2.52) * mm, v(-117.33, -2.29) * mm, v(-117.51, -2.09) * mm, v(-117.7, -1.89) * mm]});
            skFitSpline(sketch, "E2049", {"points": [v(-117.7, -1.89) * mm, v(-118.13, -1.42) * mm, v(-118.56, -0.95) * mm, v(-119.05, -0.54) * mm]});
            skFitSpline(sketch, "E2050", {"points": [v(-119.05, -0.54) * mm, v(-119.18, -0.43) * mm, v(-119.24, -0.27) * mm, v(-119.2, -0.09) * mm]});
            skFitSpline(sketch, "E2051", {"points": [v(-119.2, -0.09) * mm, v(-119.2, -0.03) * mm, v(-119.2, 0.03) * mm, v(-119.2, 0.08) * mm]});
            skFitSpline(sketch, "E2052", {"points": [v(-119.2, 0.08) * mm, v(-119.25, 0.3) * mm, v(-119.15, 0.45) * mm, v(-119, 0.58) * mm]});
            skFitSpline(sketch, "E2053", {"points": [v(-119, 0.58) * mm, v(-118.9, 0.65) * mm, v(-118.8, 0.73) * mm, v(-118.72, 0.81) * mm]});
            skFitSpline(sketch, "E2054", {"points": [v(-118.72, 0.81) * mm, v(-118.3, 1.24) * mm, v(-117.9, 1.67) * mm, v(-117.48, 2.1) * mm]});
            skFitSpline(sketch, "E2055", {"points": [v(-117.48, 2.1) * mm, v(-117.36, 2.23) * mm, v(-117.25, 2.37) * mm, v(-117.12, 2.52) * mm]});
            skFitSpline(sketch, "E2056", {"points": [v(-117.12, 2.52) * mm, v(-117.42, 2.64) * mm, v(-117.69, 2.74) * mm, v(-117.93, 2.83) * mm]});
            skFitSpline(sketch, "E2057", {"points": [v(-117.93, 2.83) * mm, v(-118.84, 1.88) * mm, v(-119.72, 0.94) * mm, v(-120.62, 0) * mm]});
            skFitSpline(sketch, "E2058", {"points": [v(-104.9, 9.59) * mm, v(-104.83, 9.6) * mm, v(-104.8, 9.6) * mm, v(-104.76, 9.6) * mm]});
            skFitSpline(sketch, "E2059", {"points": [v(-104.76, 9.6) * mm, v(-103.9, 9.78) * mm, v(-103.05, 9.95) * mm, v(-102.22, 10.25) * mm]});
            skFitSpline(sketch, "E2060", {"points": [v(-102.22, 10.25) * mm, v(-101.93, 10.35) * mm, v(-101.36, 10.04) * mm, v(-101.29, 9.75) * mm]});
            skFitSpline(sketch, "E2061", {"points": [v(-101.29, 9.75) * mm, v(-101.24, 9.53) * mm, v(-101.2, 9.31) * mm, v(-101.14, 9.1) * mm]});
            skFitSpline(sketch, "E2062", {"points": [v(-101.14, 9.1) * mm, v(-100.96, 8.47) * mm, v(-100.77, 7.85) * mm, v(-100.58, 7.22) * mm]});
            skFitSpline(sketch, "E2063", {"points": [v(-100.58, 7.22) * mm, v(-100.56, 7.17) * mm, v(-100.53, 7.13) * mm, v(-100.5, 7.07) * mm]});
            skFitSpline(sketch, "E2064", {"points": [v(-100.5, 7.07) * mm, v(-100.27, 7.26) * mm, v(-100.05, 7.44) * mm, v(-99.85, 7.6) * mm]});
            skFitSpline(sketch, "E2065", {"points": [v(-99.85, 7.6) * mm, v(-100.22, 8.87) * mm, v(-100.6, 10.1) * mm, v(-100.96, 11.34) * mm]});
            skFitSpline(sketch, "E2066", {"points": [v(-100.96, 11.34) * mm, v(-102.24, 11.04) * mm, v(-103.48, 10.74) * mm, v(-104.76, 10.44) * mm]});
            skFitSpline(sketch, "E2067", {"points": [v(-104.76, 10.44) * mm, v(-104.8, 10.18) * mm, v(-104.85, 9.9) * mm, v(-104.9, 9.59) * mm]});
            skFitSpline(sketch, "E2068", {"points": [v(-99.85, -7.6) * mm, v(-100.06, -7.43) * mm, v(-100.28, -7.26) * mm, v(-100.5, -7.07) * mm]});
            skFitSpline(sketch, "E2069", {"points": [v(-100.5, -7.07) * mm, v(-100.54, -7.13) * mm, v(-100.56, -7.17) * mm, v(-100.58, -7.22) * mm]});
            skFitSpline(sketch, "E2070", {"points": [v(-100.58, -7.22) * mm, v(-100.69, -7.56) * mm, v(-100.81, -7.91) * mm, v(-100.91, -8.26) * mm]});
            skFitSpline(sketch, "E2071", {"points": [v(-100.91, -8.26) * mm, v(-101.05, -8.75) * mm, v(-101.17, -9.23) * mm, v(-101.28, -9.72) * mm]});
            skFitSpline(sketch, "E2072", {"points": [v(-101.28, -9.72) * mm, v(-101.35, -10.02) * mm, v(-101.9, -10.36) * mm, v(-102.19, -10.27) * mm]});
            skFitSpline(sketch, "E2073", {"points": [v(-102.19, -10.27) * mm, v(-102.22, -10.26) * mm, v(-102.26, -10.24) * mm, v(-102.3, -10.23) * mm]});
            skFitSpline(sketch, "E2074", {"points": [v(-102.3, -10.23) * mm, v(-102.4, -10.2) * mm, v(-102.5, -10.15) * mm, v(-102.6, -10.13) * mm]});
            skFitSpline(sketch, "E2075", {"points": [v(-102.6, -10.13) * mm, v(-103.18, -9.98) * mm, v(-103.77, -9.83) * mm, v(-104.36, -9.7) * mm]});
            skFitSpline(sketch, "E2076", {"points": [v(-104.36, -9.7) * mm, v(-104.52, -9.65) * mm, v(-104.7, -9.63) * mm, v(-104.89, -9.6) * mm]});
            skFitSpline(sketch, "E2077", {"points": [v(-104.89, -9.6) * mm, v(-104.87, -9.78) * mm, v(-104.85, -9.92) * mm, v(-104.83, -10.06) * mm]});
            skFitSpline(sketch, "E2078", {"points": [v(-104.83, -10.06) * mm, v(-104.8, -10.2) * mm, v(-104.78, -10.33) * mm, v(-104.76, -10.45) * mm]});
            skFitSpline(sketch, "E2079", {"points": [v(-104.76, -10.45) * mm, v(-103.48, -10.75) * mm, v(-102.22, -11.05) * mm, v(-100.96, -11.35) * mm]});
            skFitSpline(sketch, "E2080", {"points": [v(-100.96, -11.35) * mm, v(-100.59, -10.1) * mm, v(-100.22, -8.87) * mm, v(-99.85, -7.6) * mm]});
            skFitSpline(sketch, "E2081", {"points": [v(-110.13, -9.61) * mm, v(-110.2, -9.61) * mm, v(-110.22, -9.6) * mm, v(-110.25, -9.61) * mm]});
            skFitSpline(sketch, "E2082", {"points": [v(-110.25, -9.61) * mm, v(-110.5, -9.66) * mm, v(-110.74, -9.7) * mm, v(-110.98, -9.77) * mm]});
            skFitSpline(sketch, "E2083", {"points": [v(-110.98, -9.77) * mm, v(-111.6, -9.93) * mm, v(-112.21, -10.09) * mm, v(-112.82, -10.27) * mm]});
            skFitSpline(sketch, "E2084", {"points": [v(-112.82, -10.27) * mm, v(-113.12, -10.36) * mm, v(-113.3, -10.13) * mm, v(-113.52, -10.04) * mm]});
            skFitSpline(sketch, "E2085", {"points": [v(-113.52, -10.04) * mm, v(-113.66, -9.98) * mm, v(-113.73, -9.85) * mm, v(-113.75, -9.7) * mm]});
            skFitSpline(sketch, "E2086", {"points": [v(-113.75, -9.7) * mm, v(-113.75, -9.69) * mm, v(-113.75, -9.68) * mm, v(-113.75, -9.67) * mm]});
            skFitSpline(sketch, "E2087", {"points": [v(-113.75, -9.67) * mm, v(-113.78, -9.55) * mm, v(-113.8, -9.42) * mm, v(-113.83, -9.3) * mm]});
            skFitSpline(sketch, "E2088", {"points": [v(-113.83, -9.3) * mm, v(-113.98, -8.75) * mm, v(-114.14, -8.2) * mm, v(-114.3, -7.64) * mm]});
            skFitSpline(sketch, "E2089", {"points": [v(-114.3, -7.64) * mm, v(-114.36, -7.46) * mm, v(-114.43, -7.27) * mm, v(-114.5, -7.06) * mm]});
            skFitSpline(sketch, "E2090", {"points": [v(-114.5, -7.06) * mm, v(-114.75, -7.26) * mm, v(-114.97, -7.44) * mm, v(-115.18, -7.6) * mm]});
            skFitSpline(sketch, "E2091", {"points": [v(-115.18, -7.6) * mm, v(-114.8, -8.87) * mm, v(-114.44, -10.1) * mm, v(-114.06, -11.35) * mm]});
            skFitSpline(sketch, "E2092", {"points": [v(-114.06, -11.35) * mm, v(-112.79, -11.05) * mm, v(-111.53, -10.75) * mm, v(-110.26, -10.45) * mm]});
            skFitSpline(sketch, "E2093", {"points": [v(-110.26, -10.45) * mm, v(-110.22, -10.18) * mm, v(-110.18, -9.91) * mm, v(-110.13, -9.61) * mm]});
            skFitSpline(sketch, "E2094", {"points": [v(-111.9, -5.01) * mm, v(-111.67, -5.38) * mm, v(-111.64, -5.78) * mm, v(-111.56, -6.17) * mm]});
            skFitSpline(sketch, "E2095", {"points": [v(-111.56, -6.17) * mm, v(-111.52, -6.36) * mm, v(-111.46, -6.55) * mm, v(-111.4, -6.76) * mm]});
            skFitSpline(sketch, "E2096", {"points": [v(-111.4, -6.76) * mm, v(-111.1, -6.67) * mm, v(-110.81, -6.6) * mm, v(-110.54, -6.49) * mm]});
            skFitSpline(sketch, "E2097", {"points": [v(-110.54, -6.49) * mm, v(-110.26, -6.38) * mm, v(-109.97, -6.3) * mm, v(-109.65, -6.3) * mm]});
            skFitSpline(sketch, "E2098", {"points": [v(-109.65, -6.3) * mm, v(-109.4, -4.95) * mm, v(-109, -3.65) * mm, v(-108.84, -2.25) * mm]});
            skFitSpline(sketch, "E2099", {"points": [v(-108.84, -2.25) * mm, v(-109.87, -3.18) * mm, v(-110.88, -4.09) * mm, v(-111.9, -5.01) * mm]});
            skFitSpline(sketch, "E2100", {"points": [v(-106.17, -2.26) * mm, v(-106.18, -2.27) * mm, v(-106.2, -2.28) * mm, v(-106.2, -2.3) * mm]});
            skFitSpline(sketch, "E2101", {"points": [v(-106.2, -2.3) * mm, v(-106.08, -2.96) * mm, v(-105.96, -3.64) * mm, v(-105.82, -4.3) * mm]});
            skFitSpline(sketch, "E2102", {"points": [v(-105.82, -4.3) * mm, v(-105.68, -4.97) * mm, v(-105.5, -5.63) * mm, v(-105.35, -6.3) * mm]});
            skFitSpline(sketch, "E2103", {"points": [v(-105.35, -6.3) * mm, v(-104.95, -6.3) * mm, v(-104.59, -6.45) * mm, v(-104.22, -6.59) * mm]});
            skFitSpline(sketch, "E2104", {"points": [v(-104.22, -6.59) * mm, v(-104.03, -6.65) * mm, v(-103.83, -6.7) * mm, v(-103.63, -6.75) * mm]});
            skFitSpline(sketch, "E2105", {"points": [v(-103.63, -6.75) * mm, v(-103.57, -6.55) * mm, v(-103.49, -6.38) * mm, v(-103.46, -6.2) * mm]});
            skFitSpline(sketch, "E2106", {"points": [v(-103.46, -6.2) * mm, v(-103.4, -5.8) * mm, v(-103.35, -5.38) * mm, v(-103.13, -5) * mm]});
            skFitSpline(sketch, "E2107", {"points": [v(-103.13, -5) * mm, v(-104.15, -4.09) * mm, v(-105.16, -3.18) * mm, v(-106.17, -2.26) * mm]});
            skFitSpline(sketch, "E2108", {"points": [v(-115.3, 0) * mm, v(-115.16, -0.14) * mm, v(-115.06, -0.28) * mm, v(-114.92, -0.4) * mm]});
            skFitSpline(sketch, "E2109", {"points": [v(-114.92, -0.4) * mm, v(-114.6, -0.66) * mm, v(-114.26, -0.92) * mm, v(-114.03, -1.3) * mm]});
            skFitSpline(sketch, "E2110", {"points": [v(-114.03, -1.3) * mm, v(-112.72, -0.87) * mm, v(-111.41, -0.45) * mm, v(-110.11, -0.03) * mm]});
            skFitSpline(sketch, "E2111", {"points": [v(-110.11, -0.03) * mm, v(-110.11, -0.01) * mm, v(-110.12, 0) * mm, v(-110.12, 0.02) * mm]});
            skFitSpline(sketch, "E2112", {"points": [v(-110.12, 0.02) * mm, v(-111.42, 0.44) * mm, v(-112.72, 0.86) * mm, v(-114.01, 1.28) * mm]});
            skFitSpline(sketch, "E2113", {"points": [v(-114.01, 1.28) * mm, v(-114.16, 1.1) * mm, v(-114.29, 0.94) * mm, v(-114.43, 0.8) * mm]});
            skFitSpline(sketch, "E2114", {"points": [v(-114.43, 0.8) * mm, v(-114.58, 0.65) * mm, v(-114.76, 0.54) * mm, v(-114.9, 0.4) * mm]});
            skFitSpline(sketch, "E2115", {"points": [v(-114.9, 0.4) * mm, v(-115.04, 0.27) * mm, v(-115.16, 0.13) * mm, v(-115.3, 0) * mm]});
            skFitSpline(sketch, "E2116", {"points": [v(-100.98, 1.3) * mm, v(-102.3, 0.86) * mm, v(-103.6, 0.44) * mm, v(-104.9, 0.02) * mm]});
            skFitSpline(sketch, "E2117", {"points": [v(-104.9, 0.02) * mm, v(-104.9, 0) * mm, v(-104.9, -0.01) * mm, v(-104.9, -0.03) * mm]});
            skFitSpline(sketch, "E2118", {"points": [v(-104.9, -0.03) * mm, v(-103.6, -0.45) * mm, v(-102.3, -0.87) * mm, v(-100.99, -1.3) * mm]});
            skFitSpline(sketch, "E2119", {"points": [v(-100.99, -1.3) * mm, v(-100.77, -0.92) * mm, v(-100.44, -0.67) * mm, v(-100.12, -0.4) * mm]});
            skFitSpline(sketch, "E2120", {"points": [v(-100.12, -0.4) * mm, v(-99.98, -0.3) * mm, v(-99.87, -0.14) * mm, v(-99.74, -0.01) * mm]});
            skFitSpline(sketch, "E2121", {"points": [v(-99.74, -0.01) * mm, v(-100.1, 0.49) * mm, v(-100.7, 0.74) * mm, v(-100.98, 1.3) * mm]});
            skFitSpline(sketch, "E2122", {"points": [v(-105.37, 6.3) * mm, v(-105.41, 6.08) * mm, v(-105.45, 5.89) * mm, v(-105.49, 5.7) * mm]});
            skFitSpline(sketch, "E2123", {"points": [v(-105.49, 5.7) * mm, v(-105.61, 5.16) * mm, v(-105.74, 4.62) * mm, v(-105.86, 4.09) * mm]});
            skFitSpline(sketch, "E2124", {"points": [v(-105.86, 4.09) * mm, v(-105.96, 3.6) * mm, v(-106.05, 3.1) * mm, v(-106.14, 2.6) * mm]});
            skFitSpline(sketch, "E2125", {"points": [v(-106.14, 2.6) * mm, v(-106.16, 2.5) * mm, v(-106.19, 2.39) * mm, v(-106.2, 2.27) * mm]});
            skFitSpline(sketch, "E2126", {"points": [v(-106.2, 2.27) * mm, v(-106.2, 2.27) * mm, v(-106.19, 2.26) * mm, v(-106.18, 2.25) * mm]});
            skFitSpline(sketch, "E2127", {"points": [v(-106.18, 2.25) * mm, v(-105.16, 3.17) * mm, v(-104.15, 4.08) * mm, v(-103.13, 5) * mm]});
            skFitSpline(sketch, "E2128", {"points": [v(-103.13, 5) * mm, v(-103.35, 5.37) * mm, v(-103.4, 5.78) * mm, v(-103.46, 6.2) * mm]});
            skFitSpline(sketch, "E2129", {"points": [v(-103.46, 6.2) * mm, v(-103.49, 6.38) * mm, v(-103.57, 6.55) * mm, v(-103.63, 6.74) * mm]});
            skFitSpline(sketch, "E2130", {"points": [v(-103.63, 6.74) * mm, v(-103.84, 6.68) * mm, v(-104.03, 6.64) * mm, v(-104.22, 6.58) * mm]});
            skFitSpline(sketch, "E2131", {"points": [v(-104.22, 6.58) * mm, v(-104.59, 6.45) * mm, v(-104.94, 6.28) * mm, v(-105.37, 6.3) * mm]});
            skFitSpline(sketch, "E2132", {"points": [v(-109.66, 6.3) * mm, v(-110.08, 6.28) * mm, v(-110.45, 6.45) * mm, v(-110.82, 6.59) * mm]});
            skFitSpline(sketch, "E2133", {"points": [v(-110.82, 6.59) * mm, v(-111, 6.65) * mm, v(-111.2, 6.69) * mm, v(-111.4, 6.74) * mm]});
            skFitSpline(sketch, "E2134", {"points": [v(-111.4, 6.74) * mm, v(-111.46, 6.54) * mm, v(-111.53, 6.37) * mm, v(-111.56, 6.2) * mm]});
            skFitSpline(sketch, "E2135", {"points": [v(-111.56, 6.2) * mm, v(-111.63, 5.79) * mm, v(-111.67, 5.37) * mm, v(-111.89, 5.02) * mm]});
            skFitSpline(sketch, "E2136", {"points": [v(-111.89, 5.02) * mm, v(-111.37, 4.53) * mm, v(-110.87, 4.05) * mm, v(-110.35, 3.58) * mm]});
            skFitSpline(sketch, "E2137", {"points": [v(-110.35, 3.58) * mm, v(-109.93, 3.2) * mm, v(-109.49, 2.83) * mm, v(-109.05, 2.46) * mm]});
            skFitSpline(sketch, "E2138", {"points": [v(-109.05, 2.46) * mm, v(-108.98, 2.4) * mm, v(-108.92, 2.34) * mm, v(-108.85, 2.28) * mm]});
            skFitSpline(sketch, "E2139", {"points": [v(-108.85, 2.28) * mm, v(-108.83, 2.29) * mm, v(-108.82, 2.3) * mm, v(-108.8, 2.3) * mm]});
            skFitSpline(sketch, "E2140", {"points": [v(-108.8, 2.3) * mm, v(-109.09, 3.63) * mm, v(-109.37, 4.95) * mm, v(-109.66, 6.3) * mm]});
            skFitSpline(sketch, "E2141", {"points": [v(-100.97, -3.76) * mm, v(-101.12, -3.27) * mm, v(-101.27, -2.83) * mm, v(-101.4, -2.37) * mm]});
            skFitSpline(sketch, "E2142", {"points": [v(-101.4, -2.37) * mm, v(-101.44, -2.22) * mm, v(-101.52, -2.14) * mm, v(-101.67, -2.1) * mm]});
            skFitSpline(sketch, "E2143", {"points": [v(-101.67, -2.1) * mm, v(-102.19, -1.94) * mm, v(-102.7, -1.8) * mm, v(-103.2, -1.62) * mm]});
            skFitSpline(sketch, "E2144", {"points": [v(-103.2, -1.62) * mm, v(-103.77, -1.44) * mm, v(-104.32, -1.23) * mm, v(-104.88, -1.05) * mm]});
            skFitSpline(sketch, "E2145", {"points": [v(-104.88, -1.05) * mm, v(-105.32, -0.9) * mm, v(-105.76, -0.78) * mm, v(-106.2, -0.66) * mm]});
            skFitSpline(sketch, "E2146", {"points": [v(-106.2, -0.66) * mm, v(-106.26, -0.64) * mm, v(-106.32, -0.66) * mm, v(-106.4, -0.66) * mm]});
            skFitSpline(sketch, "E2147", {"points": [v(-106.4, -0.66) * mm, v(-106.37, -0.7) * mm, v(-106.35, -0.74) * mm, v(-106.33, -0.76) * mm]});
            skFitSpline(sketch, "E2148", {"points": [v(-106.33, -0.76) * mm, v(-105.88, -1.2) * mm, v(-105.44, -1.65) * mm, v(-104.96, -2.06) * mm]});
            skFitSpline(sketch, "E2149", {"points": [v(-104.96, -2.06) * mm, v(-104.48, -2.46) * mm, v(-104.01, -2.87) * mm, v(-103.57, -3.3) * mm]});
            skFitSpline(sketch, "E2150", {"points": [v(-103.57, -3.3) * mm, v(-103.3, -3.57) * mm, v(-103.01, -3.8) * mm, v(-102.74, -4.06) * mm]});
            skFitSpline(sketch, "E2151", {"points": [v(-102.74, -4.06) * mm, v(-102.65, -4.14) * mm, v(-102.57, -4.15) * mm, v(-102.46, -4.12) * mm]});
            skFitSpline(sketch, "E2152", {"points": [v(-102.46, -4.12) * mm, v(-102.2, -4.06) * mm, v(-101.96, -4.02) * mm, v(-101.7, -3.96) * mm]});
            skFitSpline(sketch, "E2153", {"points": [v(-101.7, -3.96) * mm, v(-101.48, -3.9) * mm, v(-101.25, -3.84) * mm, v(-100.97, -3.76) * mm]});
            skFitSpline(sketch, "E2154", {"points": [v(-106.4, 0.68) * mm, v(-106.4, 0.66) * mm, v(-106.38, 0.64) * mm, v(-106.37, 0.62) * mm]});
            skFitSpline(sketch, "E2155", {"points": [v(-106.37, 0.62) * mm, v(-106.32, 0.63) * mm, v(-106.27, 0.63) * mm, v(-106.21, 0.65) * mm]});
            skFitSpline(sketch, "E2156", {"points": [v(-106.21, 0.65) * mm, v(-105.77, 0.78) * mm, v(-105.32, 0.9) * mm, v(-104.88, 1.04) * mm]});
            skFitSpline(sketch, "E2157", {"points": [v(-104.88, 1.04) * mm, v(-104.53, 1.15) * mm, v(-104.18, 1.3) * mm, v(-103.83, 1.41) * mm]});
            skFitSpline(sketch, "E2158", {"points": [v(-103.83, 1.41) * mm, v(-103.2, 1.61) * mm, v(-102.58, 1.8) * mm, v(-101.95, 1.99) * mm]});
            skFitSpline(sketch, "E2159", {"points": [v(-101.95, 1.99) * mm, v(-101.8, 2.04) * mm, v(-101.6, 2.07) * mm, v(-101.5, 2.17) * mm]});
            skFitSpline(sketch, "E2160", {"points": [v(-101.5, 2.17) * mm, v(-101.39, 2.28) * mm, v(-101.36, 2.47) * mm, v(-101.31, 2.63) * mm]});
            skFitSpline(sketch, "E2161", {"points": [v(-101.31, 2.63) * mm, v(-101.2, 3) * mm, v(-101.1, 3.36) * mm, v(-100.99, 3.73) * mm]});
            skFitSpline(sketch, "E2162", {"points": [v(-100.99, 3.73) * mm, v(-101.09, 3.78) * mm, v(-101.16, 3.82) * mm, v(-101.23, 3.84) * mm]});
            skFitSpline(sketch, "E2163", {"points": [v(-101.23, 3.84) * mm, v(-101.67, 3.94) * mm, v(-102.1, 4.04) * mm, v(-102.54, 4.13) * mm]});
            skFitSpline(sketch, "E2164", {"points": [v(-102.54, 4.13) * mm, v(-102.58, 4.14) * mm, v(-102.63, 4.12) * mm, v(-102.67, 4.1) * mm]});
            skFitSpline(sketch, "E2165", {"points": [v(-102.67, 4.1) * mm, v(-102.73, 4.06) * mm, v(-102.78, 4.01) * mm, v(-102.84, 3.96) * mm]});
            skFitSpline(sketch, "E2166", {"points": [v(-102.84, 3.96) * mm, v(-103.29, 3.55) * mm, v(-103.73, 3.12) * mm, v(-104.19, 2.71) * mm]});
            skFitSpline(sketch, "E2167", {"points": [v(-104.19, 2.71) * mm, v(-104.55, 2.39) * mm, v(-104.93, 2.08) * mm, v(-105.3, 1.76) * mm]});
            skFitSpline(sketch, "E2168", {"points": [v(-105.3, 1.76) * mm, v(-105.49, 1.58) * mm, v(-105.68, 1.4) * mm, v(-105.87, 1.22) * mm]});
            skFitSpline(sketch, "E2169", {"points": [v(-105.87, 1.22) * mm, v(-106.05, 1.04) * mm, v(-106.22, 0.86) * mm, v(-106.4, 0.68) * mm]});
            skFitSpline(sketch, "E2170", {"points": [v(-108.6, 0.6) * mm, v(-108.66, 0.7) * mm, v(-108.68, 0.75) * mm, v(-108.72, 0.78) * mm]});
            skFitSpline(sketch, "E2171", {"points": [v(-108.72, 0.78) * mm, v(-109.05, 1.1) * mm, v(-109.39, 1.43) * mm, v(-109.72, 1.75) * mm]});
            skFitSpline(sketch, "E2172", {"points": [v(-109.72, 1.75) * mm, v(-109.85, 1.87) * mm, v(-109.98, 1.98) * mm, v(-110.12, 2.1) * mm]});
            skFitSpline(sketch, "E2173", {"points": [v(-110.12, 2.1) * mm, v(-110.53, 2.47) * mm, v(-110.95, 2.84) * mm, v(-111.37, 3.21) * mm]});
            skFitSpline(sketch, "E2174", {"points": [v(-111.37, 3.21) * mm, v(-111.68, 3.5) * mm, v(-112, 3.78) * mm, v(-112.3, 4.07) * mm]});
            skFitSpline(sketch, "E2175", {"points": [v(-112.3, 4.07) * mm, v(-112.37, 4.12) * mm, v(-112.43, 4.15) * mm, v(-112.52, 4.13) * mm]});
            skFitSpline(sketch, "E2176", {"points": [v(-112.52, 4.13) * mm, v(-112.8, 4.06) * mm, v(-113.09, 4.01) * mm, v(-113.36, 3.95) * mm]});
            skFitSpline(sketch, "E2177", {"points": [v(-113.36, 3.95) * mm, v(-113.58, 3.9) * mm, v(-113.8, 3.83) * mm, v(-114.02, 3.76) * mm]});
            skFitSpline(sketch, "E2178", {"points": [v(-114.02, 3.76) * mm, v(-114, 3.63) * mm, v(-113.99, 3.53) * mm, v(-113.96, 3.43) * mm]});
            skFitSpline(sketch, "E2179", {"points": [v(-113.96, 3.43) * mm, v(-113.85, 3.08) * mm, v(-113.72, 2.72) * mm, v(-113.62, 2.36) * mm]});
            skFitSpline(sketch, "E2180", {"points": [v(-113.62, 2.36) * mm, v(-113.58, 2.2) * mm, v(-113.5, 2.12) * mm, v(-113.35, 2.08) * mm]});
            skFitSpline(sketch, "E2181", {"points": [v(-113.35, 2.08) * mm, v(-112.84, 1.93) * mm, v(-112.33, 1.79) * mm, v(-111.83, 1.62) * mm]});
            skFitSpline(sketch, "E2182", {"points": [v(-111.83, 1.62) * mm, v(-111.27, 1.44) * mm, v(-110.72, 1.23) * mm, v(-110.16, 1.04) * mm]});
            skFitSpline(sketch, "E2183", {"points": [v(-110.16, 1.04) * mm, v(-109.86, 0.94) * mm, v(-109.55, 0.85) * mm, v(-109.25, 0.76) * mm]});
            skFitSpline(sketch, "E2184", {"points": [v(-109.25, 0.76) * mm, v(-109.05, 0.7) * mm, v(-108.85, 0.67) * mm, v(-108.6, 0.6) * mm]});
            skFitSpline(sketch, "E2185", {"points": [v(-108.66, 6.33) * mm, v(-108.64, 6.2) * mm, v(-108.62, 6.09) * mm, v(-108.6, 5.98) * mm]});
            skFitSpline(sketch, "E2186", {"points": [v(-108.6, 5.98) * mm, v(-108.48, 5.43) * mm, v(-108.34, 4.9) * mm, v(-108.23, 4.35) * mm]});
            skFitSpline(sketch, "E2187", {"points": [v(-108.23, 4.35) * mm, v(-108.15, 3.98) * mm, v(-108.1, 3.6) * mm, v(-108.02, 3.24) * mm]});
            skFitSpline(sketch, "E2188", {"points": [v(-108.02, 3.24) * mm, v(-107.93, 2.78) * mm, v(-107.82, 2.32) * mm, v(-107.71, 1.87) * mm]});
            skFitSpline(sketch, "E2189", {"points": [v(-107.71, 1.87) * mm, v(-107.68, 1.73) * mm, v(-107.64, 1.6) * mm, v(-107.6, 1.47) * mm]});
            skFitSpline(sketch, "E2190", {"points": [v(-107.6, 1.47) * mm, v(-107.58, 1.4) * mm, v(-107.55, 1.35) * mm, v(-107.51, 1.26) * mm]});
            skFitSpline(sketch, "E2191", {"points": [v(-107.51, 1.26) * mm, v(-107.48, 1.33) * mm, v(-107.45, 1.37) * mm, v(-107.44, 1.42) * mm]});
            skFitSpline(sketch, "E2192", {"points": [v(-107.44, 1.42) * mm, v(-107.32, 1.88) * mm, v(-107.2, 2.34) * mm, v(-107.1, 2.81) * mm]});
            skFitSpline(sketch, "E2193", {"points": [v(-107.1, 2.81) * mm, v(-106.97, 3.4) * mm, v(-106.87, 4) * mm, v(-106.75, 4.6) * mm]});
            skFitSpline(sketch, "E2194", {"points": [v(-106.75, 4.6) * mm, v(-106.64, 5.11) * mm, v(-106.51, 5.62) * mm, v(-106.4, 6.13) * mm]});
            skFitSpline(sketch, "E2195", {"points": [v(-106.4, 6.13) * mm, v(-106.36, 6.25) * mm, v(-106.37, 6.35) * mm, v(-106.47, 6.43) * mm]});
            skFitSpline(sketch, "E2196", {"points": [v(-106.47, 6.43) * mm, v(-106.56, 6.51) * mm, v(-106.63, 6.62) * mm, v(-106.7, 6.7) * mm]});
            skFitSpline(sketch, "E2197", {"points": [v(-106.7, 6.7) * mm, v(-106.96, 6.97) * mm, v(-107.22, 7.24) * mm, v(-107.49, 7.52) * mm]});
            skFitSpline(sketch, "E2198", {"points": [v(-107.49, 7.52) * mm, v(-107.57, 7.45) * mm, v(-107.63, 7.42) * mm, v(-107.68, 7.37) * mm]});
            skFitSpline(sketch, "E2199", {"points": [v(-107.68, 7.37) * mm, v(-108.01, 7.02) * mm, v(-108.34, 6.67) * mm, v(-108.66, 6.33) * mm]});
            skFitSpline(sketch, "E2200", {"points": [v(-107.48, -1.3) * mm, v(-107.5, -1.3) * mm, v(-107.52, -1.3) * mm, v(-107.54, -1.3) * mm]});
            skFitSpline(sketch, "E2201", {"points": [v(-107.54, -1.3) * mm, v(-107.58, -1.45) * mm, v(-107.63, -1.6) * mm, v(-107.67, -1.75) * mm]});
            skFitSpline(sketch, "E2202", {"points": [v(-107.67, -1.75) * mm, v(-107.8, -2.26) * mm, v(-107.95, -2.78) * mm, v(-108.03, -3.3) * mm]});
            skFitSpline(sketch, "E2203", {"points": [v(-108.03, -3.3) * mm, v(-108.12, -3.9) * mm, v(-108.26, -4.5) * mm, v(-108.4, -5.08) * mm]});
            skFitSpline(sketch, "E2204", {"points": [v(-108.4, -5.08) * mm, v(-108.5, -5.49) * mm, v(-108.58, -5.9) * mm, v(-108.67, -6.3) * mm]});
            skFitSpline(sketch, "E2205", {"points": [v(-108.67, -6.3) * mm, v(-108.29, -6.72) * mm, v(-107.95, -7.16) * mm, v(-107.5, -7.52) * mm]});
            skFitSpline(sketch, "E2206", {"points": [v(-107.5, -7.52) * mm, v(-107.41, -7.43) * mm, v(-107.32, -7.36) * mm, v(-107.24, -7.27) * mm]});
            skFitSpline(sketch, "E2207", {"points": [v(-107.24, -7.27) * mm, v(-106.98, -7) * mm, v(-106.74, -6.73) * mm, v(-106.5, -6.46) * mm]});
            skFitSpline(sketch, "E2208", {"points": [v(-106.5, -6.46) * mm, v(-106.4, -6.36) * mm, v(-106.36, -6.27) * mm, v(-106.4, -6.12) * mm]});
            skFitSpline(sketch, "E2209", {"points": [v(-106.4, -6.12) * mm, v(-106.52, -5.61) * mm, v(-106.65, -5.1) * mm, v(-106.75, -4.59) * mm]});
            skFitSpline(sketch, "E2210", {"points": [v(-106.75, -4.59) * mm, v(-106.87, -4) * mm, v(-106.97, -3.41) * mm, v(-107.1, -2.83) * mm]});
            skFitSpline(sketch, "E2211", {"points": [v(-107.1, -2.83) * mm, v(-107.16, -2.51) * mm, v(-107.24, -2.2) * mm, v(-107.32, -1.88) * mm]});
            skFitSpline(sketch, "E2212", {"points": [v(-107.32, -1.88) * mm, v(-107.36, -1.68) * mm, v(-107.42, -1.5) * mm, v(-107.48, -1.3) * mm]});
            skFitSpline(sketch, "E2213", {"points": [v(-108.62, -0.64) * mm, v(-108.71, -0.65) * mm, v(-108.78, -0.65) * mm, v(-108.83, -0.66) * mm]});
            skFitSpline(sketch, "E2214", {"points": [v(-108.83, -0.66) * mm, v(-109.29, -0.8) * mm, v(-109.74, -0.92) * mm, v(-110.19, -1.06) * mm]});
            skFitSpline(sketch, "E2215", {"points": [v(-110.19, -1.06) * mm, v(-110.53, -1.17) * mm, v(-110.86, -1.31) * mm, v(-111.2, -1.42) * mm]});
            skFitSpline(sketch, "E2216", {"points": [v(-111.2, -1.42) * mm, v(-111.63, -1.56) * mm, v(-112.07, -1.68) * mm, v(-112.5, -1.81) * mm]});
            skFitSpline(sketch, "E2217", {"points": [v(-112.5, -1.81) * mm, v(-112.8, -1.9) * mm, v(-113.1, -2.02) * mm, v(-113.41, -2.11) * mm]});
            skFitSpline(sketch, "E2218", {"points": [v(-113.41, -2.11) * mm, v(-113.51, -2.15) * mm, v(-113.57, -2.2) * mm, v(-113.6, -2.3) * mm]});
            skFitSpline(sketch, "E2219", {"points": [v(-113.6, -2.3) * mm, v(-113.68, -2.56) * mm, v(-113.77, -2.81) * mm, v(-113.85, -3.07) * mm]});
            skFitSpline(sketch, "E2220", {"points": [v(-113.85, -3.07) * mm, v(-113.92, -3.3) * mm, v(-113.97, -3.52) * mm, v(-114.03, -3.76) * mm]});
            skFitSpline(sketch, "E2221", {"points": [v(-114.03, -3.76) * mm, v(-113.9, -3.8) * mm, v(-113.78, -3.85) * mm, v(-113.67, -3.88) * mm]});
            skFitSpline(sketch, "E2222", {"points": [v(-113.67, -3.88) * mm, v(-113.31, -3.96) * mm, v(-112.95, -4.03) * mm, v(-112.6, -4.12) * mm]});
            skFitSpline(sketch, "E2223", {"points": [v(-112.6, -4.12) * mm, v(-112.45, -4.16) * mm, v(-112.36, -4.13) * mm, v(-112.26, -4.03) * mm]});
            skFitSpline(sketch, "E2224", {"points": [v(-112.26, -4.03) * mm, v(-111.91, -3.7) * mm, v(-111.57, -3.38) * mm, v(-111.22, -3.07) * mm]});
            skFitSpline(sketch, "E2225", {"points": [v(-111.22, -3.07) * mm, v(-110.84, -2.72) * mm, v(-110.43, -2.4) * mm, v(-110.05, -2.05) * mm]});
            skFitSpline(sketch, "E2226", {"points": [v(-110.05, -2.05) * mm, v(-109.6, -1.64) * mm, v(-109.17, -1.22) * mm, v(-108.73, -0.8) * mm]});
            skFitSpline(sketch, "E2227", {"points": [v(-108.73, -0.8) * mm, v(-108.69, -0.76) * mm, v(-108.67, -0.71) * mm, v(-108.62, -0.64) * mm]});
            skFitSpline(sketch, "E2228", {"points": [v(-107.5, -16.12) * mm, v(-107.67, -16.26) * mm, v(-107.82, -16.39) * mm, v(-107.98, -16.51) * mm]});
            skFitSpline(sketch, "E2229", {"points": [v(-107.98, -16.51) * mm, v(-108.44, -16.9) * mm, v(-108.9, -17.3) * mm, v(-109.36, -17.7) * mm]});
            skFitSpline(sketch, "E2230", {"points": [v(-109.36, -17.7) * mm, v(-109.48, -17.8) * mm, v(-109.61, -17.86) * mm, v(-109.78, -17.84) * mm]});
            skFitSpline(sketch, "E2231", {"points": [v(-109.78, -17.84) * mm, v(-109.98, -17.83) * mm, v(-110.12, -17.72) * mm, v(-110.19, -17.53) * mm]});
            skFitSpline(sketch, "E2232", {"points": [v(-110.19, -17.53) * mm, v(-110.26, -17.33) * mm, v(-110.22, -17.15) * mm, v(-110.06, -17) * mm]});
            skFitSpline(sketch, "E2233", {"points": [v(-110.06, -17) * mm, v(-109.9, -16.86) * mm, v(-109.73, -16.73) * mm, v(-109.56, -16.6) * mm]});
            skFitSpline(sketch, "E2234", {"points": [v(-109.56, -16.6) * mm, v(-109.17, -16.26) * mm, v(-108.77, -15.92) * mm, v(-108.38, -15.58) * mm]});
            skFitSpline(sketch, "E2235", {"points": [v(-108.38, -15.58) * mm, v(-108.36, -15.57) * mm, v(-108.35, -15.54) * mm, v(-108.33, -15.5) * mm]});
            skFitSpline(sketch, "E2236", {"points": [v(-108.33, -15.5) * mm, v(-108.5, -15.38) * mm, v(-108.68, -15.25) * mm, v(-108.84, -15.12) * mm]});
            skFitSpline(sketch, "E2237", {"points": [v(-108.84, -15.12) * mm, v(-109.23, -14.8) * mm, v(-109.62, -14.46) * mm, v(-110.02, -14.13) * mm]});
            skFitSpline(sketch, "E2238", {"points": [v(-110.02, -14.13) * mm, v(-110.05, -14.1) * mm, v(-110.1, -14.07) * mm, v(-110.12, -14.03) * mm]});
            skFitSpline(sketch, "E2239", {"points": [v(-110.12, -14.03) * mm, v(-110.2, -13.89) * mm, v(-110.32, -13.82) * mm, v(-110.5, -13.78) * mm]});
            skFitSpline(sketch, "E2240", {"points": [v(-110.5, -13.78) * mm, v(-110.73, -13.74) * mm, v(-110.86, -13.47) * mm, v(-110.8, -13.22) * mm]});
            skFitSpline(sketch, "E2241", {"points": [v(-110.8, -13.22) * mm, v(-110.72, -12.85) * mm, v(-110.63, -12.49) * mm, v(-110.55, -12.12) * mm]});
            skFitSpline(sketch, "E2242", {"points": [v(-110.55, -12.12) * mm, v(-110.51, -11.92) * mm, v(-110.48, -11.72) * mm, v(-110.44, -11.48) * mm]});
            skFitSpline(sketch, "E2243", {"points": [v(-110.44, -11.48) * mm, v(-111.58, -11.76) * mm, v(-112.69, -12.03) * mm, v(-113.8, -12.3) * mm]});
            skFitSpline(sketch, "E2244", {"points": [v(-113.8, -12.3) * mm, v(-113.8, -12.36) * mm, v(-113.8, -12.42) * mm, v(-113.78, -12.47) * mm]});
            skFitSpline(sketch, "E2245", {"points": [v(-113.78, -12.47) * mm, v(-113.54, -13.4) * mm, v(-113.3, -14.34) * mm, v(-113.05, -15.27) * mm]});
            skFitSpline(sketch, "E2246", {"points": [v(-113.05, -15.27) * mm, v(-113, -15.44) * mm, v(-112.95, -15.6) * mm, v(-112.9, -15.78) * mm]});
            skFitSpline(sketch, "E2247", {"points": [v(-112.9, -15.78) * mm, v(-112.82, -16.06) * mm, v(-112.93, -16.3) * mm, v(-113.2, -16.4) * mm]});
            skFitSpline(sketch, "E2248", {"points": [v(-113.2, -16.4) * mm, v(-113.42, -16.49) * mm, v(-113.69, -16.38) * mm, v(-113.8, -16.12) * mm]});
            skFitSpline(sketch, "E2249", {"points": [v(-113.8, -16.12) * mm, v(-113.88, -15.93) * mm, v(-113.94, -15.73) * mm, v(-114, -15.53) * mm]});
            skFitSpline(sketch, "E2250", {"points": [v(-114, -15.53) * mm, v(-114.14, -15) * mm, v(-114.27, -14.48) * mm, v(-114.4, -13.96) * mm]});
            skFitSpline(sketch, "E2251", {"points": [v(-114.4, -13.96) * mm, v(-114.5, -13.6) * mm, v(-114.58, -13.24) * mm, v(-114.67, -12.89) * mm]});
            skFitSpline(sketch, "E2252", {"points": [v(-114.67, -12.89) * mm, v(-114.7, -12.79) * mm, v(-114.73, -12.7) * mm, v(-114.77, -12.57) * mm]});
            skFitSpline(sketch, "E2253", {"points": [v(-114.77, -12.57) * mm, v(-115, -12.63) * mm, v(-115.2, -12.68) * mm, v(-115.4, -12.74) * mm]});
            skFitSpline(sketch, "E2254", {"points": [v(-115.4, -12.74) * mm, v(-116.05, -12.91) * mm, v(-116.68, -13.1) * mm, v(-117.32, -13.27) * mm]});
            skFitSpline(sketch, "E2255", {"points": [v(-117.32, -13.27) * mm, v(-117.6, -13.34) * mm, v(-117.88, -13.42) * mm, v(-118.15, -13.48) * mm]});
            skFitSpline(sketch, "E2256", {"points": [v(-118.15, -13.48) * mm, v(-118.25, -13.5) * mm, v(-118.35, -13.51) * mm, v(-118.44, -13.5) * mm]});
            skFitSpline(sketch, "E2257", {"points": [v(-118.44, -13.5) * mm, v(-118.66, -13.5) * mm, v(-118.82, -13.34) * mm, v(-118.87, -13.12) * mm]});
            skFitSpline(sketch, "E2258", {"points": [v(-118.87, -13.12) * mm, v(-118.91, -12.93) * mm, v(-118.82, -12.73) * mm, v(-118.65, -12.63) * mm]});
            skFitSpline(sketch, "E2259", {"points": [v(-118.65, -12.63) * mm, v(-118.6, -12.6) * mm, v(-118.54, -12.57) * mm, v(-118.48, -12.55) * mm]});
            skFitSpline(sketch, "E2260", {"points": [v(-118.48, -12.55) * mm, v(-117.5, -12.29) * mm, v(-116.5, -12.02) * mm, v(-115.52, -11.76) * mm]});
            skFitSpline(sketch, "E2261", {"points": [v(-115.52, -11.76) * mm, v(-115.36, -11.71) * mm, v(-115.2, -11.67) * mm, v(-115, -11.62) * mm]});
            skFitSpline(sketch, "E2262", {"points": [v(-115, -11.62) * mm, v(-115.33, -10.51) * mm, v(-115.66, -9.41) * mm, v(-116, -8.28) * mm]});
            skFitSpline(sketch, "E2263", {"points": [v(-116, -8.28) * mm, v(-116.16, -8.42) * mm, v(-116.32, -8.55) * mm, v(-116.46, -8.68) * mm]});
            skFitSpline(sketch, "E2264", {"points": [v(-116.46, -8.68) * mm, v(-116.74, -8.93) * mm, v(-117, -9.18) * mm, v(-117.27, -9.43) * mm]});
            skFitSpline(sketch, "E2265", {"points": [v(-117.27, -9.43) * mm, v(-117.44, -9.59) * mm, v(-117.63, -9.65) * mm, v(-117.84, -9.55) * mm]});
            skFitSpline(sketch, "E2266", {"points": [v(-117.84, -9.55) * mm, v(-117.95, -9.5) * mm, v(-118.03, -9.4) * mm, v(-118.14, -9.3) * mm]});
            skFitSpline(sketch, "E2267", {"points": [v(-118.14, -9.3) * mm, v(-118.51, -9.27) * mm, v(-118.88, -9.12) * mm, v(-119.24, -8.99) * mm]});
            skFitSpline(sketch, "E2268", {"points": [v(-119.24, -8.99) * mm, v(-119.65, -8.84) * mm, v(-120.04, -8.66) * mm, v(-120.44, -8.5) * mm]});
            skFitSpline(sketch, "E2269", {"points": [v(-120.44, -8.5) * mm, v(-120.47, -8.49) * mm, v(-120.5, -8.48) * mm, v(-120.55, -8.46) * mm]});
            skFitSpline(sketch, "E2270", {"points": [v(-120.55, -8.46) * mm, v(-120.59, -8.67) * mm, v(-120.64, -8.86) * mm, v(-120.67, -9.05) * mm]});
            skFitSpline(sketch, "E2271", {"points": [v(-120.67, -9.05) * mm, v(-120.77, -9.58) * mm, v(-120.86, -10.1) * mm, v(-120.95, -10.63) * mm]});
            skFitSpline(sketch, "E2272", {"points": [v(-120.95, -10.63) * mm, v(-121, -10.95) * mm, v(-121.21, -11.12) * mm, v(-121.5, -11.08) * mm]});
            skFitSpline(sketch, "E2273", {"points": [v(-121.5, -11.08) * mm, v(-121.79, -11.05) * mm, v(-121.97, -10.8) * mm, v(-121.91, -10.49) * mm]});
            skFitSpline(sketch, "E2274", {"points": [v(-121.91, -10.49) * mm, v(-121.84, -10.04) * mm, v(-121.75, -9.6) * mm, v(-121.67, -9.14) * mm]});
            skFitSpline(sketch, "E2275", {"points": [v(-121.67, -9.14) * mm, v(-121.6, -8.8) * mm, v(-121.54, -8.44) * mm, v(-121.47, -8.08) * mm]});
            skFitSpline(sketch, "E2276", {"points": [v(-121.47, -8.08) * mm, v(-121.55, -8.04) * mm, v(-121.61, -8.01) * mm, v(-121.68, -8) * mm]});
            skFitSpline(sketch, "E2277", {"points": [v(-121.68, -8) * mm, v(-122.36, -7.75) * mm, v(-123.04, -7.5) * mm, v(-123.73, -7.26) * mm]});
            skFitSpline(sketch, "E2278", {"points": [v(-123.73, -7.26) * mm, v(-124.02, -7.16) * mm, v(-124.14, -7) * mm, v(-124.13, -6.74) * mm]});
            skFitSpline(sketch, "E2279", {"points": [v(-124.13, -6.74) * mm, v(-124.12, -6.42) * mm, v(-123.83, -6.2) * mm, v(-123.52, -6.3) * mm]});
            skFitSpline(sketch, "E2280", {"points": [v(-123.52, -6.3) * mm, v(-123.3, -6.37) * mm, v(-123.1, -6.46) * mm, v(-122.9, -6.53) * mm]});
            skFitSpline(sketch, "E2281", {"points": [v(-122.9, -6.53) * mm, v(-122.39, -6.7) * mm, v(-121.88, -6.88) * mm, v(-121.35, -7.07) * mm]});
            skFitSpline(sketch, "E2282", {"points": [v(-121.35, -7.07) * mm, v(-121.3, -6.63) * mm, v(-121.23, -6.21) * mm, v(-121.17, -5.8) * mm]});
            skFitSpline(sketch, "E2283", {"points": [v(-121.17, -5.8) * mm, v(-121.11, -5.36) * mm, v(-121.03, -4.94) * mm, v(-120.87, -4.5) * mm]});
            skFitSpline(sketch, "E2284", {"points": [v(-120.87, -4.5) * mm, v(-120.88, -4.5) * mm, v(-120.9, -4.47) * mm, v(-120.9, -4.43) * mm]});
            skFitSpline(sketch, "E2285", {"points": [v(-120.9, -4.43) * mm, v(-121.02, -4.12) * mm, v(-120.9, -3.87) * mm, v(-120.6, -3.76) * mm]});
            skFitSpline(sketch, "E2286", {"points": [v(-120.6, -3.76) * mm, v(-120.3, -3.66) * mm, v(-119.99, -3.57) * mm, v(-119.68, -3.48) * mm]});
            skFitSpline(sketch, "E2287", {"points": [v(-119.68, -3.48) * mm, v(-119.44, -3.4) * mm, v(-119.2, -3.31) * mm, v(-118.93, -3.22) * mm]});
            skFitSpline(sketch, "E2288", {"points": [v(-118.93, -3.22) * mm, v(-119.7, -2.34) * mm, v(-120.53, -1.55) * mm, v(-121.3, -0.7) * mm]});
            skFitSpline(sketch, "E2289", {"points": [v(-121.3, -0.7) * mm, v(-121.65, -1.02) * mm, v(-122, -1.34) * mm, v(-122.32, -1.66) * mm]});
            skFitSpline(sketch, "E2290", {"points": [v(-122.32, -1.66) * mm, v(-122.7, -2.02) * mm, v(-123.06, -2.4) * mm, v(-123.42, -2.76) * mm]});
            skFitSpline(sketch, "E2291", {"points": [v(-123.42, -2.76) * mm, v(-123.57, -2.92) * mm, v(-123.72, -3.08) * mm, v(-123.87, -3.23) * mm]});
            skFitSpline(sketch, "E2292", {"points": [v(-123.87, -3.23) * mm, v(-124, -3.36) * mm, v(-124.14, -3.43) * mm, v(-124.32, -3.4) * mm]});
            skFitSpline(sketch, "E2293", {"points": [v(-124.32, -3.4) * mm, v(-124.68, -3.32) * mm, v(-124.83, -2.93) * mm, v(-124.62, -2.62) * mm]});
            skFitSpline(sketch, "E2294", {"points": [v(-124.62, -2.62) * mm, v(-124.5, -2.46) * mm, v(-124.36, -2.32) * mm, v(-124.22, -2.18) * mm]});
            skFitSpline(sketch, "E2295", {"points": [v(-124.22, -2.18) * mm, v(-123.55, -1.52) * mm, v(-122.88, -0.86) * mm, v(-122.2, -0.2) * mm]});
            skFitSpline(sketch, "E2296", {"points": [v(-122.2, -0.2) * mm, v(-122.15, -0.14) * mm, v(-122.1, -0.08) * mm, v(-122.02, 0) * mm]});
            skFitSpline(sketch, "E2297", {"points": [v(-122.02, 0) * mm, v(-122.16, 0.14) * mm, v(-122.3, 0.28) * mm, v(-122.44, 0.42) * mm]});
            skFitSpline(sketch, "E2298", {"points": [v(-122.44, 0.42) * mm, v(-122.96, 0.93) * mm, v(-123.48, 1.44) * mm, v(-124, 1.95) * mm]});
            skFitSpline(sketch, "E2299", {"points": [v(-124, 1.95) * mm, v(-124.18, 2.14) * mm, v(-124.37, 2.32) * mm, v(-124.55, 2.52) * mm]});
            skFitSpline(sketch, "E2300", {"points": [v(-124.55, 2.52) * mm, v(-124.66, 2.63) * mm, v(-124.71, 2.76) * mm, v(-124.7, 2.93) * mm]});
            skFitSpline(sketch, "E2301", {"points": [v(-124.7, 2.93) * mm, v(-124.7, 3.11) * mm, v(-124.62, 3.25) * mm, v(-124.46, 3.33) * mm]});
            skFitSpline(sketch, "E2302", {"points": [v(-124.46, 3.33) * mm, v(-124.3, 3.42) * mm, v(-124.14, 3.41) * mm, v(-123.98, 3.32) * mm]});
            skFitSpline(sketch, "E2303", {"points": [v(-123.98, 3.32) * mm, v(-123.92, 3.28) * mm, v(-123.87, 3.22) * mm, v(-123.82, 3.17) * mm]});
            skFitSpline(sketch, "E2304", {"points": [v(-123.82, 3.17) * mm, v(-123.11, 2.47) * mm, v(-122.4, 1.77) * mm, v(-121.7, 1.06) * mm]});
            skFitSpline(sketch, "E2305", {"points": [v(-121.7, 1.06) * mm, v(-121.57, 0.94) * mm, v(-121.46, 0.8) * mm, v(-121.33, 0.67) * mm]});
            skFitSpline(sketch, "E2306", {"points": [v(-121.33, 0.67) * mm, v(-120.52, 1.52) * mm, v(-119.73, 2.34) * mm, v(-118.92, 3.2) * mm]});
            skFitSpline(sketch, "E2307", {"points": [v(-118.92, 3.2) * mm, v(-119.1, 3.27) * mm, v(-119.25, 3.33) * mm, v(-119.4, 3.38) * mm]});
            skFitSpline(sketch, "E2308", {"points": [v(-119.4, 3.38) * mm, v(-119.76, 3.5) * mm, v(-120.1, 3.6) * mm, v(-120.46, 3.7) * mm]});
            skFitSpline(sketch, "E2309", {"points": [v(-120.46, 3.7) * mm, v(-120.51, 3.73) * mm, v(-120.57, 3.74) * mm, v(-120.62, 3.76) * mm]});
            skFitSpline(sketch, "E2310", {"points": [v(-120.62, 3.76) * mm, v(-120.9, 3.86) * mm, v(-121.06, 4.2) * mm, v(-120.87, 4.5) * mm]});
            skFitSpline(sketch, "E2311", {"points": [v(-120.87, 4.5) * mm, v(-121.17, 5.32) * mm, v(-121.22, 6.19) * mm, v(-121.35, 7.05) * mm]});
            skFitSpline(sketch, "E2312", {"points": [v(-121.35, 7.05) * mm, v(-121.58, 6.98) * mm, v(-121.8, 6.9) * mm, v(-122.01, 6.83) * mm]});
            skFitSpline(sketch, "E2313", {"points": [v(-122.01, 6.83) * mm, v(-122.5, 6.65) * mm, v(-123, 6.47) * mm, v(-123.5, 6.3) * mm]});
            skFitSpline(sketch, "E2314", {"points": [v(-123.5, 6.3) * mm, v(-123.58, 6.27) * mm, v(-123.69, 6.26) * mm, v(-123.78, 6.28) * mm]});
            skFitSpline(sketch, "E2315", {"points": [v(-123.78, 6.28) * mm, v(-123.99, 6.33) * mm, v(-124.12, 6.5) * mm, v(-124.13, 6.7) * mm]});
            skFitSpline(sketch, "E2316", {"points": [v(-124.13, 6.7) * mm, v(-124.15, 6.95) * mm, v(-124.05, 7.12) * mm, v(-123.81, 7.22) * mm]});
            skFitSpline(sketch, "E2317", {"points": [v(-123.81, 7.22) * mm, v(-123.56, 7.32) * mm, v(-123.3, 7.41) * mm, v(-123.03, 7.5) * mm]});
            skFitSpline(sketch, "E2318", {"points": [v(-123.03, 7.5) * mm, v(-122.58, 7.67) * mm, v(-122.13, 7.82) * mm, v(-121.67, 7.98) * mm]});
            skFitSpline(sketch, "E2319", {"points": [v(-121.67, 7.98) * mm, v(-121.62, 8) * mm, v(-121.56, 8.03) * mm, v(-121.48, 8.05) * mm]});
            skFitSpline(sketch, "E2320", {"points": [v(-121.48, 8.05) * mm, v(-121.5, 8.2) * mm, v(-121.52, 8.36) * mm, v(-121.55, 8.5) * mm]});
            skFitSpline(sketch, "E2321", {"points": [v(-121.55, 8.5) * mm, v(-121.66, 9.13) * mm, v(-121.78, 9.76) * mm, v(-121.9, 10.38) * mm]});
            skFitSpline(sketch, "E2322", {"points": [v(-121.9, 10.38) * mm, v(-121.91, 10.45) * mm, v(-121.92, 10.51) * mm, v(-121.92, 10.57) * mm]});
            skFitSpline(sketch, "E2323", {"points": [v(-121.92, 10.57) * mm, v(-121.93, 10.84) * mm, v(-121.75, 11.05) * mm, v(-121.5, 11.07) * mm]});
            skFitSpline(sketch, "E2324", {"points": [v(-121.5, 11.07) * mm, v(-121.21, 11.1) * mm, v(-121, 10.95) * mm, v(-120.95, 10.66) * mm]});
            skFitSpline(sketch, "E2325", {"points": [v(-120.95, 10.66) * mm, v(-120.83, 9.96) * mm, v(-120.7, 9.25) * mm, v(-120.57, 8.55) * mm]});
            skFitSpline(sketch, "E2326", {"points": [v(-120.57, 8.55) * mm, v(-120.57, 8.52) * mm, v(-120.56, 8.5) * mm, v(-120.55, 8.46) * mm]});
            skFitSpline(sketch, "E2327", {"points": [v(-120.55, 8.46) * mm, v(-120.49, 8.48) * mm, v(-120.43, 8.5) * mm, v(-120.37, 8.52) * mm]});
            skFitSpline(sketch, "E2328", {"points": [v(-120.37, 8.52) * mm, v(-119.77, 8.77) * mm, v(-119.18, 9.03) * mm, v(-118.56, 9.2) * mm]});
            skFitSpline(sketch, "E2329", {"points": [v(-118.56, 9.2) * mm, v(-118.41, 9.24) * mm, v(-118.26, 9.27) * mm, v(-118.1, 9.31) * mm]});
            skFitSpline(sketch, "E2330", {"points": [v(-118.1, 9.31) * mm, v(-118.08, 9.34) * mm, v(-118.05, 9.38) * mm, v(-118.01, 9.42) * mm]});
            skFitSpline(sketch, "E2331", {"points": [v(-118.01, 9.42) * mm, v(-117.82, 9.64) * mm, v(-117.52, 9.65) * mm, v(-117.29, 9.43) * mm]});
            skFitSpline(sketch, "E2332", {"points": [v(-117.29, 9.43) * mm, v(-117, 9.18) * mm, v(-116.74, 8.92) * mm, v(-116.46, 8.67) * mm]});
            skFitSpline(sketch, "E2333", {"points": [v(-116.46, 8.67) * mm, v(-116.32, 8.54) * mm, v(-116.17, 8.42) * mm, v(-116, 8.27) * mm]});
            skFitSpline(sketch, "E2334", {"points": [v(-116, 8.27) * mm, v(-115.66, 9.4) * mm, v(-115.33, 10.5) * mm, v(-115, 11.6) * mm]});
            skFitSpline(sketch, "E2335", {"points": [v(-115, 11.6) * mm, v(-115.43, 11.73) * mm, v(-115.84, 11.85) * mm, v(-116.26, 11.97) * mm]});
            skFitSpline(sketch, "E2336", {"points": [v(-116.26, 11.97) * mm, v(-116.84, 12.13) * mm, v(-117.43, 12.29) * mm, v(-118.01, 12.44) * mm]});
            skFitSpline(sketch, "E2337", {"points": [v(-118.01, 12.44) * mm, v(-118.17, 12.48) * mm, v(-118.33, 12.5) * mm, v(-118.48, 12.55) * mm]});
            skFitSpline(sketch, "E2338", {"points": [v(-118.48, 12.55) * mm, v(-118.74, 12.61) * mm, v(-118.9, 12.83) * mm, v(-118.88, 13.07) * mm]});
            skFitSpline(sketch, "E2339", {"points": [v(-118.88, 13.07) * mm, v(-118.85, 13.33) * mm, v(-118.64, 13.51) * mm, v(-118.36, 13.5) * mm]});
            skFitSpline(sketch, "E2340", {"points": [v(-118.36, 13.5) * mm, v(-118.17, 13.48) * mm, v(-117.97, 13.44) * mm, v(-117.78, 13.39) * mm]});
            skFitSpline(sketch, "E2341", {"points": [v(-117.78, 13.39) * mm, v(-117.2, 13.23) * mm, v(-116.6, 13.08) * mm, v(-116.02, 12.92) * mm]});
            skFitSpline(sketch, "E2342", {"points": [v(-116.02, 12.92) * mm, v(-115.7, 12.83) * mm, v(-115.38, 12.73) * mm, v(-115.06, 12.63) * mm]});
            skFitSpline(sketch, "E2343", {"points": [v(-115.06, 12.63) * mm, v(-114.97, 12.6) * mm, v(-114.89, 12.6) * mm, v(-114.8, 12.57) * mm]});
            skFitSpline(sketch, "E2344", {"points": [v(-114.8, 12.57) * mm, v(-114.69, 12.72) * mm, v(-114.67, 12.89) * mm, v(-114.63, 13.04) * mm]});
            skFitSpline(sketch, "E2345", {"points": [v(-114.63, 13.04) * mm, v(-114.44, 13.77) * mm, v(-114.25, 14.5) * mm, v(-114.06, 15.22) * mm]});
            skFitSpline(sketch, "E2346", {"points": [v(-114.06, 15.22) * mm, v(-114, 15.48) * mm, v(-113.93, 15.73) * mm, v(-113.85, 15.98) * mm]});
            skFitSpline(sketch, "E2347", {"points": [v(-113.85, 15.98) * mm, v(-113.82, 16.08) * mm, v(-113.76, 16.19) * mm, v(-113.7, 16.27) * mm]});
            skFitSpline(sketch, "E2348", {"points": [v(-113.7, 16.27) * mm, v(-113.54, 16.44) * mm, v(-113.32, 16.46) * mm, v(-113.12, 16.36) * mm]});
            skFitSpline(sketch, "E2349", {"points": [v(-113.12, 16.36) * mm, v(-112.92, 16.25) * mm, v(-112.83, 16.04) * mm, v(-112.89, 15.81) * mm]});
            skFitSpline(sketch, "E2350", {"points": [v(-112.89, 15.81) * mm, v(-113.09, 15.08) * mm, v(-113.3, 14.35) * mm, v(-113.49, 13.62) * mm]});
            skFitSpline(sketch, "E2351", {"points": [v(-113.49, 13.62) * mm, v(-113.6, 13.19) * mm, v(-113.7, 12.76) * mm, v(-113.82, 12.3) * mm]});
            skFitSpline(sketch, "E2352", {"points": [v(-113.82, 12.3) * mm, v(-112.7, 12.02) * mm, v(-111.59, 11.75) * mm, v(-110.43, 11.47) * mm]});
            skFitSpline(sketch, "E2353", {"points": [v(-110.43, 11.47) * mm, v(-110.5, 11.8) * mm, v(-110.55, 12.1) * mm, v(-110.62, 12.4) * mm]});
            skFitSpline(sketch, "E2354", {"points": [v(-110.62, 12.4) * mm, v(-110.67, 12.64) * mm, v(-110.73, 12.9) * mm, v(-110.79, 13.14) * mm]});
            skFitSpline(sketch, "E2355", {"points": [v(-110.79, 13.14) * mm, v(-110.88, 13.52) * mm, v(-110.72, 13.76) * mm, v(-110.33, 13.81) * mm]});
            skFitSpline(sketch, "E2356", {"points": [v(-110.33, 13.81) * mm, v(-110.31, 13.81) * mm, v(-110.3, 13.82) * mm, v(-110.29, 13.82) * mm]});
            skFitSpline(sketch, "E2357", {"points": [v(-110.29, 13.82) * mm, v(-109.73, 14.49) * mm, v(-109, 14.96) * mm, v(-108.32, 15.51) * mm]});
            skFitSpline(sketch, "E2358", {"points": [v(-108.32, 15.51) * mm, v(-108.48, 15.66) * mm, v(-108.62, 15.8) * mm, v(-108.77, 15.92) * mm]});
            skFitSpline(sketch, "E2359", {"points": [v(-108.77, 15.92) * mm, v(-109.18, 16.27) * mm, v(-109.59, 16.62) * mm, v(-110, 16.95) * mm]});
            skFitSpline(sketch, "E2360", {"points": [v(-110, 16.95) * mm, v(-110.26, 17.14) * mm, v(-110.26, 17.49) * mm, v(-110.1, 17.67) * mm]});
            skFitSpline(sketch, "E2361", {"points": [v(-110.1, 17.67) * mm, v(-109.92, 17.88) * mm, v(-109.62, 17.9) * mm, v(-109.38, 17.7) * mm]});
            skFitSpline(sketch, "E2362", {"points": [v(-109.38, 17.7) * mm, v(-108.82, 17.23) * mm, v(-108.27, 16.76) * mm, v(-107.72, 16.29) * mm]});
            skFitSpline(sketch, "E2363", {"points": [v(-107.72, 16.29) * mm, v(-107.66, 16.24) * mm, v(-107.6, 16.19) * mm, v(-107.52, 16.13) * mm]});
            skFitSpline(sketch, "E2364", {"points": [v(-107.52, 16.13) * mm, v(-107.46, 16.17) * mm, v(-107.4, 16.22) * mm, v(-107.33, 16.27) * mm]});
            skFitSpline(sketch, "E2365", {"points": [v(-107.33, 16.27) * mm, v(-106.78, 16.74) * mm, v(-106.22, 17.2) * mm, v(-105.68, 17.68) * mm]});
            skFitSpline(sketch, "E2366", {"points": [v(-105.68, 17.68) * mm, v(-105.38, 17.95) * mm, v(-104.9, 17.85) * mm, v(-104.82, 17.46) * mm]});
            skFitSpline(sketch, "E2367", {"points": [v(-104.82, 17.46) * mm, v(-104.77, 17.27) * mm, v(-104.83, 17.11) * mm, v(-104.97, 16.99) * mm]});
            skFitSpline(sketch, "E2368", {"points": [v(-104.97, 16.99) * mm, v(-105.37, 16.65) * mm, v(-105.77, 16.32) * mm, v(-106.16, 15.99) * mm]});
            skFitSpline(sketch, "E2369", {"points": [v(-106.16, 15.99) * mm, v(-106.34, 15.84) * mm, v(-106.51, 15.68) * mm, v(-106.7, 15.52) * mm]});
            skFitSpline(sketch, "E2370", {"points": [v(-106.7, 15.52) * mm, v(-106.65, 15.47) * mm, v(-106.6, 15.43) * mm, v(-106.56, 15.4) * mm]});
            skFitSpline(sketch, "E2371", {"points": [v(-106.56, 15.4) * mm, v(-106.02, 15) * mm, v(-105.49, 14.59) * mm, v(-105, 14.12) * mm]});
            skFitSpline(sketch, "E2372", {"points": [v(-105, 14.12) * mm, v(-104.91, 14.03) * mm, v(-104.83, 13.93) * mm, v(-104.74, 13.82) * mm]});
            skFitSpline(sketch, "E2373", {"points": [v(-104.74, 13.82) * mm, v(-104.72, 13.82) * mm, v(-104.68, 13.81) * mm, v(-104.64, 13.8) * mm]});
            skFitSpline(sketch, "E2374", {"points": [v(-104.64, 13.8) * mm, v(-104.33, 13.75) * mm, v(-104.17, 13.53) * mm, v(-104.22, 13.22) * mm]});
            skFitSpline(sketch, "E2375", {"points": [v(-104.22, 13.22) * mm, v(-104.26, 12.98) * mm, v(-104.33, 12.74) * mm, v(-104.39, 12.5) * mm]});
            skFitSpline(sketch, "E2376", {"points": [v(-104.39, 12.5) * mm, v(-104.45, 12.17) * mm, v(-104.52, 11.85) * mm, v(-104.6, 11.47) * mm]});
            skFitSpline(sketch, "E2377", {"points": [v(-104.6, 11.47) * mm, v(-103.44, 11.75) * mm, v(-102.33, 12.02) * mm, v(-101.21, 12.29) * mm]});
            skFitSpline(sketch, "E2378", {"points": [v(-101.21, 12.29) * mm, v(-101.3, 12.7) * mm, v(-101.39, 13.08) * mm, v(-101.5, 13.47) * mm]});
            skFitSpline(sketch, "E2379", {"points": [v(-101.5, 13.47) * mm, v(-101.7, 14.23) * mm, v(-101.91, 14.99) * mm, v(-102.12, 15.75) * mm]});
            skFitSpline(sketch, "E2380", {"points": [v(-102.12, 15.75) * mm, v(-102.15, 15.86) * mm, v(-102.16, 15.98) * mm, v(-102.13, 16.08) * mm]});
            skFitSpline(sketch, "E2381", {"points": [v(-102.13, 16.08) * mm, v(-102.08, 16.29) * mm, v(-101.91, 16.4) * mm, v(-101.71, 16.42) * mm]});
            skFitSpline(sketch, "E2382", {"points": [v(-101.71, 16.42) * mm, v(-101.53, 16.45) * mm, v(-101.32, 16.32) * mm, v(-101.23, 16.13) * mm]});
            skFitSpline(sketch, "E2383", {"points": [v(-101.23, 16.13) * mm, v(-101.16, 15.97) * mm, v(-101.1, 15.8) * mm, v(-101.06, 15.63) * mm]});
            skFitSpline(sketch, "E2384", {"points": [v(-101.06, 15.63) * mm, v(-100.88, 14.98) * mm, v(-100.71, 14.33) * mm, v(-100.54, 13.69) * mm]});
            skFitSpline(sketch, "E2385", {"points": [v(-100.54, 13.69) * mm, v(-100.48, 13.45) * mm, v(-100.43, 13.2) * mm, v(-100.37, 12.96) * mm]});
            skFitSpline(sketch, "E2386", {"points": [v(-100.37, 12.96) * mm, v(-100.34, 12.84) * mm, v(-100.3, 12.72) * mm, v(-100.26, 12.57) * mm]});
            skFitSpline(sketch, "E2387", {"points": [v(-100.26, 12.57) * mm, v(-100.06, 12.61) * mm, v(-99.88, 12.65) * mm, v(-99.7, 12.7) * mm]});
            skFitSpline(sketch, "E2388", {"points": [v(-99.7, 12.7) * mm, v(-98.84, 12.94) * mm, v(-97.98, 13.18) * mm, v(-97.12, 13.42) * mm]});
            skFitSpline(sketch, "E2389", {"points": [v(-97.12, 13.42) * mm, v(-96.96, 13.46) * mm, v(-96.79, 13.5) * mm, v(-96.62, 13.5) * mm]});
            skFitSpline(sketch, "E2390", {"points": [v(-96.62, 13.5) * mm, v(-96.37, 13.5) * mm, v(-96.18, 13.32) * mm, v(-96.15, 13.08) * mm]});
            skFitSpline(sketch, "E2391", {"points": [v(-96.15, 13.08) * mm, v(-96.12, 12.83) * mm, v(-96.27, 12.62) * mm, v(-96.51, 12.55) * mm]});
            skFitSpline(sketch, "E2392", {"points": [v(-96.51, 12.55) * mm, v(-97.2, 12.37) * mm, v(-97.89, 12.2) * mm, v(-98.57, 12.01) * mm]});
            skFitSpline(sketch, "E2393", {"points": [v(-98.57, 12.01) * mm, v(-99.04, 11.89) * mm, v(-99.5, 11.75) * mm, v(-100, 11.61) * mm]});
            skFitSpline(sketch, "E2394", {"points": [v(-100, 11.61) * mm, v(-99.96, 11.23) * mm, v(-99.78, 10.89) * mm, v(-99.7, 10.52) * mm]});
            skFitSpline(sketch, "E2395", {"points": [v(-99.7, 10.52) * mm, v(-99.6, 10.15) * mm, v(-99.48, 9.78) * mm, v(-99.38, 9.41) * mm]});
            skFitSpline(sketch, "E2396", {"points": [v(-99.38, 9.41) * mm, v(-99.27, 9.05) * mm, v(-99.15, 8.68) * mm, v(-99.03, 8.28) * mm]});
            skFitSpline(sketch, "E2397", {"points": [v(-99.03, 8.28) * mm, v(-98.87, 8.41) * mm, v(-98.72, 8.53) * mm, v(-98.58, 8.65) * mm]});
            skFitSpline(sketch, "E2398", {"points": [v(-98.58, 8.65) * mm, v(-98.3, 8.9) * mm, v(-98.03, 9.16) * mm, v(-97.76, 9.42) * mm]});
            skFitSpline(sketch, "E2399", {"points": [v(-97.76, 9.42) * mm, v(-97.58, 9.58) * mm, v(-97.38, 9.64) * mm, v(-97.16, 9.53) * mm]});
            skFitSpline(sketch, "E2400", {"points": [v(-97.16, 9.53) * mm, v(-97.06, 9.48) * mm, v(-96.99, 9.38) * mm, v(-96.89, 9.3) * mm]});
            skFitSpline(sketch, "E2401", {"points": [v(-96.89, 9.3) * mm, v(-96.5, 9.26) * mm, v(-96.13, 9.1) * mm, v(-95.76, 8.97) * mm]});
            skFitSpline(sketch, "E2402", {"points": [v(-95.76, 8.97) * mm, v(-95.34, 8.81) * mm, v(-94.92, 8.63) * mm, v(-94.48, 8.45) * mm]});
            skFitSpline(sketch, "E2403", {"points": [v(-94.48, 8.45) * mm, v(-94.43, 8.67) * mm, v(-94.38, 8.87) * mm, v(-94.35, 9.07) * mm]});
            skFitSpline(sketch, "E2404", {"points": [v(-94.35, 9.07) * mm, v(-94.26, 9.59) * mm, v(-94.17, 10.1) * mm, v(-94.08, 10.62) * mm]});
            skFitSpline(sketch, "E2405", {"points": [v(-94.08, 10.62) * mm, v(-94.03, 10.96) * mm, v(-93.8, 11.12) * mm, v(-93.5, 11.07) * mm]});
            skFitSpline(sketch, "E2406", {"points": [v(-93.5, 11.07) * mm, v(-93.22, 11.02) * mm, v(-93.07, 10.78) * mm, v(-93.12, 10.47) * mm]});
            skFitSpline(sketch, "E2407", {"points": [v(-93.12, 10.47) * mm, v(-93.26, 9.7) * mm, v(-93.4, 8.92) * mm, v(-93.54, 8.14) * mm]});
            skFitSpline(sketch, "E2408", {"points": [v(-93.54, 8.14) * mm, v(-93.54, 8.12) * mm, v(-93.54, 8.1) * mm, v(-93.54, 8.06) * mm]});
            skFitSpline(sketch, "E2409", {"points": [v(-93.54, 8.06) * mm, v(-93.37, 8) * mm, v(-93.19, 7.92) * mm, v(-93.01, 7.86) * mm]});
            skFitSpline(sketch, "E2410", {"points": [v(-93.01, 7.86) * mm, v(-92.43, 7.65) * mm, v(-91.85, 7.45) * mm, v(-91.27, 7.25) * mm]});
            skFitSpline(sketch, "E2411", {"points": [v(-91.27, 7.25) * mm, v(-91.07, 7.17) * mm, v(-90.92, 7.05) * mm, v(-90.89, 6.83) * mm]});
            skFitSpline(sketch, "E2412", {"points": [v(-90.89, 6.83) * mm, v(-90.83, 6.46) * mm, v(-91.17, 6.17) * mm, v(-91.53, 6.3) * mm]});
            skFitSpline(sketch, "E2413", {"points": [v(-91.53, 6.3) * mm, v(-91.82, 6.4) * mm, v(-92.1, 6.52) * mm, v(-92.4, 6.62) * mm]});
            skFitSpline(sketch, "E2414", {"points": [v(-92.4, 6.62) * mm, v(-92.78, 6.76) * mm, v(-93.17, 6.89) * mm, v(-93.55, 7.02) * mm]});
            skFitSpline(sketch, "E2415", {"points": [v(-93.55, 7.02) * mm, v(-93.6, 7.03) * mm, v(-93.63, 7.04) * mm, v(-93.68, 7.05) * mm]});
            skFitSpline(sketch, "E2416", {"points": [v(-93.68, 7.05) * mm, v(-93.8, 6.2) * mm, v(-93.86, 5.35) * mm, v(-94.15, 4.5) * mm]});
            skFitSpline(sketch, "E2417", {"points": [v(-94.15, 4.5) * mm, v(-94.15, 4.5) * mm, v(-94.13, 4.46) * mm, v(-94.12, 4.43) * mm]});
            skFitSpline(sketch, "E2418", {"points": [v(-94.12, 4.43) * mm, v(-94, 4.1) * mm, v(-94.12, 3.85) * mm, v(-94.45, 3.75) * mm]});
            skFitSpline(sketch, "E2419", {"points": [v(-94.45, 3.75) * mm, v(-94.74, 3.65) * mm, v(-95.04, 3.56) * mm, v(-95.34, 3.47) * mm]});
            skFitSpline(sketch, "E2420", {"points": [v(-95.34, 3.47) * mm, v(-95.58, 3.4) * mm, v(-95.82, 3.3) * mm, v(-96.1, 3.2) * mm]});
            skFitSpline(sketch, "E2421", {"points": [v(-96.1, 3.2) * mm, v(-95.32, 2.33) * mm, v(-94.5, 1.53) * mm, v(-93.72, 0.68) * mm]});
            skFitSpline(sketch, "E2422", {"points": [v(-93.72, 0.68) * mm, v(-93.37, 1.02) * mm, v(-93.03, 1.33) * mm, v(-92.7, 1.66) * mm]});
            skFitSpline(sketch, "E2423", {"points": [v(-92.7, 1.66) * mm, v(-92.33, 2.02) * mm, v(-91.96, 2.39) * mm, v(-91.6, 2.76) * mm]});
            skFitSpline(sketch, "E2424", {"points": [v(-91.6, 2.76) * mm, v(-91.45, 2.9) * mm, v(-91.31, 3.06) * mm, v(-91.17, 3.2) * mm]});
            skFitSpline(sketch, "E2425", {"points": [v(-91.17, 3.2) * mm, v(-90.95, 3.43) * mm, v(-90.7, 3.46) * mm, v(-90.48, 3.28) * mm]});
            skFitSpline(sketch, "E2426", {"points": [v(-90.48, 3.28) * mm, v(-90.27, 3.1) * mm, v(-90.24, 2.81) * mm, v(-90.43, 2.57) * mm]});
            skFitSpline(sketch, "E2427", {"points": [v(-90.43, 2.57) * mm, v(-90.54, 2.43) * mm, v(-90.68, 2.3) * mm, v(-90.8, 2.17) * mm]});
            skFitSpline(sketch, "E2428", {"points": [v(-90.8, 2.17) * mm, v(-91.47, 1.51) * mm, v(-92.14, 0.86) * mm, v(-92.8, 0.2) * mm]});
            skFitSpline(sketch, "E2429", {"points": [v(-92.8, 0.2) * mm, v(-92.87, 0.14) * mm, v(-92.93, 0.07) * mm, v(-93, 0) * mm]});
            skFitSpline(sketch, "E2430", {"points": [v(-93, 0) * mm, v(-92.86, -0.15) * mm, v(-92.72, -0.3) * mm, v(-92.58, -0.43) * mm]});
            skFitSpline(sketch, "E2431", {"points": [v(-92.58, -0.43) * mm, v(-92.09, -0.92) * mm, v(-91.6, -1.4) * mm, v(-91.1, -1.9) * mm]});
            skFitSpline(sketch, "E2432", {"points": [v(-91.1, -1.9) * mm, v(-90.9, -2.09) * mm, v(-90.71, -2.28) * mm, v(-90.52, -2.48) * mm]});
            skFitSpline(sketch, "E2433", {"points": [v(-90.52, -2.48) * mm, v(-90.47, -2.53) * mm, v(-90.43, -2.58) * mm, v(-90.39, -2.65) * mm]});
            skFitSpline(sketch, "E2434", {"points": [v(-90.39, -2.65) * mm, v(-90.25, -2.88) * mm, v(-90.3, -3.14) * mm, v(-90.49, -3.3) * mm]});
            skFitSpline(sketch, "E2435", {"points": [v(-90.49, -3.3) * mm, v(-90.69, -3.45) * mm, v(-90.94, -3.44) * mm, v(-91.14, -3.25) * mm]});
            skFitSpline(sketch, "E2436", {"points": [v(-91.14, -3.25) * mm, v(-91.34, -3.05) * mm, v(-91.52, -2.84) * mm, v(-91.72, -2.65) * mm]});
            skFitSpline(sketch, "E2437", {"points": [v(-91.72, -2.65) * mm, v(-92.26, -2.11) * mm, v(-92.8, -1.58) * mm, v(-93.35, -1.05) * mm]});
            skFitSpline(sketch, "E2438", {"points": [v(-93.35, -1.05) * mm, v(-93.46, -0.94) * mm, v(-93.58, -0.83) * mm, v(-93.72, -0.7) * mm]});
            skFitSpline(sketch, "E2439", {"points": [v(-93.72, -0.7) * mm, v(-94.5, -1.52) * mm, v(-95.29, -2.35) * mm, v(-96.1, -3.2) * mm]});
            skFitSpline(sketch, "E2440", {"points": [v(-96.1, -3.2) * mm, v(-95.92, -3.27) * mm, v(-95.78, -3.33) * mm, v(-95.63, -3.38) * mm]});
            skFitSpline(sketch, "E2441", {"points": [v(-95.63, -3.38) * mm, v(-95.27, -3.5) * mm, v(-94.9, -3.61) * mm, v(-94.53, -3.72) * mm]});
            skFitSpline(sketch, "E2442", {"points": [v(-94.53, -3.72) * mm, v(-94.12, -3.85) * mm, v(-94.01, -4.05) * mm, v(-94.13, -4.46) * mm]});
            skFitSpline(sketch, "E2443", {"points": [v(-94.13, -4.46) * mm, v(-94.14, -4.5) * mm, v(-94.15, -4.55) * mm, v(-94.13, -4.6) * mm]});
            skFitSpline(sketch, "E2444", {"points": [v(-94.13, -4.6) * mm, v(-93.95, -5.06) * mm, v(-93.88, -5.55) * mm, v(-93.81, -6.04) * mm]});
            skFitSpline(sketch, "E2445", {"points": [v(-93.81, -6.04) * mm, v(-93.77, -6.37) * mm, v(-93.73, -6.7) * mm, v(-93.68, -7.06) * mm]});
            skFitSpline(sketch, "E2446", {"points": [v(-93.68, -7.06) * mm, v(-93.46, -7) * mm, v(-93.25, -6.93) * mm, v(-93.04, -6.85) * mm]});
            skFitSpline(sketch, "E2447", {"points": [v(-93.04, -6.85) * mm, v(-92.53, -6.67) * mm, v(-92.03, -6.48) * mm, v(-91.53, -6.3) * mm]});
            skFitSpline(sketch, "E2448", {"points": [v(-91.53, -6.3) * mm, v(-91.28, -6.22) * mm, v(-91.03, -6.33) * mm, v(-90.93, -6.55) * mm]});
            skFitSpline(sketch, "E2449", {"points": [v(-90.93, -6.55) * mm, v(-90.82, -6.8) * mm, v(-90.9, -7.07) * mm, v(-91.14, -7.2) * mm]});
            skFitSpline(sketch, "E2450", {"points": [v(-91.14, -7.2) * mm, v(-91.3, -7.27) * mm, v(-91.47, -7.33) * mm, v(-91.63, -7.38) * mm]});
            skFitSpline(sketch, "E2451", {"points": [v(-91.63, -7.38) * mm, v(-92.2, -7.6) * mm, v(-92.79, -7.8) * mm, v(-93.37, -8) * mm]});
            skFitSpline(sketch, "E2452", {"points": [v(-93.37, -8) * mm, v(-93.43, -8.02) * mm, v(-93.48, -8.05) * mm, v(-93.55, -8.07) * mm]});
            skFitSpline(sketch, "E2453", {"points": [v(-93.55, -8.07) * mm, v(-93.49, -8.43) * mm, v(-93.43, -8.77) * mm, v(-93.36, -9.12) * mm]});
            skFitSpline(sketch, "E2454", {"points": [v(-93.36, -9.12) * mm, v(-93.28, -9.58) * mm, v(-93.2, -10.04) * mm, v(-93.12, -10.5) * mm]});
            skFitSpline(sketch, "E2455", {"points": [v(-93.12, -10.5) * mm, v(-93.07, -10.8) * mm, v(-93.24, -11.04) * mm, v(-93.51, -11.08) * mm]});
            skFitSpline(sketch, "E2456", {"points": [v(-93.51, -11.08) * mm, v(-93.8, -11.13) * mm, v(-94.02, -10.96) * mm, v(-94.08, -10.66) * mm]});
            skFitSpline(sketch, "E2457", {"points": [v(-94.08, -10.66) * mm, v(-94.13, -10.35) * mm, v(-94.18, -10.03) * mm, v(-94.23, -9.72) * mm]});
            skFitSpline(sketch, "E2458", {"points": [v(-94.23, -9.72) * mm, v(-94.3, -9.35) * mm, v(-94.37, -8.98) * mm, v(-94.44, -8.61) * mm]});
            skFitSpline(sketch, "E2459", {"points": [v(-94.44, -8.61) * mm, v(-94.45, -8.57) * mm, v(-94.47, -8.52) * mm, v(-94.49, -8.46) * mm]});
            skFitSpline(sketch, "E2460", {"points": [v(-94.49, -8.46) * mm, v(-94.75, -8.57) * mm, v(-95, -8.68) * mm, v(-95.24, -8.77) * mm]});
            skFitSpline(sketch, "E2461", {"points": [v(-95.24, -8.77) * mm, v(-95.64, -8.92) * mm, v(-96.04, -9.06) * mm, v(-96.44, -9.2) * mm]});
            skFitSpline(sketch, "E2462", {"points": [v(-96.44, -9.2) * mm, v(-96.59, -9.25) * mm, v(-96.74, -9.28) * mm, v(-96.93, -9.32) * mm]});
            skFitSpline(sketch, "E2463", {"points": [v(-96.93, -9.32) * mm, v(-96.93, -9.32) * mm, v(-96.95, -9.36) * mm, v(-96.98, -9.39) * mm]});
            skFitSpline(sketch, "E2464", {"points": [v(-96.98, -9.39) * mm, v(-97.18, -9.64) * mm, v(-97.48, -9.67) * mm, v(-97.73, -9.45) * mm]});
            skFitSpline(sketch, "E2465", {"points": [v(-97.73, -9.45) * mm, v(-98.01, -9.2) * mm, v(-98.28, -8.93) * mm, v(-98.56, -8.68) * mm]});
            skFitSpline(sketch, "E2466", {"points": [v(-98.56, -8.68) * mm, v(-98.7, -8.55) * mm, v(-98.85, -8.43) * mm, v(-99.02, -8.3) * mm]});
            skFitSpline(sketch, "E2467", {"points": [v(-99.02, -8.3) * mm, v(-99.4, -9.4) * mm, v(-99.67, -10.5) * mm, v(-100.02, -11.61) * mm]});
            skFitSpline(sketch, "E2468", {"points": [v(-100.02, -11.61) * mm, v(-99.54, -11.75) * mm, v(-99.1, -11.88) * mm, v(-98.64, -12) * mm]});
            skFitSpline(sketch, "E2469", {"points": [v(-98.64, -12) * mm, v(-98.11, -12.16) * mm, v(-97.58, -12.3) * mm, v(-97.05, -12.44) * mm]});
            skFitSpline(sketch, "E2470", {"points": [v(-97.05, -12.44) * mm, v(-96.89, -12.48) * mm, v(-96.72, -12.51) * mm, v(-96.56, -12.55) * mm]});
            skFitSpline(sketch, "E2471", {"points": [v(-96.56, -12.55) * mm, v(-96.28, -12.62) * mm, v(-96.12, -12.82) * mm, v(-96.15, -13.09) * mm]});
            skFitSpline(sketch, "E2472", {"points": [v(-96.15, -13.09) * mm, v(-96.18, -13.34) * mm, v(-96.38, -13.52) * mm, v(-96.67, -13.5) * mm]});
            skFitSpline(sketch, "E2473", {"points": [v(-96.67, -13.5) * mm, v(-96.83, -13.5) * mm, v(-96.99, -13.46) * mm, v(-97.14, -13.42) * mm]});
            skFitSpline(sketch, "E2474", {"points": [v(-97.14, -13.42) * mm, v(-98.04, -13.18) * mm, v(-98.94, -12.92) * mm, v(-99.84, -12.67) * mm]});
            skFitSpline(sketch, "E2475", {"points": [v(-99.84, -12.67) * mm, v(-99.97, -12.64) * mm, v(-100.1, -12.6) * mm, v(-100.26, -12.57) * mm]});
            skFitSpline(sketch, "E2476", {"points": [v(-100.26, -12.57) * mm, v(-100.31, -12.77) * mm, v(-100.37, -12.95) * mm, v(-100.42, -13.13) * mm]});
            skFitSpline(sketch, "E2477", {"points": [v(-100.42, -13.13) * mm, v(-100.6, -13.81) * mm, v(-100.77, -14.5) * mm, v(-100.94, -15.17) * mm]});
            skFitSpline(sketch, "E2478", {"points": [v(-100.94, -15.17) * mm, v(-101.02, -15.44) * mm, v(-101.09, -15.7) * mm, v(-101.17, -15.98) * mm]});
            skFitSpline(sketch, "E2479", {"points": [v(-101.17, -15.98) * mm, v(-101.19, -16.05) * mm, v(-101.22, -16.13) * mm, v(-101.26, -16.2) * mm]});
            skFitSpline(sketch, "E2480", {"points": [v(-101.26, -16.2) * mm, v(-101.4, -16.4) * mm, v(-101.65, -16.48) * mm, v(-101.87, -16.39) * mm]});
            skFitSpline(sketch, "E2481", {"points": [v(-101.87, -16.39) * mm, v(-102.1, -16.28) * mm, v(-102.2, -16.05) * mm, v(-102.14, -15.8) * mm]});
            skFitSpline(sketch, "E2482", {"points": [v(-102.14, -15.8) * mm, v(-102.07, -15.54) * mm, v(-101.98, -15.27) * mm, v(-101.9, -15) * mm]});
            skFitSpline(sketch, "E2483", {"points": [v(-101.9, -15) * mm, v(-101.67, -14.12) * mm, v(-101.44, -13.23) * mm, v(-101.2, -12.34) * mm]});
            skFitSpline(sketch, "E2484", {"points": [v(-101.2, -12.34) * mm, v(-101.34, -12.26) * mm, v(-103.83, -11.64) * mm, v(-104.57, -11.5) * mm]});
            skFitSpline(sketch, "E2485", {"points": [v(-104.57, -11.5) * mm, v(-104.54, -11.7) * mm, v(-104.52, -11.88) * mm, v(-104.49, -12.06) * mm]});
            skFitSpline(sketch, "E2486", {"points": [v(-104.49, -12.06) * mm, v(-104.41, -12.4) * mm, v(-104.33, -12.73) * mm, v(-104.26, -13.07) * mm]});
            skFitSpline(sketch, "E2487", {"points": [v(-104.26, -13.07) * mm, v(-104.14, -13.55) * mm, v(-104.26, -13.74) * mm, v(-104.74, -13.83) * mm]});
            skFitSpline(sketch, "E2488", {"points": [v(-104.74, -13.83) * mm, v(-105.3, -14.5) * mm, v(-106.02, -14.98) * mm, v(-106.7, -15.52) * mm]});
            skFitSpline(sketch, "E2489", {"points": [v(-106.7, -15.52) * mm, v(-106.54, -15.66) * mm, v(-106.4, -15.8) * mm, v(-106.24, -15.94) * mm]});
            skFitSpline(sketch, "E2490", {"points": [v(-106.24, -15.94) * mm, v(-105.83, -16.28) * mm, v(-105.42, -16.62) * mm, v(-105, -16.97) * mm]});
            skFitSpline(sketch, "E2491", {"points": [v(-105, -16.97) * mm, v(-104.77, -17.16) * mm, v(-104.73, -17.45) * mm, v(-104.91, -17.67) * mm]});
            skFitSpline(sketch, "E2492", {"points": [v(-104.91, -17.67) * mm, v(-105.08, -17.88) * mm, v(-105.4, -17.92) * mm, v(-105.62, -17.73) * mm]});
            skFitSpline(sketch, "E2493", {"points": [v(-105.62, -17.73) * mm, v(-105.95, -17.46) * mm, v(-106.28, -17.18) * mm, v(-106.6, -16.9) * mm]});
            skFitSpline(sketch, "E2494", {"points": [v(-106.6, -16.9) * mm, v(-106.9, -16.64) * mm, v(-107.2, -16.39) * mm, v(-107.5, -16.12) * mm]});
            skFitSpline(sketch, "E2495", {"points": [v(-67.24, -3.34) * mm, v(-67.1, -4.24) * mm, v(-66.93, -5.12) * mm, v(-66.7, -6) * mm]});
            skFitSpline(sketch, "E2496", {"points": [v(-66.7, -6) * mm, v(-66.46, -5.12) * mm, v(-66.27, -4.24) * mm, v(-66.15, -3.34) * mm]});
            skLineSegment(sketch, "E2497", {"start": v(-66.15, -3.34) * mm, "end": v(-67.24, -3.34) * mm});
            skFitSpline(sketch, "E2498", {"points": [v(-61.49, -3) * mm, v(-62.15, -2.34) * mm, v(-62.84, -1.75) * mm, v(-63.53, -1.2) * mm]});
            skFitSpline(sketch, "E2499", {"points": [v(-63.53, -1.2) * mm, v(-63.71, -1.52) * mm, v(-63.9, -1.83) * mm, v(-64.07, -2.15) * mm]});
            skFitSpline(sketch, "E2500", {"points": [v(-64.07, -2.15) * mm, v(-63.38, -2.44) * mm, v(-61.77, -2.97) * mm, v(-61.49, -3) * mm]});
            skFitSpline(sketch, "E2501", {"points": [v(-64.07, 2.14) * mm, v(-63.88, 1.81) * mm, v(-63.7, 1.5) * mm, v(-63.53, 1.19) * mm]});
            skFitSpline(sketch, "E2502", {"points": [v(-63.53, 1.19) * mm, v(-62.84, 1.74) * mm, v(-62.15, 2.34) * mm, v(-61.52, 2.98) * mm]});
            skFitSpline(sketch, "E2503", {"points": [v(-61.52, 2.98) * mm, v(-62.39, 2.75) * mm, v(-63.24, 2.47) * mm, v(-64.07, 2.14) * mm]});
            skFitSpline(sketch, "E2504", {"points": [v(-69.31, -2.15) * mm, v(-69.5, -1.83) * mm, v(-69.67, -1.51) * mm, v(-69.86, -1.2) * mm]});
            skFitSpline(sketch, "E2505", {"points": [v(-69.86, -1.2) * mm, v(-70.55, -1.75) * mm, v(-71.23, -2.35) * mm, v(-71.87, -3) * mm]});
            skFitSpline(sketch, "E2506", {"points": [v(-71.87, -3) * mm, v(-71, -2.77) * mm, v(-70.15, -2.48) * mm, v(-69.31, -2.15) * mm]});
            skFitSpline(sketch, "E2507", {"points": [v(-71.87, 2.98) * mm, v(-71.23, 2.34) * mm, v(-70.55, 1.74) * mm, v(-69.86, 1.19) * mm]});
            skFitSpline(sketch, "E2508", {"points": [v(-69.86, 1.19) * mm, v(-69.67, 1.5) * mm, v(-69.5, 1.82) * mm, v(-69.31, 2.14) * mm]});
            skFitSpline(sketch, "E2509", {"points": [v(-69.31, 2.14) * mm, v(-70.14, 2.47) * mm, v(-71, 2.76) * mm, v(-71.87, 2.98) * mm]});
            skFitSpline(sketch, "E2510", {"points": [v(-66.14, 3.33) * mm, v(-66.28, 4.23) * mm, v(-66.45, 5.12) * mm, v(-66.7, 5.99) * mm]});
            skFitSpline(sketch, "E2511", {"points": [v(-66.7, 5.99) * mm, v(-66.92, 5.1) * mm, v(-67.11, 4.23) * mm, v(-67.24, 3.33) * mm]});
            skLineSegment(sketch, "E2512", {"start": v(-67.24, 3.33) * mm, "end": v(-66.14, 3.33) * mm});
            skFitSpline(sketch, "E2513", {"points": [v(-67.22, -7.98) * mm, v(-67.28, -7.74) * mm, v(-67.33, -7.52) * mm, v(-67.38, -7.3) * mm]});
            skFitSpline(sketch, "E2514", {"points": [v(-67.38, -7.3) * mm, v(-67.6, -6.37) * mm, v(-67.82, -5.44) * mm, v(-68.03, -4.5) * mm]});
            skFitSpline(sketch, "E2515", {"points": [v(-68.03, -4.5) * mm, v(-68.12, -4.1) * mm, v(-68.19, -3.68) * mm, v(-68.27, -3.27) * mm]});
            skFitSpline(sketch, "E2516", {"points": [v(-68.27, -3.27) * mm, v(-68.34, -2.92) * mm, v(-68.38, -2.9) * mm, v(-68.7, -3) * mm]});
            skFitSpline(sketch, "E2517", {"points": [v(-68.7, -3) * mm, v(-69.03, -3.1) * mm, v(-69.36, -3.23) * mm, v(-69.69, -3.34) * mm]});
            skFitSpline(sketch, "E2518", {"points": [v(-69.69, -3.34) * mm, v(-70.63, -3.63) * mm, v(-71.58, -3.92) * mm, v(-72.53, -4.21) * mm]});
            skFitSpline(sketch, "E2519", {"points": [v(-72.53, -4.21) * mm, v(-72.79, -4.3) * mm, v(-73.05, -4.37) * mm, v(-73.33, -4.45) * mm]});
            skFitSpline(sketch, "E2520", {"points": [v(-73.33, -4.45) * mm, v(-71.41, -5.85) * mm, v(-69.4, -7.01) * mm, v(-67.22, -7.98) * mm]});
            skFitSpline(sketch, "E2521", {"points": [v(-66.15, -7.95) * mm, v(-66.14, -7.96) * mm, v(-66.13, -7.98) * mm, v(-66.12, -8) * mm]});
            skFitSpline(sketch, "E2522", {"points": [v(-66.12, -8) * mm, v(-65.08, -7.46) * mm, v(-64.02, -6.95) * mm, v(-63, -6.4) * mm]});
            skFitSpline(sketch, "E2523", {"points": [v(-63, -6.4) * mm, v(-62.23, -5.99) * mm, v(-60.2, -4.6) * mm, v(-60.07, -4.44) * mm]});
            skFitSpline(sketch, "E2524", {"points": [v(-60.07, -4.44) * mm, v(-60.35, -4.36) * mm, v(-60.63, -4.28) * mm, v(-60.9, -4.2) * mm]});
            skFitSpline(sketch, "E2525", {"points": [v(-60.9, -4.2) * mm, v(-61.66, -3.97) * mm, v(-62.42, -3.75) * mm, v(-63.17, -3.51) * mm]});
            skFitSpline(sketch, "E2526", {"points": [v(-63.17, -3.51) * mm, v(-63.68, -3.35) * mm, v(-64.18, -3.16) * mm, v(-64.68, -3) * mm]});
            skFitSpline(sketch, "E2527", {"points": [v(-64.68, -3) * mm, v(-65, -2.9) * mm, v(-65.03, -2.9) * mm, v(-65.1, -3.24) * mm]});
            skFitSpline(sketch, "E2528", {"points": [v(-65.1, -3.24) * mm, v(-65.22, -3.76) * mm, v(-65.3, -4.29) * mm, v(-65.42, -4.8) * mm]});
            skFitSpline(sketch, "E2529", {"points": [v(-65.42, -4.8) * mm, v(-65.6, -5.62) * mm, v(-65.8, -6.42) * mm, v(-65.98, -7.23) * mm]});
            skFitSpline(sketch, "E2530", {"points": [v(-65.98, -7.23) * mm, v(-66.04, -7.47) * mm, v(-66.1, -7.7) * mm, v(-66.15, -7.95) * mm]});
            skFitSpline(sketch, "E2531", {"points": [v(-67.23, 7.94) * mm, v(-67.24, 7.95) * mm, v(-67.25, 7.97) * mm, v(-67.26, 7.98) * mm]});
            skFitSpline(sketch, "E2532", {"points": [v(-67.26, 7.98) * mm, v(-68.3, 7.45) * mm, v(-69.37, 6.97) * mm, v(-70.39, 6.38) * mm]});
            skFitSpline(sketch, "E2533", {"points": [v(-70.39, 6.38) * mm, v(-71.4, 5.8) * mm, v(-72.35, 5.12) * mm, v(-73.34, 4.46) * mm]});
            skFitSpline(sketch, "E2534", {"points": [v(-73.34, 4.46) * mm, v(-73.29, 4.43) * mm, v(-73.27, 4.42) * mm, v(-73.25, 4.41) * mm]});
            skFitSpline(sketch, "E2535", {"points": [v(-73.25, 4.41) * mm, v(-72.72, 4.26) * mm, v(-72.2, 4.13) * mm, v(-71.68, 3.97) * mm]});
            skFitSpline(sketch, "E2536", {"points": [v(-71.68, 3.97) * mm, v(-70.9, 3.72) * mm, v(-70.14, 3.45) * mm, v(-69.36, 3.2) * mm]});
            skFitSpline(sketch, "E2537", {"points": [v(-69.36, 3.2) * mm, v(-69.1, 3.11) * mm, v(-68.85, 3.03) * mm, v(-68.59, 2.96) * mm]});
            skFitSpline(sketch, "E2538", {"points": [v(-68.59, 2.96) * mm, v(-68.4, 2.9) * mm, v(-68.36, 2.92) * mm, v(-68.31, 3.1) * mm]});
            skFitSpline(sketch, "E2539", {"points": [v(-68.31, 3.1) * mm, v(-68.24, 3.38) * mm, v(-68.18, 3.65) * mm, v(-68.13, 3.92) * mm]});
            skFitSpline(sketch, "E2540", {"points": [v(-68.13, 3.92) * mm, v(-67.96, 4.74) * mm, v(-67.8, 5.55) * mm, v(-67.62, 6.36) * mm]});
            skFitSpline(sketch, "E2541", {"points": [v(-67.62, 6.36) * mm, v(-67.5, 6.89) * mm, v(-67.36, 7.41) * mm, v(-67.23, 7.94) * mm]});
            skFitSpline(sketch, "E2542", {"points": [v(-59.5, 3.54) * mm, v(-59.75, 3.3) * mm, v(-59.96, 3.1) * mm, v(-60.17, 2.9) * mm]});
            skFitSpline(sketch, "E2543", {"points": [v(-60.17, 2.9) * mm, v(-60.73, 2.38) * mm, v(-61.3, 1.84) * mm, v(-61.86, 1.32) * mm]});
            skFitSpline(sketch, "E2544", {"points": [v(-61.86, 1.32) * mm, v(-62.26, 0.95) * mm, v(-62.68, 0.6) * mm, v(-63.09, 0.25) * mm]});
            skFitSpline(sketch, "E2545", {"points": [v(-63.09, 0.25) * mm, v(-63.35, 0.02) * mm, v(-63.35, -0.02) * mm, v(-63.1, -0.25) * mm]});
            skFitSpline(sketch, "E2546", {"points": [v(-63.1, -0.25) * mm, v(-62.7, -0.6) * mm, v(-62.3, -0.93) * mm, v(-61.92, -1.28) * mm]});
            skFitSpline(sketch, "E2547", {"points": [v(-61.92, -1.28) * mm, v(-61.3, -1.84) * mm, v(-60.7, -2.41) * mm, v(-60.1, -2.98) * mm]});
            skFitSpline(sketch, "E2548", {"points": [v(-60.1, -2.98) * mm, v(-59.91, -3.16) * mm, v(-59.72, -3.34) * mm, v(-59.5, -3.54) * mm]});
            skFitSpline(sketch, "E2549", {"points": [v(-59.5, -3.54) * mm, v(-59.48, -3.2) * mm, v(-59.45, -2.89) * mm, v(-59.43, -2.58) * mm]});
            skFitSpline(sketch, "E2550", {"points": [v(-59.43, -2.58) * mm, v(-59.4, -2) * mm, v(-59.38, -1.4) * mm, v(-59.34, -0.82) * mm]});
            skFitSpline(sketch, "E2551", {"points": [v(-59.34, -0.82) * mm, v(-59.3, -0.28) * mm, v(-59.3, 0.26) * mm, v(-59.34, 0.8) * mm]});
            skFitSpline(sketch, "E2552", {"points": [v(-59.34, 0.8) * mm, v(-59.36, 1) * mm, v(-59.35, 1.19) * mm, v(-59.36, 1.38) * mm]});
            skFitSpline(sketch, "E2553", {"points": [v(-59.36, 1.38) * mm, v(-59.38, 1.7) * mm, v(-59.4, 2.01) * mm, v(-59.43, 2.33) * mm]});
            skFitSpline(sketch, "E2554", {"points": [v(-59.43, 2.33) * mm, v(-59.45, 2.68) * mm, v(-59.47, 3.03) * mm, v(-59.49, 3.38) * mm]});
            skFitSpline(sketch, "E2555", {"points": [v(-59.49, 3.38) * mm, v(-59.49, 3.42) * mm, v(-59.5, 3.45) * mm, v(-59.5, 3.54) * mm]});
            skFitSpline(sketch, "E2556", {"points": [v(-66.15, 7.96) * mm, v(-66.15, 7.92) * mm, v(-66.15, 7.9) * mm, v(-66.14, 7.86) * mm]});
            skFitSpline(sketch, "E2557", {"points": [v(-66.14, 7.86) * mm, v(-66, 7.34) * mm, v(-65.87, 6.81) * mm, v(-65.74, 6.29) * mm]});
            skFitSpline(sketch, "E2558", {"points": [v(-65.74, 6.29) * mm, v(-65.63, 5.84) * mm, v(-65.53, 5.4) * mm, v(-65.44, 4.96) * mm]});
            skFitSpline(sketch, "E2559", {"points": [v(-65.44, 4.96) * mm, v(-65.33, 4.4) * mm, v(-65.23, 3.83) * mm, v(-65.11, 3.27) * mm]});
            skFitSpline(sketch, "E2560", {"points": [v(-65.11, 3.27) * mm, v(-65.04, 2.89) * mm, v(-65, 2.87) * mm, v(-64.63, 3) * mm]});
            skFitSpline(sketch, "E2561", {"points": [v(-64.63, 3) * mm, v(-64.25, 3.13) * mm, v(-63.87, 3.28) * mm, v(-63.48, 3.4) * mm]});
            skFitSpline(sketch, "E2562", {"points": [v(-63.48, 3.4) * mm, v(-62.58, 3.69) * mm, v(-61.67, 3.96) * mm, v(-60.76, 4.23) * mm]});
            skFitSpline(sketch, "E2563", {"points": [v(-60.76, 4.23) * mm, v(-60.53, 4.3) * mm, v(-60.3, 4.37) * mm, v(-60.05, 4.44) * mm]});
            skFitSpline(sketch, "E2564", {"points": [v(-60.05, 4.44) * mm, v(-61.97, 5.84) * mm, v(-63.99, 7) * mm, v(-66.15, 7.96) * mm]});
            skFitSpline(sketch, "E2565", {"points": [v(-73.87, -3.55) * mm, v(-73.44, -3.13) * mm, v(-73.06, -2.74) * mm, v(-72.65, -2.36) * mm]});
            skFitSpline(sketch, "E2566", {"points": [v(-72.65, -2.36) * mm, v(-72.1, -1.85) * mm, v(-71.54, -1.35) * mm, v(-70.98, -0.85) * mm]});
            skFitSpline(sketch, "E2567", {"points": [v(-70.98, -0.85) * mm, v(-70.76, -0.65) * mm, v(-70.52, -0.46) * mm, v(-70.3, -0.26) * mm]});
            skFitSpline(sketch, "E2568", {"points": [v(-70.3, -0.26) * mm, v(-70.03, -0.01) * mm, v(-70.03, 0.01) * mm, v(-70.3, 0.26) * mm]});
            skFitSpline(sketch, "E2569", {"points": [v(-70.3, 0.26) * mm, v(-70.54, 0.47) * mm, v(-70.8, 0.67) * mm, v(-71.03, 0.89) * mm]});
            skFitSpline(sketch, "E2570", {"points": [v(-71.03, 0.89) * mm, v(-71.78, 1.58) * mm, v(-72.53, 2.27) * mm, v(-73.28, 2.97) * mm]});
            skFitSpline(sketch, "E2571", {"points": [v(-73.28, 2.97) * mm, v(-73.47, 3.15) * mm, v(-73.66, 3.33) * mm, v(-73.87, 3.53) * mm]});
            skFitSpline(sketch, "E2572", {"points": [v(-73.87, 3.53) * mm, v(-74.12, 1.16) * mm, v(-74.11, -1.17) * mm, v(-73.87, -3.55) * mm]});
            skFitSpline(sketch, "E2573", {"points": [v(-66.13, -14.4) * mm, v(-66.18, -14.66) * mm, v(-66.12, -14.84) * mm, v(-65.98, -15.02) * mm]});
            skFitSpline(sketch, "E2574", {"points": [v(-65.98, -15.02) * mm, v(-65.55, -15.61) * mm, v(-65.06, -16.14) * mm, v(-64.57, -16.68) * mm]});
            skFitSpline(sketch, "E2575", {"points": [v(-64.57, -16.68) * mm, v(-64.49, -16.77) * mm, v(-64.4, -16.86) * mm, v(-64.35, -16.96) * mm]});
            skFitSpline(sketch, "E2576", {"points": [v(-64.35, -16.96) * mm, v(-64.23, -17.18) * mm, v(-64.29, -17.44) * mm, v(-64.48, -17.59) * mm]});
            skFitSpline(sketch, "E2577", {"points": [v(-64.48, -17.59) * mm, v(-64.68, -17.74) * mm, v(-64.96, -17.72) * mm, v(-65.13, -17.52) * mm]});
            skFitSpline(sketch, "E2578", {"points": [v(-65.13, -17.52) * mm, v(-65.61, -16.97) * mm, v(-66.1, -16.4) * mm, v(-66.57, -15.85) * mm]});
            skFitSpline(sketch, "E2579", {"points": [v(-66.57, -15.85) * mm, v(-66.6, -15.81) * mm, v(-66.64, -15.77) * mm, v(-66.7, -15.7) * mm]});
            skFitSpline(sketch, "E2580", {"points": [v(-66.7, -15.7) * mm, v(-66.73, -15.76) * mm, v(-66.77, -15.8) * mm, v(-66.8, -15.83) * mm]});
            skFitSpline(sketch, "E2581", {"points": [v(-66.8, -15.83) * mm, v(-67.21, -16.31) * mm, v(-67.62, -16.79) * mm, v(-68.04, -17.27) * mm]});
            skFitSpline(sketch, "E2582", {"points": [v(-68.04, -17.27) * mm, v(-68.1, -17.35) * mm, v(-68.17, -17.43) * mm, v(-68.24, -17.5) * mm]});
            skFitSpline(sketch, "E2583", {"points": [v(-68.24, -17.5) * mm, v(-68.43, -17.7) * mm, v(-68.7, -17.74) * mm, v(-68.9, -17.59) * mm]});
            skFitSpline(sketch, "E2584", {"points": [v(-68.9, -17.59) * mm, v(-69.11, -17.43) * mm, v(-69.17, -17.14) * mm, v(-69, -16.92) * mm]});
            skFitSpline(sketch, "E2585", {"points": [v(-69, -16.92) * mm, v(-68.81, -16.66) * mm, v(-68.59, -16.42) * mm, v(-68.36, -16.18) * mm]});
            skFitSpline(sketch, "E2586", {"points": [v(-68.36, -16.18) * mm, v(-67.99, -15.78) * mm, v(-67.66, -15.36) * mm, v(-67.33, -14.92) * mm]});
            skFitSpline(sketch, "E2587", {"points": [v(-67.33, -14.92) * mm, v(-67.21, -14.77) * mm, v(-67.25, -14.6) * mm, v(-67.26, -14.41) * mm]});
            skFitSpline(sketch, "E2588", {"points": [v(-67.26, -14.41) * mm, v(-67.32, -14.46) * mm, v(-67.36, -14.48) * mm, v(-67.4, -14.52) * mm]});
            skFitSpline(sketch, "E2589", {"points": [v(-67.4, -14.52) * mm, v(-67.68, -14.76) * mm, v(-67.96, -15) * mm, v(-68.24, -15.23) * mm]});
            skFitSpline(sketch, "E2590", {"points": [v(-68.24, -15.23) * mm, v(-68.35, -15.32) * mm, v(-68.47, -15.4) * mm, v(-68.6, -15.47) * mm]});
            skFitSpline(sketch, "E2591", {"points": [v(-68.6, -15.47) * mm, v(-68.8, -15.58) * mm, v(-69.06, -15.5) * mm, v(-69.2, -15.31) * mm]});
            skFitSpline(sketch, "E2592", {"points": [v(-69.2, -15.31) * mm, v(-69.32, -15.14) * mm, v(-69.3, -14.89) * mm, v(-69.16, -14.72) * mm]});
            skFitSpline(sketch, "E2593", {"points": [v(-69.16, -14.72) * mm, v(-69.13, -14.68) * mm, v(-69.1, -14.65) * mm, v(-69.06, -14.62) * mm]});
            skFitSpline(sketch, "E2594", {"points": [v(-69.06, -14.62) * mm, v(-68.53, -14.17) * mm, v(-68, -13.71) * mm, v(-67.47, -13.27) * mm]});
            skFitSpline(sketch, "E2595", {"points": [v(-67.47, -13.27) * mm, v(-67.26, -13.1) * mm, v(-67.2, -12.9) * mm, v(-67.27, -12.64) * mm]});
            skFitSpline(sketch, "E2596", {"points": [v(-67.27, -12.64) * mm, v(-67.32, -12.67) * mm, v(-67.37, -12.7) * mm, v(-67.4, -12.73) * mm]});
            skFitSpline(sketch, "E2597", {"points": [v(-67.4, -12.73) * mm, v(-67.64, -12.9) * mm, v(-67.88, -13.1) * mm, v(-68.11, -13.27) * mm]});
            skFitSpline(sketch, "E2598", {"points": [v(-68.11, -13.27) * mm, v(-68.26, -13.38) * mm, v(-68.43, -13.43) * mm, v(-68.6, -13.35) * mm]});
            skFitSpline(sketch, "E2599", {"points": [v(-68.6, -13.35) * mm, v(-68.8, -13.27) * mm, v(-68.9, -13.14) * mm, v(-68.93, -12.94) * mm]});
            skFitSpline(sketch, "E2600", {"points": [v(-68.93, -12.94) * mm, v(-68.95, -12.73) * mm, v(-68.86, -12.58) * mm, v(-68.7, -12.47) * mm]});
            skFitSpline(sketch, "E2601", {"points": [v(-68.7, -12.47) * mm, v(-68.23, -12.13) * mm, v(-67.77, -11.79) * mm, v(-67.31, -11.44) * mm]});
            skFitSpline(sketch, "E2602", {"points": [v(-67.31, -11.44) * mm, v(-67.26, -11.4) * mm, v(-67.22, -11.32) * mm, v(-67.22, -11.26) * mm]});
            skFitSpline(sketch, "E2603", {"points": [v(-67.22, -11.26) * mm, v(-67.2, -10.74) * mm, v(-67.18, -10.21) * mm, v(-67.27, -9.67) * mm]});
            skFitSpline(sketch, "E2604", {"points": [v(-67.27, -9.67) * mm, v(-67.54, -9.81) * mm, v(-67.8, -9.95) * mm, v(-68.07, -10.1) * mm]});
            skFitSpline(sketch, "E2605", {"points": [v(-68.07, -10.1) * mm, v(-68.72, -10.45) * mm, v(-69.37, -10.8) * mm, v(-70.02, -11.16) * mm]});
            skFitSpline(sketch, "E2606", {"points": [v(-70.02, -11.16) * mm, v(-70.3, -11.3) * mm, v(-70.59, -11.45) * mm, v(-70.88, -11.6) * mm]});
            skFitSpline(sketch, "E2607", {"points": [v(-70.88, -11.6) * mm, v(-70.98, -11.64) * mm, v(-71.02, -11.71) * mm, v(-71.03, -11.8) * mm]});
            skFitSpline(sketch, "E2608", {"points": [v(-71.03, -11.8) * mm, v(-71.11, -12.24) * mm, v(-71.2, -12.67) * mm, v(-71.27, -13.1) * mm]});
            skFitSpline(sketch, "E2609", {"points": [v(-71.27, -13.1) * mm, v(-71.3, -13.3) * mm, v(-71.28, -13.49) * mm, v(-71.3, -13.68) * mm]});
            skFitSpline(sketch, "E2610", {"points": [v(-71.3, -13.68) * mm, v(-71.31, -13.98) * mm, v(-71.5, -14.16) * mm, v(-71.78, -14.16) * mm]});
            skFitSpline(sketch, "E2611", {"points": [v(-71.78, -14.16) * mm, v(-72.05, -14.16) * mm, v(-72.26, -13.92) * mm, v(-72.26, -13.64) * mm]});
            skFitSpline(sketch, "E2612", {"points": [v(-72.26, -13.64) * mm, v(-72.25, -13.05) * mm, v(-72.16, -12.46) * mm, v(-72.04, -11.89) * mm]});
            skFitSpline(sketch, "E2613", {"points": [v(-72.04, -11.89) * mm, v(-71.99, -11.67) * mm, v(-71.96, -11.45) * mm, v(-71.92, -11.23) * mm]});
            skFitSpline(sketch, "E2614", {"points": [v(-71.92, -11.23) * mm, v(-71.87, -10.98) * mm, v(-71.73, -10.83) * mm, v(-71.48, -10.78) * mm]});
            skFitSpline(sketch, "E2615", {"points": [v(-71.48, -10.78) * mm, v(-71.44, -10.77) * mm, v(-71.39, -10.76) * mm, v(-71.35, -10.74) * mm]});
            skFitSpline(sketch, "E2616", {"points": [v(-71.35, -10.74) * mm, v(-70.6, -10.33) * mm, v(-69.84, -9.93) * mm, v(-69.09, -9.53) * mm]});
            skFitSpline(sketch, "E2617", {"points": [v(-69.09, -9.53) * mm, v(-68.78, -9.36) * mm, v(-68.46, -9.2) * mm, v(-68.15, -9.04) * mm]});
            skFitSpline(sketch, "E2618", {"points": [v(-68.15, -9.04) * mm, v(-68.04, -8.98) * mm, v(-67.94, -8.91) * mm, v(-67.8, -8.83) * mm]});
            skFitSpline(sketch, "E2619", {"points": [v(-67.8, -8.83) * mm, v(-68.11, -8.66) * mm, v(-68.4, -8.51) * mm, v(-68.67, -8.37) * mm]});
            skFitSpline(sketch, "E2620", {"points": [v(-68.67, -8.37) * mm, v(-69.3, -8.05) * mm, v(-69.95, -7.74) * mm, v(-70.57, -7.4) * mm]});
            skFitSpline(sketch, "E2621", {"points": [v(-70.57, -7.4) * mm, v(-70.94, -7.21) * mm, v(-71.28, -6.98) * mm, v(-71.63, -6.76) * mm]});
            skFitSpline(sketch, "E2622", {"points": [v(-71.63, -6.76) * mm, v(-72.14, -6.44) * mm, v(-72.64, -6.1) * mm, v(-73.14, -5.78) * mm]});
            skFitSpline(sketch, "E2623", {"points": [v(-73.14, -5.78) * mm, v(-73.34, -5.65) * mm, v(-73.54, -5.53) * mm, v(-73.77, -5.38) * mm]});
            skFitSpline(sketch, "E2624", {"points": [v(-73.77, -5.38) * mm, v(-73.78, -5.47) * mm, v(-73.79, -5.53) * mm, v(-73.79, -5.59) * mm]});
            skFitSpline(sketch, "E2625", {"points": [v(-73.79, -5.59) * mm, v(-73.77, -6.3) * mm, v(-73.75, -7.03) * mm, v(-73.73, -7.74) * mm]});
            skFitSpline(sketch, "E2626", {"points": [v(-73.73, -7.74) * mm, v(-73.71, -8.23) * mm, v(-73.7, -8.72) * mm, v(-73.68, -9.2) * mm]});
            skFitSpline(sketch, "E2627", {"points": [v(-73.68, -9.2) * mm, v(-73.67, -9.32) * mm, v(-73.65, -9.44) * mm, v(-73.62, -9.55) * mm]});
            skFitSpline(sketch, "E2628", {"points": [v(-73.62, -9.55) * mm, v(-73.56, -9.78) * mm, v(-73.6, -9.97) * mm, v(-73.78, -10.12) * mm]});
            skFitSpline(sketch, "E2629", {"points": [v(-73.78, -10.12) * mm, v(-74.4, -10.63) * mm, v(-74.96, -11.22) * mm, v(-75.67, -11.62) * mm]});
            skFitSpline(sketch, "E2630", {"points": [v(-75.67, -11.62) * mm, v(-75.83, -11.7) * mm, v(-75.97, -11.77) * mm, v(-76.15, -11.7) * mm]});
            skFitSpline(sketch, "E2631", {"points": [v(-76.15, -11.7) * mm, v(-76.5, -11.57) * mm, v(-76.6, -11.14) * mm, v(-76.32, -10.88) * mm]});
            skFitSpline(sketch, "E2632", {"points": [v(-76.32, -10.88) * mm, v(-76.26, -10.83) * mm, v(-76.2, -10.78) * mm, v(-76.12, -10.75) * mm]});
            skFitSpline(sketch, "E2633", {"points": [v(-76.12, -10.75) * mm, v(-75.6, -10.45) * mm, v(-75.18, -10.02) * mm, v(-74.71, -9.64) * mm]});
            skFitSpline(sketch, "E2634", {"points": [v(-74.71, -9.64) * mm, v(-74.64, -9.58) * mm, v(-74.63, -9.5) * mm, v(-74.64, -9.42) * mm]});
            skFitSpline(sketch, "E2635", {"points": [v(-74.64, -9.42) * mm, v(-74.65, -9.14) * mm, v(-74.67, -8.85) * mm, v(-74.68, -8.56) * mm]});
            skFitSpline(sketch, "E2636", {"points": [v(-74.68, -8.56) * mm, v(-74.7, -8.18) * mm, v(-74.69, -7.8) * mm, v(-74.7, -7.41) * mm]});
            skFitSpline(sketch, "E2637", {"points": [v(-74.7, -7.41) * mm, v(-74.72, -6.83) * mm, v(-74.75, -6.25) * mm, v(-74.78, -5.67) * mm]});
            skFitSpline(sketch, "E2638", {"points": [v(-74.78, -5.67) * mm, v(-74.78, -5.57) * mm, v(-74.76, -5.46) * mm, v(-74.75, -5.31) * mm]});
            skFitSpline(sketch, "E2639", {"points": [v(-74.75, -5.31) * mm, v(-75.14, -5.5) * mm, v(-75.5, -5.65) * mm, v(-75.84, -5.87) * mm]});
            skFitSpline(sketch, "E2640", {"points": [v(-75.84, -5.87) * mm, v(-75.93, -5.93) * mm, v(-76.02, -6) * mm, v(-76.12, -6.06) * mm]});
            skFitSpline(sketch, "E2641", {"points": [v(-76.12, -6.06) * mm, v(-76.24, -6.12) * mm, v(-76.3, -6.2) * mm, v(-76.3, -6.34) * mm]});
            skFitSpline(sketch, "E2642", {"points": [v(-76.3, -6.34) * mm, v(-76.36, -6.88) * mm, v(-76.43, -7.41) * mm, v(-76.48, -7.95) * mm]});
            skFitSpline(sketch, "E2643", {"points": [v(-76.48, -7.95) * mm, v(-76.5, -8.25) * mm, v(-76.7, -8.45) * mm, v(-76.99, -8.45) * mm]});
            skFitSpline(sketch, "E2644", {"points": [v(-76.99, -8.45) * mm, v(-77.27, -8.44) * mm, v(-77.48, -8.23) * mm, v(-77.46, -7.93) * mm]});
            skFitSpline(sketch, "E2645", {"points": [v(-77.46, -7.93) * mm, v(-77.45, -7.63) * mm, v(-77.4, -7.33) * mm, v(-77.36, -7.03) * mm]});
            skFitSpline(sketch, "E2646", {"points": [v(-77.36, -7.03) * mm, v(-77.35, -6.97) * mm, v(-77.34, -6.9) * mm, v(-77.33, -6.82) * mm]});
            skFitSpline(sketch, "E2647", {"points": [v(-77.33, -6.82) * mm, v(-77.57, -6.9) * mm, v(-77.73, -7) * mm, v(-77.78, -7.26) * mm]});
            skFitSpline(sketch, "E2648", {"points": [v(-77.78, -7.26) * mm, v(-77.9, -7.94) * mm, v(-78.1, -8.61) * mm, v(-78.16, -9.3) * mm]});
            skFitSpline(sketch, "E2649", {"points": [v(-78.16, -9.3) * mm, v(-78.16, -9.34) * mm, v(-78.18, -9.37) * mm, v(-78.18, -9.4) * mm]});
            skFitSpline(sketch, "E2650", {"points": [v(-78.18, -9.4) * mm, v(-78.2, -9.67) * mm, v(-78.47, -9.84) * mm, v(-78.67, -9.83) * mm]});
            skFitSpline(sketch, "E2651", {"points": [v(-78.67, -9.83) * mm, v(-78.93, -9.82) * mm, v(-79.15, -9.6) * mm, v(-79.14, -9.32) * mm]});
            skFitSpline(sketch, "E2652", {"points": [v(-79.14, -9.32) * mm, v(-79.13, -9.05) * mm, v(-79.08, -8.78) * mm, v(-79.03, -8.51) * mm]});
            skFitSpline(sketch, "E2653", {"points": [v(-79.03, -8.51) * mm, v(-79, -8.25) * mm, v(-78.94, -8) * mm, v(-78.89, -7.74) * mm]});
            skFitSpline(sketch, "E2654", {"points": [v(-78.89, -7.74) * mm, v(-78.89, -7.73) * mm, v(-78.9, -7.73) * mm, v(-78.9, -7.7) * mm]});
            skFitSpline(sketch, "E2655", {"points": [v(-78.9, -7.7) * mm, v(-79.07, -7.78) * mm, v(-79.22, -7.86) * mm, v(-79.3, -8.04) * mm]});
            skFitSpline(sketch, "E2656", {"points": [v(-79.3, -8.04) * mm, v(-79.62, -8.73) * mm, v(-79.84, -9.44) * mm, v(-80.06, -10.16) * mm]});
            skFitSpline(sketch, "E2657", {"points": [v(-80.06, -10.16) * mm, v(-80.1, -10.27) * mm, v(-80.14, -10.39) * mm, v(-80.2, -10.5) * mm]});
            skFitSpline(sketch, "E2658", {"points": [v(-80.2, -10.5) * mm, v(-80.33, -10.73) * mm, v(-80.6, -10.81) * mm, v(-80.84, -10.7) * mm]});
            skFitSpline(sketch, "E2659", {"points": [v(-80.84, -10.7) * mm, v(-81.03, -10.61) * mm, v(-81.16, -10.33) * mm, v(-81.08, -10.1) * mm]});
            skFitSpline(sketch, "E2660", {"points": [v(-81.08, -10.1) * mm, v(-80.81, -9.37) * mm, v(-80.57, -8.65) * mm, v(-80.31, -7.93) * mm]});
            skFitSpline(sketch, "E2661", {"points": [v(-80.31, -7.93) * mm, v(-80.3, -7.91) * mm, v(-80.31, -7.9) * mm, v(-80.3, -7.86) * mm]});
            skFitSpline(sketch, "E2662", {"points": [v(-80.3, -7.86) * mm, v(-80.4, -7.84) * mm, v(-80.48, -7.82) * mm, v(-80.57, -7.8) * mm]});
            skFitSpline(sketch, "E2663", {"points": [v(-80.57, -7.8) * mm, v(-81.15, -7.7) * mm, v(-81.72, -7.59) * mm, v(-82.3, -7.48) * mm]});
            skFitSpline(sketch, "E2664", {"points": [v(-82.3, -7.48) * mm, v(-82.4, -7.46) * mm, v(-82.5, -7.43) * mm, v(-82.62, -7.41) * mm]});
            skFitSpline(sketch, "E2665", {"points": [v(-82.62, -7.41) * mm, v(-82.87, -7.37) * mm, v(-83.05, -7.15) * mm, v(-83.03, -6.9) * mm]});
            skFitSpline(sketch, "E2666", {"points": [v(-83.03, -6.9) * mm, v(-83.01, -6.66) * mm, v(-82.82, -6.47) * mm, v(-82.58, -6.46) * mm]});
            skFitSpline(sketch, "E2667", {"points": [v(-82.58, -6.46) * mm, v(-82.47, -6.45) * mm, v(-82.35, -6.47) * mm, v(-82.24, -6.49) * mm]});
            skFitSpline(sketch, "E2668", {"points": [v(-82.24, -6.49) * mm, v(-81.51, -6.65) * mm, v(-80.78, -6.82) * mm, v(-80.03, -6.9) * mm]});
            skFitSpline(sketch, "E2669", {"points": [v(-80.03, -6.9) * mm, v(-79.8, -6.93) * mm, v(-79.64, -6.84) * mm, v(-79.42, -6.72) * mm]});
            skFitSpline(sketch, "E2670", {"points": [v(-79.42, -6.72) * mm, v(-79.6, -6.66) * mm, v(-79.72, -6.61) * mm, v(-79.85, -6.56) * mm]});
            skFitSpline(sketch, "E2671", {"points": [v(-79.85, -6.56) * mm, v(-80.13, -6.46) * mm, v(-80.4, -6.37) * mm, v(-80.69, -6.26) * mm]});
            skFitSpline(sketch, "E2672", {"points": [v(-80.69, -6.26) * mm, v(-80.78, -6.23) * mm, v(-80.88, -6.18) * mm, v(-80.97, -6.13) * mm]});
            skFitSpline(sketch, "E2673", {"points": [v(-80.97, -6.13) * mm, v(-81.23, -5.98) * mm, v(-81.32, -5.73) * mm, v(-81.2, -5.48) * mm]});
            skFitSpline(sketch, "E2674", {"points": [v(-81.2, -5.48) * mm, v(-81.08, -5.25) * mm, v(-80.81, -5.16) * mm, v(-80.54, -5.26) * mm]});
            skFitSpline(sketch, "E2675", {"points": [v(-80.54, -5.26) * mm, v(-80.18, -5.4) * mm, v(-79.83, -5.54) * mm, v(-79.47, -5.67) * mm]});
            skFitSpline(sketch, "E2676", {"points": [v(-79.47, -5.67) * mm, v(-79.16, -5.78) * mm, v(-78.84, -5.86) * mm, v(-78.54, -5.97) * mm]});
            skFitSpline(sketch, "E2677", {"points": [v(-78.54, -5.97) * mm, v(-78.29, -6.07) * mm, v(-78.1, -5.98) * mm, v(-77.91, -5.8) * mm]});
            skFitSpline(sketch, "E2678", {"points": [v(-77.91, -5.8) * mm, v(-78.07, -5.75) * mm, v(-78.2, -5.7) * mm, v(-78.34, -5.64) * mm]});
            skFitSpline(sketch, "E2679", {"points": [v(-78.34, -5.64) * mm, v(-78.54, -5.56) * mm, v(-78.74, -5.48) * mm, v(-78.93, -5.38) * mm]});
            skFitSpline(sketch, "E2680", {"points": [v(-78.93, -5.38) * mm, v(-79.2, -5.24) * mm, v(-79.3, -4.94) * mm, v(-79.15, -4.69) * mm]});
            skFitSpline(sketch, "E2681", {"points": [v(-79.15, -4.69) * mm, v(-79, -4.44) * mm, v(-78.73, -4.39) * mm, v(-78.46, -4.51) * mm]});
            skFitSpline(sketch, "E2682", {"points": [v(-78.46, -4.51) * mm, v(-78.08, -4.69) * mm, v(-77.7, -4.84) * mm, v(-77.32, -5) * mm]});
            skFitSpline(sketch, "E2683", {"points": [v(-77.32, -5) * mm, v(-77.16, -5.07) * mm, v(-77, -5.2) * mm, v(-76.83, -5.2) * mm]});
            skFitSpline(sketch, "E2684", {"points": [v(-76.83, -5.2) * mm, v(-76.67, -5.2) * mm, v(-76.51, -5.07) * mm, v(-76.36, -5) * mm]});
            skFitSpline(sketch, "E2685", {"points": [v(-76.36, -5) * mm, v(-76, -4.82) * mm, v(-75.68, -4.58) * mm, v(-75.34, -4.34) * mm]});
            skFitSpline(sketch, "E2686", {"points": [v(-75.34, -4.34) * mm, v(-76.56, -3.59) * mm, v(-77.75, -2.85) * mm, v(-78.94, -2.1) * mm]});
            skFitSpline(sketch, "E2687", {"points": [v(-78.94, -2.1) * mm, v(-79.55, -2.32) * mm, v(-80.18, -2.48) * mm, v(-80.74, -2.81) * mm]});
            skFitSpline(sketch, "E2688", {"points": [v(-80.74, -2.81) * mm, v(-80.84, -2.87) * mm, v(-80.96, -2.91) * mm, v(-81.08, -2.92) * mm]});
            skFitSpline(sketch, "E2689", {"points": [v(-81.08, -2.92) * mm, v(-81.3, -2.94) * mm, v(-81.48, -2.78) * mm, v(-81.54, -2.57) * mm]});
            skFitSpline(sketch, "E2690", {"points": [v(-81.54, -2.57) * mm, v(-81.6, -2.36) * mm, v(-81.52, -2.14) * mm, v(-81.31, -2.02) * mm]});
            skFitSpline(sketch, "E2691", {"points": [v(-81.31, -2.02) * mm, v(-81.1, -1.9) * mm, v(-80.88, -1.77) * mm, v(-80.65, -1.68) * mm]});
            skFitSpline(sketch, "E2692", {"points": [v(-80.65, -1.68) * mm, v(-80.12, -1.47) * mm, v(-79.58, -1.28) * mm, v(-79.03, -1.1) * mm]});
            skFitSpline(sketch, "E2693", {"points": [v(-79.03, -1.1) * mm, v(-78.8, -1.01) * mm, v(-78.57, -1.04) * mm, v(-78.4, -1.26) * mm]});
            skFitSpline(sketch, "E2694", {"points": [v(-78.4, -1.26) * mm, v(-78.38, -1.3) * mm, v(-78.35, -1.32) * mm, v(-78.32, -1.34) * mm]});
            skFitSpline(sketch, "E2695", {"points": [v(-78.32, -1.34) * mm, v(-77.6, -1.78) * mm, v(-76.9, -2.23) * mm, v(-76.18, -2.67) * mm]});
            skFitSpline(sketch, "E2696", {"points": [v(-76.18, -2.67) * mm, v(-75.88, -2.86) * mm, v(-75.57, -3.05) * mm, v(-75.27, -3.24) * mm]});
            skFitSpline(sketch, "E2697", {"points": [v(-75.27, -3.24) * mm, v(-75.16, -3.31) * mm, v(-75.05, -3.37) * mm, v(-74.9, -3.45) * mm]});
            skFitSpline(sketch, "E2698", {"points": [v(-74.9, -3.45) * mm, v(-74.88, -3.28) * mm, v(-74.89, -3.13) * mm, v(-74.9, -2.98) * mm]});
            skFitSpline(sketch, "E2699", {"points": [v(-74.9, -2.98) * mm, v(-74.9, -2.75) * mm, v(-74.92, -2.52) * mm, v(-74.94, -2.3) * mm]});
            skFitSpline(sketch, "E2700", {"points": [v(-74.94, -2.3) * mm, v(-74.97, -1.96) * mm, v(-75, -1.62) * mm, v(-75.02, -1.3) * mm]});
            skFitSpline(sketch, "E2701", {"points": [v(-75.02, -1.3) * mm, v(-75.03, -0.7) * mm, v(-75.04, -0.1) * mm, v(-75.03, 0.5) * mm]});
            skFitSpline(sketch, "E2702", {"points": [v(-75.03, 0.5) * mm, v(-75.02, 0.93) * mm, v(-75, 1.35) * mm, v(-74.97, 1.77) * mm]});
            skFitSpline(sketch, "E2703", {"points": [v(-74.97, 1.77) * mm, v(-74.94, 2.3) * mm, v(-74.91, 2.85) * mm, v(-74.88, 3.4) * mm]});
            skFitSpline(sketch, "E2704", {"points": [v(-74.88, 3.4) * mm, v(-75.01, 3.42) * mm, v(-75.1, 3.35) * mm, v(-75.18, 3.3) * mm]});
            skFitSpline(sketch, "E2705", {"points": [v(-75.18, 3.3) * mm, v(-75.96, 2.81) * mm, v(-76.74, 2.33) * mm, v(-77.52, 1.85) * mm]});
            skFitSpline(sketch, "E2706", {"points": [v(-77.52, 1.85) * mm, v(-77.78, 1.68) * mm, v(-78.04, 1.51) * mm, v(-78.3, 1.34) * mm]});
            skFitSpline(sketch, "E2707", {"points": [v(-78.3, 1.34) * mm, v(-78.34, 1.31) * mm, v(-78.38, 1.28) * mm, v(-78.41, 1.24) * mm]});
            skFitSpline(sketch, "E2708", {"points": [v(-78.41, 1.24) * mm, v(-78.57, 1.04) * mm, v(-78.8, 1) * mm, v(-79.01, 1.08) * mm]});
            skFitSpline(sketch, "E2709", {"points": [v(-79.01, 1.08) * mm, v(-79.75, 1.36) * mm, v(-80.53, 1.55) * mm, v(-81.22, 1.95) * mm]});
            skFitSpline(sketch, "E2710", {"points": [v(-81.22, 1.95) * mm, v(-81.53, 2.13) * mm, v(-81.65, 2.4) * mm, v(-81.5, 2.66) * mm]});
            skFitSpline(sketch, "E2711", {"points": [v(-81.5, 2.66) * mm, v(-81.35, 2.94) * mm, v(-81.01, 2.98) * mm, v(-80.75, 2.82) * mm]});
            skFitSpline(sketch, "E2712", {"points": [v(-80.75, 2.82) * mm, v(-80.23, 2.5) * mm, v(-79.63, 2.33) * mm, v(-79.05, 2.13) * mm]});
            skFitSpline(sketch, "E2713", {"points": [v(-79.05, 2.13) * mm, v(-79, 2.11) * mm, v(-78.92, 2.12) * mm, v(-78.87, 2.14) * mm]});
            skFitSpline(sketch, "E2714", {"points": [v(-78.87, 2.14) * mm, v(-78.74, 2.2) * mm, v(-78.62, 2.28) * mm, v(-78.5, 2.36) * mm]});
            skFitSpline(sketch, "E2715", {"points": [v(-78.5, 2.36) * mm, v(-77.83, 2.77) * mm, v(-77.17, 3.18) * mm, v(-76.5, 3.6) * mm]});
            skFitSpline(sketch, "E2716", {"points": [v(-76.5, 3.6) * mm, v(-76.12, 3.83) * mm, v(-75.75, 4.08) * mm, v(-75.35, 4.34) * mm]});
            skFitSpline(sketch, "E2717", {"points": [v(-75.35, 4.34) * mm, v(-75.53, 4.46) * mm, v(-75.7, 4.6) * mm, v(-75.89, 4.7) * mm]});
            skFitSpline(sketch, "E2718", {"points": [v(-75.89, 4.7) * mm, v(-76.16, 4.87) * mm, v(-76.44, 5.02) * mm, v(-76.73, 5.17) * mm]});
            skFitSpline(sketch, "E2719", {"points": [v(-76.73, 5.17) * mm, v(-76.78, 5.2) * mm, v(-76.87, 5.2) * mm, v(-76.93, 5.17) * mm]});
            skFitSpline(sketch, "E2720", {"points": [v(-76.93, 5.17) * mm, v(-77.46, 4.94) * mm, v(-77.98, 4.71) * mm, v(-78.5, 4.48) * mm]});
            skFitSpline(sketch, "E2721", {"points": [v(-78.5, 4.48) * mm, v(-78.74, 4.38) * mm, v(-79, 4.45) * mm, v(-79.14, 4.66) * mm]});
            skFitSpline(sketch, "E2722", {"points": [v(-79.14, 4.66) * mm, v(-79.27, 4.88) * mm, v(-79.23, 5.15) * mm, v(-79.03, 5.3) * mm]});
            skFitSpline(sketch, "E2723", {"points": [v(-79.03, 5.3) * mm, v(-78.96, 5.36) * mm, v(-78.88, 5.4) * mm, v(-78.8, 5.44) * mm]});
            skFitSpline(sketch, "E2724", {"points": [v(-78.8, 5.44) * mm, v(-78.51, 5.56) * mm, v(-78.22, 5.68) * mm, v(-77.92, 5.8) * mm]});
            skFitSpline(sketch, "E2725", {"points": [v(-77.92, 5.8) * mm, v(-78.1, 5.95) * mm, v(-78.25, 6.06) * mm, v(-78.5, 5.97) * mm]});
            skFitSpline(sketch, "E2726", {"points": [v(-78.5, 5.97) * mm, v(-79.16, 5.73) * mm, v(-79.85, 5.5) * mm, v(-80.52, 5.26) * mm]});
            skFitSpline(sketch, "E2727", {"points": [v(-80.52, 5.26) * mm, v(-80.82, 5.15) * mm, v(-81.1, 5.24) * mm, v(-81.22, 5.52) * mm]});
            skFitSpline(sketch, "E2728", {"points": [v(-81.22, 5.52) * mm, v(-81.3, 5.74) * mm, v(-81.22, 6) * mm, v(-80.99, 6.11) * mm]});
            skFitSpline(sketch, "E2729", {"points": [v(-80.99, 6.11) * mm, v(-80.75, 6.23) * mm, v(-80.5, 6.32) * mm, v(-80.26, 6.42) * mm]});
            skFitSpline(sketch, "E2730", {"points": [v(-80.26, 6.42) * mm, v(-80, 6.51) * mm, v(-79.73, 6.6) * mm, v(-79.44, 6.7) * mm]});
            skFitSpline(sketch, "E2731", {"points": [v(-79.44, 6.7) * mm, v(-79.61, 6.83) * mm, v(-79.76, 6.91) * mm, v(-79.97, 6.9) * mm]});
            skFitSpline(sketch, "E2732", {"points": [v(-79.97, 6.9) * mm, v(-80.7, 6.83) * mm, v(-81.4, 6.67) * mm, v(-82.11, 6.51) * mm]});
            skFitSpline(sketch, "E2733", {"points": [v(-82.11, 6.51) * mm, v(-82.26, 6.48) * mm, v(-82.4, 6.45) * mm, v(-82.56, 6.45) * mm]});
            skFitSpline(sketch, "E2734", {"points": [v(-82.56, 6.45) * mm, v(-82.81, 6.45) * mm, v(-83, 6.64) * mm, v(-83.03, 6.88) * mm]});
            skFitSpline(sketch, "E2735", {"points": [v(-83.03, 6.88) * mm, v(-83.05, 7.1) * mm, v(-82.9, 7.35) * mm, v(-82.66, 7.4) * mm]});
            skFitSpline(sketch, "E2736", {"points": [v(-82.66, 7.4) * mm, v(-82.03, 7.53) * mm, v(-81.4, 7.65) * mm, v(-80.76, 7.78) * mm]});
            skFitSpline(sketch, "E2737", {"points": [v(-80.76, 7.78) * mm, v(-80.61, 7.8) * mm, v(-80.46, 7.82) * mm, v(-80.3, 7.84) * mm]});
            skFitSpline(sketch, "E2738", {"points": [v(-80.3, 7.84) * mm, v(-80.32, 7.92) * mm, v(-80.34, 7.98) * mm, v(-80.36, 8.04) * mm]});
            skFitSpline(sketch, "E2739", {"points": [v(-80.36, 8.04) * mm, v(-80.56, 8.61) * mm, v(-80.77, 9.2) * mm, v(-80.97, 9.77) * mm]});
            skFitSpline(sketch, "E2740", {"points": [v(-80.97, 9.77) * mm, v(-81, 9.88) * mm, v(-81.03, 10) * mm, v(-81.08, 10.1) * mm]});
            skFitSpline(sketch, "E2741", {"points": [v(-81.08, 10.1) * mm, v(-81.17, 10.3) * mm, v(-81.04, 10.6) * mm, v(-80.83, 10.7) * mm]});
            skFitSpline(sketch, "E2742", {"points": [v(-80.83, 10.7) * mm, v(-80.6, 10.8) * mm, v(-80.34, 10.72) * mm, v(-80.2, 10.5) * mm]});
            skFitSpline(sketch, "E2743", {"points": [v(-80.2, 10.5) * mm, v(-80.15, 10.4) * mm, v(-80.1, 10.28) * mm, v(-80.07, 10.17) * mm]});
            skFitSpline(sketch, "E2744", {"points": [v(-80.07, 10.17) * mm, v(-79.85, 9.46) * mm, v(-79.62, 8.75) * mm, v(-79.32, 8.07) * mm]});
            skFitSpline(sketch, "E2745", {"points": [v(-79.32, 8.07) * mm, v(-79.23, 7.88) * mm, v(-79.1, 7.78) * mm, v(-78.88, 7.68) * mm]});
            skFitSpline(sketch, "E2746", {"points": [v(-78.88, 7.68) * mm, v(-78.9, 7.8) * mm, v(-78.91, 7.9) * mm, v(-78.93, 8) * mm]});
            skFitSpline(sketch, "E2747", {"points": [v(-78.93, 8) * mm, v(-79, 8.37) * mm, v(-79.07, 8.73) * mm, v(-79.13, 9.1) * mm]});
            skFitSpline(sketch, "E2748", {"points": [v(-79.13, 9.1) * mm, v(-79.15, 9.23) * mm, v(-79.14, 9.36) * mm, v(-79.1, 9.48) * mm]});
            skFitSpline(sketch, "E2749", {"points": [v(-79.1, 9.48) * mm, v(-79.05, 9.7) * mm, v(-78.87, 9.81) * mm, v(-78.64, 9.8) * mm]});
            skFitSpline(sketch, "E2750", {"points": [v(-78.64, 9.8) * mm, v(-78.41, 9.8) * mm, v(-78.24, 9.68) * mm, v(-78.2, 9.45) * mm]});
            skFitSpline(sketch, "E2751", {"points": [v(-78.2, 9.45) * mm, v(-78.15, 9.26) * mm, v(-78.14, 9.07) * mm, v(-78.1, 8.88) * mm]});
            skFitSpline(sketch, "E2752", {"points": [v(-78.1, 8.88) * mm, v(-78, 8.35) * mm, v(-77.88, 7.82) * mm, v(-77.79, 7.29) * mm]});
            skFitSpline(sketch, "E2753", {"points": [v(-77.79, 7.29) * mm, v(-77.74, 7.02) * mm, v(-77.59, 6.89) * mm, v(-77.33, 6.81) * mm]});
            skFitSpline(sketch, "E2754", {"points": [v(-77.33, 6.81) * mm, v(-77.35, 6.98) * mm, v(-77.38, 7.14) * mm, v(-77.4, 7.3) * mm]});
            skFitSpline(sketch, "E2755", {"points": [v(-77.4, 7.3) * mm, v(-77.43, 7.5) * mm, v(-77.46, 7.72) * mm, v(-77.46, 7.94) * mm]});
            skFitSpline(sketch, "E2756", {"points": [v(-77.46, 7.94) * mm, v(-77.47, 8.23) * mm, v(-77.27, 8.43) * mm, v(-77, 8.44) * mm]});
            skFitSpline(sketch, "E2757", {"points": [v(-77, 8.44) * mm, v(-76.7, 8.45) * mm, v(-76.5, 8.25) * mm, v(-76.48, 7.95) * mm]});
            skFitSpline(sketch, "E2758", {"points": [v(-76.48, 7.95) * mm, v(-76.43, 7.42) * mm, v(-76.37, 6.9) * mm, v(-76.31, 6.36) * mm]});
            skFitSpline(sketch, "E2759", {"points": [v(-76.31, 6.36) * mm, v(-76.3, 6.22) * mm, v(-76.23, 6.13) * mm, v(-76.1, 6.04) * mm]});
            skFitSpline(sketch, "E2760", {"points": [v(-76.1, 6.04) * mm, v(-75.7, 5.75) * mm, v(-75.24, 5.53) * mm, v(-74.76, 5.31) * mm]});
            skFitSpline(sketch, "E2761", {"points": [v(-74.76, 5.31) * mm, v(-74.76, 5.47) * mm, v(-74.76, 5.61) * mm, v(-74.76, 5.75) * mm]});
            skFitSpline(sketch, "E2762", {"points": [v(-74.76, 5.75) * mm, v(-74.74, 6.1) * mm, v(-74.71, 6.43) * mm, v(-74.7, 6.78) * mm]});
            skFitSpline(sketch, "E2763", {"points": [v(-74.7, 6.78) * mm, v(-74.7, 7.13) * mm, v(-74.7, 7.5) * mm, v(-74.69, 7.85) * mm]});
            skFitSpline(sketch, "E2764", {"points": [v(-74.69, 7.85) * mm, v(-74.68, 8.36) * mm, v(-74.66, 8.87) * mm, v(-74.63, 9.38) * mm]});
            skFitSpline(sketch, "E2765", {"points": [v(-74.63, 9.38) * mm, v(-74.63, 9.51) * mm, v(-74.68, 9.6) * mm, v(-74.78, 9.68) * mm]});
            skFitSpline(sketch, "E2766", {"points": [v(-74.78, 9.68) * mm, v(-75.25, 10.08) * mm, v(-75.7, 10.5) * mm, v(-76.23, 10.81) * mm]});
            skFitSpline(sketch, "E2767", {"points": [v(-76.23, 10.81) * mm, v(-76.44, 10.93) * mm, v(-76.51, 11.12) * mm, v(-76.46, 11.34) * mm]});
            skFitSpline(sketch, "E2768", {"points": [v(-76.46, 11.34) * mm, v(-76.42, 11.54) * mm, v(-76.28, 11.66) * mm, v(-76.1, 11.71) * mm]});
            skFitSpline(sketch, "E2769", {"points": [v(-76.1, 11.71) * mm, v(-75.94, 11.75) * mm, v(-75.8, 11.69) * mm, v(-75.68, 11.61) * mm]});
            skFitSpline(sketch, "E2770", {"points": [v(-75.68, 11.61) * mm, v(-75.28, 11.37) * mm, v(-74.9, 11.1) * mm, v(-74.55, 10.77) * mm]});
            skFitSpline(sketch, "E2771", {"points": [v(-74.55, 10.77) * mm, v(-74.32, 10.56) * mm, v(-74.08, 10.37) * mm, v(-73.84, 10.17) * mm]});
            skFitSpline(sketch, "E2772", {"points": [v(-73.84, 10.17) * mm, v(-73.62, 10) * mm, v(-73.54, 9.78) * mm, v(-73.63, 9.51) * mm]});
            skFitSpline(sketch, "E2773", {"points": [v(-73.63, 9.51) * mm, v(-73.67, 9.4) * mm, v(-73.67, 9.3) * mm, v(-73.68, 9.18) * mm]});
            skFitSpline(sketch, "E2774", {"points": [v(-73.68, 9.18) * mm, v(-73.7, 8.32) * mm, v(-73.72, 7.46) * mm, v(-73.74, 6.6) * mm]});
            skFitSpline(sketch, "E2775", {"points": [v(-73.74, 6.6) * mm, v(-73.75, 6.26) * mm, v(-73.77, 5.93) * mm, v(-73.79, 5.6) * mm]});
            skFitSpline(sketch, "E2776", {"points": [v(-73.79, 5.6) * mm, v(-73.8, 5.53) * mm, v(-73.78, 5.47) * mm, v(-73.78, 5.38) * mm]});
            skFitSpline(sketch, "E2777", {"points": [v(-73.78, 5.38) * mm, v(-73.7, 5.43) * mm, v(-73.63, 5.46) * mm, v(-73.57, 5.5) * mm]});
            skFitSpline(sketch, "E2778", {"points": [v(-73.57, 5.5) * mm, v(-73.06, 5.83) * mm, v(-72.55, 6.18) * mm, v(-72.03, 6.5) * mm]});
            skFitSpline(sketch, "E2779", {"points": [v(-72.03, 6.5) * mm, v(-71.4, 6.91) * mm, v(-70.75, 7.32) * mm, v(-70.07, 7.66) * mm]});
            skFitSpline(sketch, "E2780", {"points": [v(-70.07, 7.66) * mm, v(-69.36, 8) * mm, v(-68.65, 8.38) * mm, v(-67.94, 8.74) * mm]});
            skFitSpline(sketch, "E2781", {"points": [v(-67.94, 8.74) * mm, v(-67.9, 8.76) * mm, v(-67.87, 8.79) * mm, v(-67.81, 8.82) * mm]});
            skFitSpline(sketch, "E2782", {"points": [v(-67.81, 8.82) * mm, v(-67.93, 8.9) * mm, v(-68.02, 8.96) * mm, v(-68.12, 9.02) * mm]});
            skFitSpline(sketch, "E2783", {"points": [v(-68.12, 9.02) * mm, v(-68.9, 9.44) * mm, v(-69.68, 9.86) * mm, v(-70.46, 10.28) * mm]});
            skFitSpline(sketch, "E2784", {"points": [v(-70.46, 10.28) * mm, v(-70.75, 10.43) * mm, v(-71.05, 10.58) * mm, v(-71.34, 10.72) * mm]});
            skFitSpline(sketch, "E2785", {"points": [v(-71.34, 10.72) * mm, v(-71.4, 10.75) * mm, v(-71.46, 10.76) * mm, v(-71.52, 10.78) * mm]});
            skFitSpline(sketch, "E2786", {"points": [v(-71.52, 10.78) * mm, v(-71.72, 10.83) * mm, v(-71.86, 10.95) * mm, v(-71.9, 11.14) * mm]});
            skFitSpline(sketch, "E2787", {"points": [v(-71.9, 11.14) * mm, v(-72.04, 11.97) * mm, v(-72.28, 12.79) * mm, v(-72.25, 13.65) * mm]});
            skFitSpline(sketch, "E2788", {"points": [v(-72.25, 13.65) * mm, v(-72.25, 13.95) * mm, v(-72.07, 14.14) * mm, v(-71.79, 14.15) * mm]});
            skFitSpline(sketch, "E2789", {"points": [v(-71.79, 14.15) * mm, v(-71.51, 14.15) * mm, v(-71.32, 13.98) * mm, v(-71.3, 13.7) * mm]});
            skFitSpline(sketch, "E2790", {"points": [v(-71.3, 13.7) * mm, v(-71.27, 13.42) * mm, v(-71.27, 13.14) * mm, v(-71.23, 12.87) * mm]});
            skFitSpline(sketch, "E2791", {"points": [v(-71.23, 12.87) * mm, v(-71.17, 12.5) * mm, v(-71.1, 12.13) * mm, v(-71.02, 11.76) * mm]});
            skFitSpline(sketch, "E2792", {"points": [v(-71.02, 11.76) * mm, v(-71, 11.7) * mm, v(-70.95, 11.64) * mm, v(-70.9, 11.6) * mm]});
            skFitSpline(sketch, "E2793", {"points": [v(-70.9, 11.6) * mm, v(-70.8, 11.53) * mm, v(-70.68, 11.47) * mm, v(-70.57, 11.4) * mm]});
            skFitSpline(sketch, "E2794", {"points": [v(-70.57, 11.4) * mm, v(-69.58, 10.88) * mm, v(-68.58, 10.36) * mm, v(-67.58, 9.84) * mm]});
            skFitSpline(sketch, "E2795", {"points": [v(-67.58, 9.84) * mm, v(-67.48, 9.78) * mm, v(-67.38, 9.72) * mm, v(-67.27, 9.65) * mm]});
            skFitSpline(sketch, "E2796", {"points": [v(-67.27, 9.65) * mm, v(-67.18, 10.2) * mm, v(-67.2, 10.74) * mm, v(-67.22, 11.27) * mm]});
            skFitSpline(sketch, "E2797", {"points": [v(-67.22, 11.27) * mm, v(-67.22, 11.33) * mm, v(-67.26, 11.4) * mm, v(-67.3, 11.43) * mm]});
            skFitSpline(sketch, "E2798", {"points": [v(-67.3, 11.43) * mm, v(-67.76, 11.77) * mm, v(-68.21, 12.11) * mm, v(-68.68, 12.44) * mm]});
            skFitSpline(sketch, "E2799", {"points": [v(-68.68, 12.44) * mm, v(-68.92, 12.61) * mm, v(-69, 12.88) * mm, v(-68.86, 13.13) * mm]});
            skFitSpline(sketch, "E2800", {"points": [v(-68.86, 13.13) * mm, v(-68.72, 13.37) * mm, v(-68.43, 13.45) * mm, v(-68.18, 13.3) * mm]});
            skFitSpline(sketch, "E2801", {"points": [v(-68.18, 13.3) * mm, v(-68, 13.18) * mm, v(-67.83, 13.05) * mm, v(-67.65, 12.91) * mm]});
            skFitSpline(sketch, "E2802", {"points": [v(-67.65, 12.91) * mm, v(-67.53, 12.82) * mm, v(-67.42, 12.73) * mm, v(-67.28, 12.61) * mm]});
            skFitSpline(sketch, "E2803", {"points": [v(-67.28, 12.61) * mm, v(-67.24, 12.84) * mm, v(-67.2, 13.02) * mm, v(-67.4, 13.18) * mm]});
            skFitSpline(sketch, "E2804", {"points": [v(-67.4, 13.18) * mm, v(-67.95, 13.65) * mm, v(-68.5, 14.13) * mm, v(-69.05, 14.6) * mm]});
            skFitSpline(sketch, "E2805", {"points": [v(-69.05, 14.6) * mm, v(-69.22, 14.74) * mm, v(-69.31, 14.9) * mm, v(-69.27, 15.12) * mm]});
            skFitSpline(sketch, "E2806", {"points": [v(-69.27, 15.12) * mm, v(-69.23, 15.32) * mm, v(-69.1, 15.44) * mm, v(-68.9, 15.5) * mm]});
            skFitSpline(sketch, "E2807", {"points": [v(-68.9, 15.5) * mm, v(-68.76, 15.54) * mm, v(-68.63, 15.5) * mm, v(-68.52, 15.42) * mm]});
            skFitSpline(sketch, "E2808", {"points": [v(-68.52, 15.42) * mm, v(-68.32, 15.28) * mm, v(-68.12, 15.13) * mm, v(-67.93, 14.97) * mm]});
            skFitSpline(sketch, "E2809", {"points": [v(-67.93, 14.97) * mm, v(-67.72, 14.8) * mm, v(-67.5, 14.6) * mm, v(-67.28, 14.4) * mm]});
            skFitSpline(sketch, "E2810", {"points": [v(-67.28, 14.4) * mm, v(-67.23, 14.6) * mm, v(-67.22, 14.76) * mm, v(-67.34, 14.93) * mm]});
            skFitSpline(sketch, "E2811", {"points": [v(-67.34, 14.93) * mm, v(-67.78, 15.55) * mm, v(-68.3, 16.1) * mm, v(-68.81, 16.66) * mm]});
            skFitSpline(sketch, "E2812", {"points": [v(-68.81, 16.66) * mm, v(-68.93, 16.8) * mm, v(-69.06, 16.92) * mm, v(-69.08, 17.1) * mm]});
            skFitSpline(sketch, "E2813", {"points": [v(-69.08, 17.1) * mm, v(-69.12, 17.35) * mm, v(-69.03, 17.53) * mm, v(-68.83, 17.62) * mm]});
            skFitSpline(sketch, "E2814", {"points": [v(-68.83, 17.62) * mm, v(-68.63, 17.72) * mm, v(-68.4, 17.68) * mm, v(-68.24, 17.5) * mm]});
            skFitSpline(sketch, "E2815", {"points": [v(-68.24, 17.5) * mm, v(-67.97, 17.2) * mm, v(-67.7, 16.9) * mm, v(-67.43, 16.59) * mm]});
            skFitSpline(sketch, "E2816", {"points": [v(-67.43, 16.59) * mm, v(-67.18, 16.3) * mm, v(-66.95, 16.01) * mm, v(-66.67, 15.68) * mm]});
            skFitSpline(sketch, "E2817", {"points": [v(-66.67, 15.68) * mm, v(-66.64, 15.73) * mm, v(-66.62, 15.78) * mm, v(-66.59, 15.82) * mm]});
            skFitSpline(sketch, "E2818", {"points": [v(-66.59, 15.82) * mm, v(-66.16, 16.31) * mm, v(-65.74, 16.8) * mm, v(-65.32, 17.3) * mm]});
            skFitSpline(sketch, "E2819", {"points": [v(-65.32, 17.3) * mm, v(-65.26, 17.36) * mm, v(-65.2, 17.43) * mm, v(-65.15, 17.5) * mm]});
            skFitSpline(sketch, "E2820", {"points": [v(-65.15, 17.5) * mm, v(-64.96, 17.7) * mm, v(-64.69, 17.73) * mm, v(-64.48, 17.58) * mm]});
            skFitSpline(sketch, "E2821", {"points": [v(-64.48, 17.58) * mm, v(-64.27, 17.43) * mm, v(-64.23, 17.16) * mm, v(-64.37, 16.92) * mm]});
            skFitSpline(sketch, "E2822", {"points": [v(-64.37, 16.92) * mm, v(-64.43, 16.83) * mm, v(-64.5, 16.75) * mm, v(-64.56, 16.67) * mm]});
            skFitSpline(sketch, "E2823", {"points": [v(-64.56, 16.67) * mm, v(-65.06, 16.14) * mm, v(-65.55, 15.6) * mm, v(-65.98, 15.02) * mm]});
            skFitSpline(sketch, "E2824", {"points": [v(-65.98, 15.02) * mm, v(-66.11, 14.83) * mm, v(-66.18, 14.66) * mm, v(-66.13, 14.42) * mm]});
            skFitSpline(sketch, "E2825", {"points": [v(-66.13, 14.42) * mm, v(-66.08, 14.45) * mm, v(-66.03, 14.47) * mm, v(-66, 14.5) * mm]});
            skFitSpline(sketch, "E2826", {"points": [v(-66, 14.5) * mm, v(-65.71, 14.74) * mm, v(-65.43, 14.99) * mm, v(-65.14, 15.23) * mm]});
            skFitSpline(sketch, "E2827", {"points": [v(-65.14, 15.23) * mm, v(-65.05, 15.3) * mm, v(-64.96, 15.36) * mm, v(-64.87, 15.42) * mm]});
            skFitSpline(sketch, "E2828", {"points": [v(-64.87, 15.42) * mm, v(-64.61, 15.57) * mm, v(-64.34, 15.52) * mm, v(-64.19, 15.3) * mm]});
            skFitSpline(sketch, "E2829", {"points": [v(-64.19, 15.3) * mm, v(-64.03, 15.07) * mm, v(-64.1, 14.8) * mm, v(-64.34, 14.6) * mm]});
            skFitSpline(sketch, "E2830", {"points": [v(-64.34, 14.6) * mm, v(-64.6, 14.4) * mm, v(-64.86, 14.19) * mm, v(-65.12, 13.97) * mm]});
            skFitSpline(sketch, "E2831", {"points": [v(-65.12, 13.97) * mm, v(-65.39, 13.74) * mm, v(-65.65, 13.5) * mm, v(-65.92, 13.25) * mm]});
            skFitSpline(sketch, "E2832", {"points": [v(-65.92, 13.25) * mm, v(-66.17, 13.02) * mm, v(-66.17, 13.02) * mm, v(-66.13, 12.62) * mm]});
            skFitSpline(sketch, "E2833", {"points": [v(-66.13, 12.62) * mm, v(-66.07, 12.66) * mm, v(-66.01, 12.69) * mm, v(-65.97, 12.73) * mm]});
            skFitSpline(sketch, "E2834", {"points": [v(-65.97, 12.73) * mm, v(-65.76, 12.89) * mm, v(-65.55, 13.05) * mm, v(-65.34, 13.2) * mm]});
            skFitSpline(sketch, "E2835", {"points": [v(-65.34, 13.2) * mm, v(-65.28, 13.25) * mm, v(-65.22, 13.3) * mm, v(-65.16, 13.32) * mm]});
            skFitSpline(sketch, "E2836", {"points": [v(-65.16, 13.32) * mm, v(-64.91, 13.44) * mm, v(-64.64, 13.35) * mm, v(-64.52, 13.12) * mm]});
            skFitSpline(sketch, "E2837", {"points": [v(-64.52, 13.12) * mm, v(-64.4, 12.89) * mm, v(-64.47, 12.62) * mm, v(-64.68, 12.46) * mm]});
            skFitSpline(sketch, "E2838", {"points": [v(-64.68, 12.46) * mm, v(-65.15, 12.12) * mm, v(-65.6, 11.78) * mm, v(-66.07, 11.44) * mm]});
            skFitSpline(sketch, "E2839", {"points": [v(-66.07, 11.44) * mm, v(-66.12, 11.4) * mm, v(-66.15, 11.32) * mm, v(-66.16, 11.26) * mm]});
            skFitSpline(sketch, "E2840", {"points": [v(-66.16, 11.26) * mm, v(-66.23, 10.73) * mm, v(-66.18, 10.2) * mm, v(-66.13, 9.65) * mm]});
            skFitSpline(sketch, "E2841", {"points": [v(-66.13, 9.65) * mm, v(-64.87, 10.32) * mm, v(-63.63, 10.99) * mm, v(-62.38, 11.66) * mm]});
            skFitSpline(sketch, "E2842", {"points": [v(-62.38, 11.66) * mm, v(-62.3, 12.26) * mm, v(-62.09, 12.85) * mm, v(-62.11, 13.47) * mm]});
            skFitSpline(sketch, "E2843", {"points": [v(-62.11, 13.47) * mm, v(-62.12, 13.55) * mm, v(-62.1, 13.63) * mm, v(-62.08, 13.7) * mm]});
            skFitSpline(sketch, "E2844", {"points": [v(-62.08, 13.7) * mm, v(-62.05, 14) * mm, v(-61.87, 14.16) * mm, v(-61.59, 14.15) * mm]});
            skFitSpline(sketch, "E2845", {"points": [v(-61.59, 14.15) * mm, v(-61.32, 14.14) * mm, v(-61.13, 13.94) * mm, v(-61.13, 13.67) * mm]});
            skFitSpline(sketch, "E2846", {"points": [v(-61.13, 13.67) * mm, v(-61.12, 13.56) * mm, v(-61.16, 13.46) * mm, v(-61.15, 13.36) * mm]});
            skFitSpline(sketch, "E2847", {"points": [v(-61.15, 13.36) * mm, v(-61.13, 12.62) * mm, v(-61.38, 11.92) * mm, v(-61.47, 11.2) * mm]});
            skFitSpline(sketch, "E2848", {"points": [v(-61.47, 11.2) * mm, v(-61.5, 10.97) * mm, v(-61.65, 10.82) * mm, v(-61.9, 10.77) * mm]});
            skFitSpline(sketch, "E2849", {"points": [v(-61.9, 10.77) * mm, v(-61.95, 10.76) * mm, v(-62, 10.75) * mm, v(-62.05, 10.72) * mm]});
            skFitSpline(sketch, "E2850", {"points": [v(-62.05, 10.72) * mm, v(-62.34, 10.58) * mm, v(-62.62, 10.44) * mm, v(-62.9, 10.29) * mm]});
            skFitSpline(sketch, "E2851", {"points": [v(-62.9, 10.29) * mm, v(-63.7, 9.86) * mm, v(-64.5, 9.43) * mm, v(-65.29, 9) * mm]});
            skFitSpline(sketch, "E2852", {"points": [v(-65.29, 9) * mm, v(-65.38, 8.96) * mm, v(-65.46, 8.9) * mm, v(-65.57, 8.83) * mm]});
            skFitSpline(sketch, "E2853", {"points": [v(-65.57, 8.83) * mm, v(-65.5, 8.79) * mm, v(-65.46, 8.75) * mm, v(-65.4, 8.72) * mm]});
            skFitSpline(sketch, "E2854", {"points": [v(-65.4, 8.72) * mm, v(-64.85, 8.44) * mm, v(-64.3, 8.17) * mm, v(-63.74, 7.89) * mm]});
            skFitSpline(sketch, "E2855", {"points": [v(-63.74, 7.89) * mm, v(-63.34, 7.68) * mm, v(-62.94, 7.48) * mm, v(-62.57, 7.24) * mm]});
            skFitSpline(sketch, "E2856", {"points": [v(-62.57, 7.24) * mm, v(-61.65, 6.68) * mm, v(-60.75, 6.09) * mm, v(-59.84, 5.51) * mm]});
            skFitSpline(sketch, "E2857", {"points": [v(-59.84, 5.51) * mm, v(-59.77, 5.47) * mm, v(-59.7, 5.43) * mm, v(-59.6, 5.38) * mm]});
            skFitSpline(sketch, "E2858", {"points": [v(-59.6, 5.38) * mm, v(-59.57, 5.55) * mm, v(-59.59, 5.7) * mm, v(-59.59, 5.84) * mm]});
            skFitSpline(sketch, "E2859", {"points": [v(-59.59, 5.84) * mm, v(-59.6, 6.34) * mm, v(-59.62, 6.85) * mm, v(-59.64, 7.35) * mm]});
            skFitSpline(sketch, "E2860", {"points": [v(-59.64, 7.35) * mm, v(-59.66, 7.85) * mm, v(-59.69, 8.35) * mm, v(-59.71, 8.85) * mm]});
            skFitSpline(sketch, "E2861", {"points": [v(-59.71, 8.85) * mm, v(-59.72, 8.98) * mm, v(-59.71, 9.1) * mm, v(-59.72, 9.24) * mm]});
            skFitSpline(sketch, "E2862", {"points": [v(-59.72, 9.24) * mm, v(-59.72, 9.33) * mm, v(-59.72, 9.43) * mm, v(-59.75, 9.52) * mm]});
            skFitSpline(sketch, "E2863", {"points": [v(-59.75, 9.52) * mm, v(-59.86, 9.78) * mm, v(-59.77, 9.97) * mm, v(-59.58, 10.14) * mm]});
            skFitSpline(sketch, "E2864", {"points": [v(-59.58, 10.14) * mm, v(-59.43, 10.27) * mm, v(-59.26, 10.4) * mm, v(-59.1, 10.54) * mm]});
            skFitSpline(sketch, "E2865", {"points": [v(-59.1, 10.54) * mm, v(-58.66, 10.93) * mm, v(-58.22, 11.32) * mm, v(-57.7, 11.62) * mm]});
            skFitSpline(sketch, "E2866", {"points": [v(-57.7, 11.62) * mm, v(-57.55, 11.7) * mm, v(-57.4, 11.76) * mm, v(-57.22, 11.69) * mm]});
            skFitSpline(sketch, "E2867", {"points": [v(-57.22, 11.69) * mm, v(-56.87, 11.55) * mm, v(-56.8, 11.12) * mm, v(-57.07, 10.87) * mm]});
            skFitSpline(sketch, "E2868", {"points": [v(-57.07, 10.87) * mm, v(-57.14, 10.81) * mm, v(-57.21, 10.76) * mm, v(-57.3, 10.72) * mm]});
            skFitSpline(sketch, "E2869", {"points": [v(-57.3, 10.72) * mm, v(-57.81, 10.43) * mm, v(-58.22, 10) * mm, v(-58.68, 9.62) * mm]});
            skFitSpline(sketch, "E2870", {"points": [v(-58.68, 9.62) * mm, v(-58.72, 9.58) * mm, v(-58.75, 9.51) * mm, v(-58.75, 9.46) * mm]});
            skFitSpline(sketch, "E2871", {"points": [v(-58.75, 9.46) * mm, v(-58.75, 9.27) * mm, v(-58.74, 9.08) * mm, v(-58.73, 8.88) * mm]});
            skFitSpline(sketch, "E2872", {"points": [v(-58.73, 8.88) * mm, v(-58.73, 8.78) * mm, v(-58.71, 8.68) * mm, v(-58.7, 8.57) * mm]});
            skFitSpline(sketch, "E2873", {"points": [v(-58.7, 8.57) * mm, v(-58.7, 8.08) * mm, v(-58.7, 7.58) * mm, v(-58.68, 7.09) * mm]});
            skFitSpline(sketch, "E2874", {"points": [v(-58.68, 7.09) * mm, v(-58.66, 6.63) * mm, v(-58.64, 6.18) * mm, v(-58.62, 5.73) * mm]});
            skFitSpline(sketch, "E2875", {"points": [v(-58.62, 5.73) * mm, v(-58.62, 5.6) * mm, v(-58.62, 5.47) * mm, v(-58.62, 5.31) * mm]});
            skFitSpline(sketch, "E2876", {"points": [v(-58.62, 5.31) * mm, v(-58.38, 5.43) * mm, v(-58.15, 5.52) * mm, v(-57.94, 5.64) * mm]});
            skFitSpline(sketch, "E2877", {"points": [v(-57.94, 5.64) * mm, v(-57.69, 5.78) * mm, v(-57.45, 5.94) * mm, v(-57.2, 6.1) * mm]});
            skFitSpline(sketch, "E2878", {"points": [v(-57.2, 6.1) * mm, v(-57.13, 6.14) * mm, v(-57.1, 6.2) * mm, v(-57.09, 6.28) * mm]});
            skFitSpline(sketch, "E2879", {"points": [v(-57.09, 6.28) * mm, v(-57.03, 6.85) * mm, v(-56.96, 7.42) * mm, v(-56.9, 8) * mm]});
            skFitSpline(sketch, "E2880", {"points": [v(-56.9, 8) * mm, v(-56.87, 8.26) * mm, v(-56.67, 8.44) * mm, v(-56.4, 8.44) * mm]});
            skFitSpline(sketch, "E2881", {"points": [v(-56.4, 8.44) * mm, v(-56.12, 8.43) * mm, v(-55.92, 8.24) * mm, v(-55.93, 7.96) * mm]});
            skFitSpline(sketch, "E2882", {"points": [v(-55.93, 7.96) * mm, v(-55.94, 7.7) * mm, v(-55.98, 7.44) * mm, v(-56, 7.18) * mm]});
            skFitSpline(sketch, "E2883", {"points": [v(-56, 7.18) * mm, v(-56.02, 7.07) * mm, v(-56.03, 6.96) * mm, v(-56.05, 6.83) * mm]});
            skFitSpline(sketch, "E2884", {"points": [v(-56.05, 6.83) * mm, v(-55.83, 6.9) * mm, v(-55.67, 6.97) * mm, v(-55.62, 7.2) * mm]});
            skFitSpline(sketch, "E2885", {"points": [v(-55.62, 7.2) * mm, v(-55.47, 7.91) * mm, v(-55.29, 8.62) * mm, v(-55.22, 9.34) * mm]});
            skFitSpline(sketch, "E2886", {"points": [v(-55.22, 9.34) * mm, v(-55.19, 9.65) * mm, v(-54.97, 9.83) * mm, v(-54.66, 9.8) * mm]});
            skFitSpline(sketch, "E2887", {"points": [v(-54.66, 9.8) * mm, v(-54.4, 9.78) * mm, v(-54.22, 9.56) * mm, v(-54.26, 9.26) * mm]});
            skFitSpline(sketch, "E2888", {"points": [v(-54.26, 9.26) * mm, v(-54.31, 8.82) * mm, v(-54.4, 8.38) * mm, v(-54.46, 7.94) * mm]});
            skFitSpline(sketch, "E2889", {"points": [v(-54.46, 7.94) * mm, v(-54.48, 7.86) * mm, v(-54.49, 7.79) * mm, v(-54.5, 7.68) * mm]});
            skFitSpline(sketch, "E2890", {"points": [v(-54.5, 7.68) * mm, v(-54.3, 7.77) * mm, v(-54.16, 7.86) * mm, v(-54.07, 8.05) * mm]});
            skFitSpline(sketch, "E2891", {"points": [v(-54.07, 8.05) * mm, v(-53.77, 8.73) * mm, v(-53.54, 9.43) * mm, v(-53.33, 10.14) * mm]});
            skFitSpline(sketch, "E2892", {"points": [v(-53.33, 10.14) * mm, v(-53.3, 10.26) * mm, v(-53.25, 10.37) * mm, v(-53.2, 10.48) * mm]});
            skFitSpline(sketch, "E2893", {"points": [v(-53.2, 10.48) * mm, v(-53.06, 10.72) * mm, v(-52.8, 10.8) * mm, v(-52.56, 10.7) * mm]});
            skFitSpline(sketch, "E2894", {"points": [v(-52.56, 10.7) * mm, v(-52.33, 10.6) * mm, v(-52.23, 10.33) * mm, v(-52.32, 10.07) * mm]});
            skFitSpline(sketch, "E2895", {"points": [v(-52.32, 10.07) * mm, v(-52.56, 9.34) * mm, v(-52.81, 8.6) * mm, v(-53.07, 7.84) * mm]});
            skFitSpline(sketch, "E2896", {"points": [v(-53.07, 7.84) * mm, v(-53.02, 7.83) * mm, v(-52.94, 7.82) * mm, v(-52.87, 7.8) * mm]});
            skFitSpline(sketch, "E2897", {"points": [v(-52.87, 7.8) * mm, v(-52.27, 7.7) * mm, v(-51.68, 7.58) * mm, v(-51.08, 7.47) * mm]});
            skFitSpline(sketch, "E2898", {"points": [v(-51.08, 7.47) * mm, v(-50.98, 7.45) * mm, v(-50.88, 7.43) * mm, v(-50.78, 7.4) * mm]});
            skFitSpline(sketch, "E2899", {"points": [v(-50.78, 7.4) * mm, v(-50.51, 7.36) * mm, v(-50.34, 7.15) * mm, v(-50.36, 6.88) * mm]});
            skFitSpline(sketch, "E2900", {"points": [v(-50.36, 6.88) * mm, v(-50.38, 6.63) * mm, v(-50.57, 6.45) * mm, v(-50.85, 6.45) * mm]});
            skFitSpline(sketch, "E2901", {"points": [v(-50.85, 6.45) * mm, v(-50.96, 6.45) * mm, v(-51.07, 6.47) * mm, v(-51.18, 6.49) * mm]});
            skFitSpline(sketch, "E2902", {"points": [v(-51.18, 6.49) * mm, v(-51.7, 6.6) * mm, v(-52.22, 6.71) * mm, v(-52.75, 6.81) * mm]});
            skFitSpline(sketch, "E2903", {"points": [v(-52.75, 6.81) * mm, v(-52.98, 6.86) * mm, v(-53.22, 6.87) * mm, v(-53.46, 6.9) * mm]});
            skFitSpline(sketch, "E2904", {"points": [v(-53.46, 6.9) * mm, v(-53.64, 6.92) * mm, v(-53.78, 6.82) * mm, v(-53.94, 6.71) * mm]});
            skFitSpline(sketch, "E2905", {"points": [v(-53.94, 6.71) * mm, v(-53.86, 6.68) * mm, v(-53.8, 6.66) * mm, v(-53.75, 6.64) * mm]});
            skFitSpline(sketch, "E2906", {"points": [v(-53.75, 6.64) * mm, v(-53.4, 6.51) * mm, v(-53.06, 6.4) * mm, v(-52.72, 6.26) * mm]});
            skFitSpline(sketch, "E2907", {"points": [v(-52.72, 6.26) * mm, v(-52.61, 6.22) * mm, v(-52.51, 6.18) * mm, v(-52.41, 6.12) * mm]});
            skFitSpline(sketch, "E2908", {"points": [v(-52.41, 6.12) * mm, v(-52.16, 5.98) * mm, v(-52.07, 5.71) * mm, v(-52.2, 5.47) * mm]});
            skFitSpline(sketch, "E2909", {"points": [v(-52.2, 5.47) * mm, v(-52.31, 5.23) * mm, v(-52.57, 5.15) * mm, v(-52.85, 5.25) * mm]});
            skFitSpline(sketch, "E2910", {"points": [v(-52.85, 5.25) * mm, v(-53.3, 5.43) * mm, v(-53.76, 5.6) * mm, v(-54.22, 5.76) * mm]});
            skFitSpline(sketch, "E2911", {"points": [v(-54.22, 5.76) * mm, v(-54.43, 5.83) * mm, v(-54.64, 5.9) * mm, v(-54.86, 5.96) * mm]});
            skFitSpline(sketch, "E2912", {"points": [v(-54.86, 5.96) * mm, v(-55.15, 6.05) * mm, v(-55.2, 6.03) * mm, v(-55.46, 5.8) * mm]});
            skFitSpline(sketch, "E2913", {"points": [v(-55.46, 5.8) * mm, v(-55.17, 5.68) * mm, v(-54.9, 5.57) * mm, v(-54.62, 5.45) * mm]});
            skFitSpline(sketch, "E2914", {"points": [v(-54.62, 5.45) * mm, v(-54.54, 5.42) * mm, v(-54.45, 5.38) * mm, v(-54.38, 5.33) * mm]});
            skFitSpline(sketch, "E2915", {"points": [v(-54.38, 5.33) * mm, v(-54.16, 5.18) * mm, v(-54.1, 4.9) * mm, v(-54.24, 4.67) * mm]});
            skFitSpline(sketch, "E2916", {"points": [v(-54.24, 4.67) * mm, v(-54.37, 4.45) * mm, v(-54.65, 4.38) * mm, v(-54.89, 4.48) * mm]});
            skFitSpline(sketch, "E2917", {"points": [v(-54.89, 4.48) * mm, v(-55.4, 4.72) * mm, v(-55.93, 4.94) * mm, v(-56.45, 5.17) * mm]});
            skFitSpline(sketch, "E2918", {"points": [v(-56.45, 5.17) * mm, v(-56.52, 5.2) * mm, v(-56.59, 5.2) * mm, v(-56.67, 5.17) * mm]});
            skFitSpline(sketch, "E2919", {"points": [v(-56.67, 5.17) * mm, v(-57.14, 4.96) * mm, v(-57.56, 4.67) * mm, v(-57.98, 4.38) * mm]});
            skFitSpline(sketch, "E2920", {"points": [v(-57.98, 4.38) * mm, v(-58, 4.37) * mm, v(-58.01, 4.34) * mm, v(-58.03, 4.32) * mm]});
            skFitSpline(sketch, "E2921", {"points": [v(-58.03, 4.32) * mm, v(-57.4, 3.93) * mm, v(-56.76, 3.54) * mm, v(-56.14, 3.15) * mm]});
            skFitSpline(sketch, "E2922", {"points": [v(-56.14, 3.15) * mm, v(-55.61, 2.83) * mm, v(-55.1, 2.5) * mm, v(-54.57, 2.17) * mm]});
            skFitSpline(sketch, "E2923", {"points": [v(-54.57, 2.17) * mm, v(-54.47, 2.1) * mm, v(-54.4, 2.1) * mm, v(-54.29, 2.14) * mm]});
            skFitSpline(sketch, "E2924", {"points": [v(-54.29, 2.14) * mm, v(-53.7, 2.35) * mm, v(-53.1, 2.53) * mm, v(-52.56, 2.85) * mm]});
            skFitSpline(sketch, "E2925", {"points": [v(-52.56, 2.85) * mm, v(-52.28, 3) * mm, v(-51.98, 2.89) * mm, v(-51.86, 2.61) * mm]});
            skFitSpline(sketch, "E2926", {"points": [v(-51.86, 2.61) * mm, v(-51.76, 2.38) * mm, v(-51.85, 2.13) * mm, v(-52.09, 2) * mm]});
            skFitSpline(sketch, "E2927", {"points": [v(-52.09, 2) * mm, v(-52.44, 1.82) * mm, v(-52.8, 1.66) * mm, v(-53.15, 1.5) * mm]});
            skFitSpline(sketch, "E2928", {"points": [v(-53.15, 1.5) * mm, v(-53.52, 1.36) * mm, v(-53.9, 1.24) * mm, v(-54.28, 1.1) * mm]});
            skFitSpline(sketch, "E2929", {"points": [v(-54.28, 1.1) * mm, v(-54.55, 1) * mm, v(-54.8, 1.01) * mm, v(-55, 1.26) * mm]});
            skFitSpline(sketch, "E2930", {"points": [v(-55, 1.26) * mm, v(-55.02, 1.3) * mm, v(-55.05, 1.32) * mm, v(-55.08, 1.34) * mm]});
            skFitSpline(sketch, "E2931", {"points": [v(-55.08, 1.34) * mm, v(-55.82, 1.8) * mm, v(-56.56, 2.25) * mm, v(-57.3, 2.71) * mm]});
            skFitSpline(sketch, "E2932", {"points": [v(-57.3, 2.71) * mm, v(-57.58, 2.89) * mm, v(-57.85, 3.07) * mm, v(-58.13, 3.24) * mm]});
            skFitSpline(sketch, "E2933", {"points": [v(-58.13, 3.24) * mm, v(-58.23, 3.3) * mm, v(-58.33, 3.36) * mm, v(-58.46, 3.44) * mm]});
            skFitSpline(sketch, "E2934", {"points": [v(-58.46, 3.44) * mm, v(-58.47, 3.35) * mm, v(-58.49, 3.3) * mm, v(-58.48, 3.24) * mm]});
            skFitSpline(sketch, "E2935", {"points": [v(-58.48, 3.24) * mm, v(-58.45, 2.65) * mm, v(-58.42, 2.06) * mm, v(-58.4, 1.47) * mm]});
            skFitSpline(sketch, "E2936", {"points": [v(-58.4, 1.47) * mm, v(-58.37, 0.87) * mm, v(-58.33, 0.27) * mm, v(-58.35, -0.33) * mm]});
            skFitSpline(sketch, "E2937", {"points": [v(-58.35, -0.33) * mm, v(-58.36, -1.03) * mm, v(-58.43, -1.73) * mm, v(-58.46, -2.43) * mm]});
            skFitSpline(sketch, "E2938", {"points": [v(-58.46, -2.43) * mm, v(-58.48, -2.75) * mm, v(-58.47, -3.08) * mm, v(-58.47, -3.44) * mm]});
            skFitSpline(sketch, "E2939", {"points": [v(-58.47, -3.44) * mm, v(-58.38, -3.4) * mm, v(-58.3, -3.36) * mm, v(-58.21, -3.3) * mm]});
            skFitSpline(sketch, "E2940", {"points": [v(-58.21, -3.3) * mm, v(-57.57, -2.9) * mm, v(-56.93, -2.5) * mm, v(-56.28, -2.1) * mm]});
            skFitSpline(sketch, "E2941", {"points": [v(-56.28, -2.1) * mm, v(-55.9, -1.86) * mm, v(-55.51, -1.62) * mm, v(-55.13, -1.38) * mm]});
            skFitSpline(sketch, "E2942", {"points": [v(-55.13, -1.38) * mm, v(-55.07, -1.34) * mm, v(-55.02, -1.3) * mm, v(-54.98, -1.26) * mm]});
            skFitSpline(sketch, "E2943", {"points": [v(-54.98, -1.26) * mm, v(-54.8, -1.04) * mm, v(-54.58, -1) * mm, v(-54.35, -1.1) * mm]});
            skFitSpline(sketch, "E2944", {"points": [v(-54.35, -1.1) * mm, v(-53.63, -1.37) * mm, v(-52.87, -1.55) * mm, v(-52.2, -1.95) * mm]});
            skFitSpline(sketch, "E2945", {"points": [v(-52.2, -1.95) * mm, v(-52.13, -1.99) * mm, v(-52.07, -2.02) * mm, v(-52.01, -2.06) * mm]});
            skFitSpline(sketch, "E2946", {"points": [v(-52.01, -2.06) * mm, v(-51.83, -2.2) * mm, v(-51.77, -2.44) * mm, v(-51.87, -2.64) * mm]});
            skFitSpline(sketch, "E2947", {"points": [v(-51.87, -2.64) * mm, v(-51.97, -2.85) * mm, v(-52.2, -2.97) * mm, v(-52.42, -2.9) * mm]});
            skFitSpline(sketch, "E2948", {"points": [v(-52.42, -2.9) * mm, v(-52.51, -2.88) * mm, v(-52.6, -2.84) * mm, v(-52.69, -2.8) * mm]});
            skFitSpline(sketch, "E2949", {"points": [v(-52.69, -2.8) * mm, v(-53.2, -2.48) * mm, v(-53.8, -2.34) * mm, v(-54.35, -2.14) * mm]});
            skFitSpline(sketch, "E2950", {"points": [v(-54.35, -2.14) * mm, v(-54.4, -2.12) * mm, v(-54.48, -2.13) * mm, v(-54.53, -2.16) * mm]});
            skFitSpline(sketch, "E2951", {"points": [v(-54.53, -2.16) * mm, v(-54.65, -2.22) * mm, v(-54.77, -2.29) * mm, v(-54.88, -2.36) * mm]});
            skFitSpline(sketch, "E2952", {"points": [v(-54.88, -2.36) * mm, v(-55.55, -2.77) * mm, v(-56.21, -3.18) * mm, v(-56.87, -3.6) * mm]});
            skFitSpline(sketch, "E2953", {"points": [v(-56.87, -3.6) * mm, v(-57.26, -3.84) * mm, v(-57.64, -4.09) * mm, v(-58.04, -4.35) * mm]});
            skFitSpline(sketch, "E2954", {"points": [v(-58.04, -4.35) * mm, v(-57.71, -4.57) * mm, v(-57.4, -4.8) * mm, v(-57.06, -4.98) * mm]});
            skFitSpline(sketch, "E2955", {"points": [v(-57.06, -4.98) * mm, v(-56.95, -5.04) * mm, v(-56.83, -5.08) * mm, v(-56.73, -5.14) * mm]});
            skFitSpline(sketch, "E2956", {"points": [v(-56.73, -5.14) * mm, v(-56.62, -5.21) * mm, v(-56.52, -5.21) * mm, v(-56.4, -5.16) * mm]});
            skFitSpline(sketch, "E2957", {"points": [v(-56.4, -5.16) * mm, v(-56.02, -5) * mm, v(-55.63, -4.84) * mm, v(-55.25, -4.67) * mm]});
            skFitSpline(sketch, "E2958", {"points": [v(-55.25, -4.67) * mm, v(-55.13, -4.63) * mm, v(-55.02, -4.56) * mm, v(-54.9, -4.5) * mm]});
            skFitSpline(sketch, "E2959", {"points": [v(-54.9, -4.5) * mm, v(-54.66, -4.38) * mm, v(-54.38, -4.45) * mm, v(-54.24, -4.68) * mm]});
            skFitSpline(sketch, "E2960", {"points": [v(-54.24, -4.68) * mm, v(-54.1, -4.93) * mm, v(-54.16, -5.22) * mm, v(-54.42, -5.36) * mm]});
            skFitSpline(sketch, "E2961", {"points": [v(-54.42, -5.36) * mm, v(-54.62, -5.47) * mm, v(-54.83, -5.55) * mm, v(-55.04, -5.64) * mm]});
            skFitSpline(sketch, "E2962", {"points": [v(-55.04, -5.64) * mm, v(-55.17, -5.7) * mm, v(-55.31, -5.74) * mm, v(-55.48, -5.8) * mm]});
            skFitSpline(sketch, "E2963", {"points": [v(-55.48, -5.8) * mm, v(-55.28, -5.97) * mm, v(-55.12, -6.07) * mm, v(-54.88, -5.98) * mm]});
            skFitSpline(sketch, "E2964", {"points": [v(-54.88, -5.98) * mm, v(-54.2, -5.73) * mm, v(-53.54, -5.5) * mm, v(-52.87, -5.27) * mm]});
            skFitSpline(sketch, "E2965", {"points": [v(-52.87, -5.27) * mm, v(-52.58, -5.16) * mm, v(-52.31, -5.24) * mm, v(-52.19, -5.48) * mm]});
            skFitSpline(sketch, "E2966", {"points": [v(-52.19, -5.48) * mm, v(-52.07, -5.73) * mm, v(-52.16, -6) * mm, v(-52.44, -6.15) * mm]});
            skFitSpline(sketch, "E2967", {"points": [v(-52.44, -6.15) * mm, v(-52.51, -6.19) * mm, v(-52.6, -6.23) * mm, v(-52.68, -6.26) * mm]});
            skFitSpline(sketch, "E2968", {"points": [v(-52.68, -6.26) * mm, v(-52.92, -6.35) * mm, v(-53.17, -6.44) * mm, v(-53.42, -6.53) * mm]});
            skFitSpline(sketch, "E2969", {"points": [v(-53.42, -6.53) * mm, v(-53.58, -6.59) * mm, v(-53.75, -6.64) * mm, v(-53.95, -6.71) * mm]});
            skFitSpline(sketch, "E2970", {"points": [v(-53.95, -6.71) * mm, v(-53.76, -6.84) * mm, v(-53.6, -6.93) * mm, v(-53.39, -6.9) * mm]});
            skFitSpline(sketch, "E2971", {"points": [v(-53.39, -6.9) * mm, v(-52.62, -6.83) * mm, v(-51.88, -6.65) * mm, v(-51.13, -6.49) * mm]});
            skFitSpline(sketch, "E2972", {"points": [v(-51.13, -6.49) * mm, v(-51.02, -6.46) * mm, v(-50.9, -6.45) * mm, v(-50.8, -6.46) * mm]});
            skFitSpline(sketch, "E2973", {"points": [v(-50.8, -6.46) * mm, v(-50.55, -6.48) * mm, v(-50.37, -6.67) * mm, v(-50.36, -6.92) * mm]});
            skFitSpline(sketch, "E2974", {"points": [v(-50.36, -6.92) * mm, v(-50.35, -7.17) * mm, v(-50.51, -7.37) * mm, v(-50.76, -7.41) * mm]});
            skFitSpline(sketch, "E2975", {"points": [v(-50.76, -7.41) * mm, v(-51.52, -7.56) * mm, v(-52.28, -7.7) * mm, v(-53.04, -7.84) * mm]});
            skFitSpline(sketch, "E2976", {"points": [v(-53.04, -7.84) * mm, v(-53.05, -7.85) * mm, v(-53.06, -7.86) * mm, v(-53.09, -7.87) * mm]});
            skFitSpline(sketch, "E2977", {"points": [v(-53.09, -7.87) * mm, v(-53.07, -7.91) * mm, v(-53.06, -7.96) * mm, v(-53.04, -8) * mm]});
            skFitSpline(sketch, "E2978", {"points": [v(-53.04, -8) * mm, v(-52.77, -8.58) * mm, v(-52.6, -9.2) * mm, v(-52.41, -9.8) * mm]});
            skFitSpline(sketch, "E2979", {"points": [v(-52.41, -9.8) * mm, v(-52.38, -9.9) * mm, v(-52.34, -10) * mm, v(-52.3, -10.1) * mm]});
            skFitSpline(sketch, "E2980", {"points": [v(-52.3, -10.1) * mm, v(-52.23, -10.35) * mm, v(-52.34, -10.6) * mm, v(-52.56, -10.7) * mm]});
            skFitSpline(sketch, "E2981", {"points": [v(-52.56, -10.7) * mm, v(-52.79, -10.81) * mm, v(-53.05, -10.73) * mm, v(-53.18, -10.5) * mm]});
            skFitSpline(sketch, "E2982", {"points": [v(-53.18, -10.5) * mm, v(-53.24, -10.4) * mm, v(-53.29, -10.29) * mm, v(-53.32, -10.17) * mm]});
            skFitSpline(sketch, "E2983", {"points": [v(-53.32, -10.17) * mm, v(-53.54, -9.46) * mm, v(-53.76, -8.76) * mm, v(-54.07, -8.07) * mm]});
            skFitSpline(sketch, "E2984", {"points": [v(-54.07, -8.07) * mm, v(-54.15, -7.88) * mm, v(-54.3, -7.78) * mm, v(-54.5, -7.7) * mm]});
            skFitSpline(sketch, "E2985", {"points": [v(-54.5, -7.7) * mm, v(-54.48, -7.87) * mm, v(-54.45, -8.01) * mm, v(-54.42, -8.16) * mm]});
            skFitSpline(sketch, "E2986", {"points": [v(-54.42, -8.16) * mm, v(-54.36, -8.53) * mm, v(-54.3, -8.9) * mm, v(-54.25, -9.27) * mm]});
            skFitSpline(sketch, "E2987", {"points": [v(-54.25, -9.27) * mm, v(-54.22, -9.57) * mm, v(-54.4, -9.8) * mm, v(-54.69, -9.83) * mm]});
            skFitSpline(sketch, "E2988", {"points": [v(-54.69, -9.83) * mm, v(-54.95, -9.86) * mm, v(-55.17, -9.65) * mm, v(-55.22, -9.36) * mm]});
            skFitSpline(sketch, "E2989", {"points": [v(-55.22, -9.36) * mm, v(-55.31, -8.8) * mm, v(-55.41, -8.24) * mm, v(-55.52, -7.68) * mm]});
            skFitSpline(sketch, "E2990", {"points": [v(-55.52, -7.68) * mm, v(-55.54, -7.56) * mm, v(-55.57, -7.43) * mm, v(-55.6, -7.31) * mm]});
            skFitSpline(sketch, "E2991", {"points": [v(-55.6, -7.31) * mm, v(-55.68, -6.98) * mm, v(-55.68, -6.98) * mm, v(-56.05, -6.82) * mm]});
            skFitSpline(sketch, "E2992", {"points": [v(-56.05, -6.82) * mm, v(-56.02, -7.05) * mm, v(-55.99, -7.27) * mm, v(-55.96, -7.48) * mm]});
            skFitSpline(sketch, "E2993", {"points": [v(-55.96, -7.48) * mm, v(-55.95, -7.66) * mm, v(-55.93, -7.83) * mm, v(-55.93, -8) * mm]});
            skFitSpline(sketch, "E2994", {"points": [v(-55.93, -8) * mm, v(-55.93, -8.25) * mm, v(-56.13, -8.44) * mm, v(-56.38, -8.45) * mm]});
            skFitSpline(sketch, "E2995", {"points": [v(-56.38, -8.45) * mm, v(-56.63, -8.46) * mm, v(-56.86, -8.29) * mm, v(-56.9, -8.04) * mm]});
            skFitSpline(sketch, "E2996", {"points": [v(-56.9, -8.04) * mm, v(-56.96, -7.49) * mm, v(-57.02, -6.93) * mm, v(-57.08, -6.38) * mm]});
            skFitSpline(sketch, "E2997", {"points": [v(-57.08, -6.38) * mm, v(-57.1, -6.23) * mm, v(-57.14, -6.14) * mm, v(-57.27, -6.05) * mm]});
            skFitSpline(sketch, "E2998", {"points": [v(-57.27, -6.05) * mm, v(-57.66, -5.78) * mm, v(-58.08, -5.58) * mm, v(-58.5, -5.37) * mm]});
            skFitSpline(sketch, "E2999", {"points": [v(-58.5, -5.37) * mm, v(-58.53, -5.36) * mm, v(-58.56, -5.35) * mm, v(-58.62, -5.33) * mm]});
            skFitSpline(sketch, "E3000", {"points": [v(-58.62, -5.33) * mm, v(-58.62, -5.47) * mm, v(-58.62, -5.6) * mm, v(-58.62, -5.72) * mm]});
            skFitSpline(sketch, "E3001", {"points": [v(-58.62, -5.72) * mm, v(-58.64, -6.23) * mm, v(-58.66, -6.74) * mm, v(-58.68, -7.25) * mm]});
            skFitSpline(sketch, "E3002", {"points": [v(-58.68, -7.25) * mm, v(-58.7, -7.84) * mm, v(-58.73, -8.43) * mm, v(-58.75, -9.02) * mm]});
            skFitSpline(sketch, "E3003", {"points": [v(-58.75, -9.02) * mm, v(-58.76, -9.04) * mm, v(-58.75, -9.07) * mm, v(-58.76, -9.1) * mm]});
            skFitSpline(sketch, "E3004", {"points": [v(-58.76, -9.1) * mm, v(-58.8, -9.4) * mm, v(-58.7, -9.64) * mm, v(-58.44, -9.85) * mm]});
            skFitSpline(sketch, "E3005", {"points": [v(-58.44, -9.85) * mm, v(-58.03, -10.17) * mm, v(-57.64, -10.53) * mm, v(-57.18, -10.8) * mm]});
            skFitSpline(sketch, "E3006", {"points": [v(-57.18, -10.8) * mm, v(-56.98, -10.91) * mm, v(-56.87, -11.08) * mm, v(-56.91, -11.32) * mm]});
            skFitSpline(sketch, "E3007", {"points": [v(-56.91, -11.32) * mm, v(-56.96, -11.64) * mm, v(-57.33, -11.86) * mm, v(-57.65, -11.65) * mm]});
            skFitSpline(sketch, "E3008", {"points": [v(-57.65, -11.65) * mm, v(-57.97, -11.44) * mm, v(-58.29, -11.23) * mm, v(-58.59, -11) * mm]});
            skFitSpline(sketch, "E3009", {"points": [v(-58.59, -11) * mm, v(-58.92, -10.73) * mm, v(-59.23, -10.45) * mm, v(-59.56, -10.17) * mm]});
            skFitSpline(sketch, "E3010", {"points": [v(-59.56, -10.17) * mm, v(-59.76, -10) * mm, v(-59.88, -9.8) * mm, v(-59.75, -9.52) * mm]});
            skFitSpline(sketch, "E3011", {"points": [v(-59.75, -9.52) * mm, v(-59.73, -9.47) * mm, v(-59.72, -9.4) * mm, v(-59.72, -9.35) * mm]});
            skFitSpline(sketch, "E3012", {"points": [v(-59.72, -9.35) * mm, v(-59.7, -9.04) * mm, v(-59.68, -8.73) * mm, v(-59.67, -8.42) * mm]});
            skFitSpline(sketch, "E3013", {"points": [v(-59.67, -8.42) * mm, v(-59.65, -7.86) * mm, v(-59.65, -7.29) * mm, v(-59.63, -6.72) * mm]});
            skFitSpline(sketch, "E3014", {"points": [v(-59.63, -6.72) * mm, v(-59.62, -6.36) * mm, v(-59.6, -6) * mm, v(-59.59, -5.65) * mm]});
            skFitSpline(sketch, "E3015", {"points": [v(-59.59, -5.65) * mm, v(-59.59, -5.57) * mm, v(-59.59, -5.5) * mm, v(-59.59, -5.38) * mm]});
            skFitSpline(sketch, "E3016", {"points": [v(-59.59, -5.38) * mm, v(-59.68, -5.43) * mm, v(-59.75, -5.46) * mm, v(-59.8, -5.5) * mm]});
            skFitSpline(sketch, "E3017", {"points": [v(-59.8, -5.5) * mm, v(-60.32, -5.84) * mm, v(-60.83, -6.18) * mm, v(-61.35, -6.51) * mm]});
            skFitSpline(sketch, "E3018", {"points": [v(-61.35, -6.51) * mm, v(-61.72, -6.75) * mm, v(-62.1, -7) * mm, v(-62.5, -7.2) * mm]});
            skFitSpline(sketch, "E3019", {"points": [v(-62.5, -7.2) * mm, v(-63.31, -7.65) * mm, v(-64.14, -8.08) * mm, v(-64.97, -8.51) * mm]});
            skFitSpline(sketch, "E3020", {"points": [v(-64.97, -8.51) * mm, v(-65.16, -8.61) * mm, v(-65.36, -8.71) * mm, v(-65.6, -8.83) * mm]});
            skFitSpline(sketch, "E3021", {"points": [v(-65.6, -8.83) * mm, v(-65.27, -9.01) * mm, v(-64.98, -9.17) * mm, v(-64.68, -9.33) * mm]});
            skFitSpline(sketch, "E3022", {"points": [v(-64.68, -9.33) * mm, v(-64.11, -9.63) * mm, v(-63.55, -9.95) * mm, v(-62.98, -10.25) * mm]});
            skFitSpline(sketch, "E3023", {"points": [v(-62.98, -10.25) * mm, v(-62.66, -10.42) * mm, v(-62.34, -10.58) * mm, v(-62.02, -10.75) * mm]});
            skFitSpline(sketch, "E3024", {"points": [v(-62.02, -10.75) * mm, v(-61.99, -10.76) * mm, v(-61.95, -10.77) * mm, v(-61.9, -10.78) * mm]});
            skFitSpline(sketch, "E3025", {"points": [v(-61.9, -10.78) * mm, v(-61.64, -10.82) * mm, v(-61.5, -11) * mm, v(-61.46, -11.25) * mm]});
            skFitSpline(sketch, "E3026", {"points": [v(-61.46, -11.25) * mm, v(-61.37, -11.76) * mm, v(-61.26, -12.28) * mm, v(-61.18, -12.8) * mm]});
            skFitSpline(sketch, "E3027", {"points": [v(-61.18, -12.8) * mm, v(-61.14, -13.09) * mm, v(-61.13, -13.39) * mm, v(-61.13, -13.68) * mm]});
            skFitSpline(sketch, "E3028", {"points": [v(-61.13, -13.68) * mm, v(-61.13, -13.93) * mm, v(-61.3, -14.11) * mm, v(-61.53, -14.15) * mm]});
            skFitSpline(sketch, "E3029", {"points": [v(-61.53, -14.15) * mm, v(-61.75, -14.19) * mm, v(-61.99, -14.08) * mm, v(-62.05, -13.87) * mm]});
            skFitSpline(sketch, "E3030", {"points": [v(-62.05, -13.87) * mm, v(-62.1, -13.74) * mm, v(-62.11, -13.59) * mm, v(-62.11, -13.45) * mm]});
            skFitSpline(sketch, "E3031", {"points": [v(-62.11, -13.45) * mm, v(-62.1, -12.86) * mm, v(-62.28, -12.31) * mm, v(-62.37, -11.75) * mm]});
            skFitSpline(sketch, "E3032", {"points": [v(-62.37, -11.75) * mm, v(-62.38, -11.7) * mm, v(-62.42, -11.65) * mm, v(-62.46, -11.62) * mm]});
            skFitSpline(sketch, "E3033", {"points": [v(-62.46, -11.62) * mm, v(-62.62, -11.53) * mm, v(-62.78, -11.44) * mm, v(-62.94, -11.35) * mm]});
            skFitSpline(sketch, "E3034", {"points": [v(-62.94, -11.35) * mm, v(-63.57, -11.02) * mm, v(-64.2, -10.68) * mm, v(-64.82, -10.35) * mm]});
            skFitSpline(sketch, "E3035", {"points": [v(-64.82, -10.35) * mm, v(-65.1, -10.2) * mm, v(-65.4, -10.06) * mm, v(-65.67, -9.9) * mm]});
            skFitSpline(sketch, "E3036", {"points": [v(-65.67, -9.9) * mm, v(-65.82, -9.83) * mm, v(-65.96, -9.75) * mm, v(-66.14, -9.65) * mm]});
            skFitSpline(sketch, "E3037", {"points": [v(-66.14, -9.65) * mm, v(-66.14, -10.13) * mm, v(-66.25, -10.58) * mm, v(-66.17, -11.03) * mm]});
            skFitSpline(sketch, "E3038", {"points": [v(-66.17, -11.03) * mm, v(-66.17, -11.04) * mm, v(-66.16, -11.05) * mm, v(-66.16, -11.05) * mm]});
            skFitSpline(sketch, "E3039", {"points": [v(-66.16, -11.05) * mm, v(-66.22, -11.33) * mm, v(-66.07, -11.47) * mm, v(-65.85, -11.6) * mm]});
            skFitSpline(sketch, "E3040", {"points": [v(-65.85, -11.6) * mm, v(-65.62, -11.76) * mm, v(-65.4, -11.94) * mm, v(-65.18, -12.11) * mm]});
            skFitSpline(sketch, "E3041", {"points": [v(-65.18, -12.11) * mm, v(-65.02, -12.23) * mm, v(-64.86, -12.35) * mm, v(-64.7, -12.46) * mm]});
            skFitSpline(sketch, "E3042", {"points": [v(-64.7, -12.46) * mm, v(-64.47, -12.61) * mm, v(-64.39, -12.9) * mm, v(-64.52, -13.13) * mm]});
            skFitSpline(sketch, "E3043", {"points": [v(-64.52, -13.13) * mm, v(-64.66, -13.37) * mm, v(-64.95, -13.46) * mm, v(-65.2, -13.3) * mm]});
            skFitSpline(sketch, "E3044", {"points": [v(-65.2, -13.3) * mm, v(-65.38, -13.2) * mm, v(-65.55, -13.06) * mm, v(-65.72, -12.93) * mm]});
            skFitSpline(sketch, "E3045", {"points": [v(-65.72, -12.93) * mm, v(-65.85, -12.83) * mm, v(-65.97, -12.73) * mm, v(-66.12, -12.6) * mm]});
            skFitSpline(sketch, "E3046", {"points": [v(-66.12, -12.6) * mm, v(-66.16, -12.86) * mm, v(-66.17, -13.05) * mm, v(-65.97, -13.21) * mm]});
            skFitSpline(sketch, "E3047", {"points": [v(-65.97, -13.21) * mm, v(-65.42, -13.67) * mm, v(-64.88, -14.15) * mm, v(-64.34, -14.61) * mm]});
            skFitSpline(sketch, "E3048", {"points": [v(-64.34, -14.61) * mm, v(-64.18, -14.75) * mm, v(-64.08, -14.9) * mm, v(-64.1, -15.1) * mm]});
            skFitSpline(sketch, "E3049", {"points": [v(-64.1, -15.1) * mm, v(-64.14, -15.3) * mm, v(-64.26, -15.45) * mm, v(-64.46, -15.5) * mm]});
            skFitSpline(sketch, "E3050", {"points": [v(-64.46, -15.5) * mm, v(-64.56, -15.52) * mm, v(-64.68, -15.5) * mm, v(-64.78, -15.47) * mm]});
            skFitSpline(sketch, "E3051", {"points": [v(-64.78, -15.47) * mm, v(-64.9, -15.42) * mm, v(-65.02, -15.34) * mm, v(-65.12, -15.25) * mm]});
            skFitSpline(sketch, "E3052", {"points": [v(-65.12, -15.25) * mm, v(-65.42, -15) * mm, v(-65.7, -14.76) * mm, v(-66, -14.5) * mm]});
            skFitSpline(sketch, "E3053", {"points": [v(-66, -14.5) * mm, v(-66.03, -14.48) * mm, v(-66.07, -14.45) * mm, v(-66.13, -14.4) * mm]});
            skFitSpline(sketch, "E3054", {"points": [v(-23.72, -2.12) * mm, v(-23.7, -2.25) * mm, v(-23.68, -2.34) * mm, v(-23.66, -2.42) * mm]});
            skFitSpline(sketch, "E3055", {"points": [v(-23.66, -2.42) * mm, v(-23.3, -3.79) * mm, v(-23, -5.17) * mm, v(-22.58, -6.52) * mm]});
            skFitSpline(sketch, "E3056", {"points": [v(-22.58, -6.52) * mm, v(-22.3, -7.42) * mm, v(-22.06, -8.33) * mm, v(-21.8, -9.23) * mm]});
            skFitSpline(sketch, "E3057", {"points": [v(-21.8, -9.23) * mm, v(-21.77, -9.3) * mm, v(-21.73, -9.39) * mm, v(-21.67, -9.42) * mm]});
            skFitSpline(sketch, "E3058", {"points": [v(-21.67, -9.42) * mm, v(-21.46, -9.55) * mm, v(-21.24, -9.67) * mm, v(-21.02, -9.77) * mm]});
            skFitSpline(sketch, "E3059", {"points": [v(-21.02, -9.77) * mm, v(-20.47, -10.01) * mm, v(-19.92, -10.25) * mm, v(-19.37, -10.48) * mm]});
            skFitSpline(sketch, "E3060", {"points": [v(-19.37, -10.48) * mm, v(-19.18, -10.56) * mm, v(-18.98, -10.62) * mm, v(-18.77, -10.7) * mm]});
            skFitSpline(sketch, "E3061", {"points": [v(-18.77, -10.7) * mm, v(-18.74, -10.55) * mm, v(-18.71, -10.44) * mm, v(-18.7, -10.32) * mm]});
            skFitSpline(sketch, "E3062", {"points": [v(-18.7, -10.32) * mm, v(-18.63, -9.8) * mm, v(-18.55, -9.28) * mm, v(-18.5, -8.76) * mm]});
            skFitSpline(sketch, "E3063", {"points": [v(-18.5, -8.76) * mm, v(-18.46, -8.38) * mm, v(-18.44, -8) * mm, v(-18.4, -7.64) * mm]});
            skFitSpline(sketch, "E3064", {"points": [v(-18.4, -7.64) * mm, v(-18.4, -7.5) * mm, v(-18.45, -7.41) * mm, v(-18.54, -7.32) * mm]});
            skFitSpline(sketch, "E3065", {"points": [v(-18.54, -7.32) * mm, v(-18.7, -7.17) * mm, v(-18.85, -7.02) * mm, v(-19, -6.86) * mm]});
            skFitSpline(sketch, "E3066", {"points": [v(-19, -6.86) * mm, v(-20.02, -5.75) * mm, v(-21.06, -4.66) * mm, v(-22.16, -3.62) * mm]});
            skFitSpline(sketch, "E3067", {"points": [v(-22.16, -3.62) * mm, v(-22.62, -3.17) * mm, v(-23.08, -2.73) * mm, v(-23.54, -2.28) * mm]});
            skFitSpline(sketch, "E3068", {"points": [v(-23.54, -2.28) * mm, v(-23.58, -2.23) * mm, v(-23.64, -2.2) * mm, v(-23.72, -2.12) * mm]});
            skFitSpline(sketch, "E3069", {"points": [v(-26.17, -2.17) * mm, v(-26.19, -2.17) * mm, v(-26.2, -2.16) * mm, v(-26.22, -2.16) * mm]});
            skFitSpline(sketch, "E3070", {"points": [v(-26.22, -2.16) * mm, v(-26.52, -2.45) * mm, v(-26.83, -2.74) * mm, v(-27.13, -3.04) * mm]});
            skFitSpline(sketch, "E3071", {"points": [v(-27.13, -3.04) * mm, v(-27.77, -3.66) * mm, v(-28.41, -4.28) * mm, v(-29.04, -4.92) * mm]});
            skFitSpline(sketch, "E3072", {"points": [v(-29.04, -4.92) * mm, v(-29.81, -5.7) * mm, v(-30.56, -6.51) * mm, v(-31.32, -7.3) * mm]});
            skFitSpline(sketch, "E3073", {"points": [v(-31.32, -7.3) * mm, v(-31.42, -7.4) * mm, v(-31.46, -7.5) * mm, v(-31.46, -7.64) * mm]});
            skFitSpline(sketch, "E3074", {"points": [v(-31.46, -7.64) * mm, v(-31.47, -8.53) * mm, v(-31.28, -9.4) * mm, v(-31.2, -10.28) * mm]});
            skFitSpline(sketch, "E3075", {"points": [v(-31.2, -10.28) * mm, v(-31.18, -10.41) * mm, v(-31.14, -10.55) * mm, v(-31.1, -10.69) * mm]});
            skFitSpline(sketch, "E3076", {"points": [v(-31.1, -10.69) * mm, v(-31.04, -10.67) * mm, v(-31.01, -10.66) * mm, v(-30.98, -10.65) * mm]});
            skFitSpline(sketch, "E3077", {"points": [v(-30.98, -10.65) * mm, v(-30.22, -10.34) * mm, v(-29.46, -10.04) * mm, v(-28.7, -9.7) * mm]});
            skFitSpline(sketch, "E3078", {"points": [v(-28.7, -9.7) * mm, v(-28.14, -9.46) * mm, v(-28.15, -9.44) * mm, v(-27.99, -8.84) * mm]});
            skFitSpline(sketch, "E3079", {"points": [v(-27.99, -8.84) * mm, v(-27.98, -8.81) * mm, v(-27.97, -8.8) * mm, v(-27.96, -8.77) * mm]});
            skFitSpline(sketch, "E3080", {"points": [v(-27.96, -8.77) * mm, v(-27.65, -7.7) * mm, v(-27.32, -6.65) * mm, v(-27.02, -5.58) * mm]});
            skFitSpline(sketch, "E3081", {"points": [v(-27.02, -5.58) * mm, v(-26.74, -4.55) * mm, v(-26.5, -3.5) * mm, v(-26.23, -2.47) * mm]});
            skFitSpline(sketch, "E3082", {"points": [v(-26.23, -2.47) * mm, v(-26.2, -2.37) * mm, v(-26.2, -2.27) * mm, v(-26.17, -2.17) * mm]});
            skFitSpline(sketch, "E3083", {"points": [v(-22.51, 0) * mm, v(-22.4, -0.04) * mm, v(-22.35, -0.06) * mm, v(-22.29, -0.08) * mm]});
            skFitSpline(sketch, "E3084", {"points": [v(-22.29, -0.08) * mm, v(-20.92, -0.45) * mm, v(-19.55, -0.84) * mm, v(-18.18, -1.2) * mm]});
            skFitSpline(sketch, "E3085", {"points": [v(-18.18, -1.2) * mm, v(-17.25, -1.45) * mm, v(-16.32, -1.66) * mm, v(-15.4, -1.89) * mm]});
            skFitSpline(sketch, "E3086", {"points": [v(-15.4, -1.89) * mm, v(-15.31, -1.9) * mm, v(-15.2, -1.92) * mm, v(-15.14, -1.88) * mm]});
            skFitSpline(sketch, "E3087", {"points": [v(-15.14, -1.88) * mm, v(-14.92, -1.76) * mm, v(-14.71, -1.63) * mm, v(-14.51, -1.49) * mm]});
            skFitSpline(sketch, "E3088", {"points": [v(-14.51, -1.49) * mm, v(-14.03, -1.13) * mm, v(-13.55, -0.77) * mm, v(-13.07, -0.4) * mm]});
            skFitSpline(sketch, "E3089", {"points": [v(-13.07, -0.4) * mm, v(-12.91, -0.29) * mm, v(-12.76, -0.15) * mm, v(-12.58, 0) * mm]});
            skFitSpline(sketch, "E3090", {"points": [v(-12.58, 0) * mm, v(-12.9, 0.25) * mm, v(-13.18, 0.48) * mm, v(-13.48, 0.7) * mm]});
            skFitSpline(sketch, "E3091", {"points": [v(-13.48, 0.7) * mm, v(-14, 1.08) * mm, v(-14.48, 1.5) * mm, v(-15.05, 1.83) * mm]});
            skFitSpline(sketch, "E3092", {"points": [v(-15.05, 1.83) * mm, v(-15.18, 1.9) * mm, v(-15.28, 1.91) * mm, v(-15.41, 1.88) * mm]});
            skFitSpline(sketch, "E3093", {"points": [v(-15.41, 1.88) * mm, v(-16.46, 1.62) * mm, v(-17.5, 1.38) * mm, v(-18.55, 1.11) * mm]});
            skFitSpline(sketch, "E3094", {"points": [v(-18.55, 1.11) * mm, v(-19.55, 0.85) * mm, v(-20.54, 0.56) * mm, v(-21.53, 0.29) * mm]});
            skFitSpline(sketch, "E3095", {"points": [v(-21.53, 0.29) * mm, v(-21.84, 0.2) * mm, v(-22.15, 0.1) * mm, v(-22.51, 0) * mm]});
            skFitSpline(sketch, "E3096", {"points": [v(-37.31, -0.02) * mm, v(-37.24, -0.06) * mm, v(-37.2, -0.09) * mm, v(-37.15, -0.12) * mm]});
            skFitSpline(sketch, "E3097", {"points": [v(-37.15, -0.12) * mm, v(-36.38, -0.72) * mm, v(-35.63, -1.35) * mm, v(-34.8, -1.85) * mm]});
            skFitSpline(sketch, "E3098", {"points": [v(-34.8, -1.85) * mm, v(-34.69, -1.92) * mm, v(-34.6, -1.92) * mm, v(-34.48, -1.9) * mm]});
            skFitSpline(sketch, "E3099", {"points": [v(-34.48, -1.9) * mm, v(-34.24, -1.83) * mm, v(-34, -1.76) * mm, v(-33.76, -1.7) * mm]});
            skFitSpline(sketch, "E3100", {"points": [v(-33.76, -1.7) * mm, v(-32.76, -1.46) * mm, v(-31.76, -1.24) * mm, v(-30.76, -0.98) * mm]});
            skFitSpline(sketch, "E3101", {"points": [v(-30.76, -0.98) * mm, v(-29.77, -0.72) * mm, v(-28.8, -0.42) * mm, v(-27.81, -0.14) * mm]});
            skFitSpline(sketch, "E3102", {"points": [v(-27.81, -0.14) * mm, v(-27.68, -0.1) * mm, v(-27.54, -0.06) * mm, v(-27.37, 0) * mm]});
            skFitSpline(sketch, "E3103", {"points": [v(-27.37, 0) * mm, v(-27.47, 0.03) * mm, v(-27.52, 0.05) * mm, v(-27.57, 0.06) * mm]});
            skFitSpline(sketch, "E3104", {"points": [v(-27.57, 0.06) * mm, v(-28.48, 0.32) * mm, v(-29.38, 0.6) * mm, v(-30.29, 0.84) * mm]});
            skFitSpline(sketch, "E3105", {"points": [v(-30.29, 0.84) * mm, v(-31.7, 1.2) * mm, v(-33.1, 1.54) * mm, v(-34.51, 1.9) * mm]});
            skFitSpline(sketch, "E3106", {"points": [v(-34.51, 1.9) * mm, v(-34.61, 1.92) * mm, v(-34.7, 1.9) * mm, v(-34.79, 1.85) * mm]});
            skFitSpline(sketch, "E3107", {"points": [v(-34.79, 1.85) * mm, v(-35.06, 1.66) * mm, v(-35.34, 1.5) * mm, v(-35.6, 1.3) * mm]});
            skFitSpline(sketch, "E3108", {"points": [v(-35.6, 1.3) * mm, v(-36.02, 1) * mm, v(-36.42, 0.7) * mm, v(-36.83, 0.38) * mm]});
            skFitSpline(sketch, "E3109", {"points": [v(-36.83, 0.38) * mm, v(-36.98, 0.27) * mm, v(-37.12, 0.14) * mm, v(-37.31, -0.02) * mm]});
            skFitSpline(sketch, "E3110", {"points": [v(-31.11, 10.69) * mm, v(-31.15, 10.48) * mm, v(-31.2, 10.3) * mm, v(-31.22, 10.11) * mm]});
            skFitSpline(sketch, "E3111", {"points": [v(-31.22, 10.11) * mm, v(-31.27, 9.7) * mm, v(-31.3, 9.3) * mm, v(-31.37, 8.9) * mm]});
            skFitSpline(sketch, "E3112", {"points": [v(-31.37, 8.9) * mm, v(-31.43, 8.47) * mm, v(-31.47, 8.05) * mm, v(-31.46, 7.62) * mm]});
            skFitSpline(sketch, "E3113", {"points": [v(-31.46, 7.62) * mm, v(-31.46, 7.5) * mm, v(-31.44, 7.4) * mm, v(-31.35, 7.32) * mm]});
            skFitSpline(sketch, "E3114", {"points": [v(-31.35, 7.32) * mm, v(-31.17, 7.16) * mm, v(-31, 6.99) * mm, v(-30.84, 6.81) * mm]});
            skFitSpline(sketch, "E3115", {"points": [v(-30.84, 6.81) * mm, v(-30.18, 6.12) * mm, v(-29.54, 5.4) * mm, v(-28.86, 4.72) * mm]});
            skFitSpline(sketch, "E3116", {"points": [v(-28.86, 4.72) * mm, v(-28.1, 3.95) * mm, v(-27.3, 3.2) * mm, v(-26.51, 2.43) * mm]});
            skFitSpline(sketch, "E3117", {"points": [v(-26.51, 2.43) * mm, v(-26.41, 2.33) * mm, v(-26.3, 2.24) * mm, v(-26.16, 2.1) * mm]});
            skFitSpline(sketch, "E3118", {"points": [v(-26.16, 2.1) * mm, v(-26.18, 2.22) * mm, v(-26.2, 2.28) * mm, v(-26.2, 2.34) * mm]});
            skFitSpline(sketch, "E3119", {"points": [v(-26.2, 2.34) * mm, v(-26.43, 3.24) * mm, v(-26.64, 4.14) * mm, v(-26.88, 5.03) * mm]});
            skFitSpline(sketch, "E3120", {"points": [v(-26.88, 5.03) * mm, v(-27.27, 6.44) * mm, v(-27.69, 7.84) * mm, v(-28.09, 9.24) * mm]});
            skFitSpline(sketch, "E3121", {"points": [v(-28.09, 9.24) * mm, v(-28.12, 9.33) * mm, v(-28.15, 9.4) * mm, v(-28.24, 9.44) * mm]});
            skFitSpline(sketch, "E3122", {"points": [v(-28.24, 9.44) * mm, v(-28.51, 9.57) * mm, v(-28.78, 9.72) * mm, v(-29.05, 9.85) * mm]});
            skFitSpline(sketch, "E3123", {"points": [v(-29.05, 9.85) * mm, v(-29.55, 10.07) * mm, v(-30.05, 10.28) * mm, v(-30.55, 10.48) * mm]});
            skFitSpline(sketch, "E3124", {"points": [v(-30.55, 10.48) * mm, v(-30.72, 10.56) * mm, v(-30.9, 10.61) * mm, v(-31.11, 10.69) * mm]});
            skFitSpline(sketch, "E3125", {"points": [v(-18.75, 10.68) * mm, v(-18.83, 10.66) * mm, v(-18.89, 10.65) * mm, v(-18.93, 10.63) * mm]});
            skFitSpline(sketch, "E3126", {"points": [v(-18.93, 10.63) * mm, v(-19.84, 10.26) * mm, v(-20.77, 9.92) * mm, v(-21.63, 9.45) * mm]});
            skFitSpline(sketch, "E3127", {"points": [v(-21.63, 9.45) * mm, v(-21.72, 9.4) * mm, v(-21.77, 9.32) * mm, v(-21.8, 9.23) * mm]});
            skFitSpline(sketch, "E3128", {"points": [v(-21.8, 9.23) * mm, v(-21.84, 9.05) * mm, v(-21.88, 8.87) * mm, v(-21.94, 8.7) * mm]});
            skFitSpline(sketch, "E3129", {"points": [v(-21.94, 8.7) * mm, v(-22.23, 7.7) * mm, v(-22.55, 6.7) * mm, v(-22.82, 5.69) * mm]});
            skFitSpline(sketch, "E3130", {"points": [v(-22.82, 5.69) * mm, v(-23.1, 4.65) * mm, v(-23.36, 3.6) * mm, v(-23.62, 2.56) * mm]});
            skFitSpline(sketch, "E3131", {"points": [v(-23.62, 2.56) * mm, v(-23.66, 2.43) * mm, v(-23.68, 2.3) * mm, v(-23.72, 2.1) * mm]});
            skFitSpline(sketch, "E3132", {"points": [v(-23.72, 2.1) * mm, v(-23.63, 2.18) * mm, v(-23.6, 2.22) * mm, v(-23.55, 2.25) * mm]});
            skFitSpline(sketch, "E3133", {"points": [v(-23.55, 2.25) * mm, v(-23.28, 2.52) * mm, v(-23, 2.77) * mm, v(-22.74, 3.04) * mm]});
            skFitSpline(sketch, "E3134", {"points": [v(-22.74, 3.04) * mm, v(-22.04, 3.73) * mm, v(-21.33, 4.43) * mm, v(-20.63, 5.13) * mm]});
            skFitSpline(sketch, "E3135", {"points": [v(-20.63, 5.13) * mm, v(-19.93, 5.85) * mm, v(-19.24, 6.59) * mm, v(-18.54, 7.32) * mm]});
            skFitSpline(sketch, "E3136", {"points": [v(-18.54, 7.32) * mm, v(-18.49, 7.37) * mm, v(-18.42, 7.46) * mm, v(-18.42, 7.53) * mm]});
            skFitSpline(sketch, "E3137", {"points": [v(-18.42, 7.53) * mm, v(-18.4, 7.74) * mm, v(-18.4, 7.95) * mm, v(-18.42, 8.15) * mm]});
            skFitSpline(sketch, "E3138", {"points": [v(-18.42, 8.15) * mm, v(-18.47, 8.64) * mm, v(-18.54, 9.13) * mm, v(-18.6, 9.62) * mm]});
            skFitSpline(sketch, "E3139", {"points": [v(-18.6, 9.62) * mm, v(-18.65, 9.97) * mm, v(-18.7, 10.31) * mm, v(-18.75, 10.68) * mm]});
            skFitSpline(sketch, "E3140", {"points": [v(-25.48, -13.29) * mm, v(-25.5, -12.85) * mm, v(-25.5, -12.42) * mm, v(-25.52, -11.96) * mm]});
            skFitSpline(sketch, "E3141", {"points": [v(-25.52, -11.96) * mm, v(-25.58, -12) * mm, v(-25.61, -12.02) * mm, v(-25.64, -12.04) * mm]});
            skFitSpline(sketch, "E3142", {"points": [v(-25.64, -12.04) * mm, v(-26.02, -12.33) * mm, v(-26.4, -12.63) * mm, v(-26.78, -12.92) * mm]});
            skFitSpline(sketch, "E3143", {"points": [v(-26.78, -12.92) * mm, v(-26.97, -13.06) * mm, v(-27.24, -13.02) * mm, v(-27.41, -12.84) * mm]});
            skFitSpline(sketch, "E3144", {"points": [v(-27.41, -12.84) * mm, v(-27.58, -12.66) * mm, v(-27.6, -12.38) * mm, v(-27.43, -12.2) * mm]});
            skFitSpline(sketch, "E3145", {"points": [v(-27.43, -12.2) * mm, v(-27.37, -12.12) * mm, v(-27.3, -12.06) * mm, v(-27.21, -12) * mm]});
            skFitSpline(sketch, "E3146", {"points": [v(-27.21, -12) * mm, v(-26.83, -11.74) * mm, v(-26.44, -11.49) * mm, v(-26.12, -11.16) * mm]});
            skFitSpline(sketch, "E3147", {"points": [v(-26.12, -11.16) * mm, v(-25.96, -11) * mm, v(-25.78, -10.94) * mm, v(-25.55, -10.97) * mm]});
            skFitSpline(sketch, "E3148", {"points": [v(-25.55, -10.97) * mm, v(-25.55, -10.86) * mm, v(-25.54, -10.76) * mm, v(-25.55, -10.65) * mm]});
            skFitSpline(sketch, "E3149", {"points": [v(-25.55, -10.65) * mm, v(-25.55, -10.57) * mm, v(-25.56, -10.5) * mm, v(-25.56, -10.41) * mm]});
            skFitSpline(sketch, "E3150", {"points": [v(-25.56, -10.41) * mm, v(-25.59, -9.7) * mm, v(-25.6, -9) * mm, v(-25.65, -8.29) * mm]});
            skFitSpline(sketch, "E3151", {"points": [v(-25.65, -8.29) * mm, v(-25.7, -7.23) * mm, v(-25.72, -6.18) * mm, v(-25.69, -5.13) * mm]});
            skFitSpline(sketch, "E3152", {"points": [v(-25.69, -5.13) * mm, v(-25.68, -4.86) * mm, v(-25.66, -4.6) * mm, v(-25.7, -4.33) * mm]});
            skFitSpline(sketch, "E3153", {"points": [v(-25.7, -4.33) * mm, v(-25.74, -4.5) * mm, v(-25.8, -4.66) * mm, v(-25.83, -4.83) * mm]});
            skFitSpline(sketch, "E3154", {"points": [v(-25.83, -4.83) * mm, v(-26.13, -6.12) * mm, v(-26.53, -7.38) * mm, v(-26.9, -8.65) * mm]});
            skFitSpline(sketch, "E3155", {"points": [v(-26.9, -8.65) * mm, v(-27.01, -9) * mm, v(-27.12, -9.36) * mm, v(-27.21, -9.71) * mm]});
            skFitSpline(sketch, "E3156", {"points": [v(-27.21, -9.71) * mm, v(-27.27, -9.95) * mm, v(-27.41, -10.1) * mm, v(-27.62, -10.22) * mm]});
            skFitSpline(sketch, "E3157", {"points": [v(-27.62, -10.22) * mm, v(-28.11, -10.5) * mm, v(-28.62, -10.75) * mm, v(-29.15, -10.96) * mm]});
            skFitSpline(sketch, "E3158", {"points": [v(-29.15, -10.96) * mm, v(-29.72, -11.18) * mm, v(-30.29, -11.41) * mm, v(-30.86, -11.64) * mm]});
            skFitSpline(sketch, "E3159", {"points": [v(-30.86, -11.64) * mm, v(-30.88, -11.65) * mm, v(-30.9, -11.67) * mm, v(-30.94, -11.7) * mm]});
            skFitSpline(sketch, "E3160", {"points": [v(-30.94, -11.7) * mm, v(-30.9, -11.9) * mm, v(-30.86, -12.12) * mm, v(-30.82, -12.34) * mm]});
            skFitSpline(sketch, "E3161", {"points": [v(-30.82, -12.34) * mm, v(-30.53, -13.69) * mm, v(-30.25, -15.04) * mm, v(-29.96, -16.39) * mm]});
            skFitSpline(sketch, "E3162", {"points": [v(-29.96, -16.39) * mm, v(-29.94, -16.48) * mm, v(-29.9, -16.57) * mm, v(-29.87, -16.66) * mm]});
            skFitSpline(sketch, "E3163", {"points": [v(-29.87, -16.66) * mm, v(-29.78, -16.93) * mm, v(-29.88, -17.2) * mm, v(-30.12, -17.3) * mm]});
            skFitSpline(sketch, "E3164", {"points": [v(-30.12, -17.3) * mm, v(-30.37, -17.42) * mm, v(-30.63, -17.32) * mm, v(-30.76, -17.05) * mm]});
            skFitSpline(sketch, "E3165", {"points": [v(-30.76, -17.05) * mm, v(-30.83, -16.9) * mm, v(-30.88, -16.72) * mm, v(-30.92, -16.55) * mm]});
            skFitSpline(sketch, "E3166", {"points": [v(-30.92, -16.55) * mm, v(-31.15, -15.52) * mm, v(-31.37, -14.48) * mm, v(-31.59, -13.44) * mm]});
            skFitSpline(sketch, "E3167", {"points": [v(-31.59, -13.44) * mm, v(-31.6, -13.4) * mm, v(-31.61, -13.36) * mm, v(-31.66, -13.3) * mm]});
            skFitSpline(sketch, "E3168", {"points": [v(-31.66, -13.3) * mm, v(-31.69, -13.42) * mm, v(-31.72, -13.53) * mm, v(-31.73, -13.64) * mm]});
            skFitSpline(sketch, "E3169", {"points": [v(-31.73, -13.64) * mm, v(-31.77, -14.28) * mm, v(-31.9, -14.9) * mm, v(-31.9, -15.55) * mm]});
            skFitSpline(sketch, "E3170", {"points": [v(-31.9, -15.55) * mm, v(-31.9, -15.78) * mm, v(-32.05, -15.95) * mm, v(-32.25, -16) * mm]});
            skFitSpline(sketch, "E3171", {"points": [v(-32.25, -16) * mm, v(-32.46, -16.06) * mm, v(-32.67, -15.99) * mm, v(-32.8, -15.8) * mm]});
            skFitSpline(sketch, "E3172", {"points": [v(-32.8, -15.8) * mm, v(-32.9, -15.63) * mm, v(-32.97, -15.46) * mm, v(-32.89, -15.26) * mm]});
            skFitSpline(sketch, "E3173", {"points": [v(-32.89, -15.26) * mm, v(-32.86, -15.18) * mm, v(-32.85, -15.1) * mm, v(-32.84, -15.02) * mm]});
            skFitSpline(sketch, "E3174", {"points": [v(-32.84, -15.02) * mm, v(-32.8, -14.62) * mm, v(-32.75, -14.22) * mm, v(-32.71, -13.81) * mm]});
            skFitSpline(sketch, "E3175", {"points": [v(-32.71, -13.81) * mm, v(-32.7, -13.7) * mm, v(-32.7, -13.59) * mm, v(-32.7, -13.45) * mm]});
            skFitSpline(sketch, "E3176", {"points": [v(-32.7, -13.45) * mm, v(-32.76, -13.48) * mm, v(-32.81, -13.5) * mm, v(-32.85, -13.53) * mm]});
            skFitSpline(sketch, "E3177", {"points": [v(-32.85, -13.53) * mm, v(-33.1, -13.72) * mm, v(-33.35, -13.9) * mm, v(-33.6, -14.1) * mm]});
            skFitSpline(sketch, "E3178", {"points": [v(-33.6, -14.1) * mm, v(-33.83, -14.27) * mm, v(-34.05, -14.44) * mm, v(-34.29, -14.6) * mm]});
            skFitSpline(sketch, "E3179", {"points": [v(-34.29, -14.6) * mm, v(-34.44, -14.71) * mm, v(-34.62, -14.74) * mm, v(-34.8, -14.69) * mm]});
            skFitSpline(sketch, "E3180", {"points": [v(-34.8, -14.69) * mm, v(-34.97, -14.64) * mm, v(-35.1, -14.52) * mm, v(-35.14, -14.33) * mm]});
            skFitSpline(sketch, "E3181", {"points": [v(-35.14, -14.33) * mm, v(-35.19, -14.13) * mm, v(-35.13, -13.95) * mm, v(-34.96, -13.82) * mm]});
            skFitSpline(sketch, "E3182", {"points": [v(-34.96, -13.82) * mm, v(-34.87, -13.76) * mm, v(-34.78, -13.72) * mm, v(-34.7, -13.66) * mm]});
            skFitSpline(sketch, "E3183", {"points": [v(-34.7, -13.66) * mm, v(-34.2, -13.3) * mm, v(-33.7, -12.95) * mm, v(-33.22, -12.59) * mm]});
            skFitSpline(sketch, "E3184", {"points": [v(-33.22, -12.59) * mm, v(-33.17, -12.56) * mm, v(-33.14, -12.51) * mm, v(-33.11, -12.45) * mm]});
            skFitSpline(sketch, "E3185", {"points": [v(-33.11, -12.45) * mm, v(-33.2, -12.47) * mm, v(-33.28, -12.49) * mm, v(-33.36, -12.51) * mm]});
            skFitSpline(sketch, "E3186", {"points": [v(-33.36, -12.51) * mm, v(-34.34, -12.83) * mm, v(-35.31, -13.15) * mm, v(-36.3, -13.46) * mm]});
            skFitSpline(sketch, "E3187", {"points": [v(-36.3, -13.46) * mm, v(-36.45, -13.51) * mm, v(-36.62, -13.55) * mm, v(-36.78, -13.56) * mm]});
            skFitSpline(sketch, "E3188", {"points": [v(-36.78, -13.56) * mm, v(-37.07, -13.6) * mm, v(-37.29, -13.43) * mm, v(-37.33, -13.16) * mm]});
            skFitSpline(sketch, "E3189", {"points": [v(-37.33, -13.16) * mm, v(-37.37, -12.93) * mm, v(-37.2, -12.68) * mm, v(-36.96, -12.61) * mm]});
            skFitSpline(sketch, "E3190", {"points": [v(-36.96, -12.61) * mm, v(-36.7, -12.54) * mm, v(-36.45, -12.49) * mm, v(-36.2, -12.4) * mm]});
            skFitSpline(sketch, "E3191", {"points": [v(-36.2, -12.4) * mm, v(-34.84, -11.97) * mm, v(-33.48, -11.52) * mm, v(-32.13, -11.07) * mm]});
            skFitSpline(sketch, "E3192", {"points": [v(-32.13, -11.07) * mm, v(-32.1, -11.06) * mm, v(-32.09, -11.05) * mm, v(-32.04, -11.03) * mm]});
            skFitSpline(sketch, "E3193", {"points": [v(-32.04, -11.03) * mm, v(-32.07, -10.9) * mm, v(-32.1, -10.76) * mm, v(-32.12, -10.62) * mm]});
            skFitSpline(sketch, "E3194", {"points": [v(-32.12, -10.62) * mm, v(-32.19, -10.13) * mm, v(-32.25, -9.64) * mm, v(-32.31, -9.15) * mm]});
            skFitSpline(sketch, "E3195", {"points": [v(-32.31, -9.15) * mm, v(-32.38, -8.7) * mm, v(-32.44, -8.25) * mm, v(-32.42, -7.8) * mm]});
            skFitSpline(sketch, "E3196", {"points": [v(-32.42, -7.8) * mm, v(-32.42, -7.66) * mm, v(-32.45, -7.52) * mm, v(-32.45, -7.39) * mm]});
            skFitSpline(sketch, "E3197", {"points": [v(-32.45, -7.39) * mm, v(-32.45, -7.18) * mm, v(-32.38, -7) * mm, v(-32.23, -6.85) * mm]});
            skFitSpline(sketch, "E3198", {"points": [v(-32.23, -6.85) * mm, v(-31.53, -6.12) * mm, v(-30.83, -5.38) * mm, v(-30.12, -4.65) * mm]});
            skFitSpline(sketch, "E3199", {"points": [v(-30.12, -4.65) * mm, v(-29.6, -4.11) * mm, v(-29.06, -3.59) * mm, v(-28.53, -3.05) * mm]});
            skFitSpline(sketch, "E3200", {"points": [v(-28.53, -3.05) * mm, v(-28.48, -3) * mm, v(-28.43, -2.94) * mm, v(-28.4, -2.85) * mm]});
            skFitSpline(sketch, "E3201", {"points": [v(-28.4, -2.85) * mm, v(-28.47, -2.9) * mm, v(-28.55, -2.93) * mm, v(-28.62, -2.97) * mm]});
            skFitSpline(sketch, "E3202", {"points": [v(-28.62, -2.97) * mm, v(-29.3, -3.38) * mm, v(-29.96, -3.79) * mm, v(-30.63, -4.18) * mm]});
            skFitSpline(sketch, "E3203", {"points": [v(-30.63, -4.18) * mm, v(-30.94, -4.36) * mm, v(-31.27, -4.51) * mm, v(-31.59, -4.68) * mm]});
            skFitSpline(sketch, "E3204", {"points": [v(-31.59, -4.68) * mm, v(-32.41, -5.1) * mm, v(-33.23, -5.53) * mm, v(-34.05, -5.96) * mm]});
            skFitSpline(sketch, "E3205", {"points": [v(-34.05, -5.96) * mm, v(-34.07, -5.97) * mm, v(-34.1, -5.99) * mm, v(-34.14, -6.01) * mm]});
            skFitSpline(sketch, "E3206", {"points": [v(-34.14, -6.01) * mm, v(-33.92, -6.24) * mm, v(-34, -6.5) * mm, v(-34.04, -6.77) * mm]});
            skFitSpline(sketch, "E3207", {"points": [v(-34.04, -6.77) * mm, v(-34.1, -7.14) * mm, v(-34.15, -7.52) * mm, v(-34.2, -7.89) * mm]});
            skFitSpline(sketch, "E3208", {"points": [v(-34.2, -7.89) * mm, v(-34.2, -7.97) * mm, v(-34.21, -8.06) * mm, v(-34.23, -8.15) * mm]});
            skFitSpline(sketch, "E3209", {"points": [v(-34.23, -8.15) * mm, v(-34.28, -8.46) * mm, v(-34.5, -8.61) * mm, v(-34.81, -8.56) * mm]});
            skFitSpline(sketch, "E3210", {"points": [v(-34.81, -8.56) * mm, v(-35.07, -8.52) * mm, v(-35.23, -8.28) * mm, v(-35.2, -8) * mm]});
            skFitSpline(sketch, "E3211", {"points": [v(-35.2, -8) * mm, v(-35.17, -7.78) * mm, v(-35.14, -7.57) * mm, v(-35.12, -7.35) * mm]});
            skFitSpline(sketch, "E3212", {"points": [v(-35.12, -7.35) * mm, v(-35.08, -7.08) * mm, v(-35.05, -6.8) * mm, v(-35.01, -6.5) * mm]});
            skFitSpline(sketch, "E3213", {"points": [v(-35.01, -6.5) * mm, v(-35.21, -6.6) * mm, v(-35.4, -6.7) * mm, v(-35.6, -6.8) * mm]});
            skFitSpline(sketch, "E3214", {"points": [v(-35.6, -6.8) * mm, v(-35.78, -6.9) * mm, v(-35.97, -7) * mm, v(-36.15, -7.1) * mm]});
            skFitSpline(sketch, "E3215", {"points": [v(-36.15, -7.1) * mm, v(-36.17, -7.24) * mm, v(-36.18, -7.37) * mm, v(-36.2, -7.49) * mm]});
            skFitSpline(sketch, "E3216", {"points": [v(-36.2, -7.49) * mm, v(-36.23, -7.56) * mm, v(-36.25, -7.65) * mm, v(-36.3, -7.7) * mm]});
            skFitSpline(sketch, "E3217", {"points": [v(-36.3, -7.7) * mm, v(-36.5, -7.88) * mm, v(-36.68, -8.09) * mm, v(-36.95, -8.2) * mm]});
            skFitSpline(sketch, "E3218", {"points": [v(-36.95, -8.2) * mm, v(-37.18, -8.29) * mm, v(-37.41, -8.26) * mm, v(-37.65, -8.2) * mm]});
            skFitSpline(sketch, "E3219", {"points": [v(-37.65, -8.2) * mm, v(-37.73, -8.17) * mm, v(-37.8, -8.16) * mm, v(-37.88, -8.14) * mm]});
            skFitSpline(sketch, "E3220", {"points": [v(-37.88, -8.14) * mm, v(-38.04, -8.1) * mm, v(-38.16, -8) * mm, v(-38.2, -7.84) * mm]});
            skFitSpline(sketch, "E3221", {"points": [v(-38.2, -7.84) * mm, v(-38.23, -7.74) * mm, v(-38.27, -7.66) * mm, v(-38.35, -7.58) * mm]});
            skFitSpline(sketch, "E3222", {"points": [v(-38.35, -7.58) * mm, v(-38.48, -7.45) * mm, v(-38.49, -7.28) * mm, v(-38.45, -7.11) * mm]});
            skFitSpline(sketch, "E3223", {"points": [v(-38.45, -7.11) * mm, v(-38.42, -6.98) * mm, v(-38.38, -6.84) * mm, v(-38.32, -6.72) * mm]});
            skFitSpline(sketch, "E3224", {"points": [v(-38.32, -6.72) * mm, v(-38.26, -6.6) * mm, v(-38.18, -6.46) * mm, v(-38.08, -6.35) * mm]});
            skFitSpline(sketch, "E3225", {"points": [v(-38.08, -6.35) * mm, v(-37.87, -6.13) * mm, v(-37.58, -6.07) * mm, v(-37.3, -6.01) * mm]});
            skFitSpline(sketch, "E3226", {"points": [v(-37.3, -6.01) * mm, v(-37.1, -5.96) * mm, v(-36.9, -6.05) * mm, v(-36.71, -6.18) * mm]});
            skFitSpline(sketch, "E3227", {"points": [v(-36.71, -6.18) * mm, v(-36.34, -5.95) * mm, v(-35.98, -5.72) * mm, v(-35.62, -5.49) * mm]});
            skFitSpline(sketch, "E3228", {"points": [v(-35.62, -5.49) * mm, v(-35.63, -5.47) * mm, v(-35.63, -5.45) * mm, v(-35.64, -5.45) * mm]});
            skFitSpline(sketch, "E3229", {"points": [v(-35.64, -5.45) * mm, v(-36.08, -5.26) * mm, v(-36.52, -5.08) * mm, v(-36.96, -4.9) * mm]});
            skFitSpline(sketch, "E3230", {"points": [v(-36.96, -4.9) * mm, v(-37.24, -4.79) * mm, v(-37.37, -4.56) * mm, v(-37.3, -4.3) * mm]});
            skFitSpline(sketch, "E3231", {"points": [v(-37.3, -4.3) * mm, v(-37.23, -4.05) * mm, v(-37, -3.9) * mm, v(-36.72, -3.95) * mm]});
            skFitSpline(sketch, "E3232", {"points": [v(-36.72, -3.95) * mm, v(-36.66, -3.96) * mm, v(-36.6, -3.98) * mm, v(-36.54, -4) * mm]});
            skFitSpline(sketch, "E3233", {"points": [v(-36.54, -4) * mm, v(-36.08, -4.22) * mm, v(-35.62, -4.45) * mm, v(-35.13, -4.58) * mm]});
            skFitSpline(sketch, "E3234", {"points": [v(-35.13, -4.58) * mm, v(-34.93, -4.64) * mm, v(-34.82, -4.77) * mm, v(-34.75, -4.97) * mm]});
            skFitSpline(sketch, "E3235", {"points": [v(-34.75, -4.97) * mm, v(-34.35, -4.73) * mm, v(-33.97, -4.5) * mm, v(-33.6, -4.26) * mm]});
            skFitSpline(sketch, "E3236", {"points": [v(-33.6, -4.26) * mm, v(-33, -3.88) * mm, v(-32.4, -3.48) * mm, v(-31.8, -3.1) * mm]});
            skFitSpline(sketch, "E3237", {"points": [v(-31.8, -3.1) * mm, v(-31.35, -2.81) * mm, v(-30.88, -2.54) * mm, v(-30.4, -2.27) * mm]});
            skFitSpline(sketch, "E3238", {"points": [v(-30.4, -2.27) * mm, v(-30.08, -2.08) * mm, v(-29.74, -1.92) * mm, v(-29.41, -1.74) * mm]});
            skFitSpline(sketch, "E3239", {"points": [v(-29.41, -1.74) * mm, v(-29.33, -1.7) * mm, v(-29.25, -1.65) * mm, v(-29.18, -1.56) * mm]});
            skFitSpline(sketch, "E3240", {"points": [v(-29.18, -1.56) * mm, v(-29.23, -1.57) * mm, v(-29.29, -1.57) * mm, v(-29.34, -1.58) * mm]});
            skFitSpline(sketch, "E3241", {"points": [v(-29.34, -1.58) * mm, v(-29.76, -1.7) * mm, v(-30.18, -1.84) * mm, v(-30.6, -1.94) * mm]});
            skFitSpline(sketch, "E3242", {"points": [v(-30.6, -1.94) * mm, v(-31.6, -2.19) * mm, v(-32.6, -2.42) * mm, v(-33.59, -2.66) * mm]});
            skFitSpline(sketch, "E3243", {"points": [v(-33.59, -2.66) * mm, v(-33.89, -2.73) * mm, v(-34.2, -2.81) * mm, v(-34.5, -2.9) * mm]});
            skFitSpline(sketch, "E3244", {"points": [v(-34.5, -2.9) * mm, v(-34.72, -2.96) * mm, v(-34.93, -2.91) * mm, v(-35.13, -2.8) * mm]});
            skFitSpline(sketch, "E3245", {"points": [v(-35.13, -2.8) * mm, v(-35.63, -2.5) * mm, v(-36.11, -2.16) * mm, v(-36.57, -1.8) * mm]});
            skFitSpline(sketch, "E3246", {"points": [v(-36.57, -1.8) * mm, v(-37.06, -1.42) * mm, v(-37.56, -1.04) * mm, v(-38.07, -0.65) * mm]});
            skFitSpline(sketch, "E3247", {"points": [v(-38.07, -0.65) * mm, v(-38.39, -0.93) * mm, v(-38.72, -1.21) * mm, v(-39.05, -1.5) * mm]});
            skFitSpline(sketch, "E3248", {"points": [v(-39.05, -1.5) * mm, v(-39.92, -2.29) * mm, v(-40.78, -3.07) * mm, v(-41.65, -3.85) * mm]});
            skFitSpline(sketch, "E3249", {"points": [v(-41.65, -3.85) * mm, v(-41.72, -3.92) * mm, v(-41.78, -4) * mm, v(-41.85, -4.09) * mm]});
            skFitSpline(sketch, "E3250", {"points": [v(-41.85, -4.09) * mm, v(-42, -4.25) * mm, v(-42.18, -4.29) * mm, v(-42.37, -4.23) * mm]});
            skFitSpline(sketch, "E3251", {"points": [v(-42.37, -4.23) * mm, v(-42.55, -4.19) * mm, v(-42.66, -4.06) * mm, v(-42.7, -3.88) * mm]});
            skFitSpline(sketch, "E3252", {"points": [v(-42.7, -3.88) * mm, v(-42.74, -3.74) * mm, v(-42.71, -3.6) * mm, v(-42.62, -3.5) * mm]});
            skFitSpline(sketch, "E3253", {"points": [v(-42.62, -3.5) * mm, v(-42.5, -3.35) * mm, v(-42.38, -3.2) * mm, v(-42.24, -3.07) * mm]});
            skFitSpline(sketch, "E3254", {"points": [v(-42.24, -3.07) * mm, v(-41.47, -2.38) * mm, v(-40.7, -1.7) * mm, v(-39.94, -1) * mm]});
            skFitSpline(sketch, "E3255", {"points": [v(-39.94, -1) * mm, v(-39.9, -0.96) * mm, v(-39.85, -0.91) * mm, v(-39.83, -0.84) * mm]});
            skFitSpline(sketch, "E3256", {"points": [v(-39.83, -0.84) * mm, v(-39.9, -0.86) * mm, v(-39.96, -0.87) * mm, v(-40.02, -0.9) * mm]});
            skFitSpline(sketch, "E3257", {"points": [v(-40.02, -0.9) * mm, v(-40.62, -1.18) * mm, v(-41.25, -1.4) * mm, v(-41.82, -1.73) * mm]});
            skFitSpline(sketch, "E3258", {"points": [v(-41.82, -1.73) * mm, v(-42.02, -1.84) * mm, v(-42.22, -1.86) * mm, v(-42.4, -1.72) * mm]});
            skFitSpline(sketch, "E3259", {"points": [v(-42.4, -1.72) * mm, v(-42.57, -1.6) * mm, v(-42.62, -1.42) * mm, v(-42.58, -1.23) * mm]});
            skFitSpline(sketch, "E3260", {"points": [v(-42.58, -1.23) * mm, v(-42.54, -1) * mm, v(-42.4, -0.85) * mm, v(-42.18, -0.76) * mm]});
            skFitSpline(sketch, "E3261", {"points": [v(-42.18, -0.76) * mm, v(-41.61, -0.52) * mm, v(-41.05, -0.28) * mm, v(-40.5, -0.03) * mm]});
            skFitSpline(sketch, "E3262", {"points": [v(-40.5, -0.03) * mm, v(-40.48, -0.03) * mm, v(-40.47, -0.01) * mm, v(-40.45, 0.01) * mm]});
            skFitSpline(sketch, "E3263", {"points": [v(-40.45, 0.01) * mm, v(-40.75, 0.15) * mm, v(-41.05, 0.27) * mm, v(-41.35, 0.4) * mm]});
            skFitSpline(sketch, "E3264", {"points": [v(-41.35, 0.4) * mm, v(-41.51, 0.48) * mm, v(-41.67, 0.55) * mm, v(-41.83, 0.62) * mm]});
            skFitSpline(sketch, "E3265", {"points": [v(-41.83, 0.62) * mm, v(-41.94, 0.67) * mm, v(-42.05, 0.71) * mm, v(-42.16, 0.75) * mm]});
            skFitSpline(sketch, "E3266", {"points": [v(-42.16, 0.75) * mm, v(-42.4, 0.82) * mm, v(-42.58, 1.04) * mm, v(-42.6, 1.27) * mm]});
            skFitSpline(sketch, "E3267", {"points": [v(-42.6, 1.27) * mm, v(-42.61, 1.66) * mm, v(-42.28, 1.9) * mm, v(-41.92, 1.76) * mm]});
            skFitSpline(sketch, "E3268", {"points": [v(-41.92, 1.76) * mm, v(-41.82, 1.72) * mm, v(-41.74, 1.66) * mm, v(-41.64, 1.62) * mm]});
            skFitSpline(sketch, "E3269", {"points": [v(-41.64, 1.62) * mm, v(-41.1, 1.37) * mm, v(-40.55, 1.13) * mm, v(-40, 0.88) * mm]});
            skFitSpline(sketch, "E3270", {"points": [v(-40, 0.88) * mm, v(-39.95, 0.86) * mm, v(-39.89, 0.85) * mm, v(-39.81, 0.86) * mm]});
            skFitSpline(sketch, "E3271", {"points": [v(-39.81, 0.86) * mm, v(-39.87, 0.92) * mm, v(-39.92, 0.97) * mm, v(-39.97, 1.02) * mm]});
            skFitSpline(sketch, "E3272", {"points": [v(-39.97, 1.02) * mm, v(-40.74, 1.72) * mm, v(-41.5, 2.4) * mm, v(-42.27, 3.1) * mm]});
            skFitSpline(sketch, "E3273", {"points": [v(-42.27, 3.1) * mm, v(-42.4, 3.22) * mm, v(-42.53, 3.36) * mm, v(-42.63, 3.5) * mm]});
            skFitSpline(sketch, "E3274", {"points": [v(-42.63, 3.5) * mm, v(-42.78, 3.73) * mm, v(-42.73, 4) * mm, v(-42.53, 4.15) * mm]});
            skFitSpline(sketch, "E3275", {"points": [v(-42.53, 4.15) * mm, v(-42.33, 4.3) * mm, v(-42.05, 4.28) * mm, v(-41.87, 4.1) * mm]});
            skFitSpline(sketch, "E3276", {"points": [v(-41.87, 4.1) * mm, v(-40.71, 2.91) * mm, v(-39.43, 1.87) * mm, v(-38.2, 0.76) * mm]});
            skFitSpline(sketch, "E3277", {"points": [v(-38.2, 0.76) * mm, v(-38.16, 0.72) * mm, v(-38.1, 0.68) * mm, v(-38.04, 0.63) * mm]});
            skFitSpline(sketch, "E3278", {"points": [v(-38.04, 0.63) * mm, v(-37.97, 0.7) * mm, v(-37.9, 0.75) * mm, v(-37.84, 0.8) * mm]});
            skFitSpline(sketch, "E3279", {"points": [v(-37.84, 0.8) * mm, v(-37.14, 1.34) * mm, v(-36.45, 1.88) * mm, v(-35.75, 2.4) * mm]});
            skFitSpline(sketch, "E3280", {"points": [v(-35.75, 2.4) * mm, v(-35.54, 2.56) * mm, v(-35.31, 2.68) * mm, v(-35.1, 2.8) * mm]});
            skFitSpline(sketch, "E3281", {"points": [v(-35.1, 2.8) * mm, v(-34.9, 2.92) * mm, v(-34.7, 2.94) * mm, v(-34.5, 2.88) * mm]});
            skFitSpline(sketch, "E3282", {"points": [v(-34.5, 2.88) * mm, v(-33.52, 2.64) * mm, v(-32.55, 2.4) * mm, v(-31.59, 2.17) * mm]});
            skFitSpline(sketch, "E3283", {"points": [v(-31.59, 2.17) * mm, v(-30.76, 1.96) * mm, v(-29.93, 1.75) * mm, v(-29.1, 1.55) * mm]});
            skFitSpline(sketch, "E3284", {"points": [v(-29.1, 1.55) * mm, v(-29.17, 1.6) * mm, v(-29.25, 1.65) * mm, v(-29.33, 1.7) * mm]});
            skFitSpline(sketch, "E3285", {"points": [v(-29.33, 1.7) * mm, v(-30.02, 2.07) * mm, v(-30.7, 2.44) * mm, v(-31.39, 2.83) * mm]});
            skFitSpline(sketch, "E3286", {"points": [v(-31.39, 2.83) * mm, v(-31.7, 3) * mm, v(-32, 3.22) * mm, v(-32.32, 3.42) * mm]});
            skFitSpline(sketch, "E3287", {"points": [v(-32.32, 3.42) * mm, v(-33.09, 3.91) * mm, v(-33.86, 4.4) * mm, v(-34.64, 4.9) * mm]});
            skFitSpline(sketch, "E3288", {"points": [v(-34.64, 4.9) * mm, v(-34.66, 4.92) * mm, v(-34.7, 4.93) * mm, v(-34.74, 4.96) * mm]});
            skFitSpline(sketch, "E3289", {"points": [v(-34.74, 4.96) * mm, v(-34.84, 4.68) * mm, v(-35.06, 4.6) * mm, v(-35.31, 4.5) * mm]});
            skFitSpline(sketch, "E3290", {"points": [v(-35.31, 4.5) * mm, v(-35.73, 4.36) * mm, v(-36.14, 4.17) * mm, v(-36.55, 4) * mm]});
            skFitSpline(sketch, "E3291", {"points": [v(-36.55, 4) * mm, v(-36.73, 3.9) * mm, v(-36.9, 3.87) * mm, v(-37.09, 4) * mm]});
            skFitSpline(sketch, "E3292", {"points": [v(-37.09, 4) * mm, v(-37.25, 4.11) * mm, v(-37.33, 4.27) * mm, v(-37.31, 4.47) * mm]});
            skFitSpline(sketch, "E3293", {"points": [v(-37.31, 4.47) * mm, v(-37.3, 4.67) * mm, v(-37.2, 4.8) * mm, v(-37.01, 4.87) * mm]});
            skFitSpline(sketch, "E3294", {"points": [v(-37.01, 4.87) * mm, v(-36.75, 4.99) * mm, v(-36.5, 5.1) * mm, v(-36.23, 5.22) * mm]});
            skFitSpline(sketch, "E3295", {"points": [v(-36.23, 5.22) * mm, v(-36.03, 5.3) * mm, v(-35.82, 5.37) * mm, v(-35.6, 5.46) * mm]});
            skFitSpline(sketch, "E3296", {"points": [v(-35.6, 5.46) * mm, v(-35.97, 5.7) * mm, v(-36.34, 5.94) * mm, v(-36.7, 6.17) * mm]});
            skFitSpline(sketch, "E3297", {"points": [v(-36.7, 6.17) * mm, v(-36.8, 6.12) * mm, v(-36.9, 6.06) * mm, v(-36.99, 6.03) * mm]});
            skFitSpline(sketch, "E3298", {"points": [v(-36.99, 6.03) * mm, v(-37.09, 6) * mm, v(-37.2, 5.97) * mm, v(-37.3, 6) * mm]});
            skFitSpline(sketch, "E3299", {"points": [v(-37.3, 6) * mm, v(-37.58, 6.07) * mm, v(-37.88, 6.13) * mm, v(-38.1, 6.35) * mm]});
            skFitSpline(sketch, "E3300", {"points": [v(-38.1, 6.35) * mm, v(-38.19, 6.45) * mm, v(-38.26, 6.58) * mm, v(-38.32, 6.7) * mm]});
            skFitSpline(sketch, "E3301", {"points": [v(-38.32, 6.7) * mm, v(-38.38, 6.83) * mm, v(-38.42, 6.96) * mm, v(-38.45, 7.1) * mm]});
            skFitSpline(sketch, "E3302", {"points": [v(-38.45, 7.1) * mm, v(-38.5, 7.28) * mm, v(-38.47, 7.46) * mm, v(-38.33, 7.6) * mm]});
            skFitSpline(sketch, "E3303", {"points": [v(-38.33, 7.6) * mm, v(-38.27, 7.66) * mm, v(-38.24, 7.74) * mm, v(-38.22, 7.8) * mm]});
            skFitSpline(sketch, "E3304", {"points": [v(-38.22, 7.8) * mm, v(-38.15, 7.99) * mm, v(-38.03, 8.1) * mm, v(-37.84, 8.14) * mm]});
            skFitSpline(sketch, "E3305", {"points": [v(-37.84, 8.14) * mm, v(-37.7, 8.17) * mm, v(-37.56, 8.21) * mm, v(-37.42, 8.23) * mm]});
            skFitSpline(sketch, "E3306", {"points": [v(-37.42, 8.23) * mm, v(-37.12, 8.28) * mm, v(-36.85, 8.2) * mm, v(-36.63, 7.99) * mm]});
            skFitSpline(sketch, "E3307", {"points": [v(-36.63, 7.99) * mm, v(-36.6, 7.96) * mm, v(-36.59, 7.93) * mm, v(-36.56, 7.92) * mm]});
            skFitSpline(sketch, "E3308", {"points": [v(-36.56, 7.92) * mm, v(-36.24, 7.74) * mm, v(-36.15, 7.45) * mm, v(-36.17, 7.1) * mm]});
            skFitSpline(sketch, "E3309", {"points": [v(-36.17, 7.1) * mm, v(-35.78, 6.9) * mm, v(-35.4, 6.7) * mm, v(-35.01, 6.5) * mm]});
            skFitSpline(sketch, "E3310", {"points": [v(-35.01, 6.5) * mm, v(-35.05, 6.8) * mm, v(-35.08, 7.07) * mm, v(-35.12, 7.34) * mm]});
            skFitSpline(sketch, "E3311", {"points": [v(-35.12, 7.34) * mm, v(-35.14, 7.57) * mm, v(-35.18, 7.8) * mm, v(-35.2, 8.03) * mm]});
            skFitSpline(sketch, "E3312", {"points": [v(-35.2, 8.03) * mm, v(-35.23, 8.3) * mm, v(-35.05, 8.53) * mm, v(-34.8, 8.56) * mm]});
            skFitSpline(sketch, "E3313", {"points": [v(-34.8, 8.56) * mm, v(-34.5, 8.6) * mm, v(-34.27, 8.44) * mm, v(-34.23, 8.17) * mm]});
            skFitSpline(sketch, "E3314", {"points": [v(-34.23, 8.17) * mm, v(-34.2, 7.92) * mm, v(-34.18, 7.68) * mm, v(-34.15, 7.43) * mm]});
            skFitSpline(sketch, "E3315", {"points": [v(-34.15, 7.43) * mm, v(-34.11, 7.17) * mm, v(-34.08, 6.9) * mm, v(-34.02, 6.65) * mm]});
            skFitSpline(sketch, "E3316", {"points": [v(-34.02, 6.65) * mm, v(-33.97, 6.42) * mm, v(-33.95, 6.2) * mm, v(-34.14, 6.01) * mm]});
            skFitSpline(sketch, "E3317", {"points": [v(-34.14, 6.01) * mm, v(-34.07, 5.97) * mm, v(-34.01, 5.93) * mm, v(-33.95, 5.9) * mm]});
            skFitSpline(sketch, "E3318", {"points": [v(-33.95, 5.9) * mm, v(-32.87, 5.34) * mm, v(-31.79, 4.8) * mm, v(-30.72, 4.22) * mm]});
            skFitSpline(sketch, "E3319", {"points": [v(-30.72, 4.22) * mm, v(-30.03, 3.85) * mm, v(-29.38, 3.42) * mm, v(-28.7, 3.02) * mm]});
            skFitSpline(sketch, "E3320", {"points": [v(-28.7, 3.02) * mm, v(-28.61, 2.97) * mm, v(-28.53, 2.91) * mm, v(-28.44, 2.86) * mm]});
            skFitSpline(sketch, "E3321", {"points": [v(-28.44, 2.86) * mm, v(-28.43, 2.86) * mm, v(-28.4, 2.87) * mm, v(-28.36, 2.88) * mm]});
            skFitSpline(sketch, "E3322", {"points": [v(-28.36, 2.88) * mm, v(-28.48, 2.98) * mm, v(-28.57, 3.08) * mm, v(-28.68, 3.18) * mm]});
            skFitSpline(sketch, "E3323", {"points": [v(-28.68, 3.18) * mm, v(-29.63, 4.07) * mm, v(-30.52, 5.05) * mm, v(-31.42, 6) * mm]});
            skFitSpline(sketch, "E3324", {"points": [v(-31.42, 6) * mm, v(-31.67, 6.26) * mm, v(-31.92, 6.54) * mm, v(-32.19, 6.79) * mm]});
            skFitSpline(sketch, "E3325", {"points": [v(-32.19, 6.79) * mm, v(-32.43, 7.02) * mm, v(-32.48, 7.3) * mm, v(-32.44, 7.62) * mm]});
            skFitSpline(sketch, "E3326", {"points": [v(-32.44, 7.62) * mm, v(-32.43, 7.68) * mm, v(-32.42, 7.75) * mm, v(-32.42, 7.81) * mm]});
            skFitSpline(sketch, "E3327", {"points": [v(-32.42, 7.81) * mm, v(-32.44, 8.28) * mm, v(-32.37, 8.73) * mm, v(-32.3, 9.2) * mm]});
            skFitSpline(sketch, "E3328", {"points": [v(-32.3, 9.2) * mm, v(-32.26, 9.54) * mm, v(-32.23, 9.89) * mm, v(-32.18, 10.24) * mm]});
            skFitSpline(sketch, "E3329", {"points": [v(-32.18, 10.24) * mm, v(-32.14, 10.5) * mm, v(-32.1, 10.75) * mm, v(-32.05, 11.03) * mm]});
            skFitSpline(sketch, "E3330", {"points": [v(-32.05, 11.03) * mm, v(-32.12, 11.06) * mm, v(-32.2, 11.09) * mm, v(-32.27, 11.11) * mm]});
            skFitSpline(sketch, "E3331", {"points": [v(-32.27, 11.11) * mm, v(-33.63, 11.56) * mm, v(-34.98, 12) * mm, v(-36.34, 12.44) * mm]});
            skFitSpline(sketch, "E3332", {"points": [v(-36.34, 12.44) * mm, v(-36.54, 12.5) * mm, v(-36.74, 12.55) * mm, v(-36.94, 12.6) * mm]});
            skFitSpline(sketch, "E3333", {"points": [v(-36.94, 12.6) * mm, v(-37.18, 12.66) * mm, v(-37.37, 12.9) * mm, v(-37.34, 13.13) * mm]});
            skFitSpline(sketch, "E3334", {"points": [v(-37.34, 13.13) * mm, v(-37.3, 13.4) * mm, v(-37.1, 13.58) * mm, v(-36.83, 13.56) * mm]});
            skFitSpline(sketch, "E3335", {"points": [v(-36.83, 13.56) * mm, v(-36.64, 13.54) * mm, v(-36.46, 13.5) * mm, v(-36.29, 13.45) * mm]});
            skFitSpline(sketch, "E3336", {"points": [v(-36.29, 13.45) * mm, v(-35.3, 13.14) * mm, v(-34.33, 12.82) * mm, v(-33.35, 12.5) * mm]});
            skFitSpline(sketch, "E3337", {"points": [v(-33.35, 12.5) * mm, v(-33.28, 12.48) * mm, v(-33.2, 12.46) * mm, v(-33.1, 12.47) * mm]});
            skFitSpline(sketch, "E3338", {"points": [v(-33.1, 12.47) * mm, v(-33.15, 12.5) * mm, v(-33.18, 12.56) * mm, v(-33.23, 12.59) * mm]});
            skFitSpline(sketch, "E3339", {"points": [v(-33.23, 12.59) * mm, v(-33.78, 12.97) * mm, v(-34.29, 13.41) * mm, v(-34.87, 13.75) * mm]});
            skFitSpline(sketch, "E3340", {"points": [v(-34.87, 13.75) * mm, v(-35.17, 13.93) * mm, v(-35.25, 14.24) * mm, v(-35.07, 14.49) * mm]});
            skFitSpline(sketch, "E3341", {"points": [v(-35.07, 14.49) * mm, v(-34.9, 14.74) * mm, v(-34.5, 14.76) * mm, v(-34.23, 14.57) * mm]});
            skFitSpline(sketch, "E3342", {"points": [v(-34.23, 14.57) * mm, v(-33.76, 14.2) * mm, v(-33.27, 13.84) * mm, v(-32.78, 13.47) * mm]});
            skFitSpline(sketch, "E3343", {"points": [v(-32.78, 13.47) * mm, v(-32.76, 13.46) * mm, v(-32.74, 13.46) * mm, v(-32.68, 13.44) * mm]});
            skFitSpline(sketch, "E3344", {"points": [v(-32.68, 13.44) * mm, v(-32.71, 13.73) * mm, v(-32.74, 14) * mm, v(-32.77, 14.26) * mm]});
            skFitSpline(sketch, "E3345", {"points": [v(-32.77, 14.26) * mm, v(-32.79, 14.5) * mm, v(-32.8, 14.72) * mm, v(-32.84, 14.95) * mm]});
            skFitSpline(sketch, "E3346", {"points": [v(-32.84, 14.95) * mm, v(-32.85, 15.08) * mm, v(-32.88, 15.2) * mm, v(-32.9, 15.32) * mm]});
            skFitSpline(sketch, "E3347", {"points": [v(-32.9, 15.32) * mm, v(-32.98, 15.62) * mm, v(-32.73, 15.98) * mm, v(-32.43, 16.01) * mm]});
            skFitSpline(sketch, "E3348", {"points": [v(-32.43, 16.01) * mm, v(-32.15, 16.04) * mm, v(-31.9, 15.85) * mm, v(-31.9, 15.56) * mm]});
            skFitSpline(sketch, "E3349", {"points": [v(-31.9, 15.56) * mm, v(-31.9, 14.92) * mm, v(-31.78, 14.3) * mm, v(-31.73, 13.67) * mm]});
            skFitSpline(sketch, "E3350", {"points": [v(-31.73, 13.67) * mm, v(-31.72, 13.55) * mm, v(-31.7, 13.43) * mm, v(-31.67, 13.3) * mm]});
            skLineSegment(sketch, "E3351", {"start": v(-31.67, 13.3) * mm, "end": v(-31.62, 13.3) * mm});
            skFitSpline(sketch, "E3352", {"points": [v(-31.62, 13.3) * mm, v(-31.6, 13.4) * mm, v(-31.57, 13.49) * mm, v(-31.55, 13.58) * mm]});
            skFitSpline(sketch, "E3353", {"points": [v(-31.55, 13.58) * mm, v(-31.33, 14.63) * mm, v(-31.1, 15.67) * mm, v(-30.88, 16.72) * mm]});
            skFitSpline(sketch, "E3354", {"points": [v(-30.88, 16.72) * mm, v(-30.85, 16.85) * mm, v(-30.8, 16.98) * mm, v(-30.73, 17.1) * mm]});
            skFitSpline(sketch, "E3355", {"points": [v(-30.73, 17.1) * mm, v(-30.6, 17.32) * mm, v(-30.36, 17.4) * mm, v(-30.14, 17.3) * mm]});
            skFitSpline(sketch, "E3356", {"points": [v(-30.14, 17.3) * mm, v(-29.91, 17.2) * mm, v(-29.78, 16.97) * mm, v(-29.85, 16.74) * mm]});
            skFitSpline(sketch, "E3357", {"points": [v(-29.85, 16.74) * mm, v(-30.18, 15.58) * mm, v(-30.38, 14.4) * mm, v(-30.63, 13.23) * mm]});
            skFitSpline(sketch, "E3358", {"points": [v(-30.63, 13.23) * mm, v(-30.73, 12.77) * mm, v(-30.82, 12.31) * mm, v(-30.91, 11.85) * mm]});
            skFitSpline(sketch, "E3359", {"points": [v(-30.91, 11.85) * mm, v(-30.93, 11.8) * mm, v(-30.93, 11.74) * mm, v(-30.93, 11.67) * mm]});
            skFitSpline(sketch, "E3360", {"points": [v(-30.93, 11.67) * mm, v(-30.88, 11.65) * mm, v(-30.83, 11.62) * mm, v(-30.78, 11.6) * mm]});
            skFitSpline(sketch, "E3361", {"points": [v(-30.78, 11.6) * mm, v(-29.95, 11.26) * mm, v(-29.11, 10.93) * mm, v(-28.28, 10.57) * mm]});
            skFitSpline(sketch, "E3362", {"points": [v(-28.28, 10.57) * mm, v(-28.03, 10.47) * mm, v(-27.79, 10.31) * mm, v(-27.55, 10.17) * mm]});
            skFitSpline(sketch, "E3363", {"points": [v(-27.55, 10.17) * mm, v(-27.4, 10.08) * mm, v(-27.28, 9.95) * mm, v(-27.23, 9.77) * mm]});
            skFitSpline(sketch, "E3364", {"points": [v(-27.23, 9.77) * mm, v(-26.8, 8.29) * mm, v(-26.37, 6.8) * mm, v(-25.95, 5.33) * mm]});
            skFitSpline(sketch, "E3365", {"points": [v(-25.95, 5.33) * mm, v(-25.87, 5.05) * mm, v(-25.81, 4.77) * mm, v(-25.74, 4.5) * mm]});
            skFitSpline(sketch, "E3366", {"points": [v(-25.74, 4.5) * mm, v(-25.73, 4.44) * mm, v(-25.7, 4.39) * mm, v(-25.65, 4.34) * mm]});
            skFitSpline(sketch, "E3367", {"points": [v(-25.65, 4.34) * mm, v(-25.67, 4.63) * mm, v(-25.7, 4.91) * mm, v(-25.7, 5.2) * mm]});
            skFitSpline(sketch, "E3368", {"points": [v(-25.7, 5.2) * mm, v(-25.7, 5.9) * mm, v(-25.7, 6.6) * mm, v(-25.69, 7.29) * mm]});
            skFitSpline(sketch, "E3369", {"points": [v(-25.69, 7.29) * mm, v(-25.67, 8.02) * mm, v(-25.62, 8.75) * mm, v(-25.6, 9.48) * mm]});
            skFitSpline(sketch, "E3370", {"points": [v(-25.6, 9.48) * mm, v(-25.57, 9.91) * mm, v(-25.56, 10.35) * mm, v(-25.54, 10.78) * mm]});
            skFitSpline(sketch, "E3371", {"points": [v(-25.54, 10.78) * mm, v(-25.54, 10.83) * mm, v(-25.55, 10.88) * mm, v(-25.55, 10.97) * mm]});
            skFitSpline(sketch, "E3372", {"points": [v(-25.55, 10.97) * mm, v(-25.86, 10.9) * mm, v(-26.04, 11.1) * mm, v(-26.25, 11.27) * mm]});
            skFitSpline(sketch, "E3373", {"points": [v(-26.25, 11.27) * mm, v(-26.55, 11.51) * mm, v(-26.87, 11.74) * mm, v(-27.18, 11.98) * mm]});
            skFitSpline(sketch, "E3374", {"points": [v(-27.18, 11.98) * mm, v(-27.24, 12.03) * mm, v(-27.32, 12.07) * mm, v(-27.37, 12.12) * mm]});
            skFitSpline(sketch, "E3375", {"points": [v(-27.37, 12.12) * mm, v(-27.6, 12.31) * mm, v(-27.6, 12.61) * mm, v(-27.42, 12.82) * mm]});
            skFitSpline(sketch, "E3376", {"points": [v(-27.42, 12.82) * mm, v(-27.24, 13.03) * mm, v(-26.96, 13.05) * mm, v(-26.73, 12.87) * mm]});
            skFitSpline(sketch, "E3377", {"points": [v(-26.73, 12.87) * mm, v(-26.34, 12.58) * mm, v(-25.94, 12.28) * mm, v(-25.52, 11.97) * mm]});
            skFitSpline(sketch, "E3378", {"points": [v(-25.52, 11.97) * mm, v(-25.5, 12.4) * mm, v(-25.5, 12.83) * mm, v(-25.48, 13.27) * mm]});
            skFitSpline(sketch, "E3379", {"points": [v(-25.48, 13.27) * mm, v(-25.52, 13.3) * mm, v(-25.57, 13.32) * mm, v(-25.62, 13.36) * mm]});
            skFitSpline(sketch, "E3380", {"points": [v(-25.62, 13.36) * mm, v(-25.76, 13.46) * mm, v(-25.9, 13.56) * mm, v(-25.94, 13.74) * mm]});
            skFitSpline(sketch, "E3381", {"points": [v(-25.94, 13.74) * mm, v(-25.99, 13.95) * mm, v(-26.02, 14.17) * mm, v(-26.03, 14.4) * mm]});
            skFitSpline(sketch, "E3382", {"points": [v(-26.03, 14.4) * mm, v(-26.04, 14.6) * mm, v(-25.97, 14.79) * mm, v(-25.82, 14.94) * mm]});
            skFitSpline(sketch, "E3383", {"points": [v(-25.82, 14.94) * mm, v(-25.73, 15.05) * mm, v(-25.64, 15.16) * mm, v(-25.53, 15.26) * mm]});
            skFitSpline(sketch, "E3384", {"points": [v(-25.53, 15.26) * mm, v(-25.4, 15.39) * mm, v(-25.25, 15.45) * mm, v(-25.05, 15.4) * mm]});
            skFitSpline(sketch, "E3385", {"points": [v(-25.05, 15.4) * mm, v(-24.98, 15.37) * mm, v(-24.9, 15.38) * mm, v(-24.82, 15.4) * mm]});
            skFitSpline(sketch, "E3386", {"points": [v(-24.82, 15.4) * mm, v(-24.64, 15.45) * mm, v(-24.49, 15.4) * mm, v(-24.36, 15.27) * mm]});
            skFitSpline(sketch, "E3387", {"points": [v(-24.36, 15.27) * mm, v(-24.25, 15.17) * mm, v(-24.15, 15.05) * mm, v(-24.05, 14.94) * mm]});
            skFitSpline(sketch, "E3388", {"points": [v(-24.05, 14.94) * mm, v(-23.86, 14.7) * mm, v(-23.8, 14.45) * mm, v(-23.86, 14.15) * mm]});
            skFitSpline(sketch, "E3389", {"points": [v(-23.86, 14.15) * mm, v(-23.88, 14.04) * mm, v(-23.9, 13.93) * mm, v(-23.91, 13.82) * mm]});
            skFitSpline(sketch, "E3390", {"points": [v(-23.91, 13.82) * mm, v(-23.94, 13.63) * mm, v(-24.06, 13.51) * mm, v(-24.2, 13.4) * mm]});
            skFitSpline(sketch, "E3391", {"points": [v(-24.2, 13.4) * mm, v(-24.25, 13.35) * mm, v(-24.32, 13.32) * mm, v(-24.4, 13.27) * mm]});
            skFitSpline(sketch, "E3392", {"points": [v(-24.4, 13.27) * mm, v(-24.4, 12.86) * mm, v(-24.37, 12.42) * mm, v(-24.35, 11.95) * mm]});
            skFitSpline(sketch, "E3393", {"points": [v(-24.35, 11.95) * mm, v(-24.27, 12.01) * mm, v(-24.22, 12.06) * mm, v(-24.16, 12.1) * mm]});
            skFitSpline(sketch, "E3394", {"points": [v(-24.16, 12.1) * mm, v(-23.94, 12.28) * mm, v(-23.7, 12.45) * mm, v(-23.48, 12.62) * mm]});
            skFitSpline(sketch, "E3395", {"points": [v(-23.48, 12.62) * mm, v(-23.37, 12.7) * mm, v(-23.26, 12.78) * mm, v(-23.15, 12.87) * mm]});
            skFitSpline(sketch, "E3396", {"points": [v(-23.15, 12.87) * mm, v(-22.92, 13.05) * mm, v(-22.63, 13.03) * mm, v(-22.45, 12.81) * mm]});
            skFitSpline(sketch, "E3397", {"points": [v(-22.45, 12.81) * mm, v(-22.27, 12.6) * mm, v(-22.3, 12.3) * mm, v(-22.52, 12.1) * mm]});
            skFitSpline(sketch, "E3398", {"points": [v(-22.52, 12.1) * mm, v(-22.67, 11.98) * mm, v(-22.85, 11.88) * mm, v(-23, 11.76) * mm]});
            skFitSpline(sketch, "E3399", {"points": [v(-23, 11.76) * mm, v(-23.23, 11.6) * mm, v(-23.45, 11.42) * mm, v(-23.66, 11.24) * mm]});
            skFitSpline(sketch, "E3400", {"points": [v(-23.66, 11.24) * mm, v(-23.85, 11.07) * mm, v(-24.03, 10.9) * mm, v(-24.32, 10.98) * mm]});
            skFitSpline(sketch, "E3401", {"points": [v(-24.32, 10.98) * mm, v(-24.33, 10.9) * mm, v(-24.34, 10.84) * mm, v(-24.34, 10.79) * mm]});
            skFitSpline(sketch, "E3402", {"points": [v(-24.34, 10.79) * mm, v(-24.33, 10.37) * mm, v(-24.31, 9.96) * mm, v(-24.3, 9.55) * mm]});
            skFitSpline(sketch, "E3403", {"points": [v(-24.3, 9.55) * mm, v(-24.28, 9.16) * mm, v(-24.28, 8.76) * mm, v(-24.25, 8.37) * mm]});
            skFitSpline(sketch, "E3404", {"points": [v(-24.25, 8.37) * mm, v(-24.17, 7.46) * mm, v(-24.16, 6.54) * mm, v(-24.17, 5.62) * mm]});
            skFitSpline(sketch, "E3405", {"points": [v(-24.17, 5.62) * mm, v(-24.17, 5.32) * mm, v(-24.2, 5.02) * mm, v(-24.2, 4.71) * mm]});
            skFitSpline(sketch, "E3406", {"points": [v(-24.2, 4.71) * mm, v(-24.21, 4.6) * mm, v(-24.21, 4.5) * mm, v(-24.19, 4.37) * mm]});
            skFitSpline(sketch, "E3407", {"points": [v(-24.19, 4.37) * mm, v(-24.17, 4.41) * mm, v(-24.14, 4.45) * mm, v(-24.13, 4.5) * mm]});
            skFitSpline(sketch, "E3408", {"points": [v(-24.13, 4.5) * mm, v(-23.77, 6.04) * mm, v(-23.3, 7.55) * mm, v(-22.84, 9.06) * mm]});
            skFitSpline(sketch, "E3409", {"points": [v(-22.84, 9.06) * mm, v(-22.78, 9.26) * mm, v(-22.72, 9.46) * mm, v(-22.68, 9.66) * mm]});
            skFitSpline(sketch, "E3410", {"points": [v(-22.68, 9.66) * mm, v(-22.62, 9.95) * mm, v(-22.43, 10.12) * mm, v(-22.18, 10.26) * mm]});
            skFitSpline(sketch, "E3411", {"points": [v(-22.18, 10.26) * mm, v(-21.53, 10.64) * mm, v(-20.82, 10.9) * mm, v(-20.13, 11.2) * mm]});
            skFitSpline(sketch, "E3412", {"points": [v(-20.13, 11.2) * mm, v(-19.75, 11.36) * mm, v(-19.35, 11.51) * mm, v(-18.94, 11.68) * mm]});
            skFitSpline(sketch, "E3413", {"points": [v(-18.94, 11.68) * mm, v(-18.96, 11.82) * mm, v(-19, 11.97) * mm, v(-19.02, 12.11) * mm]});
            skFitSpline(sketch, "E3414", {"points": [v(-19.02, 12.11) * mm, v(-19.28, 13.34) * mm, v(-19.53, 14.56) * mm, v(-19.79, 15.79) * mm]});
            skFitSpline(sketch, "E3415", {"points": [v(-19.79, 15.79) * mm, v(-19.85, 16.1) * mm, v(-19.94, 16.4) * mm, v(-20.03, 16.7) * mm]});
            skFitSpline(sketch, "E3416", {"points": [v(-20.03, 16.7) * mm, v(-20.1, 16.95) * mm, v(-19.98, 17.2) * mm, v(-19.74, 17.3) * mm]});
            skFitSpline(sketch, "E3417", {"points": [v(-19.74, 17.3) * mm, v(-19.5, 17.4) * mm, v(-19.25, 17.31) * mm, v(-19.13, 17.07) * mm]});
            skFitSpline(sketch, "E3418", {"points": [v(-19.13, 17.07) * mm, v(-19.06, 16.93) * mm, v(-19.01, 16.77) * mm, v(-18.98, 16.62) * mm]});
            skFitSpline(sketch, "E3419", {"points": [v(-18.98, 16.62) * mm, v(-18.75, 15.58) * mm, v(-18.53, 14.54) * mm, v(-18.3, 13.5) * mm]});
            skFitSpline(sketch, "E3420", {"points": [v(-18.3, 13.5) * mm, v(-18.3, 13.43) * mm, v(-18.27, 13.35) * mm, v(-18.21, 13.28) * mm]});
            skFitSpline(sketch, "E3421", {"points": [v(-18.21, 13.28) * mm, v(-18.18, 13.48) * mm, v(-18.15, 13.67) * mm, v(-18.13, 13.87) * mm]});
            skFitSpline(sketch, "E3422", {"points": [v(-18.13, 13.87) * mm, v(-18.07, 14.44) * mm, v(-18.02, 15) * mm, v(-17.98, 15.57) * mm]});
            skFitSpline(sketch, "E3423", {"points": [v(-17.98, 15.57) * mm, v(-17.95, 15.93) * mm, v(-17.57, 16.13) * mm, v(-17.26, 15.95) * mm]});
            skFitSpline(sketch, "E3424", {"points": [v(-17.26, 15.95) * mm, v(-17.04, 15.83) * mm, v(-16.93, 15.53) * mm, v(-16.98, 15.29) * mm]});
            skFitSpline(sketch, "E3425", {"points": [v(-16.98, 15.29) * mm, v(-17.02, 15.13) * mm, v(-17.03, 14.96) * mm, v(-17.05, 14.8) * mm]});
            skFitSpline(sketch, "E3426", {"points": [v(-17.05, 14.8) * mm, v(-17.1, 14.41) * mm, v(-17.14, 14.03) * mm, v(-17.18, 13.65) * mm]});
            skFitSpline(sketch, "E3427", {"points": [v(-17.18, 13.65) * mm, v(-17.19, 13.59) * mm, v(-17.2, 13.52) * mm, v(-17.2, 13.4) * mm]});
            skFitSpline(sketch, "E3428", {"points": [v(-17.2, 13.4) * mm, v(-16.93, 13.6) * mm, v(-16.7, 13.76) * mm, v(-16.47, 13.93) * mm]});
            skFitSpline(sketch, "E3429", {"points": [v(-16.47, 13.93) * mm, v(-16.28, 14.07) * mm, v(-16.1, 14.2) * mm, v(-15.9, 14.33) * mm]});
            skFitSpline(sketch, "E3430", {"points": [v(-15.9, 14.33) * mm, v(-15.83, 14.4) * mm, v(-15.76, 14.45) * mm, v(-15.69, 14.52) * mm]});
            skFitSpline(sketch, "E3431", {"points": [v(-15.69, 14.52) * mm, v(-15.52, 14.7) * mm, v(-15.31, 14.72) * mm, v(-15.1, 14.68) * mm]});
            skFitSpline(sketch, "E3432", {"points": [v(-15.1, 14.68) * mm, v(-14.9, 14.63) * mm, v(-14.77, 14.5) * mm, v(-14.73, 14.3) * mm]});
            skFitSpline(sketch, "E3433", {"points": [v(-14.73, 14.3) * mm, v(-14.69, 14.1) * mm, v(-14.76, 13.94) * mm, v(-14.92, 13.82) * mm]});
            skFitSpline(sketch, "E3434", {"points": [v(-14.92, 13.82) * mm, v(-15.07, 13.7) * mm, v(-15.24, 13.61) * mm, v(-15.4, 13.5) * mm]});
            skFitSpline(sketch, "E3435", {"points": [v(-15.4, 13.5) * mm, v(-15.83, 13.19) * mm, v(-16.26, 12.87) * mm, v(-16.7, 12.55) * mm]});
            skFitSpline(sketch, "E3436", {"points": [v(-16.7, 12.55) * mm, v(-16.72, 12.53) * mm, v(-16.74, 12.5) * mm, v(-16.75, 12.44) * mm]});
            skFitSpline(sketch, "E3437", {"points": [v(-16.75, 12.44) * mm, v(-16.67, 12.46) * mm, v(-16.59, 12.48) * mm, v(-16.5, 12.5) * mm]});
            skFitSpline(sketch, "E3438", {"points": [v(-16.5, 12.5) * mm, v(-15.53, 12.82) * mm, v(-14.55, 13.15) * mm, v(-13.57, 13.46) * mm]});
            skFitSpline(sketch, "E3439", {"points": [v(-13.57, 13.46) * mm, v(-13.4, 13.51) * mm, v(-13.23, 13.55) * mm, v(-13.05, 13.56) * mm]});
            skFitSpline(sketch, "E3440", {"points": [v(-13.05, 13.56) * mm, v(-12.8, 13.58) * mm, v(-12.58, 13.4) * mm, v(-12.55, 13.15) * mm]});
            skFitSpline(sketch, "E3441", {"points": [v(-12.55, 13.15) * mm, v(-12.52, 12.91) * mm, v(-12.68, 12.67) * mm, v(-12.92, 12.6) * mm]});
            skFitSpline(sketch, "E3442", {"points": [v(-12.92, 12.6) * mm, v(-13.17, 12.54) * mm, v(-13.43, 12.48) * mm, v(-13.68, 12.4) * mm]});
            skFitSpline(sketch, "E3443", {"points": [v(-13.68, 12.4) * mm, v(-15.04, 11.96) * mm, v(-16.4, 11.5) * mm, v(-17.75, 11.06) * mm]});
            skFitSpline(sketch, "E3444", {"points": [v(-17.75, 11.06) * mm, v(-17.77, 11.05) * mm, v(-17.8, 11.04) * mm, v(-17.83, 11.02) * mm]});
            skFitSpline(sketch, "E3445", {"points": [v(-17.83, 11.02) * mm, v(-17.8, 10.85) * mm, v(-17.76, 10.67) * mm, v(-17.74, 10.5) * mm]});
            skFitSpline(sketch, "E3446", {"points": [v(-17.74, 10.5) * mm, v(-17.67, 9.97) * mm, v(-17.6, 9.45) * mm, v(-17.54, 8.93) * mm]});
            skFitSpline(sketch, "E3447", {"points": [v(-17.54, 8.93) * mm, v(-17.5, 8.45) * mm, v(-17.47, 7.97) * mm, v(-17.44, 7.5) * mm]});
            skFitSpline(sketch, "E3448", {"points": [v(-17.44, 7.5) * mm, v(-17.42, 7.22) * mm, v(-17.5, 6.99) * mm, v(-17.7, 6.78) * mm]});
            skFitSpline(sketch, "E3449", {"points": [v(-17.7, 6.78) * mm, v(-18.39, 6.08) * mm, v(-19.06, 5.36) * mm, v(-19.74, 4.66) * mm]});
            skFitSpline(sketch, "E3450", {"points": [v(-19.74, 4.66) * mm, v(-20.29, 4.1) * mm, v(-20.85, 3.55) * mm, v(-21.4, 3) * mm]});
            skFitSpline(sketch, "E3451", {"points": [v(-21.4, 3) * mm, v(-21.45, 2.94) * mm, v(-21.5, 2.9) * mm, v(-21.51, 2.81) * mm]});
            skFitSpline(sketch, "E3452", {"points": [v(-21.51, 2.81) * mm, v(-21.29, 2.95) * mm, v(-21.06, 3.1) * mm, v(-20.83, 3.24) * mm]});
            skFitSpline(sketch, "E3453", {"points": [v(-20.83, 3.24) * mm, v(-20.1, 3.66) * mm, v(-19.37, 4.09) * mm, v(-18.62, 4.5) * mm]});
            skFitSpline(sketch, "E3454", {"points": [v(-18.62, 4.5) * mm, v(-17.86, 4.9) * mm, v(-17.08, 5.3) * mm, v(-16.31, 5.7) * mm]});
            skFitSpline(sketch, "E3455", {"points": [v(-16.31, 5.7) * mm, v(-16.13, 5.8) * mm, v(-15.94, 5.9) * mm, v(-15.74, 6) * mm]});
            skFitSpline(sketch, "E3456", {"points": [v(-15.74, 6) * mm, v(-15.94, 6.22) * mm, v(-15.91, 6.47) * mm, v(-15.84, 6.72) * mm]});
            skFitSpline(sketch, "E3457", {"points": [v(-15.84, 6.72) * mm, v(-15.72, 7.13) * mm, v(-15.72, 7.56) * mm, v(-15.68, 7.98) * mm]});
            skFitSpline(sketch, "E3458", {"points": [v(-15.68, 7.98) * mm, v(-15.67, 8.05) * mm, v(-15.67, 8.12) * mm, v(-15.65, 8.2) * mm]});
            skFitSpline(sketch, "E3459", {"points": [v(-15.65, 8.2) * mm, v(-15.58, 8.47) * mm, v(-15.32, 8.62) * mm, v(-15.04, 8.55) * mm]});
            skFitSpline(sketch, "E3460", {"points": [v(-15.04, 8.55) * mm, v(-14.8, 8.5) * mm, v(-14.65, 8.25) * mm, v(-14.68, 7.98) * mm]});
            skFitSpline(sketch, "E3461", {"points": [v(-14.68, 7.98) * mm, v(-14.73, 7.65) * mm, v(-14.76, 7.32) * mm, v(-14.8, 6.98) * mm]});
            skFitSpline(sketch, "E3462", {"points": [v(-14.8, 6.98) * mm, v(-14.82, 6.83) * mm, v(-14.85, 6.67) * mm, v(-14.88, 6.48) * mm]});
            skFitSpline(sketch, "E3463", {"points": [v(-14.88, 6.48) * mm, v(-14.47, 6.7) * mm, v(-14.1, 6.9) * mm, v(-13.7, 7.1) * mm]});
            skFitSpline(sketch, "E3464", {"points": [v(-13.7, 7.1) * mm, v(-13.7, 7.19) * mm, v(-13.71, 7.27) * mm, v(-13.7, 7.34) * mm]});
            skFitSpline(sketch, "E3465", {"points": [v(-13.7, 7.34) * mm, v(-13.67, 7.55) * mm, v(-13.6, 7.73) * mm, v(-13.42, 7.85) * mm]});
            skFitSpline(sketch, "E3466", {"points": [v(-13.42, 7.85) * mm, v(-13.37, 7.88) * mm, v(-13.33, 7.91) * mm, v(-13.29, 7.95) * mm]});
            skFitSpline(sketch, "E3467", {"points": [v(-13.29, 7.95) * mm, v(-13.02, 8.23) * mm, v(-12.69, 8.3) * mm, v(-12.32, 8.21) * mm]});
            skFitSpline(sketch, "E3468", {"points": [v(-12.32, 8.21) * mm, v(-12.23, 8.2) * mm, v(-12.15, 8.16) * mm, v(-12.06, 8.15) * mm]});
            skFitSpline(sketch, "E3469", {"points": [v(-12.06, 8.15) * mm, v(-11.85, 8.11) * mm, v(-11.72, 7.99) * mm, v(-11.66, 7.79) * mm]});
            skFitSpline(sketch, "E3470", {"points": [v(-11.66, 7.79) * mm, v(-11.63, 7.71) * mm, v(-11.59, 7.65) * mm, v(-11.54, 7.59) * mm]});
            skFitSpline(sketch, "E3471", {"points": [v(-11.54, 7.59) * mm, v(-11.4, 7.43) * mm, v(-11.37, 7.27) * mm, v(-11.44, 7.08) * mm]});
            skFitSpline(sketch, "E3472", {"points": [v(-11.44, 7.08) * mm, v(-11.48, 6.96) * mm, v(-11.5, 6.85) * mm, v(-11.54, 6.73) * mm]});
            skFitSpline(sketch, "E3473", {"points": [v(-11.54, 6.73) * mm, v(-11.64, 6.44) * mm, v(-11.84, 6.25) * mm, v(-12.13, 6.14) * mm]});
            skFitSpline(sketch, "E3474", {"points": [v(-12.13, 6.14) * mm, v(-12.17, 6.12) * mm, v(-12.22, 6.12) * mm, v(-12.26, 6.1) * mm]});
            skFitSpline(sketch, "E3475", {"points": [v(-12.26, 6.1) * mm, v(-12.58, 5.93) * mm, v(-12.88, 5.96) * mm, v(-13.17, 6.17) * mm]});
            skFitSpline(sketch, "E3476", {"points": [v(-13.17, 6.17) * mm, v(-13.54, 5.94) * mm, v(-13.9, 5.7) * mm, v(-14.29, 5.46) * mm]});
            skFitSpline(sketch, "E3477", {"points": [v(-14.29, 5.46) * mm, v(-14.2, 5.43) * mm, v(-14.15, 5.41) * mm, v(-14.1, 5.39) * mm]});
            skFitSpline(sketch, "E3478", {"points": [v(-14.1, 5.39) * mm, v(-13.85, 5.29) * mm, v(-13.6, 5.19) * mm, v(-13.37, 5.09) * mm]});
            skFitSpline(sketch, "E3479", {"points": [v(-13.37, 5.09) * mm, v(-13.2, 5.02) * mm, v(-13.05, 4.95) * mm, v(-12.88, 4.88) * mm]});
            skFitSpline(sketch, "E3480", {"points": [v(-12.88, 4.88) * mm, v(-12.6, 4.77) * mm, v(-12.5, 4.5) * mm, v(-12.6, 4.23) * mm]});
            skFitSpline(sketch, "E3481", {"points": [v(-12.6, 4.23) * mm, v(-12.67, 4.03) * mm, v(-12.97, 3.82) * mm, v(-13.25, 3.96) * mm]});
            skFitSpline(sketch, "E3482", {"points": [v(-13.25, 3.96) * mm, v(-13.42, 4.04) * mm, v(-13.6, 4.12) * mm, v(-13.77, 4.2) * mm]});
            skFitSpline(sketch, "E3483", {"points": [v(-13.77, 4.2) * mm, v(-14.05, 4.31) * mm, v(-14.33, 4.43) * mm, v(-14.62, 4.53) * mm]});
            skFitSpline(sketch, "E3484", {"points": [v(-14.62, 4.53) * mm, v(-14.85, 4.6) * mm, v(-15.05, 4.7) * mm, v(-15.14, 4.96) * mm]});
            skFitSpline(sketch, "E3485", {"points": [v(-15.14, 4.96) * mm, v(-15.53, 4.72) * mm, v(-15.91, 4.5) * mm, v(-16.28, 4.25) * mm]});
            skFitSpline(sketch, "E3486", {"points": [v(-16.28, 4.25) * mm, v(-16.88, 3.87) * mm, v(-17.46, 3.48) * mm, v(-18.05, 3.1) * mm]});
            skFitSpline(sketch, "E3487", {"points": [v(-18.05, 3.1) * mm, v(-18.58, 2.78) * mm, v(-19.1, 2.47) * mm, v(-19.64, 2.16) * mm]});
            skFitSpline(sketch, "E3488", {"points": [v(-19.64, 2.16) * mm, v(-19.9, 2.01) * mm, v(-20.18, 1.88) * mm, v(-20.45, 1.74) * mm]});
            skFitSpline(sketch, "E3489", {"points": [v(-20.45, 1.74) * mm, v(-20.56, 1.68) * mm, v(-20.67, 1.62) * mm, v(-20.77, 1.52) * mm]});
            skFitSpline(sketch, "E3490", {"points": [v(-20.77, 1.52) * mm, v(-20.68, 1.54) * mm, v(-20.6, 1.56) * mm, v(-20.52, 1.58) * mm]});
            skFitSpline(sketch, "E3491", {"points": [v(-20.52, 1.58) * mm, v(-19.23, 1.98) * mm, v(-17.9, 2.27) * mm, v(-16.6, 2.59) * mm]});
            skFitSpline(sketch, "E3492", {"points": [v(-16.6, 2.59) * mm, v(-16.2, 2.68) * mm, v(-15.82, 2.77) * mm, v(-15.43, 2.87) * mm]});
            skFitSpline(sketch, "E3493", {"points": [v(-15.43, 2.87) * mm, v(-15.16, 2.95) * mm, v(-14.92, 2.9) * mm, v(-14.68, 2.75) * mm]});
            skFitSpline(sketch, "E3494", {"points": [v(-14.68, 2.75) * mm, v(-13.71, 2.15) * mm, v(-12.83, 1.44) * mm, v(-11.95, 0.73) * mm]});
            skFitSpline(sketch, "E3495", {"points": [v(-11.95, 0.73) * mm, v(-11.91, 0.7) * mm, v(-11.87, 0.67) * mm, v(-11.83, 0.63) * mm]});
            skFitSpline(sketch, "E3496", {"points": [v(-11.83, 0.63) * mm, v(-11.5, 0.92) * mm, v(-11.17, 1.2) * mm, v(-10.85, 1.49) * mm]});
            skFitSpline(sketch, "E3497", {"points": [v(-10.85, 1.49) * mm, v(-10.17, 2.1) * mm, v(-9.49, 2.7) * mm, v(-8.81, 3.31) * mm]});
            skFitSpline(sketch, "E3498", {"points": [v(-8.81, 3.31) * mm, v(-8.54, 3.56) * mm, v(-8.29, 3.82) * mm, v(-8.03, 4.08) * mm]});
            skFitSpline(sketch, "E3499", {"points": [v(-8.03, 4.08) * mm, v(-7.84, 4.27) * mm, v(-7.55, 4.3) * mm, v(-7.35, 4.15) * mm]});
            skFitSpline(sketch, "E3500", {"points": [v(-7.35, 4.15) * mm, v(-7.15, 4) * mm, v(-7.1, 3.7) * mm, v(-7.26, 3.49) * mm]});
            skFitSpline(sketch, "E3501", {"points": [v(-7.26, 3.49) * mm, v(-7.38, 3.33) * mm, v(-7.52, 3.18) * mm, v(-7.67, 3.05) * mm]});
            skFitSpline(sketch, "E3502", {"points": [v(-7.67, 3.05) * mm, v(-8.45, 2.34) * mm, v(-9.23, 1.63) * mm, v(-10.01, 0.93) * mm]});
            skFitSpline(sketch, "E3503", {"points": [v(-10.01, 0.93) * mm, v(-10.04, 0.9) * mm, v(-10.06, 0.89) * mm, v(-10.07, 0.83) * mm]});
            skFitSpline(sketch, "E3504", {"points": [v(-10.07, 0.83) * mm, v(-10.02, 0.84) * mm, v(-9.96, 0.85) * mm, v(-9.91, 0.87) * mm]});
            skFitSpline(sketch, "E3505", {"points": [v(-9.91, 0.87) * mm, v(-9.3, 1.15) * mm, v(-8.65, 1.37) * mm, v(-8.07, 1.72) * mm]});
            skFitSpline(sketch, "E3506", {"points": [v(-8.07, 1.72) * mm, v(-7.86, 1.83) * mm, v(-7.54, 1.84) * mm, v(-7.37, 1.61) * mm]});
            skFitSpline(sketch, "E3507", {"points": [v(-7.37, 1.61) * mm, v(-7.18, 1.34) * mm, v(-7.32, 0.9) * mm, v(-7.65, 0.77) * mm]});
            skFitSpline(sketch, "E3508", {"points": [v(-7.65, 0.77) * mm, v(-8.11, 0.58) * mm, v(-8.57, 0.38) * mm, v(-9.03, 0.19) * mm]});
            skFitSpline(sketch, "E3509", {"points": [v(-9.03, 0.19) * mm, v(-9.17, 0.13) * mm, v(-9.3, 0.07) * mm, v(-9.46, 0) * mm]});
            skFitSpline(sketch, "E3510", {"points": [v(-9.46, 0) * mm, v(-9.14, -0.15) * mm, v(-8.86, -0.27) * mm, v(-8.58, -0.4) * mm]});
            skFitSpline(sketch, "E3511", {"points": [v(-8.58, -0.4) * mm, v(-8.4, -0.48) * mm, v(-8.21, -0.56) * mm, v(-8.03, -0.64) * mm]});
            skFitSpline(sketch, "E3512", {"points": [v(-8.03, -0.64) * mm, v(-7.94, -0.68) * mm, v(-7.84, -0.73) * mm, v(-7.74, -0.75) * mm]});
            skFitSpline(sketch, "E3513", {"points": [v(-7.74, -0.75) * mm, v(-7.49, -0.81) * mm, v(-7.35, -1) * mm, v(-7.3, -1.23) * mm]});
            skFitSpline(sketch, "E3514", {"points": [v(-7.3, -1.23) * mm, v(-7.25, -1.41) * mm, v(-7.3, -1.58) * mm, v(-7.46, -1.7) * mm]});
            skFitSpline(sketch, "E3515", {"points": [v(-7.46, -1.7) * mm, v(-7.6, -1.82) * mm, v(-7.77, -1.86) * mm, v(-7.95, -1.78) * mm]});
            skFitSpline(sketch, "E3516", {"points": [v(-7.95, -1.78) * mm, v(-8.12, -1.7) * mm, v(-8.27, -1.6) * mm, v(-8.44, -1.53) * mm]});
            skFitSpline(sketch, "E3517", {"points": [v(-8.44, -1.53) * mm, v(-8.93, -1.31) * mm, v(-9.42, -1.1) * mm, v(-9.9, -0.88) * mm]});
            skFitSpline(sketch, "E3518", {"points": [v(-9.9, -0.88) * mm, v(-9.96, -0.86) * mm, v(-10, -0.85) * mm, v(-10.08, -0.87) * mm]});
            skFitSpline(sketch, "E3519", {"points": [v(-10.08, -0.87) * mm, v(-9.94, -1) * mm, v(-9.8, -1.12) * mm, v(-9.67, -1.24) * mm]});
            skFitSpline(sketch, "E3520", {"points": [v(-9.67, -1.24) * mm, v(-8.97, -1.88) * mm, v(-8.27, -2.5) * mm, v(-7.57, -3.14) * mm]});
            skFitSpline(sketch, "E3521", {"points": [v(-7.57, -3.14) * mm, v(-7.45, -3.25) * mm, v(-7.35, -3.37) * mm, v(-7.26, -3.5) * mm]});
            skFitSpline(sketch, "E3522", {"points": [v(-7.26, -3.5) * mm, v(-7.1, -3.72) * mm, v(-7.15, -3.99) * mm, v(-7.34, -4.15) * mm]});
            skFitSpline(sketch, "E3523", {"points": [v(-7.34, -4.15) * mm, v(-7.53, -4.3) * mm, v(-7.83, -4.3) * mm, v(-8.01, -4.1) * mm]});
            skFitSpline(sketch, "E3524", {"points": [v(-8.01, -4.1) * mm, v(-8.76, -3.32) * mm, v(-9.6, -2.62) * mm, v(-10.4, -1.9) * mm]});
            skFitSpline(sketch, "E3525", {"points": [v(-10.4, -1.9) * mm, v(-10.87, -1.48) * mm, v(-11.34, -1.07) * mm, v(-11.82, -0.64) * mm]});
            skFitSpline(sketch, "E3526", {"points": [v(-11.82, -0.64) * mm, v(-11.87, -0.68) * mm, v(-11.92, -0.72) * mm, v(-11.97, -0.75) * mm]});
            skFitSpline(sketch, "E3527", {"points": [v(-11.97, -0.75) * mm, v(-12.68, -1.3) * mm, v(-13.38, -1.85) * mm, v(-14.1, -2.4) * mm]});
            skFitSpline(sketch, "E3528", {"points": [v(-14.1, -2.4) * mm, v(-14.32, -2.56) * mm, v(-14.57, -2.69) * mm, v(-14.81, -2.83) * mm]});
            skFitSpline(sketch, "E3529", {"points": [v(-14.81, -2.83) * mm, v(-15, -2.93) * mm, v(-15.19, -2.95) * mm, v(-15.4, -2.9) * mm]});
            skFitSpline(sketch, "E3530", {"points": [v(-15.4, -2.9) * mm, v(-16.37, -2.65) * mm, v(-17.36, -2.41) * mm, v(-18.34, -2.16) * mm]});
            skFitSpline(sketch, "E3531", {"points": [v(-18.34, -2.16) * mm, v(-19.12, -1.96) * mm, v(-19.9, -1.75) * mm, v(-20.68, -1.55) * mm]});
            skFitSpline(sketch, "E3532", {"points": [v(-20.68, -1.55) * mm, v(-20.72, -1.54) * mm, v(-20.75, -1.53) * mm, v(-20.8, -1.55) * mm]});
            skFitSpline(sketch, "E3533", {"points": [v(-20.8, -1.55) * mm, v(-20.56, -1.68) * mm, v(-20.31, -1.8) * mm, v(-20.08, -1.94) * mm]});
            skFitSpline(sketch, "E3534", {"points": [v(-20.08, -1.94) * mm, v(-19.34, -2.37) * mm, v(-18.6, -2.8) * mm, v(-17.87, -3.24) * mm]});
            skFitSpline(sketch, "E3535", {"points": [v(-17.87, -3.24) * mm, v(-17.14, -3.68) * mm, v(-16.42, -4.15) * mm, v(-15.7, -4.6) * mm]});
            skFitSpline(sketch, "E3536", {"points": [v(-15.7, -4.6) * mm, v(-15.52, -4.72) * mm, v(-15.34, -4.84) * mm, v(-15.14, -4.97) * mm]});
            skFitSpline(sketch, "E3537", {"points": [v(-15.14, -4.97) * mm, v(-15.04, -4.69) * mm, v(-14.81, -4.6) * mm, v(-14.56, -4.52) * mm]});
            skFitSpline(sketch, "E3538", {"points": [v(-14.56, -4.52) * mm, v(-14.17, -4.37) * mm, v(-13.78, -4.2) * mm, v(-13.4, -4.03) * mm]});
            skFitSpline(sketch, "E3539", {"points": [v(-13.4, -4.03) * mm, v(-13.3, -4) * mm, v(-13.18, -3.95) * mm, v(-13.07, -3.94) * mm]});
            skFitSpline(sketch, "E3540", {"points": [v(-13.07, -3.94) * mm, v(-12.81, -3.93) * mm, v(-12.63, -4.07) * mm, v(-12.57, -4.33) * mm]});
            skFitSpline(sketch, "E3541", {"points": [v(-12.57, -4.33) * mm, v(-12.52, -4.57) * mm, v(-12.64, -4.79) * mm, v(-12.88, -4.89) * mm]});
            skFitSpline(sketch, "E3542", {"points": [v(-12.88, -4.89) * mm, v(-13.33, -5.07) * mm, v(-13.78, -5.26) * mm, v(-14.23, -5.44) * mm]});
            skFitSpline(sketch, "E3543", {"points": [v(-14.23, -5.44) * mm, v(-14.24, -5.45) * mm, v(-14.25, -5.46) * mm, v(-14.27, -5.48) * mm]});
            skFitSpline(sketch, "E3544", {"points": [v(-14.27, -5.48) * mm, v(-13.9, -5.71) * mm, v(-13.54, -5.94) * mm, v(-13.2, -6.16) * mm]});
            skFitSpline(sketch, "E3545", {"points": [v(-13.2, -6.16) * mm, v(-13.03, -6.1) * mm, v(-12.88, -6.01) * mm, v(-12.73, -6.01) * mm]});
            skFitSpline(sketch, "E3546", {"points": [v(-12.73, -6.01) * mm, v(-12.28, -6) * mm, v(-11.62, -6.26) * mm, v(-11.5, -6.85) * mm]});
            skFitSpline(sketch, "E3547", {"points": [v(-11.5, -6.85) * mm, v(-11.49, -6.94) * mm, v(-11.46, -7.02) * mm, v(-11.43, -7.1) * mm]});
            skFitSpline(sketch, "E3548", {"points": [v(-11.43, -7.1) * mm, v(-11.38, -7.28) * mm, v(-11.4, -7.43) * mm, v(-11.52, -7.57) * mm]});
            skFitSpline(sketch, "E3549", {"points": [v(-11.52, -7.57) * mm, v(-11.58, -7.65) * mm, v(-11.63, -7.74) * mm, v(-11.67, -7.84) * mm]});
            skFitSpline(sketch, "E3550", {"points": [v(-11.67, -7.84) * mm, v(-11.74, -8) * mm, v(-11.84, -8.1) * mm, v(-12, -8.15) * mm]});
            skFitSpline(sketch, "E3551", {"points": [v(-12, -8.15) * mm, v(-12.14, -8.18) * mm, v(-12.27, -8.2) * mm, v(-12.4, -8.24) * mm]});
            skFitSpline(sketch, "E3552", {"points": [v(-12.4, -8.24) * mm, v(-12.6, -8.28) * mm, v(-12.78, -8.27) * mm, v(-12.94, -8.18) * mm]});
            skFitSpline(sketch, "E3553", {"points": [v(-12.94, -8.18) * mm, v(-13.26, -8.01) * mm, v(-13.58, -7.83) * mm, v(-13.68, -7.45) * mm]});
            skFitSpline(sketch, "E3554", {"points": [v(-13.68, -7.45) * mm, v(-13.71, -7.35) * mm, v(-13.7, -7.23) * mm, v(-13.72, -7.1) * mm]});
            skFitSpline(sketch, "E3555", {"points": [v(-13.72, -7.1) * mm, v(-13.78, -7.08) * mm, v(-13.84, -7.04) * mm, v(-13.9, -7) * mm]});
            skFitSpline(sketch, "E3556", {"points": [v(-13.9, -7) * mm, v(-14.22, -6.84) * mm, v(-14.53, -6.68) * mm, v(-14.89, -6.5) * mm]});
            skFitSpline(sketch, "E3557", {"points": [v(-14.89, -6.5) * mm, v(-14.85, -6.67) * mm, v(-14.82, -6.81) * mm, v(-14.8, -6.96) * mm]});
            skFitSpline(sketch, "E3558", {"points": [v(-14.8, -6.96) * mm, v(-14.77, -7.24) * mm, v(-14.74, -7.51) * mm, v(-14.72, -7.8) * mm]});
            skFitSpline(sketch, "E3559", {"points": [v(-14.72, -7.8) * mm, v(-14.7, -7.85) * mm, v(-14.7, -7.92) * mm, v(-14.69, -7.98) * mm]});
            skFitSpline(sketch, "E3560", {"points": [v(-14.69, -7.98) * mm, v(-14.64, -8.26) * mm, v(-14.8, -8.51) * mm, v(-15.05, -8.56) * mm]});
            skFitSpline(sketch, "E3561", {"points": [v(-15.05, -8.56) * mm, v(-15.35, -8.62) * mm, v(-15.6, -8.46) * mm, v(-15.66, -8.16) * mm]});
            skFitSpline(sketch, "E3562", {"points": [v(-15.66, -8.16) * mm, v(-15.69, -8) * mm, v(-15.69, -7.83) * mm, v(-15.7, -7.66) * mm]});
            skFitSpline(sketch, "E3563", {"points": [v(-15.7, -7.66) * mm, v(-15.75, -7.35) * mm, v(-15.79, -7.03) * mm, v(-15.85, -6.72) * mm]});
            skFitSpline(sketch, "E3564", {"points": [v(-15.85, -6.72) * mm, v(-15.9, -6.47) * mm, v(-15.95, -6.23) * mm, v(-15.74, -6.02) * mm]});
            skFitSpline(sketch, "E3565", {"points": [v(-15.74, -6.02) * mm, v(-17.67, -4.93) * mm, v(-19.7, -4.07) * mm, v(-21.5, -2.8) * mm]});
            skLineSegment(sketch, "E3566", {"start": v(-21.5, -2.8) * mm, "end": v(-21.54, -2.85) * mm});
            skFitSpline(sketch, "E3567", {"points": [v(-21.54, -2.85) * mm, v(-21.48, -2.91) * mm, v(-21.42, -2.98) * mm, v(-21.36, -3.04) * mm]});
            skFitSpline(sketch, "E3568", {"points": [v(-21.36, -3.04) * mm, v(-20.39, -3.93) * mm, v(-19.51, -4.9) * mm, v(-18.6, -5.85) * mm]});
            skFitSpline(sketch, "E3569", {"points": [v(-18.6, -5.85) * mm, v(-18.29, -6.18) * mm, v(-17.98, -6.51) * mm, v(-17.66, -6.84) * mm]});
            skFitSpline(sketch, "E3570", {"points": [v(-17.66, -6.84) * mm, v(-17.5, -7) * mm, v(-17.43, -7.18) * mm, v(-17.44, -7.4) * mm]});
            skFitSpline(sketch, "E3571", {"points": [v(-17.44, -7.4) * mm, v(-17.44, -7.96) * mm, v(-17.47, -8.53) * mm, v(-17.55, -9.1) * mm]});
            skFitSpline(sketch, "E3572", {"points": [v(-17.55, -9.1) * mm, v(-17.62, -9.55) * mm, v(-17.67, -10) * mm, v(-17.73, -10.46) * mm]});
            skFitSpline(sketch, "E3573", {"points": [v(-17.73, -10.46) * mm, v(-17.76, -10.65) * mm, v(-17.8, -10.84) * mm, v(-17.84, -11.04) * mm]});
            skFitSpline(sketch, "E3574", {"points": [v(-17.84, -11.04) * mm, v(-17.76, -11.06) * mm, v(-17.7, -11.09) * mm, v(-17.65, -11.1) * mm]});
            skFitSpline(sketch, "E3575", {"points": [v(-17.65, -11.1) * mm, v(-16.39, -11.52) * mm, v(-15.13, -11.94) * mm, v(-13.87, -12.35) * mm]});
            skFitSpline(sketch, "E3576", {"points": [v(-13.87, -12.35) * mm, v(-13.56, -12.45) * mm, v(-13.24, -12.53) * mm, v(-12.93, -12.6) * mm]});
            skFitSpline(sketch, "E3577", {"points": [v(-12.93, -12.6) * mm, v(-12.68, -12.68) * mm, v(-12.51, -12.92) * mm, v(-12.55, -13.17) * mm]});
            skFitSpline(sketch, "E3578", {"points": [v(-12.55, -13.17) * mm, v(-12.6, -13.43) * mm, v(-12.81, -13.58) * mm, v(-13.1, -13.57) * mm]});
            skFitSpline(sketch, "E3579", {"points": [v(-13.1, -13.57) * mm, v(-13.46, -13.55) * mm, v(-13.79, -13.4) * mm, v(-14.13, -13.3) * mm]});
            skFitSpline(sketch, "E3580", {"points": [v(-14.13, -13.3) * mm, v(-14.92, -13.05) * mm, v(-15.7, -12.78) * mm, v(-16.5, -12.52) * mm]});
            skFitSpline(sketch, "E3581", {"points": [v(-16.5, -12.52) * mm, v(-16.58, -12.5) * mm, v(-16.67, -12.47) * mm, v(-16.78, -12.48) * mm]});
            skFitSpline(sketch, "E3582", {"points": [v(-16.78, -12.48) * mm, v(-16.73, -12.53) * mm, v(-16.68, -12.58) * mm, v(-16.62, -12.62) * mm]});
            skFitSpline(sketch, "E3583", {"points": [v(-16.62, -12.62) * mm, v(-16.08, -13) * mm, v(-15.58, -13.43) * mm, v(-15, -13.77) * mm]});
            skFitSpline(sketch, "E3584", {"points": [v(-15, -13.77) * mm, v(-14.7, -13.94) * mm, v(-14.63, -14.26) * mm, v(-14.81, -14.5) * mm]});
            skFitSpline(sketch, "E3585", {"points": [v(-14.81, -14.5) * mm, v(-15, -14.75) * mm, v(-15.4, -14.77) * mm, v(-15.65, -14.57) * mm]});
            skFitSpline(sketch, "E3586", {"points": [v(-15.65, -14.57) * mm, v(-16.13, -14.2) * mm, v(-16.63, -13.83) * mm, v(-17.12, -13.46) * mm]});
            skFitSpline(sketch, "E3587", {"points": [v(-17.12, -13.46) * mm, v(-17.14, -13.46) * mm, v(-17.15, -13.46) * mm, v(-17.2, -13.45) * mm]});
            skFitSpline(sketch, "E3588", {"points": [v(-17.2, -13.45) * mm, v(-17.19, -13.52) * mm, v(-17.19, -13.59) * mm, v(-17.18, -13.65) * mm]});
            skFitSpline(sketch, "E3589", {"points": [v(-17.18, -13.65) * mm, v(-17.14, -14.08) * mm, v(-17.1, -14.51) * mm, v(-17.05, -14.94) * mm]});
            skFitSpline(sketch, "E3590", {"points": [v(-17.05, -14.94) * mm, v(-17.04, -15.06) * mm, v(-17, -15.19) * mm, v(-16.98, -15.31) * mm]});
            skFitSpline(sketch, "E3591", {"points": [v(-16.98, -15.31) * mm, v(-16.9, -15.62) * mm, v(-17.12, -15.97) * mm, v(-17.43, -16.02) * mm]});
            skFitSpline(sketch, "E3592", {"points": [v(-17.43, -16.02) * mm, v(-17.71, -16.06) * mm, v(-17.97, -15.87) * mm, v(-17.97, -15.58) * mm]});
            skFitSpline(sketch, "E3593", {"points": [v(-17.97, -15.58) * mm, v(-17.99, -14.9) * mm, v(-18.1, -14.23) * mm, v(-18.17, -13.56) * mm]});
            skFitSpline(sketch, "E3594", {"points": [v(-18.17, -13.56) * mm, v(-18.18, -13.47) * mm, v(-18.2, -13.37) * mm, v(-18.26, -13.28) * mm]});
            skFitSpline(sketch, "E3595", {"points": [v(-18.26, -13.28) * mm, v(-18.32, -13.56) * mm, v(-18.38, -13.84) * mm, v(-18.44, -14.11) * mm]});
            skFitSpline(sketch, "E3596", {"points": [v(-18.44, -14.11) * mm, v(-18.62, -14.96) * mm, v(-18.8, -15.8) * mm, v(-18.98, -16.64) * mm]});
            skFitSpline(sketch, "E3597", {"points": [v(-18.98, -16.64) * mm, v(-19.01, -16.79) * mm, v(-19.06, -16.93) * mm, v(-19.13, -17.07) * mm]});
            skFitSpline(sketch, "E3598", {"points": [v(-19.13, -17.07) * mm, v(-19.25, -17.31) * mm, v(-19.5, -17.4) * mm, v(-19.73, -17.32) * mm]});
            skFitSpline(sketch, "E3599", {"points": [v(-19.73, -17.32) * mm, v(-19.97, -17.23) * mm, v(-20.1, -16.97) * mm, v(-20.03, -16.7) * mm]});
            skFitSpline(sketch, "E3600", {"points": [v(-20.03, -16.7) * mm, v(-19.8, -15.94) * mm, v(-19.64, -15.15) * mm, v(-19.48, -14.36) * mm]});
            skFitSpline(sketch, "E3601", {"points": [v(-19.48, -14.36) * mm, v(-19.3, -13.5) * mm, v(-19.13, -12.65) * mm, v(-18.96, -11.8) * mm]});
            skFitSpline(sketch, "E3602", {"points": [v(-18.96, -11.8) * mm, v(-18.95, -11.76) * mm, v(-18.95, -11.72) * mm, v(-18.94, -11.68) * mm]});
            skFitSpline(sketch, "E3603", {"points": [v(-18.94, -11.68) * mm, v(-18.98, -11.66) * mm, v(-19, -11.65) * mm, v(-19.03, -11.64) * mm]});
            skFitSpline(sketch, "E3604", {"points": [v(-19.03, -11.64) * mm, v(-19.87, -11.3) * mm, v(-20.7, -10.96) * mm, v(-21.54, -10.6) * mm]});
            skFitSpline(sketch, "E3605", {"points": [v(-21.54, -10.6) * mm, v(-21.81, -10.5) * mm, v(-22.08, -10.33) * mm, v(-22.34, -10.18) * mm]});
            skFitSpline(sketch, "E3606", {"points": [v(-22.34, -10.18) * mm, v(-22.5, -10.08) * mm, v(-22.6, -9.93) * mm, v(-22.66, -9.75) * mm]});
            skFitSpline(sketch, "E3607", {"points": [v(-22.66, -9.75) * mm, v(-23.09, -8.27) * mm, v(-23.52, -6.79) * mm, v(-23.94, -5.3) * mm]});
            skFitSpline(sketch, "E3608", {"points": [v(-23.94, -5.3) * mm, v(-24.03, -5) * mm, v(-24.09, -4.69) * mm, v(-24.2, -4.38) * mm]});
            skFitSpline(sketch, "E3609", {"points": [v(-24.2, -4.38) * mm, v(-24.21, -4.47) * mm, v(-24.22, -4.57) * mm, v(-24.21, -4.66) * mm]});
            skFitSpline(sketch, "E3610", {"points": [v(-24.21, -4.66) * mm, v(-24.2, -5.19) * mm, v(-24.17, -5.72) * mm, v(-24.17, -6.24) * mm]});
            skFitSpline(sketch, "E3611", {"points": [v(-24.17, -6.24) * mm, v(-24.18, -7) * mm, v(-24.23, -7.76) * mm, v(-24.25, -8.51) * mm]});
            skFitSpline(sketch, "E3612", {"points": [v(-24.25, -8.51) * mm, v(-24.27, -9.04) * mm, v(-24.3, -9.57) * mm, v(-24.31, -10.1) * mm]});
            skFitSpline(sketch, "E3613", {"points": [v(-24.31, -10.1) * mm, v(-24.32, -10.3) * mm, v(-24.33, -10.49) * mm, v(-24.34, -10.69) * mm]});
            skFitSpline(sketch, "E3614", {"points": [v(-24.34, -10.69) * mm, v(-24.35, -10.77) * mm, v(-24.34, -10.86) * mm, v(-24.34, -10.98) * mm]});
            skFitSpline(sketch, "E3615", {"points": [v(-24.34, -10.98) * mm, v(-24.01, -10.9) * mm, v(-23.83, -11.1) * mm, v(-23.62, -11.29) * mm]});
            skFitSpline(sketch, "E3616", {"points": [v(-23.62, -11.29) * mm, v(-23.34, -11.52) * mm, v(-23.04, -11.73) * mm, v(-22.74, -11.96) * mm]});
            skFitSpline(sketch, "E3617", {"points": [v(-22.74, -11.96) * mm, v(-22.68, -12) * mm, v(-22.6, -12.04) * mm, v(-22.55, -12.1) * mm]});
            skFitSpline(sketch, "E3618", {"points": [v(-22.55, -12.1) * mm, v(-22.3, -12.28) * mm, v(-22.26, -12.58) * mm, v(-22.44, -12.81) * mm]});
            skFitSpline(sketch, "E3619", {"points": [v(-22.44, -12.81) * mm, v(-22.62, -13.04) * mm, v(-22.92, -13.06) * mm, v(-23.16, -12.87) * mm]});
            skFitSpline(sketch, "E3620", {"points": [v(-23.16, -12.87) * mm, v(-23.55, -12.58) * mm, v(-23.94, -12.29) * mm, v(-24.35, -11.98) * mm]});
            skFitSpline(sketch, "E3621", {"points": [v(-24.35, -11.98) * mm, v(-24.37, -12.42) * mm, v(-24.4, -12.85) * mm, v(-24.4, -13.25) * mm]});
            skFitSpline(sketch, "E3622", {"points": [v(-24.4, -13.25) * mm, v(-24.27, -13.36) * mm, v(-24.15, -13.44) * mm, v(-24.06, -13.55) * mm]});
            skFitSpline(sketch, "E3623", {"points": [v(-24.06, -13.55) * mm, v(-23.99, -13.64) * mm, v(-23.95, -13.76) * mm, v(-23.92, -13.87) * mm]});
            skFitSpline(sketch, "E3624", {"points": [v(-23.92, -13.87) * mm, v(-23.89, -13.96) * mm, v(-23.88, -14.06) * mm, v(-23.86, -14.15) * mm]});
            skFitSpline(sketch, "E3625", {"points": [v(-23.86, -14.15) * mm, v(-23.8, -14.45) * mm, v(-23.86, -14.72) * mm, v(-24.06, -14.95) * mm]});
            skFitSpline(sketch, "E3626", {"points": [v(-24.06, -14.95) * mm, v(-24.16, -15.07) * mm, v(-24.26, -15.18) * mm, v(-24.37, -15.29) * mm]});
            skFitSpline(sketch, "E3627", {"points": [v(-24.37, -15.29) * mm, v(-24.5, -15.4) * mm, v(-24.63, -15.45) * mm, v(-24.8, -15.41) * mm]});
            skFitSpline(sketch, "E3628", {"points": [v(-24.8, -15.41) * mm, v(-24.89, -15.4) * mm, v(-24.98, -15.39) * mm, v(-25.06, -15.4) * mm]});
            skFitSpline(sketch, "E3629", {"points": [v(-25.06, -15.4) * mm, v(-25.24, -15.45) * mm, v(-25.4, -15.4) * mm, v(-25.52, -15.28) * mm]});
            skFitSpline(sketch, "E3630", {"points": [v(-25.52, -15.28) * mm, v(-25.63, -15.18) * mm, v(-25.72, -15.07) * mm, v(-25.82, -14.96) * mm]});
            skFitSpline(sketch, "E3631", {"points": [v(-25.82, -14.96) * mm, v(-25.97, -14.8) * mm, v(-26.05, -14.6) * mm, v(-26.03, -14.37) * mm]});
            skFitSpline(sketch, "E3632", {"points": [v(-26.03, -14.37) * mm, v(-26.02, -14.16) * mm, v(-26, -13.96) * mm, v(-25.94, -13.76) * mm]});
            skFitSpline(sketch, "E3633", {"points": [v(-25.94, -13.76) * mm, v(-25.88, -13.52) * mm, v(-25.7, -13.4) * mm, v(-25.48, -13.29) * mm]});
            skSolve(sketch);
        }
        {
            var Q0;
            Q0=makeQuery(id+"F0.imprint","IMPRINT",FACE,{"disambiguationData":[TD([[makeQuery(id+"F0.imprint","IMPRINT",EDGE,{"derivedFrom":sQuery(id+"F0.wireOp",EDGE,"E1734")}),-1.0]])]});
            var Q1;
            Q1=makeQuery(id+"F0.imprint","IMPRINT",FACE,{"disambiguationData":[TD([[makeQuery(id+"F0.imprint","IMPRINT",EDGE,{"derivedFrom":sQuery(id+"F0.wireOp",EDGE,"E2495")}),-1.0]])]});
            var Q2;
            Q2=makeQuery(id+"F0.imprint","IMPRINT",FACE,{"disambiguationData":[TD([[makeQuery(id+"F0.imprint","IMPRINT",EDGE,{"derivedFrom":sQuery(id+"F0.wireOp",EDGE,"E3054")}),-1.0]])]});
            var Q3;
            Q3=makeQuery(id+"F0.imprint","IMPRINT",FACE,{"disambiguationData":[TD([[makeQuery(id+"F0.imprint","IMPRINT",EDGE,{"derivedFrom":sQuery(id+"F0.wireOp",EDGE,"E0")}),-1.0]])]});
            var Q4;
            Q4=makeQuery(id+"F0.imprint","IMPRINT",FACE,{"disambiguationData":[TD([[makeQuery(id+"F0.imprint","IMPRINT",EDGE,{"derivedFrom":sQuery(id+"F0.wireOp",EDGE,"E1367")}),-1.0]])]});
            var Q5;
            Q5=makeQuery(id+"F0.imprint","IMPRINT",FACE,{"disambiguationData":[TD([[makeQuery(id+"F0.imprint","IMPRINT",EDGE,{"derivedFrom":sQuery(id+"F0.wireOp",EDGE,"E718")}),-1.0]])]});
            extrude(context, id + "F1", {"entities" : qUnion([Q0, Q1, Q2, Q3, Q4, Q5]), "depth" : 0.8 * mm});
        }
    });
